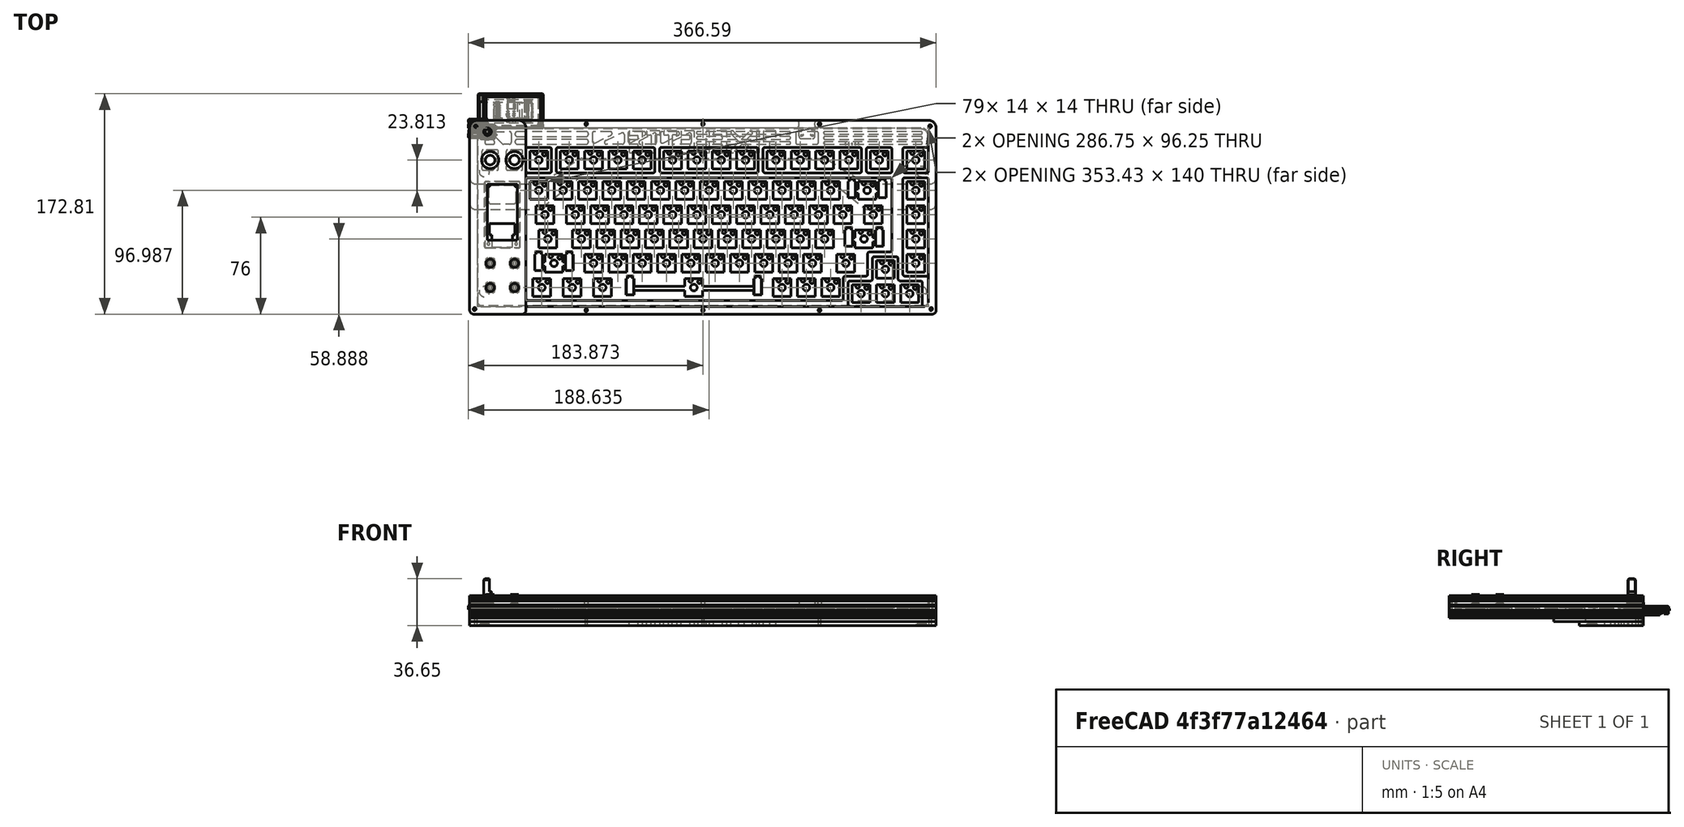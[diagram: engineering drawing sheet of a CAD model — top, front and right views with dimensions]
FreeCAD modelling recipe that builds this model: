
FCSTD DOCUMENT  (FreeCAD 0.20R29177 +426 (Git))
Label: Case design
License: All rights reserved
LicenseURL: http://en.wikipedia.org/wiki/All_rights_reserved
objects: App::Part×101, Part::Feature×100, Sketcher::SketchObject×84, PartDesign::Pocket×64, PartDesign::Pad×17, PartDesign::Body×17, TechDraw::DrawViewPart×13, TechDraw::DrawSVGTemplate×6, TechDraw::DrawPage×6, TechDraw::DrawViewDimension×4, App::DocumentObjectGroup×2, Spreadsheet::Sheet×1, PartDesign::Fillet×1
note: 365 computed .brp shape members not serialized (recipe doc carries the construction recipe); baked Part::Feature solids carry a one-line shape summary decoded from their .brp

FEATURE [Sketcher::SketchObject] Sketch
  AttachmentOffset = pos=(0,0,4.1) rot=(0,0,1;0rad)
  FullyConstrained = true
  MapMode = 5
  Placement = pos=(0,0,4.1) rot=(0,0,1;0rad)
  Support = -> [XY_Plane097]
  expr: .AttachmentOffset.Base.z = 4.1
  expr: Constraints[10] = Spreadsheet.switch_hole
  expr: Constraints[11] = Spreadsheet.PCB_width - Spreadsheet.u * 6
  expr: Constraints[12] = Spreadsheet.u * 2.5
  expr: Constraints[139] = Spreadsheet.switch_hole
  expr: Constraints[140] = Spreadsheet.switch_hole
  expr: Constraints[141] = Spreadsheet.switch_hole
  expr: Constraints[142] = Spreadsheet.switch_hole
  expr: Constraints[143] = Spreadsheet.switch_hole
  expr: Constraints[144] = Spreadsheet.switch_hole
  expr: Constraints[145] = Spreadsheet.switch_hole
  expr: Constraints[146] = Spreadsheet.switch_hole
  expr: Constraints[147] = Spreadsheet.switch_hole
  expr: Constraints[148] = Spreadsheet.switch_hole
  expr: Constraints[149] = Spreadsheet.switch_hole
  expr: Constraints[150] = Spreadsheet.switch_hole
  expr: Constraints[151] = Spreadsheet.switch_hole
  expr: Constraints[152] = Spreadsheet.switch_hole
  expr: Constraints[153] = Spreadsheet.switch_hole
  expr: Constraints[154] = Spreadsheet.switch_hole
  expr: Constraints[155] = Spreadsheet.switch_hole
  expr: Constraints[156] = Spreadsheet.switch_hole
  expr: Constraints[157] = Spreadsheet.switch_hole
  expr: Constraints[158] = Spreadsheet.switch_hole
  expr: Constraints[159] = Spreadsheet.switch_hole
  expr: Constraints[160] = Spreadsheet.switch_hole
  expr: Constraints[161] = Spreadsheet.switch_hole
  expr: Constraints[162] = Spreadsheet.switch_hole
  expr: Constraints[163] = Spreadsheet.switch_hole
  expr: Constraints[164] = Spreadsheet.switch_hole
  expr: Constraints[165] = Spreadsheet.switch_hole
  expr: Constraints[166] = Spreadsheet.switch_hole
  expr: Constraints[167] = Spreadsheet.u * 1.25
  expr: Constraints[182] = Spreadsheet.u
  expr: Constraints[183] = Spreadsheet.u
  expr: Constraints[184] = Spreadsheet.u
  expr: Constraints[185] = Spreadsheet.u
  expr: Constraints[186] = Spreadsheet.u
  expr: Constraints[187] = Spreadsheet.u
  expr: Constraints[188] = Spreadsheet.u
  expr: Constraints[189] = Spreadsheet.u
  expr: Constraints[190] = Spreadsheet.u
  expr: Constraints[191] = Spreadsheet.u * 1.25
  expr: Constraints[192] = Spreadsheet.u * 1.25
  expr: Constraints[193] = Spreadsheet.u * 1.25
  expr: Constraints[194] = Spreadsheet.u * 1.5
  expr: Constraints[9] = Spreadsheet.switch_hole
  sketch-geometry (75):
    g0: LineSegment StartX=40.625 StartY=-17.7 StartZ=0 EndX=40.625 EndY=-31.7 EndZ=0
    g1: LineSegment StartX=40.625 StartY=-31.7 StartZ=0 EndX=54.625 EndY=-31.7 EndZ=0
    g2: LineSegment StartX=54.625 StartY=-31.7 StartZ=0 EndX=54.625 EndY=-17.7 EndZ=0
    g3: LineSegment StartX=54.625 StartY=-17.7 StartZ=0 EndX=40.625 EndY=-17.7 EndZ=0
    g4: GeomPoint X=47.625 Y=-24.7 Z=0
    g5: LineSegment StartX=64.4375 StartY=-17.7 StartZ=0 EndX=64.4375 EndY=-31.7 EndZ=0
    g6: LineSegment StartX=64.4375 StartY=-31.7 StartZ=0 EndX=78.4375 EndY=-31.7 EndZ=0
    g7: LineSegment StartX=78.4375 StartY=-31.7 StartZ=0 EndX=78.4375 EndY=-17.7 EndZ=0
    g8: LineSegment StartX=78.4375 StartY=-17.7 StartZ=0 EndX=64.4375 EndY=-17.7 EndZ=0
    g9: GeomPoint X=71.4375 Y=-24.7 Z=0
    g10: LineSegment StartX=83.4875 StartY=-17.7 StartZ=0 EndX=83.4875 EndY=-31.7 EndZ=0
    g11: LineSegment StartX=83.4875 StartY=-31.7 StartZ=0 EndX=97.4875 EndY=-31.7 EndZ=0
    g12: LineSegment StartX=97.4875 StartY=-31.7 StartZ=0 EndX=97.4875 EndY=-17.7 EndZ=0
    g13: LineSegment StartX=97.4875 StartY=-17.7 StartZ=0 EndX=83.4875 EndY=-17.7 EndZ=0
    g14: GeomPoint X=90.4875 Y=-24.7 Z=0
    g15: LineSegment StartX=102.538 StartY=-17.7 StartZ=0 EndX=102.538 EndY=-31.7 EndZ=0
    g16: LineSegment StartX=102.538 StartY=-31.7 StartZ=0 EndX=116.538 EndY=-31.7 EndZ=0
    g17: LineSegment StartX=116.538 StartY=-31.7 StartZ=0 EndX=116.538 EndY=-17.7 EndZ=0
    g18: LineSegment StartX=116.538 StartY=-17.7 StartZ=0 EndX=102.538 EndY=-17.7 EndZ=0
    g19: GeomPoint X=109.538 Y=-24.7 Z=0
    g20: LineSegment StartX=121.588 StartY=-17.7 StartZ=0 EndX=121.588 EndY=-31.7 EndZ=0
    g21: LineSegment StartX=121.588 StartY=-31.7 StartZ=0 EndX=135.588 EndY=-31.7 EndZ=0
    g22: LineSegment StartX=135.588 StartY=-31.7 StartZ=0 EndX=135.588 EndY=-17.7 EndZ=0
    g23: LineSegment StartX=135.588 StartY=-17.7 StartZ=0 EndX=121.588 EndY=-17.7 EndZ=0
    g24: GeomPoint X=128.588 Y=-24.7 Z=0
    g25: LineSegment StartX=145.4 StartY=-17.7 StartZ=0 EndX=145.4 EndY=-31.7 EndZ=0
    g26: LineSegment StartX=145.4 StartY=-31.7 StartZ=0 EndX=159.4 EndY=-31.7 EndZ=0
    g27: LineSegment StartX=159.4 StartY=-31.7 StartZ=0 EndX=159.4 EndY=-17.7 EndZ=0
    g28: LineSegment StartX=159.4 StartY=-17.7 StartZ=0 EndX=145.4 EndY=-17.7 EndZ=0
    g29: GeomPoint X=152.4 Y=-24.7 Z=0
    g30: LineSegment StartX=164.45 StartY=-17.7 StartZ=0 EndX=164.45 EndY=-31.7 EndZ=0
    g31: LineSegment StartX=164.45 StartY=-31.7 StartZ=0 EndX=178.45 EndY=-31.7 EndZ=0
    g32: LineSegment StartX=178.45 StartY=-31.7 StartZ=0 EndX=178.45 EndY=-17.7 EndZ=0
    g33: LineSegment StartX=178.45 StartY=-17.7 StartZ=0 EndX=164.45 EndY=-17.7 EndZ=0
    g34: GeomPoint X=171.45 Y=-24.7 Z=0
    g35: LineSegment StartX=183.5 StartY=-17.7 StartZ=0 EndX=183.5 EndY=-31.7 EndZ=0
    g36: LineSegment StartX=183.5 StartY=-31.7 StartZ=0 EndX=197.5 EndY=-31.7 EndZ=0
    g37: LineSegment StartX=197.5 StartY=-31.7 StartZ=0 EndX=197.5 EndY=-17.7 EndZ=0
    g38: LineSegment StartX=197.5 StartY=-17.7 StartZ=0 EndX=183.5 EndY=-17.7 EndZ=0
    g39: GeomPoint X=190.5 Y=-24.7 Z=0
    g40: LineSegment StartX=202.55 StartY=-17.7 StartZ=0 EndX=202.55 EndY=-31.7 EndZ=0
    g41: LineSegment StartX=202.55 StartY=-31.7 StartZ=0 EndX=216.55 EndY=-31.7 EndZ=0
    g42: LineSegment StartX=216.55 StartY=-31.7 StartZ=0 EndX=216.55 EndY=-17.7 EndZ=0
    g43: LineSegment StartX=216.55 StartY=-17.7 StartZ=0 EndX=202.55 EndY=-17.7 EndZ=0
    g44: GeomPoint X=209.55 Y=-24.7 Z=0
    g45: LineSegment StartX=226.362 StartY=-17.7 StartZ=0 EndX=226.362 EndY=-31.7 EndZ=0
    g46: LineSegment StartX=226.362 StartY=-31.7 StartZ=0 EndX=240.362 EndY=-31.7 EndZ=0
    g47: LineSegment StartX=240.362 StartY=-31.7 StartZ=0 EndX=240.362 EndY=-17.7 EndZ=0
    g48: LineSegment StartX=240.362 StartY=-17.7 StartZ=0 EndX=226.362 EndY=-17.7 EndZ=0
    g49: GeomPoint X=233.363 Y=-24.7 Z=0
    g50: LineSegment StartX=245.412 StartY=-17.7 StartZ=0 EndX=245.412 EndY=-31.7 EndZ=0
    g51: LineSegment StartX=245.412 StartY=-31.7 StartZ=0 EndX=259.413 EndY=-31.7 EndZ=0
    g52: LineSegment StartX=259.413 StartY=-31.7 StartZ=0 EndX=259.413 EndY=-17.7 EndZ=0
    g53: LineSegment StartX=259.413 StartY=-17.7 StartZ=0 EndX=245.412 EndY=-17.7 EndZ=0
    g54: GeomPoint X=252.412 Y=-24.7 Z=0
    g55: LineSegment StartX=264.463 StartY=-17.7 StartZ=0 EndX=264.463 EndY=-31.7 EndZ=0
    g56: LineSegment StartX=264.463 StartY=-31.7 StartZ=0 EndX=278.463 EndY=-31.7 EndZ=0
    g57: LineSegment StartX=278.463 StartY=-31.7 StartZ=0 EndX=278.463 EndY=-17.7 EndZ=0
    g58: LineSegment StartX=278.463 StartY=-17.7 StartZ=0 EndX=264.463 EndY=-17.7 EndZ=0
    g59: GeomPoint X=271.462 Y=-24.7 Z=0
    g60: LineSegment StartX=283.513 StartY=-17.7 StartZ=0 EndX=283.513 EndY=-31.7 EndZ=0
    g61: LineSegment StartX=283.513 StartY=-31.7 StartZ=0 EndX=297.513 EndY=-31.7 EndZ=0
    g62: LineSegment StartX=297.513 StartY=-31.7 StartZ=0 EndX=297.513 EndY=-17.7 EndZ=0
    g63: LineSegment StartX=297.513 StartY=-17.7 StartZ=0 EndX=283.513 EndY=-17.7 EndZ=0
    g64: GeomPoint X=290.512 Y=-24.7 Z=0
    g65: LineSegment StartX=307.325 StartY=-17.7 StartZ=0 EndX=307.325 EndY=-31.7 EndZ=0
    g66: LineSegment StartX=307.325 StartY=-31.7 StartZ=0 EndX=321.325 EndY=-31.7 EndZ=0
    g67: LineSegment StartX=321.325 StartY=-31.7 StartZ=0 EndX=321.325 EndY=-17.7 EndZ=0
    g68: LineSegment StartX=321.325 StartY=-17.7 StartZ=0 EndX=307.325 EndY=-17.7 EndZ=0
    g69: GeomPoint X=314.325 Y=-24.7 Z=0
    g70: LineSegment StartX=335.9 StartY=-17.7 StartZ=0 EndX=335.9 EndY=-31.7 EndZ=0
    g71: LineSegment StartX=335.9 StartY=-31.7 StartZ=0 EndX=349.9 EndY=-31.7 EndZ=0
    g72: LineSegment StartX=349.9 StartY=-31.7 StartZ=0 EndX=349.9 EndY=-17.7 EndZ=0
    g73: LineSegment StartX=349.9 StartY=-17.7 StartZ=0 EndX=335.9 EndY=-17.7 EndZ=0
    g74: GeomPoint X=342.9 Y=-24.7 Z=0
  constraints (195):
    c: Coincident(g0,g1)
    c: Coincident(g1,g2)
    c: Coincident(g2,g3)
    c: Coincident(g3,g0)
    c: Horizontal(g1)
    c: Horizontal(g3)
    c: Vertical(g0)
    c: Vertical(g2)
    c: Symmetric(g1,g0,g4)
    c: DistanceX(g3,g3) = 14
    c: DistanceY(g2,g2) = 14
    c: DistanceY(g4,g-1) = 24.7
    c: DistanceX(g-1,g4) = 47.625
    c: Coincident(g5,g6)
    c: Coincident(g6,g7)
    c: Coincident(g7,g8)
    c: Coincident(g8,g5)
    c: Horizontal(g6)
    c: Horizontal(g8)
    c: Vertical(g5)
    c: Vertical(g7)
    c: Symmetric(g6,g5,g9)
    c: Coincident(g10,g11)
    c: Coincident(g11,g12)
    c: Coincident(g12,g13)
    c: Coincident(g13,g10)
    c: Horizontal(g11)
    c: Horizontal(g13)
    c: Vertical(g10)
    c: Vertical(g12)
    c: Symmetric(g11,g10,g14)
    c: Coincident(g15,g16)
    c: Coincident(g16,g17)
    c: Coincident(g17,g18)
    c: Coincident(g18,g15)
    c: Horizontal(g16)
    c: Horizontal(g18)
    c: Vertical(g15)
    c: Vertical(g17)
    c: Symmetric(g16,g15,g19)
    c: Coincident(g20,g21)
    c: Coincident(g21,g22)
    c: Coincident(g22,g23)
    c: Coincident(g23,g20)
    c: Horizontal(g21)
    c: Horizontal(g23)
    c: Vertical(g20)
    c: Vertical(g22)
    c: Symmetric(g21,g20,g24)
    c: Coincident(g25,g26)
    c: Coincident(g26,g27)
    c: Coincident(g27,g28)
    c: Coincident(g28,g25)
    c: Horizontal(g26)
    c: Horizontal(g28)
    c: Vertical(g25)
    c: Vertical(g27)
    c: Symmetric(g26,g25,g29)
    c: Coincident(g30,g31)
    c: Coincident(g31,g32)
    c: Coincident(g32,g33)
    c: Coincident(g33,g30)
    c: Horizontal(g31)
    c: Horizontal(g33)
    c: Vertical(g30)
    c: Vertical(g32)
    c: Symmetric(g31,g30,g34)
    c: Coincident(g35,g36)
    c: Coincident(g36,g37)
    c: Coincident(g37,g38)
    c: Coincident(g38,g35)
    c: Horizontal(g36)
    c: Horizontal(g38)
    c: Vertical(g35)
    c: Vertical(g37)
    c: Symmetric(g36,g35,g39)
    c: Coincident(g40,g41)
    c: Coincident(g41,g42)
    c: Coincident(g42,g43)
    c: Coincident(g43,g40)
    c: Horizontal(g41)
    c: Horizontal(g43)
    c: Vertical(g40)
    c: Vertical(g42)
    c: Symmetric(g41,g40,g44)
    c: Coincident(g45,g46)
    c: Coincident(g46,g47)
    c: Coincident(g47,g48)
    c: Coincident(g48,g45)
    c: Horizontal(g46)
    c: Horizontal(g48)
    c: Vertical(g45)
    c: Vertical(g47)
    c: Symmetric(g46,g45,g49)
    c: Coincident(g50,g51)
    c: Coincident(g51,g52)
    c: Coincident(g52,g53)
    c: Coincident(g53,g50)
    c: Horizontal(g51)
    c: Horizontal(g53)
    c: Vertical(g50)
    c: Vertical(g52)
    c: Symmetric(g51,g50,g54)
    c: Coincident(g55,g56)
    c: Coincident(g56,g57)
    c: Coincident(g57,g58)
    c: Coincident(g58,g55)
    c: Horizontal(g56)
    c: Horizontal(g58)
    c: Vertical(g55)
    c: Vertical(g57)
    c: Symmetric(g56,g55,g59)
    c: Coincident(g60,g61)
    c: Coincident(g61,g62)
    c: Coincident(g62,g63)
    c: Coincident(g63,g60)
    c: Horizontal(g61)
    c: Horizontal(g63)
    c: Vertical(g60)
    c: Vertical(g62)
    c: Symmetric(g61,g60,g64)
    c: Coincident(g65,g66)
    c: Coincident(g66,g67)
    c: Coincident(g67,g68)
    c: Coincident(g68,g65)
    c: Horizontal(g66)
    c: Horizontal(g68)
    c: Vertical(g65)
    c: Vertical(g67)
    c: Symmetric(g66,g65,g69)
    c: Coincident(g70,g71)
    c: Coincident(g71,g72)
    c: Coincident(g72,g73)
    c: Coincident(g73,g70)
    c: Horizontal(g71)
    c: Horizontal(g73)
    c: Vertical(g70)
    c: Vertical(g72)
    c: Symmetric(g71,g70,g74)
    c: DistanceX(g8,g8) = 14
    c: DistanceX(g13,g13) = 14
    c: DistanceX(g18,g18) = 14
    c: DistanceX(g23,g23) = 14
    c: DistanceX(g28,g28) = 14
    c: DistanceX(g33,g33) = 14
    c: DistanceX(g38,g38) = 14
    c: DistanceX(g43,g43) = 14
    c: DistanceX(g48,g48) = 14
    c: DistanceX(g53,g53) = 14
    c: DistanceX(g58,g58) = 14
    c: DistanceX(g63,g63) = 14
    c: DistanceX(g68,g68) = 14
    c: DistanceX(g73,g73) = 14
    c: DistanceY(g7,g7) = 14
    c: DistanceY(g12,g12) = 14
    c: DistanceY(g17,g17) = 14
    c: DistanceY(g22,g22) = 14
    c: DistanceY(g27,g27) = 14
    c: DistanceY(g32,g32) = 14
    c: DistanceY(g37,g37) = 14
    c: DistanceY(g42,g42) = 14
    c: DistanceY(g47,g47) = 14
    c: DistanceY(g52,g52) = 14
    c: DistanceY(g57,g57) = 14
    c: DistanceY(g62,g62) = 14
    c: DistanceY(g67,g67) = 14
    c: DistanceY(g72,g72) = 14
    c: DistanceX(g4,g9) = 23.8125
    c: Horizontal(g4,g9)
    c: Horizontal(g9,g14)
    c: Horizontal(g14,g19)
    c: Horizontal(g19,g24)
    c: Horizontal(g24,g29)
    c: Horizontal(g29,g34)
    c: Horizontal(g34,g39)
    c: Horizontal(g39,g44)
    c: Horizontal(g44,g49)
    c: Horizontal(g49,g54)
    c: Horizontal(g54,g59)
    c: Horizontal(g59,g64)
    c: Horizontal(g64,g69)
    c: Horizontal(g69,g74)
    c: DistanceX(g9,g14) = 19.05
    c: DistanceX(g14,g19) = 19.05
    c: DistanceX(g19,g24) = 19.05
    c: DistanceX(g29,g34) = 19.05
    c: DistanceX(g34,g39) = 19.05
    c: DistanceX(g39,g44) = 19.05
    c: DistanceX(g49,g54) = 19.05
    c: DistanceX(g54,g59) = 19.05
    c: DistanceX(g59,g64) = 19.05
    c: DistanceX(g24,g29) = 23.8125
    c: DistanceX(g44,g49) = 23.8125
    c: DistanceX(g64,g69) = 23.8125
    c: DistanceX(g69,g74) = 28.575
FEATURE [Spreadsheet::Sheet] Spreadsheet
  cells = A2=PCB_length; B2(PCB_length)=352.425; F2=u; G2(u)=19.05; A3=PCB_width; B3(PCB_width)=139; F3=switch_hole; G3(switch_hole)=14; A4=pcb_to_wall_gap; B4(pcb_to_wall_gap)=0.5; F4=encoder_hole_width; G4(encoder_hole_width)=13; A5=wall_thickness; B5(wall_thickness)=6; F5=encoder_hole_length; G5(encoder_hole_length)=16; A6=Spacer_hole; B6(Spacer_hole)=3.1; F6=encoder_fillet_rad; G6(encoder_fillet_rad)=1.25; A7=Screw_hole; B7(Screw_hole)=2.1; F7=screen_module_width; G7(screen_module_width)=27.3; A8=Bottom_c_rad; B8(Bottom_c_rad)=3; F8=screen_module_length; G8(screen_module_length)=51.2; A9=Top_c_rad; B9(Top_c_rad)=6; F9=screen_width; G9(screen_width)=22.7; F10=screen_length; G10(screen_length)=42.72; F11=bot_scr_mod_to_scr; G11(bot_scr_mod_to_scr)=6.25; F12=tact_button_size; G12(tact_button_size)=6; F13=stab_length; G13(stab_length)=12.4; F14=stab_width; G14(stab_width)=5.9; F15=key_fillet; G15(key_fillet)=1.5
FEATURE [Sketcher::SketchObject] Sketch001
  AttachmentOffset = pos=(0,0,2.9) rot=(0,0,1;0rad)
  FullyConstrained = false
  MapMode = 5
  Placement = pos=(0,0,2.9) rot=(0,0,1;0rad)
  Support = -> [XY_Plane097]
  expr: .AttachmentOffset.Base.z = 1.6 + 1.3
  expr: Constraints[25] = Spreadsheet.Bottom_c_rad
  expr: Constraints[26] = Spreadsheet.Bottom_c_rad
  expr: Constraints[29] = Spreadsheet.Spacer_hole + 0.3
  expr: Constraints[32] = Spreadsheet.PCB_length + Spreadsheet.pcb_to_wall_gap * 2
  expr: Constraints[33] = Spreadsheet.PCB_width + Spreadsheet.pcb_to_wall_gap * 2
  expr: Constraints[35] = 2 * Spreadsheet.Top_c_rad * sin(45 / 2)
  expr: Constraints[37] = Spreadsheet.Spacer_hole + 0.3
  expr: Constraints[39] = 2 * Spreadsheet.Top_c_rad * sin(45 / 2)
  expr: Constraints[43] = Spreadsheet.Spacer_hole + 0.3
  expr: Constraints[44] = Spreadsheet.wall_thickness / 2
  expr: Constraints[45] = Spreadsheet.PCB_length / 2
  expr: Constraints[46] = (Spreadsheet.PCB_length + Spreadsheet.pcb_to_wall_gap * 2 + Spreadsheet.wall_thickness * 2) / 4
  expr: Constraints[47] = (Spreadsheet.PCB_length + Spreadsheet.pcb_to_wall_gap * 2 + Spreadsheet.wall_thickness * 2) / 4
  expr: Constraints[49] = 2 * Spreadsheet.Bottom_c_rad * sin(45 / 2)
  expr: Constraints[51] = 2 * Spreadsheet.Bottom_c_rad * sin(45 / 2)
  expr: Constraints[53] = Spreadsheet.Spacer_hole + 0.3
  expr: Constraints[54] = Spreadsheet.Spacer_hole + 0.3
  expr: Constraints[5] = Spreadsheet.PCB_length / 2
  expr: Constraints[61] = Spreadsheet.PCB_length
  expr: Constraints[62] = Spreadsheet.PCB_width
  expr: Constraints[65] = Spreadsheet.PCB_length + 2 * Spreadsheet.pcb_to_wall_gap
  expr: Constraints[66] = Spreadsheet.PCB_width + 2 * Spreadsheet.pcb_to_wall_gap
  expr: Constraints[6] = Spreadsheet.PCB_width / 2
  expr: Constraints[74] = Spreadsheet.wall_thickness / 2
  expr: Constraints[7] = Spreadsheet.PCB_width + 2 * Spreadsheet.pcb_to_wall_gap + 2 * Spreadsheet.wall_thickness
  expr: Constraints[8] = Spreadsheet.PCB_length + 2 * Spreadsheet.pcb_to_wall_gap + 2 * Spreadsheet.wall_thickness
  sketch-geometry (46):
    g0: LineSegment StartX=-6.5 StartY=0.5 StartZ=0 EndX=-6.5 EndY=-142.5 EndZ=0
    g1: LineSegment StartX=-3.5 StartY=-145.5 StartZ=0 EndX=355.925 EndY=-145.5 EndZ=0
    g2: LineSegment StartX=358.925 StartY=-142.5 StartZ=0 EndX=358.925 EndY=0.5 EndZ=0
    g3: LineSegment StartX=352.925 StartY=6.5 StartZ=0 EndX=-0.5 EndY=6.5 EndZ=0
    g4: GeomPoint X=176.213 Y=-69.5 Z=0
    g5: ArcOfCircle CenterX=-0.5 CenterY=0.5 CenterZ=0 NormalX=0 NormalY=0 NormalZ=1 AngleXU=0 Radius=6 StartAngle=1.5708 EndAngle=3.14159
    g6: GeomPoint X=-6.5 Y=6.5 Z=0
    g7: ArcOfCircle CenterX=352.925 CenterY=0.5 CenterZ=0 NormalX=0 NormalY=0 NormalZ=1 AngleXU=0 Radius=6 StartAngle=0 EndAngle=1.5708
    g8: GeomPoint X=358.925 Y=6.5 Z=0
    g9: ArcOfCircle CenterX=-3.5 CenterY=-142.5 CenterZ=0 NormalX=0 NormalY=0 NormalZ=1 AngleXU=0 Radius=3 StartAngle=3.14159 EndAngle=4.71239
    g10: GeomPoint X=-6.5 Y=-145.5 Z=0
    g11: ArcOfCircle CenterX=355.925 CenterY=-142.5 CenterZ=0 NormalX=0 NormalY=0 NormalZ=1 AngleXU=0 Radius=3 StartAngle=4.71239 EndAngle=6.28319
    g12: GeomPoint X=358.925 Y=-145.5 Z=0
    g13: Circle CenterX=-1.74263 CenterY=1.74264 CenterZ=0 NormalX=0 NormalY=0 NormalZ=1 AngleXU=0 Radius=1.7
    g14: GeomPoint X=176.213 Y=-69.5 Z=0
    g15: GeomPoint X=-0.472801 Y=1.29801 Z=0
    g16: GeomPoint X=352.952 Y=1.5 Z=0
    g17: GeomPoint X=352.898 Y=-140.298 Z=0
    g18: GeomPoint X=-1.5 Y=-138.702 Z=0
    g19: GeomPoint X=-4.74264 Y=4.74264 Z=0
    g20: GeomPoint X=1.25738 Y=-1.25737 Z=0
    g21: Circle CenterX=354.168 CenterY=1.74264 CenterZ=0 NormalX=0 NormalY=0 NormalZ=1 AngleXU=0 Radius=1.7
    g22: GeomPoint X=351.168 Y=-1.25737 Z=0
    g23: GeomPoint X=357.168 Y=4.74264 Z=0
    g24: Circle CenterX=84.8563 CenterY=3.5 CenterZ=0 NormalX=0 NormalY=0 NormalZ=1 AngleXU=0 Radius=1.7
    g25: Circle CenterX=176.213 CenterY=3.5 CenterZ=0 NormalX=0 NormalY=0 NormalZ=1 AngleXU=0 Radius=1.7
    g26: Circle CenterX=267.569 CenterY=3.5 CenterZ=0 NormalX=0 NormalY=0 NormalZ=1 AngleXU=0 Radius=1.7
    g27: Circle CenterX=-2.62131 CenterY=-141.621 CenterZ=0 NormalX=0 NormalY=0 NormalZ=1 AngleXU=0 Radius=1.7
    g28: GeomPoint X=0.378703 Y=-138.621 Z=0
    g29: GeomPoint X=-5.62132 Y=-144.621 Z=0
    g30: GeomPoint X=352.046 Y=-138.621 Z=0
    g31: GeomPoint X=358.046 Y=-144.621 Z=0
    g32: Circle CenterX=355.046 CenterY=-141.621 CenterZ=0 NormalX=0 NormalY=0 NormalZ=1 AngleXU=0 Radius=1.7
    g33: GeomPoint X=176.213 Y=-69.5 Z=0
    g34: GeomPoint X=-0.472801 Y=1.29801 Z=0
    g35: GeomPoint X=7.7e-15 Y=-137.702 Z=0
    g36: GeomPoint X=352.898 Y=-140.298 Z=0
    g37: GeomPoint X=351.952 Y=-3e-15 Z=0
    g38: GeomPoint X=176.213 Y=-69.5 Z=0
    g39: GeomPoint X=-0.850325 Y=1.71354 Z=0
    g40: GeomPoint X=352.925 Y=-0.713539 Z=0
    g41: GeomPoint X=-0.149675 Y=-139.5 Z=0
    g42: GeomPoint X=353.275 Y=-140.714 Z=0
    g43: Circle CenterX=84.8563 CenterY=-142.5 CenterZ=0 NormalX=0 NormalY=0 NormalZ=1 AngleXU=0 Radius=1.7
    g44: Circle CenterX=176.213 CenterY=-142.5 CenterZ=0 NormalX=0 NormalY=0 NormalZ=1 AngleXU=0 Radius=1.7
    g45: Circle CenterX=267.569 CenterY=-142.5 CenterZ=0 NormalX=0 NormalY=0 NormalZ=1 AngleXU=0 Radius=1.7
  constraints (76):
    c: Horizontal(g1)
    c: Horizontal(g3)
    c: Vertical(g0)
    c: Vertical(g2)
    c: Symmetric(g12,g6,g4)
    c: DistanceX(g-1,g4) = 176.213
    c: DistanceY(g4,g-1) = 69.5
    c: DistanceY(g10,g6) = 152
    c: DistanceX(g6,g8) = 365.425
    c: PointOnObject(g6,g0)
    c: PointOnObject(g6,g3)
    c: Tangent(g0,g5) = -1.5708
    c: Tangent(g3,g5) = -1.5708
    c: PointOnObject(g8,g2)
    c: PointOnObject(g8,g3)
    c: Tangent(g2,g7) = -1.5708
    c: Tangent(g3,g7) = -1.5708
    c: PointOnObject(g10,g0)
    c: PointOnObject(g10,g1)
    c: Tangent(g0,g9) = -1.5708
    c: Tangent(g1,g9) = -1.5708
    c: PointOnObject(g12,g1)
    c: PointOnObject(g12,g2)
    c: Tangent(g1,g11) = -1.5708
    c: Tangent(g2,g11) = -1.5708
    c: Radius(g11) = 3
    c: Radius(g9) = 3
    c: Radius(g5) = 6
    c: Radius(g7) = 6
    c: Diameter(g13) = 3.4
    c: Symmetric(g17,g15,g14)
    c: Coincident(g14,g4)
    c: DistanceX(g15,g16) = 353.425
    c: DistanceY(g18,g15) = 140
    c: PointOnObject(g19,g5)
    c: Distance(g0,g19) = 4.5922
    c: Symmetric(g19,g20,g13)
    c: Diameter(g21) = 3.4
    c: PointOnObject(g23,g7)
    c: Distance(g2,g23) = 4.5922
    c: Symmetric(g22,g23,g21)
    c: Equal(g24,g25)
    c: Equal(g26,g25)
    c: Diameter(g25) = 3.4
    c: Distance(g25,g3) = 3
    c: DistanceX(g-1,g25) = 176.213
    c: DistanceX(g24,g25) = 91.3563
    c: DistanceX(g25,g26) = 91.3563
    c: PointOnObject(g29,g9)
    c: Distance(g0,g29) = 2.2961
    c: PointOnObject(g31,g11)
    c: Distance(g1,g31) = 2.2961
    c: Symmetric(g30,g31,g32)
    c: Diameter(g32) = 3.4
    c: Diameter(g27) = 3.4
    c: Symmetric(g29,g28,g27)
    c: Horizontal(g24,g25)
    c: Horizontal(g26,g25)
    c: Symmetric(g36,g34,g33)
    c: Coincident(g33,g4)
    c: Coincident(g36,g17)
    c: DistanceX(g34,g37) = 352.425
    c: DistanceY(g35,g34) = 139
    c: Symmetric(g42,g39,g38)
    c: Coincident(g38,g4)
    c: DistanceX(g41,g42) = 353.425
    c: DistanceY(g42,g40) = 140
    c: Equal(g43,g44)
    c: Equal(g45,g44)
    c: Equal(g25,g44) = 3.1
    c: DistanceX(g43,g44) = 91.3563
    c: DistanceX(g44,g45) = 91.3563
    c: Horizontal(g43,g44)
    c: Horizontal(g45,g44)
    c: Distance(g44,g1) = 3
    c: Vertical(g44,g25)
FEATURE [PartDesign::Pad] Pad
  Direction = (0,0,1)
  Length = 1.2
  Length2 = 10
  Profile = -> Sketch001
  ReferenceAxis = -> Sketch001 [N_Axis]
  Type = 0
FEATURE [Sketcher::SketchObject] Sketch002
  AttachmentOffset = pos=(0,0,4.1) rot=(0,0,1;0rad)
  FullyConstrained = true
  MapMode = 5
  Placement = pos=(0,0,4.1) rot=(0,0,1;0rad)
  Support = -> [XY_Plane097]
  expr: Constraints[10] = Spreadsheet.switch_hole
  expr: Constraints[11] = Spreadsheet.PCB_width - Spreadsheet.u * 4.75
  expr: Constraints[12] = Spreadsheet.u * 2.5
  expr: Constraints[139] = Spreadsheet.switch_hole
  expr: Constraints[140] = Spreadsheet.switch_hole
  expr: Constraints[141] = Spreadsheet.switch_hole
  expr: Constraints[142] = Spreadsheet.switch_hole
  expr: Constraints[143] = Spreadsheet.switch_hole
  expr: Constraints[144] = Spreadsheet.switch_hole
  expr: Constraints[145] = Spreadsheet.switch_hole
  expr: Constraints[146] = Spreadsheet.switch_hole
  expr: Constraints[147] = Spreadsheet.switch_hole
  expr: Constraints[148] = Spreadsheet.switch_hole
  expr: Constraints[149] = Spreadsheet.switch_hole
  expr: Constraints[150] = Spreadsheet.switch_hole
  expr: Constraints[151] = Spreadsheet.switch_hole
  expr: Constraints[152] = Spreadsheet.switch_hole
  expr: Constraints[153] = Spreadsheet.switch_hole
  expr: Constraints[154] = Spreadsheet.switch_hole
  expr: Constraints[155] = Spreadsheet.switch_hole
  expr: Constraints[156] = Spreadsheet.switch_hole
  expr: Constraints[157] = Spreadsheet.switch_hole
  expr: Constraints[158] = Spreadsheet.switch_hole
  expr: Constraints[159] = Spreadsheet.switch_hole
  expr: Constraints[160] = Spreadsheet.switch_hole
  expr: Constraints[161] = Spreadsheet.switch_hole
  expr: Constraints[162] = Spreadsheet.switch_hole
  expr: Constraints[163] = Spreadsheet.switch_hole
  expr: Constraints[164] = Spreadsheet.switch_hole
  expr: Constraints[165] = Spreadsheet.switch_hole
  expr: Constraints[166] = Spreadsheet.switch_hole
  expr: Constraints[167] = Spreadsheet.u
  expr: Constraints[182] = Spreadsheet.u
  expr: Constraints[183] = Spreadsheet.u
  expr: Constraints[184] = Spreadsheet.u
  expr: Constraints[185] = Spreadsheet.u
  expr: Constraints[186] = Spreadsheet.u
  expr: Constraints[187] = Spreadsheet.u
  expr: Constraints[188] = Spreadsheet.u
  expr: Constraints[189] = Spreadsheet.u
  expr: Constraints[190] = Spreadsheet.u
  expr: Constraints[191] = Spreadsheet.u
  expr: Constraints[192] = Spreadsheet.u
  expr: Constraints[193] = Spreadsheet.u * 1.5
  expr: Constraints[194] = Spreadsheet.u * 2
  expr: Constraints[9] = Spreadsheet.switch_hole
  sketch-geometry (75):
    g0: LineSegment StartX=40.625 StartY=-41.5125 StartZ=0 EndX=40.625 EndY=-55.5125 EndZ=0
    g1: LineSegment StartX=40.625 StartY=-55.5125 StartZ=0 EndX=54.625 EndY=-55.5125 EndZ=0
    g2: LineSegment StartX=54.625 StartY=-55.5125 StartZ=0 EndX=54.625 EndY=-41.5125 EndZ=0
    g3: LineSegment StartX=54.625 StartY=-41.5125 StartZ=0 EndX=40.625 EndY=-41.5125 EndZ=0
    g4: GeomPoint X=47.625 Y=-48.5125 Z=0
    g5: LineSegment StartX=59.675 StartY=-41.5125 StartZ=0 EndX=59.675 EndY=-55.5125 EndZ=0
    g6: LineSegment StartX=59.675 StartY=-55.5125 StartZ=0 EndX=73.675 EndY=-55.5125 EndZ=0
    g7: LineSegment StartX=73.675 StartY=-55.5125 StartZ=0 EndX=73.675 EndY=-41.5125 EndZ=0
    g8: LineSegment StartX=73.675 StartY=-41.5125 StartZ=0 EndX=59.675 EndY=-41.5125 EndZ=0
    g9: GeomPoint X=66.675 Y=-48.5125 Z=0
    g10: LineSegment StartX=78.725 StartY=-41.5125 StartZ=0 EndX=78.725 EndY=-55.5125 EndZ=0
    g11: LineSegment StartX=78.725 StartY=-55.5125 StartZ=0 EndX=92.725 EndY=-55.5125 EndZ=0
    g12: LineSegment StartX=92.725 StartY=-55.5125 StartZ=0 EndX=92.725 EndY=-41.5125 EndZ=0
    g13: LineSegment StartX=92.725 StartY=-41.5125 StartZ=0 EndX=78.725 EndY=-41.5125 EndZ=0
    g14: GeomPoint X=85.725 Y=-48.5125 Z=0
    g15: LineSegment StartX=97.775 StartY=-41.5125 StartZ=0 EndX=97.775 EndY=-55.5125 EndZ=0
    g16: LineSegment StartX=97.775 StartY=-55.5125 StartZ=0 EndX=111.775 EndY=-55.5125 EndZ=0
    g17: LineSegment StartX=111.775 StartY=-55.5125 StartZ=0 EndX=111.775 EndY=-41.5125 EndZ=0
    g18: LineSegment StartX=111.775 StartY=-41.5125 StartZ=0 EndX=97.775 EndY=-41.5125 EndZ=0
    g19: GeomPoint X=104.775 Y=-48.5125 Z=0
    g20: LineSegment StartX=116.825 StartY=-41.5125 StartZ=0 EndX=116.825 EndY=-55.5125 EndZ=0
    g21: LineSegment StartX=116.825 StartY=-55.5125 StartZ=0 EndX=130.825 EndY=-55.5125 EndZ=0
    g22: LineSegment StartX=130.825 StartY=-55.5125 StartZ=0 EndX=130.825 EndY=-41.5125 EndZ=0
    g23: LineSegment StartX=130.825 StartY=-41.5125 StartZ=0 EndX=116.825 EndY=-41.5125 EndZ=0
    g24: GeomPoint X=123.825 Y=-48.5125 Z=0
    g25: LineSegment StartX=135.875 StartY=-41.5125 StartZ=0 EndX=135.875 EndY=-55.5125 EndZ=0
    g26: LineSegment StartX=135.875 StartY=-55.5125 StartZ=0 EndX=149.875 EndY=-55.5125 EndZ=0
    g27: LineSegment StartX=149.875 StartY=-55.5125 StartZ=0 EndX=149.875 EndY=-41.5125 EndZ=0
    g28: LineSegment StartX=149.875 StartY=-41.5125 StartZ=0 EndX=135.875 EndY=-41.5125 EndZ=0
    g29: GeomPoint X=142.875 Y=-48.5125 Z=0
    g30: LineSegment StartX=154.925 StartY=-41.5125 StartZ=0 EndX=154.925 EndY=-55.5125 EndZ=0
    g31: LineSegment StartX=154.925 StartY=-55.5125 StartZ=0 EndX=168.925 EndY=-55.5125 EndZ=0
    g32: LineSegment StartX=168.925 StartY=-55.5125 StartZ=0 EndX=168.925 EndY=-41.5125 EndZ=0
    g33: LineSegment StartX=168.925 StartY=-41.5125 StartZ=0 EndX=154.925 EndY=-41.5125 EndZ=0
    g34: GeomPoint X=161.925 Y=-48.5125 Z=0
    g35: LineSegment StartX=173.975 StartY=-41.5125 StartZ=0 EndX=173.975 EndY=-55.5125 EndZ=0
    g36: LineSegment StartX=173.975 StartY=-55.5125 StartZ=0 EndX=187.975 EndY=-55.5125 EndZ=0
    g37: LineSegment StartX=187.975 StartY=-55.5125 StartZ=0 EndX=187.975 EndY=-41.5125 EndZ=0
    g38: LineSegment StartX=187.975 StartY=-41.5125 StartZ=0 EndX=173.975 EndY=-41.5125 EndZ=0
    g39: GeomPoint X=180.975 Y=-48.5125 Z=0
    g40: LineSegment StartX=193.025 StartY=-41.5125 StartZ=0 EndX=193.025 EndY=-55.5125 EndZ=0
    g41: LineSegment StartX=193.025 StartY=-55.5125 StartZ=0 EndX=207.025 EndY=-55.5125 EndZ=0
    g42: LineSegment StartX=207.025 StartY=-55.5125 StartZ=0 EndX=207.025 EndY=-41.5125 EndZ=0
    g43: LineSegment StartX=207.025 StartY=-41.5125 StartZ=0 EndX=193.025 EndY=-41.5125 EndZ=0
    g44: GeomPoint X=200.025 Y=-48.5125 Z=0
    g45: LineSegment StartX=212.075 StartY=-41.5125 StartZ=0 EndX=212.075 EndY=-55.5125 EndZ=0
    g46: LineSegment StartX=212.075 StartY=-55.5125 StartZ=0 EndX=226.075 EndY=-55.5125 EndZ=0
    g47: LineSegment StartX=226.075 StartY=-55.5125 StartZ=0 EndX=226.075 EndY=-41.5125 EndZ=0
    g48: LineSegment StartX=226.075 StartY=-41.5125 StartZ=0 EndX=212.075 EndY=-41.5125 EndZ=0
    g49: GeomPoint X=219.075 Y=-48.5125 Z=0
    g50: LineSegment StartX=231.125 StartY=-41.5125 StartZ=0 EndX=231.125 EndY=-55.5125 EndZ=0
    g51: LineSegment StartX=231.125 StartY=-55.5125 StartZ=0 EndX=245.125 EndY=-55.5125 EndZ=0
    g52: LineSegment StartX=245.125 StartY=-55.5125 StartZ=0 EndX=245.125 EndY=-41.5125 EndZ=0
    g53: LineSegment StartX=245.125 StartY=-41.5125 StartZ=0 EndX=231.125 EndY=-41.5125 EndZ=0
    g54: GeomPoint X=238.125 Y=-48.5125 Z=0
    g55: LineSegment StartX=250.175 StartY=-41.5125 StartZ=0 EndX=250.175 EndY=-55.5125 EndZ=0
    g56: LineSegment StartX=250.175 StartY=-55.5125 StartZ=0 EndX=264.175 EndY=-55.5125 EndZ=0
    g57: LineSegment StartX=264.175 StartY=-55.5125 StartZ=0 EndX=264.175 EndY=-41.5125 EndZ=0
    g58: LineSegment StartX=264.175 StartY=-41.5125 StartZ=0 EndX=250.175 EndY=-41.5125 EndZ=0
    g59: GeomPoint X=257.175 Y=-48.5125 Z=0
    g60: LineSegment StartX=269.225 StartY=-41.5125 StartZ=0 EndX=269.225 EndY=-55.5125 EndZ=0
    g61: LineSegment StartX=269.225 StartY=-55.5125 StartZ=0 EndX=283.225 EndY=-55.5125 EndZ=0
    g62: LineSegment StartX=283.225 StartY=-55.5125 StartZ=0 EndX=283.225 EndY=-41.5125 EndZ=0
    g63: LineSegment StartX=283.225 StartY=-41.5125 StartZ=0 EndX=269.225 EndY=-41.5125 EndZ=0
    g64: GeomPoint X=276.225 Y=-48.5125 Z=0
    g65: LineSegment StartX=297.8 StartY=-41.5125 StartZ=0 EndX=297.8 EndY=-55.5125 EndZ=0
    g66: LineSegment StartX=297.8 StartY=-55.5125 StartZ=0 EndX=311.8 EndY=-55.5125 EndZ=0
    g67: LineSegment StartX=311.8 StartY=-55.5125 StartZ=0 EndX=311.8 EndY=-41.5125 EndZ=0
    g68: LineSegment StartX=311.8 StartY=-41.5125 StartZ=0 EndX=297.8 EndY=-41.5125 EndZ=0
    g69: GeomPoint X=304.8 Y=-48.5125 Z=0
    g70: LineSegment StartX=335.9 StartY=-41.5125 StartZ=0 EndX=335.9 EndY=-55.5125 EndZ=0
    g71: LineSegment StartX=335.9 StartY=-55.5125 StartZ=0 EndX=349.9 EndY=-55.5125 EndZ=0
    g72: LineSegment StartX=349.9 StartY=-55.5125 StartZ=0 EndX=349.9 EndY=-41.5125 EndZ=0
    g73: LineSegment StartX=349.9 StartY=-41.5125 StartZ=0 EndX=335.9 EndY=-41.5125 EndZ=0
    g74: GeomPoint X=342.9 Y=-48.5125 Z=0
  constraints (195):
    c: Coincident(g0,g1)
    c: Coincident(g1,g2)
    c: Coincident(g2,g3)
    c: Coincident(g3,g0)
    c: Horizontal(g1)
    c: Horizontal(g3)
    c: Vertical(g0)
    c: Vertical(g2)
    c: Symmetric(g1,g0,g4)
    c: DistanceX(g3,g3) = 14
    c: DistanceY(g2,g2) = 14
    c: DistanceY(g4,g-1) = 48.5125
    c: DistanceX(g-1,g4) = 47.625
    c: Coincident(g5,g6)
    c: Coincident(g6,g7)
    c: Coincident(g7,g8)
    c: Coincident(g8,g5)
    c: Horizontal(g6)
    c: Horizontal(g8)
    c: Vertical(g5)
    c: Vertical(g7)
    c: Symmetric(g6,g5,g9)
    c: Coincident(g10,g11)
    c: Coincident(g11,g12)
    c: Coincident(g12,g13)
    c: Coincident(g13,g10)
    c: Horizontal(g11)
    c: Horizontal(g13)
    c: Vertical(g10)
    c: Vertical(g12)
    c: Symmetric(g11,g10,g14)
    c: Coincident(g15,g16)
    c: Coincident(g16,g17)
    c: Coincident(g17,g18)
    c: Coincident(g18,g15)
    c: Horizontal(g16)
    c: Horizontal(g18)
    c: Vertical(g15)
    c: Vertical(g17)
    c: Symmetric(g16,g15,g19)
    c: Coincident(g20,g21)
    c: Coincident(g21,g22)
    c: Coincident(g22,g23)
    c: Coincident(g23,g20)
    c: Horizontal(g21)
    c: Horizontal(g23)
    c: Vertical(g20)
    c: Vertical(g22)
    c: Symmetric(g21,g20,g24)
    c: Coincident(g25,g26)
    c: Coincident(g26,g27)
    c: Coincident(g27,g28)
    c: Coincident(g28,g25)
    c: Horizontal(g26)
    c: Horizontal(g28)
    c: Vertical(g25)
    c: Vertical(g27)
    c: Symmetric(g26,g25,g29)
    c: Coincident(g30,g31)
    c: Coincident(g31,g32)
    c: Coincident(g32,g33)
    c: Coincident(g33,g30)
    c: Horizontal(g31)
    c: Horizontal(g33)
    c: Vertical(g30)
    c: Vertical(g32)
    c: Symmetric(g31,g30,g34)
    c: Coincident(g35,g36)
    c: Coincident(g36,g37)
    c: Coincident(g37,g38)
    c: Coincident(g38,g35)
    c: Horizontal(g36)
    c: Horizontal(g38)
    c: Vertical(g35)
    c: Vertical(g37)
    c: Symmetric(g36,g35,g39)
    c: Coincident(g40,g41)
    c: Coincident(g41,g42)
    c: Coincident(g42,g43)
    c: Coincident(g43,g40)
    c: Horizontal(g41)
    c: Horizontal(g43)
    c: Vertical(g40)
    c: Vertical(g42)
    c: Symmetric(g41,g40,g44)
    c: Coincident(g45,g46)
    c: Coincident(g46,g47)
    c: Coincident(g47,g48)
    c: Coincident(g48,g45)
    c: Horizontal(g46)
    c: Horizontal(g48)
    c: Vertical(g45)
    c: Vertical(g47)
    c: Symmetric(g46,g45,g49)
    c: Coincident(g50,g51)
    c: Coincident(g51,g52)
    c: Coincident(g52,g53)
    c: Coincident(g53,g50)
    c: Horizontal(g51)
    c: Horizontal(g53)
    c: Vertical(g50)
    c: Vertical(g52)
    c: Symmetric(g51,g50,g54)
    c: Coincident(g55,g56)
    c: Coincident(g56,g57)
    c: Coincident(g57,g58)
    c: Coincident(g58,g55)
    c: Horizontal(g56)
    c: Horizontal(g58)
    c: Vertical(g55)
    c: Vertical(g57)
    c: Symmetric(g56,g55,g59)
    c: Coincident(g60,g61)
    c: Coincident(g61,g62)
    c: Coincident(g62,g63)
    c: Coincident(g63,g60)
    c: Horizontal(g61)
    c: Horizontal(g63)
    c: Vertical(g60)
    c: Vertical(g62)
    c: Symmetric(g61,g60,g64)
    c: Coincident(g65,g66)
    c: Coincident(g66,g67)
    c: Coincident(g67,g68)
    c: Coincident(g68,g65)
    c: Horizontal(g66)
    c: Horizontal(g68)
    c: Vertical(g65)
    c: Vertical(g67)
    c: Symmetric(g66,g65,g69)
    c: Coincident(g70,g71)
    c: Coincident(g71,g72)
    c: Coincident(g72,g73)
    c: Coincident(g73,g70)
    c: Horizontal(g71)
    c: Horizontal(g73)
    c: Vertical(g70)
    c: Vertical(g72)
    c: Symmetric(g71,g70,g74)
    c: DistanceX(g8,g8) = 14
    c: DistanceX(g13,g13) = 14
    c: DistanceX(g18,g18) = 14
    c: DistanceX(g23,g23) = 14
    c: DistanceX(g28,g28) = 14
    c: DistanceX(g33,g33) = 14
    c: DistanceX(g38,g38) = 14
    c: DistanceX(g43,g43) = 14
    c: DistanceX(g48,g48) = 14
    c: DistanceX(g53,g53) = 14
    c: DistanceX(g58,g58) = 14
    c: DistanceX(g63,g63) = 14
    c: DistanceX(g68,g68) = 14
    c: DistanceX(g73,g73) = 14
    c: DistanceY(g7,g7) = 14
    c: DistanceY(g12,g12) = 14
    c: DistanceY(g17,g17) = 14
    c: DistanceY(g22,g22) = 14
    c: DistanceY(g27,g27) = 14
    c: DistanceY(g32,g32) = 14
    c: DistanceY(g37,g37) = 14
    c: DistanceY(g42,g42) = 14
    c: DistanceY(g47,g47) = 14
    c: DistanceY(g52,g52) = 14
    c: DistanceY(g57,g57) = 14
    c: DistanceY(g62,g62) = 14
    c: DistanceY(g67,g67) = 14
    c: DistanceY(g72,g72) = 14
    c: DistanceX(g4,g9) = 19.05
    c: Horizontal(g4,g9)
    c: Horizontal(g9,g14)
    c: Horizontal(g14,g19)
    c: Horizontal(g19,g24)
    c: Horizontal(g24,g29)
    c: Horizontal(g29,g34)
    c: Horizontal(g34,g39)
    c: Horizontal(g39,g44)
    c: Horizontal(g44,g49)
    c: Horizontal(g49,g54)
    c: Horizontal(g54,g59)
    c: Horizontal(g59,g64)
    c: Horizontal(g64,g69)
    c: Horizontal(g69,g74)
    c: DistanceX(g9,g14) = 19.05
    c: DistanceX(g14,g19) = 19.05
    c: DistanceX(g19,g24) = 19.05
    c: DistanceX(g29,g34) = 19.05
    c: DistanceX(g34,g39) = 19.05
    c: DistanceX(g39,g44) = 19.05
    c: DistanceX(g49,g54) = 19.05
    c: DistanceX(g54,g59) = 19.05
    c: DistanceX(g59,g64) = 19.05
    c: DistanceX(g24,g29) = 19.05
    c: DistanceX(g44,g49) = 19.05
    c: DistanceX(g64,g69) = 28.575
    c: DistanceX(g69,g74) = 38.1
FEATURE [PartDesign::Pocket] Pocket
  BaseFeature = -> Pad
  Direction = (0,0,-1)
  Length = 5
  Length2 = 5
  Profile = -> Sketch
  ReferenceAxis = -> Sketch [N_Axis]
  Type = 0
FEATURE [Sketcher::SketchObject] Sketch003
  AttachmentOffset = pos=(0,0,4.1) rot=(0,0,1;0rad)
  FullyConstrained = true
  MapMode = 5
  Placement = pos=(0,0,4.1) rot=(0,0,1;0rad)
  Support = -> [XY_Plane097]
  expr: Constraints[10] = Spreadsheet.switch_hole
  expr: Constraints[11] = Spreadsheet.PCB_width - Spreadsheet.u * 3.75
  expr: Constraints[12] = Spreadsheet.u * 2.75
  expr: Constraints[139] = Spreadsheet.switch_hole
  expr: Constraints[140] = Spreadsheet.switch_hole
  expr: Constraints[141] = Spreadsheet.switch_hole
  expr: Constraints[142] = Spreadsheet.switch_hole
  expr: Constraints[143] = Spreadsheet.switch_hole
  expr: Constraints[144] = Spreadsheet.switch_hole
  expr: Constraints[145] = Spreadsheet.switch_hole
  expr: Constraints[146] = Spreadsheet.switch_hole
  expr: Constraints[147] = Spreadsheet.switch_hole
  expr: Constraints[148] = Spreadsheet.switch_hole
  expr: Constraints[149] = Spreadsheet.switch_hole
  expr: Constraints[150] = Spreadsheet.switch_hole
  expr: Constraints[151] = Spreadsheet.switch_hole
  expr: Constraints[152] = Spreadsheet.switch_hole
  expr: Constraints[153] = Spreadsheet.switch_hole
  expr: Constraints[154] = Spreadsheet.switch_hole
  expr: Constraints[155] = Spreadsheet.switch_hole
  expr: Constraints[156] = Spreadsheet.switch_hole
  expr: Constraints[157] = Spreadsheet.switch_hole
  expr: Constraints[158] = Spreadsheet.switch_hole
  expr: Constraints[159] = Spreadsheet.switch_hole
  expr: Constraints[160] = Spreadsheet.switch_hole
  expr: Constraints[161] = Spreadsheet.switch_hole
  expr: Constraints[162] = Spreadsheet.switch_hole
  expr: Constraints[163] = Spreadsheet.switch_hole
  expr: Constraints[164] = Spreadsheet.switch_hole
  expr: Constraints[165] = Spreadsheet.switch_hole
  expr: Constraints[166] = Spreadsheet.switch_hole
  expr: Constraints[167] = Spreadsheet.u * 1.25
  expr: Constraints[182] = Spreadsheet.u
  expr: Constraints[183] = Spreadsheet.u
  expr: Constraints[184] = Spreadsheet.u
  expr: Constraints[185] = Spreadsheet.u
  expr: Constraints[186] = Spreadsheet.u
  expr: Constraints[187] = Spreadsheet.u
  expr: Constraints[188] = Spreadsheet.u
  expr: Constraints[189] = Spreadsheet.u
  expr: Constraints[190] = Spreadsheet.u
  expr: Constraints[191] = Spreadsheet.u
  expr: Constraints[192] = Spreadsheet.u
  expr: Constraints[193] = Spreadsheet.u * 1.25
  expr: Constraints[194] = Spreadsheet.u * 1.75
  expr: Constraints[9] = Spreadsheet.switch_hole
  sketch-geometry (75):
    g0: LineSegment StartX=45.3875 StartY=-60.5625 StartZ=0 EndX=45.3875 EndY=-74.5625 EndZ=0
    g1: LineSegment StartX=45.3875 StartY=-74.5625 StartZ=0 EndX=59.3875 EndY=-74.5625 EndZ=0
    g2: LineSegment StartX=59.3875 StartY=-74.5625 StartZ=0 EndX=59.3875 EndY=-60.5625 EndZ=0
    g3: LineSegment StartX=59.3875 StartY=-60.5625 StartZ=0 EndX=45.3875 EndY=-60.5625 EndZ=0
    g4: GeomPoint X=52.3875 Y=-67.5625 Z=0
    g5: LineSegment StartX=69.2 StartY=-60.5625 StartZ=0 EndX=69.2 EndY=-74.5625 EndZ=0
    g6: LineSegment StartX=69.2 StartY=-74.5625 StartZ=0 EndX=83.2 EndY=-74.5625 EndZ=0
    g7: LineSegment StartX=83.2 StartY=-74.5625 StartZ=0 EndX=83.2 EndY=-60.5625 EndZ=0
    g8: LineSegment StartX=83.2 StartY=-60.5625 StartZ=0 EndX=69.2 EndY=-60.5625 EndZ=0
    g9: GeomPoint X=76.2 Y=-67.5625 Z=0
    g10: LineSegment StartX=88.25 StartY=-60.5625 StartZ=0 EndX=88.25 EndY=-74.5625 EndZ=0
    g11: LineSegment StartX=88.25 StartY=-74.5625 StartZ=0 EndX=102.25 EndY=-74.5625 EndZ=0
    g12: LineSegment StartX=102.25 StartY=-74.5625 StartZ=0 EndX=102.25 EndY=-60.5625 EndZ=0
    g13: LineSegment StartX=102.25 StartY=-60.5625 StartZ=0 EndX=88.25 EndY=-60.5625 EndZ=0
    g14: GeomPoint X=95.25 Y=-67.5625 Z=0
    g15: LineSegment StartX=107.3 StartY=-60.5625 StartZ=0 EndX=107.3 EndY=-74.5625 EndZ=0
    g16: LineSegment StartX=107.3 StartY=-74.5625 StartZ=0 EndX=121.3 EndY=-74.5625 EndZ=0
    g17: LineSegment StartX=121.3 StartY=-74.5625 StartZ=0 EndX=121.3 EndY=-60.5625 EndZ=0
    g18: LineSegment StartX=121.3 StartY=-60.5625 StartZ=0 EndX=107.3 EndY=-60.5625 EndZ=0
    g19: GeomPoint X=114.3 Y=-67.5625 Z=0
    g20: LineSegment StartX=126.35 StartY=-60.5625 StartZ=0 EndX=126.35 EndY=-74.5625 EndZ=0
    g21: LineSegment StartX=126.35 StartY=-74.5625 StartZ=0 EndX=140.35 EndY=-74.5625 EndZ=0
    g22: LineSegment StartX=140.35 StartY=-74.5625 StartZ=0 EndX=140.35 EndY=-60.5625 EndZ=0
    g23: LineSegment StartX=140.35 StartY=-60.5625 StartZ=0 EndX=126.35 EndY=-60.5625 EndZ=0
    g24: GeomPoint X=133.35 Y=-67.5625 Z=0
    g25: LineSegment StartX=145.4 StartY=-60.5625 StartZ=0 EndX=145.4 EndY=-74.5625 EndZ=0
    g26: LineSegment StartX=145.4 StartY=-74.5625 StartZ=0 EndX=159.4 EndY=-74.5625 EndZ=0
    g27: LineSegment StartX=159.4 StartY=-74.5625 StartZ=0 EndX=159.4 EndY=-60.5625 EndZ=0
    g28: LineSegment StartX=159.4 StartY=-60.5625 StartZ=0 EndX=145.4 EndY=-60.5625 EndZ=0
    g29: GeomPoint X=152.4 Y=-67.5625 Z=0
    g30: LineSegment StartX=164.45 StartY=-60.5625 StartZ=0 EndX=164.45 EndY=-74.5625 EndZ=0
    g31: LineSegment StartX=164.45 StartY=-74.5625 StartZ=0 EndX=178.45 EndY=-74.5625 EndZ=0
    g32: LineSegment StartX=178.45 StartY=-74.5625 StartZ=0 EndX=178.45 EndY=-60.5625 EndZ=0
    g33: LineSegment StartX=178.45 StartY=-60.5625 StartZ=0 EndX=164.45 EndY=-60.5625 EndZ=0
    g34: GeomPoint X=171.45 Y=-67.5625 Z=0
    g35: LineSegment StartX=183.5 StartY=-60.5625 StartZ=0 EndX=183.5 EndY=-74.5625 EndZ=0
    g36: LineSegment StartX=183.5 StartY=-74.5625 StartZ=0 EndX=197.5 EndY=-74.5625 EndZ=0
    g37: LineSegment StartX=197.5 StartY=-74.5625 StartZ=0 EndX=197.5 EndY=-60.5625 EndZ=0
    g38: LineSegment StartX=197.5 StartY=-60.5625 StartZ=0 EndX=183.5 EndY=-60.5625 EndZ=0
    g39: GeomPoint X=190.5 Y=-67.5625 Z=0
    g40: LineSegment StartX=202.55 StartY=-60.5625 StartZ=0 EndX=202.55 EndY=-74.5625 EndZ=0
    g41: LineSegment StartX=202.55 StartY=-74.5625 StartZ=0 EndX=216.55 EndY=-74.5625 EndZ=0
    g42: LineSegment StartX=216.55 StartY=-74.5625 StartZ=0 EndX=216.55 EndY=-60.5625 EndZ=0
    g43: LineSegment StartX=216.55 StartY=-60.5625 StartZ=0 EndX=202.55 EndY=-60.5625 EndZ=0
    g44: GeomPoint X=209.55 Y=-67.5625 Z=0
    g45: LineSegment StartX=221.6 StartY=-60.5625 StartZ=0 EndX=221.6 EndY=-74.5625 EndZ=0
    g46: LineSegment StartX=221.6 StartY=-74.5625 StartZ=0 EndX=235.6 EndY=-74.5625 EndZ=0
    g47: LineSegment StartX=235.6 StartY=-74.5625 StartZ=0 EndX=235.6 EndY=-60.5625 EndZ=0
    g48: LineSegment StartX=235.6 StartY=-60.5625 StartZ=0 EndX=221.6 EndY=-60.5625 EndZ=0
    g49: GeomPoint X=228.6 Y=-67.5625 Z=0
    g50: LineSegment StartX=240.65 StartY=-60.5625 StartZ=0 EndX=240.65 EndY=-74.5625 EndZ=0
    g51: LineSegment StartX=240.65 StartY=-74.5625 StartZ=0 EndX=254.65 EndY=-74.5625 EndZ=0
    g52: LineSegment StartX=254.65 StartY=-74.5625 StartZ=0 EndX=254.65 EndY=-60.5625 EndZ=0
    g53: LineSegment StartX=254.65 StartY=-60.5625 StartZ=0 EndX=240.65 EndY=-60.5625 EndZ=0
    g54: GeomPoint X=247.65 Y=-67.5625 Z=0
    g55: LineSegment StartX=259.7 StartY=-60.5625 StartZ=0 EndX=259.7 EndY=-74.5625 EndZ=0
    g56: LineSegment StartX=259.7 StartY=-74.5625 StartZ=0 EndX=273.7 EndY=-74.5625 EndZ=0
    g57: LineSegment StartX=273.7 StartY=-74.5625 StartZ=0 EndX=273.7 EndY=-60.5625 EndZ=0
    g58: LineSegment StartX=273.7 StartY=-60.5625 StartZ=0 EndX=259.7 EndY=-60.5625 EndZ=0
    g59: GeomPoint X=266.7 Y=-67.5625 Z=0
    g60: LineSegment StartX=278.75 StartY=-60.5625 StartZ=0 EndX=278.75 EndY=-74.5625 EndZ=0
    g61: LineSegment StartX=278.75 StartY=-74.5625 StartZ=0 EndX=292.75 EndY=-74.5625 EndZ=0
    g62: LineSegment StartX=292.75 StartY=-74.5625 StartZ=0 EndX=292.75 EndY=-60.5625 EndZ=0
    g63: LineSegment StartX=292.75 StartY=-60.5625 StartZ=0 EndX=278.75 EndY=-60.5625 EndZ=0
    g64: GeomPoint X=285.75 Y=-67.5625 Z=0
    g65: LineSegment StartX=302.562 StartY=-60.5625 StartZ=0 EndX=302.562 EndY=-74.5625 EndZ=0
    g66: LineSegment StartX=302.562 StartY=-74.5625 StartZ=0 EndX=316.562 EndY=-74.5625 EndZ=0
    g67: LineSegment StartX=316.562 StartY=-74.5625 StartZ=0 EndX=316.562 EndY=-60.5625 EndZ=0
    g68: LineSegment StartX=316.562 StartY=-60.5625 StartZ=0 EndX=302.562 EndY=-60.5625 EndZ=0
    g69: GeomPoint X=309.562 Y=-67.5625 Z=0
    g70: LineSegment StartX=335.9 StartY=-60.5625 StartZ=0 EndX=335.9 EndY=-74.5625 EndZ=0
    g71: LineSegment StartX=335.9 StartY=-74.5625 StartZ=0 EndX=349.9 EndY=-74.5625 EndZ=0
    g72: LineSegment StartX=349.9 StartY=-74.5625 StartZ=0 EndX=349.9 EndY=-60.5625 EndZ=0
    g73: LineSegment StartX=349.9 StartY=-60.5625 StartZ=0 EndX=335.9 EndY=-60.5625 EndZ=0
    g74: GeomPoint X=342.9 Y=-67.5625 Z=0
  constraints (195):
    c: Coincident(g0,g1)
    c: Coincident(g1,g2)
    c: Coincident(g2,g3)
    c: Coincident(g3,g0)
    c: Horizontal(g1)
    c: Horizontal(g3)
    c: Vertical(g0)
    c: Vertical(g2)
    c: Symmetric(g1,g0,g4)
    c: DistanceX(g3,g3) = 14
    c: DistanceY(g2,g2) = 14
    c: DistanceY(g4,g-1) = 67.5625
    c: DistanceX(g-1,g4) = 52.3875
    c: Coincident(g5,g6)
    c: Coincident(g6,g7)
    c: Coincident(g7,g8)
    c: Coincident(g8,g5)
    c: Horizontal(g6)
    c: Horizontal(g8)
    c: Vertical(g5)
    c: Vertical(g7)
    c: Symmetric(g6,g5,g9)
    c: Coincident(g10,g11)
    c: Coincident(g11,g12)
    c: Coincident(g12,g13)
    c: Coincident(g13,g10)
    c: Horizontal(g11)
    c: Horizontal(g13)
    c: Vertical(g10)
    c: Vertical(g12)
    c: Symmetric(g11,g10,g14)
    c: Coincident(g15,g16)
    c: Coincident(g16,g17)
    c: Coincident(g17,g18)
    c: Coincident(g18,g15)
    c: Horizontal(g16)
    c: Horizontal(g18)
    c: Vertical(g15)
    c: Vertical(g17)
    c: Symmetric(g16,g15,g19)
    c: Coincident(g20,g21)
    c: Coincident(g21,g22)
    c: Coincident(g22,g23)
    c: Coincident(g23,g20)
    c: Horizontal(g21)
    c: Horizontal(g23)
    c: Vertical(g20)
    c: Vertical(g22)
    c: Symmetric(g21,g20,g24)
    c: Coincident(g25,g26)
    c: Coincident(g26,g27)
    c: Coincident(g27,g28)
    c: Coincident(g28,g25)
    c: Horizontal(g26)
    c: Horizontal(g28)
    c: Vertical(g25)
    c: Vertical(g27)
    c: Symmetric(g26,g25,g29)
    c: Coincident(g30,g31)
    c: Coincident(g31,g32)
    c: Coincident(g32,g33)
    c: Coincident(g33,g30)
    c: Horizontal(g31)
    c: Horizontal(g33)
    c: Vertical(g30)
    c: Vertical(g32)
    c: Symmetric(g31,g30,g34)
    c: Coincident(g35,g36)
    c: Coincident(g36,g37)
    c: Coincident(g37,g38)
    c: Coincident(g38,g35)
    c: Horizontal(g36)
    c: Horizontal(g38)
    c: Vertical(g35)
    c: Vertical(g37)
    c: Symmetric(g36,g35,g39)
    c: Coincident(g40,g41)
    c: Coincident(g41,g42)
    c: Coincident(g42,g43)
    c: Coincident(g43,g40)
    c: Horizontal(g41)
    c: Horizontal(g43)
    c: Vertical(g40)
    c: Vertical(g42)
    c: Symmetric(g41,g40,g44)
    c: Coincident(g45,g46)
    c: Coincident(g46,g47)
    c: Coincident(g47,g48)
    c: Coincident(g48,g45)
    c: Horizontal(g46)
    c: Horizontal(g48)
    c: Vertical(g45)
    c: Vertical(g47)
    c: Symmetric(g46,g45,g49)
    c: Coincident(g50,g51)
    c: Coincident(g51,g52)
    c: Coincident(g52,g53)
    c: Coincident(g53,g50)
    c: Horizontal(g51)
    c: Horizontal(g53)
    c: Vertical(g50)
    c: Vertical(g52)
    c: Symmetric(g51,g50,g54)
    c: Coincident(g55,g56)
    c: Coincident(g56,g57)
    c: Coincident(g57,g58)
    c: Coincident(g58,g55)
    c: Horizontal(g56)
    c: Horizontal(g58)
    c: Vertical(g55)
    c: Vertical(g57)
    c: Symmetric(g56,g55,g59)
    c: Coincident(g60,g61)
    c: Coincident(g61,g62)
    c: Coincident(g62,g63)
    c: Coincident(g63,g60)
    c: Horizontal(g61)
    c: Horizontal(g63)
    c: Vertical(g60)
    c: Vertical(g62)
    c: Symmetric(g61,g60,g64)
    c: Coincident(g65,g66)
    c: Coincident(g66,g67)
    c: Coincident(g67,g68)
    c: Coincident(g68,g65)
    c: Horizontal(g66)
    c: Horizontal(g68)
    c: Vertical(g65)
    c: Vertical(g67)
    c: Symmetric(g66,g65,g69)
    c: Coincident(g70,g71)
    c: Coincident(g71,g72)
    c: Coincident(g72,g73)
    c: Coincident(g73,g70)
    c: Horizontal(g71)
    c: Horizontal(g73)
    c: Vertical(g70)
    c: Vertical(g72)
    c: Symmetric(g71,g70,g74)
    c: DistanceX(g8,g8) = 14
    c: DistanceX(g13,g13) = 14
    c: DistanceX(g18,g18) = 14
    c: DistanceX(g23,g23) = 14
    c: DistanceX(g28,g28) = 14
    c: DistanceX(g33,g33) = 14
    c: DistanceX(g38,g38) = 14
    c: DistanceX(g43,g43) = 14
    c: DistanceX(g48,g48) = 14
    c: DistanceX(g53,g53) = 14
    c: DistanceX(g58,g58) = 14
    c: DistanceX(g63,g63) = 14
    c: DistanceX(g68,g68) = 14
    c: DistanceX(g73,g73) = 14
    c: DistanceY(g7,g7) = 14
    c: DistanceY(g12,g12) = 14
    c: DistanceY(g17,g17) = 14
    c: DistanceY(g22,g22) = 14
    c: DistanceY(g27,g27) = 14
    c: DistanceY(g32,g32) = 14
    c: DistanceY(g37,g37) = 14
    c: DistanceY(g42,g42) = 14
    c: DistanceY(g47,g47) = 14
    c: DistanceY(g52,g52) = 14
    c: DistanceY(g57,g57) = 14
    c: DistanceY(g62,g62) = 14
    c: DistanceY(g67,g67) = 14
    c: DistanceY(g72,g72) = 14
    c: DistanceX(g4,g9) = 23.8125
    c: Horizontal(g4,g9)
    c: Horizontal(g9,g14)
    c: Horizontal(g14,g19)
    c: Horizontal(g19,g24)
    c: Horizontal(g24,g29)
    c: Horizontal(g29,g34)
    c: Horizontal(g34,g39)
    c: Horizontal(g39,g44)
    c: Horizontal(g44,g49)
    c: Horizontal(g49,g54)
    c: Horizontal(g54,g59)
    c: Horizontal(g59,g64)
    c: Horizontal(g64,g69)
    c: Horizontal(g69,g74)
    c: DistanceX(g9,g14) = 19.05
    c: DistanceX(g14,g19) = 19.05
    c: DistanceX(g19,g24) = 19.05
    c: DistanceX(g29,g34) = 19.05
    c: DistanceX(g34,g39) = 19.05
    c: DistanceX(g39,g44) = 19.05
    c: DistanceX(g49,g54) = 19.05
    c: DistanceX(g54,g59) = 19.05
    c: DistanceX(g59,g64) = 19.05
    c: DistanceX(g24,g29) = 19.05
    c: DistanceX(g44,g49) = 19.05
    c: DistanceX(g64,g69) = 23.8125
    c: DistanceX(g69,g74) = 33.3375
FEATURE [PartDesign::Pocket] Pocket001
  BaseFeature = -> Pocket
  Direction = (0,0,-1)
  Length = 5
  Length2 = 5
  Profile = -> Sketch002
  ReferenceAxis = -> Sketch002 [N_Axis]
  Type = 0
FEATURE [Sketcher::SketchObject] Sketch004
  AttachmentOffset = pos=(0,0,4.1) rot=(0,0,1;0rad)
  FullyConstrained = true
  MapMode = 5
  Placement = pos=(0,0,4.1) rot=(0,0,1;0rad)
  Support = -> [XY_Plane097]
  expr: Constraints[10] = Spreadsheet.switch_hole
  expr: Constraints[11] = Spreadsheet.PCB_width - Spreadsheet.u * 2.75
  expr: Constraints[12] = Spreadsheet.u * 2.875
  expr: Constraints[130] = Spreadsheet.switch_hole
  expr: Constraints[131] = Spreadsheet.switch_hole
  expr: Constraints[132] = Spreadsheet.switch_hole
  expr: Constraints[133] = Spreadsheet.switch_hole
  expr: Constraints[134] = Spreadsheet.switch_hole
  expr: Constraints[135] = Spreadsheet.switch_hole
  expr: Constraints[136] = Spreadsheet.switch_hole
  expr: Constraints[137] = Spreadsheet.switch_hole
  expr: Constraints[138] = Spreadsheet.switch_hole
  expr: Constraints[139] = Spreadsheet.switch_hole
  expr: Constraints[140] = Spreadsheet.switch_hole
  expr: Constraints[141] = Spreadsheet.switch_hole
  expr: Constraints[142] = Spreadsheet.switch_hole
  expr: Constraints[143] = Spreadsheet.switch_hole
  expr: Constraints[144] = Spreadsheet.switch_hole
  expr: Constraints[145] = Spreadsheet.switch_hole
  expr: Constraints[146] = Spreadsheet.switch_hole
  expr: Constraints[147] = Spreadsheet.switch_hole
  expr: Constraints[148] = Spreadsheet.switch_hole
  expr: Constraints[149] = Spreadsheet.switch_hole
  expr: Constraints[150] = Spreadsheet.switch_hole
  expr: Constraints[151] = Spreadsheet.switch_hole
  expr: Constraints[152] = Spreadsheet.switch_hole
  expr: Constraints[153] = Spreadsheet.switch_hole
  expr: Constraints[154] = Spreadsheet.switch_hole
  expr: Constraints[155] = Spreadsheet.switch_hole
  expr: Constraints[156] = Spreadsheet.u * 1.375
  expr: Constraints[170] = Spreadsheet.u
  expr: Constraints[171] = Spreadsheet.u
  expr: Constraints[172] = Spreadsheet.u
  expr: Constraints[173] = Spreadsheet.u
  expr: Constraints[174] = Spreadsheet.u
  expr: Constraints[175] = Spreadsheet.u
  expr: Constraints[176] = Spreadsheet.u
  expr: Constraints[177] = Spreadsheet.u
  expr: Constraints[178] = Spreadsheet.u * (0.5 + 1.125)
  expr: Constraints[179] = Spreadsheet.u
  expr: Constraints[180] = Spreadsheet.u
  expr: Constraints[181] = Spreadsheet.u * (1.125 + 1)
  expr: Constraints[9] = Spreadsheet.switch_hole
  sketch-geometry (70):
    g0: LineSegment StartX=47.7688 StartY=-79.6125 StartZ=0 EndX=47.7688 EndY=-93.6125 EndZ=0
    g1: LineSegment StartX=47.7688 StartY=-93.6125 StartZ=0 EndX=61.7688 EndY=-93.6125 EndZ=0
    g2: LineSegment StartX=61.7688 StartY=-93.6125 StartZ=0 EndX=61.7688 EndY=-79.6125 EndZ=0
    g3: LineSegment StartX=61.7688 StartY=-79.6125 StartZ=0 EndX=47.7688 EndY=-79.6125 EndZ=0
    g4: GeomPoint X=54.7688 Y=-86.6125 Z=0
    g5: LineSegment StartX=73.9625 StartY=-79.6125 StartZ=0 EndX=73.9625 EndY=-93.6125 EndZ=0
    g6: LineSegment StartX=73.9625 StartY=-93.6125 StartZ=0 EndX=87.9625 EndY=-93.6125 EndZ=0
    g7: LineSegment StartX=87.9625 StartY=-93.6125 StartZ=0 EndX=87.9625 EndY=-79.6125 EndZ=0
    g8: LineSegment StartX=87.9625 StartY=-79.6125 StartZ=0 EndX=73.9625 EndY=-79.6125 EndZ=0
    g9: GeomPoint X=80.9625 Y=-86.6125 Z=0
    g10: LineSegment StartX=93.0125 StartY=-79.6125 StartZ=0 EndX=93.0125 EndY=-93.6125 EndZ=0
    g11: LineSegment StartX=93.0125 StartY=-93.6125 StartZ=0 EndX=107.012 EndY=-93.6125 EndZ=0
    g12: LineSegment StartX=107.012 StartY=-93.6125 StartZ=0 EndX=107.012 EndY=-79.6125 EndZ=0
    g13: LineSegment StartX=107.012 StartY=-79.6125 StartZ=0 EndX=93.0125 EndY=-79.6125 EndZ=0
    g14: GeomPoint X=100.013 Y=-86.6125 Z=0
    g15: LineSegment StartX=112.063 StartY=-79.6125 StartZ=0 EndX=112.063 EndY=-93.6125 EndZ=0
    g16: LineSegment StartX=112.063 StartY=-93.6125 StartZ=0 EndX=126.063 EndY=-93.6125 EndZ=0
    g17: LineSegment StartX=126.063 StartY=-93.6125 StartZ=0 EndX=126.063 EndY=-79.6125 EndZ=0
    g18: LineSegment StartX=126.063 StartY=-79.6125 StartZ=0 EndX=112.063 EndY=-79.6125 EndZ=0
    g19: GeomPoint X=119.062 Y=-86.6125 Z=0
    g20: LineSegment StartX=131.113 StartY=-79.6125 StartZ=0 EndX=131.113 EndY=-93.6125 EndZ=0
    g21: LineSegment StartX=131.113 StartY=-93.6125 StartZ=0 EndX=145.113 EndY=-93.6125 EndZ=0
    g22: LineSegment StartX=145.113 StartY=-93.6125 StartZ=0 EndX=145.113 EndY=-79.6125 EndZ=0
    g23: LineSegment StartX=145.113 StartY=-79.6125 StartZ=0 EndX=131.113 EndY=-79.6125 EndZ=0
    g24: GeomPoint X=138.113 Y=-86.6125 Z=0
    g25: LineSegment StartX=150.163 StartY=-79.6125 StartZ=0 EndX=150.163 EndY=-93.6125 EndZ=0
    g26: LineSegment StartX=150.163 StartY=-93.6125 StartZ=0 EndX=164.163 EndY=-93.6125 EndZ=0
    g27: LineSegment StartX=164.163 StartY=-93.6125 StartZ=0 EndX=164.163 EndY=-79.6125 EndZ=0
    g28: LineSegment StartX=164.163 StartY=-79.6125 StartZ=0 EndX=150.163 EndY=-79.6125 EndZ=0
    g29: GeomPoint X=157.163 Y=-86.6125 Z=0
    g30: LineSegment StartX=169.213 StartY=-79.6125 StartZ=0 EndX=169.213 EndY=-93.6125 EndZ=0
    g31: LineSegment StartX=169.213 StartY=-93.6125 StartZ=0 EndX=183.213 EndY=-93.6125 EndZ=0
    g32: LineSegment StartX=183.213 StartY=-93.6125 StartZ=0 EndX=183.213 EndY=-79.6125 EndZ=0
    g33: LineSegment StartX=183.213 StartY=-79.6125 StartZ=0 EndX=169.213 EndY=-79.6125 EndZ=0
    g34: GeomPoint X=176.213 Y=-86.6125 Z=0
    g35: LineSegment StartX=188.263 StartY=-79.6125 StartZ=0 EndX=188.263 EndY=-93.6125 EndZ=0
    g36: LineSegment StartX=188.263 StartY=-93.6125 StartZ=0 EndX=202.263 EndY=-93.6125 EndZ=0
    g37: LineSegment StartX=202.263 StartY=-93.6125 StartZ=0 EndX=202.263 EndY=-79.6125 EndZ=0
    g38: LineSegment StartX=202.263 StartY=-79.6125 StartZ=0 EndX=188.263 EndY=-79.6125 EndZ=0
    g39: GeomPoint X=195.263 Y=-86.6125 Z=0
    g40: LineSegment StartX=207.313 StartY=-79.6125 StartZ=0 EndX=207.313 EndY=-93.6125 EndZ=0
    g41: LineSegment StartX=207.313 StartY=-93.6125 StartZ=0 EndX=221.313 EndY=-93.6125 EndZ=0
    g42: LineSegment StartX=221.313 StartY=-93.6125 StartZ=0 EndX=221.313 EndY=-79.6125 EndZ=0
    g43: LineSegment StartX=221.313 StartY=-79.6125 StartZ=0 EndX=207.313 EndY=-79.6125 EndZ=0
    g44: GeomPoint X=214.312 Y=-86.6125 Z=0
    g45: LineSegment StartX=226.362 StartY=-79.6125 StartZ=0 EndX=226.362 EndY=-93.6125 EndZ=0
    g46: LineSegment StartX=226.362 StartY=-93.6125 StartZ=0 EndX=240.362 EndY=-93.6125 EndZ=0
    g47: LineSegment StartX=240.362 StartY=-93.6125 StartZ=0 EndX=240.362 EndY=-79.6125 EndZ=0
    g48: LineSegment StartX=240.362 StartY=-79.6125 StartZ=0 EndX=226.362 EndY=-79.6125 EndZ=0
    g49: GeomPoint X=233.363 Y=-86.6125 Z=0
    g50: LineSegment StartX=245.412 StartY=-79.6125 StartZ=0 EndX=245.412 EndY=-93.6125 EndZ=0
    g51: LineSegment StartX=245.412 StartY=-93.6125 StartZ=0 EndX=259.413 EndY=-93.6125 EndZ=0
    g52: LineSegment StartX=259.413 StartY=-93.6125 StartZ=0 EndX=259.413 EndY=-79.6125 EndZ=0
    g53: LineSegment StartX=259.413 StartY=-79.6125 StartZ=0 EndX=245.412 EndY=-79.6125 EndZ=0
    g54: GeomPoint X=252.413 Y=-86.6125 Z=0
    g55: LineSegment StartX=264.463 StartY=-79.6125 StartZ=0 EndX=264.463 EndY=-93.6125 EndZ=0
    g56: LineSegment StartX=264.463 StartY=-93.6125 StartZ=0 EndX=278.463 EndY=-93.6125 EndZ=0
    g57: LineSegment StartX=278.463 StartY=-93.6125 StartZ=0 EndX=278.463 EndY=-79.6125 EndZ=0
    g58: LineSegment StartX=278.463 StartY=-79.6125 StartZ=0 EndX=264.463 EndY=-79.6125 EndZ=0
    g59: GeomPoint X=271.463 Y=-86.6125 Z=0
    g60: LineSegment StartX=295.419 StartY=-79.6125 StartZ=0 EndX=295.419 EndY=-93.6125 EndZ=0
    g61: LineSegment StartX=295.419 StartY=-93.6125 StartZ=0 EndX=309.419 EndY=-93.6125 EndZ=0
    g62: LineSegment StartX=309.419 StartY=-93.6125 StartZ=0 EndX=309.419 EndY=-79.6125 EndZ=0
    g63: LineSegment StartX=309.419 StartY=-79.6125 StartZ=0 EndX=295.419 EndY=-79.6125 EndZ=0
    g64: GeomPoint X=302.419 Y=-86.6125 Z=0
    g65: LineSegment StartX=335.9 StartY=-79.6125 StartZ=0 EndX=335.9 EndY=-93.6125 EndZ=0
    g66: LineSegment StartX=335.9 StartY=-93.6125 StartZ=0 EndX=349.9 EndY=-93.6125 EndZ=0
    g67: LineSegment StartX=349.9 StartY=-93.6125 StartZ=0 EndX=349.9 EndY=-79.6125 EndZ=0
    g68: LineSegment StartX=349.9 StartY=-79.6125 StartZ=0 EndX=335.9 EndY=-79.6125 EndZ=0
    g69: GeomPoint X=342.9 Y=-86.6125 Z=0
  constraints (182):
    c: Coincident(g0,g1)
    c: Coincident(g1,g2)
    c: Coincident(g2,g3)
    c: Coincident(g3,g0)
    c: Horizontal(g1)
    c: Horizontal(g3)
    c: Vertical(g0)
    c: Vertical(g2)
    c: Symmetric(g1,g0,g4)
    c: DistanceX(g3,g3) = 14
    c: DistanceY(g2,g2) = 14
    c: DistanceY(g4,g-1) = 86.6125
    c: DistanceX(g-1,g4) = 54.7688
    c: Coincident(g5,g6)
    c: Coincident(g6,g7)
    c: Coincident(g7,g8)
    c: Coincident(g8,g5)
    c: Horizontal(g6)
    c: Horizontal(g8)
    c: Vertical(g5)
    c: Vertical(g7)
    c: Symmetric(g6,g5,g9)
    c: Coincident(g10,g11)
    c: Coincident(g11,g12)
    c: Coincident(g12,g13)
    c: Coincident(g13,g10)
    c: Horizontal(g11)
    c: Horizontal(g13)
    c: Vertical(g10)
    c: Vertical(g12)
    c: Symmetric(g11,g10,g14)
    c: Coincident(g15,g16)
    c: Coincident(g16,g17)
    c: Coincident(g17,g18)
    c: Coincident(g18,g15)
    c: Horizontal(g16)
    c: Horizontal(g18)
    c: Vertical(g15)
    c: Vertical(g17)
    c: Symmetric(g16,g15,g19)
    c: Coincident(g20,g21)
    c: Coincident(g21,g22)
    c: Coincident(g22,g23)
    c: Coincident(g23,g20)
    c: Horizontal(g21)
    c: Horizontal(g23)
    c: Vertical(g20)
    c: Vertical(g22)
    c: Symmetric(g21,g20,g24)
    c: Coincident(g25,g26)
    c: Coincident(g26,g27)
    c: Coincident(g27,g28)
    c: Coincident(g28,g25)
    c: Horizontal(g26)
    c: Horizontal(g28)
    c: Vertical(g25)
    c: Vertical(g27)
    c: Symmetric(g26,g25,g29)
    c: Coincident(g30,g31)
    c: Coincident(g31,g32)
    c: Coincident(g32,g33)
    c: Coincident(g33,g30)
    c: Horizontal(g31)
    c: Horizontal(g33)
    c: Vertical(g30)
    c: Vertical(g32)
    c: Symmetric(g31,g30,g34)
    c: Coincident(g35,g36)
    c: Coincident(g36,g37)
    c: Coincident(g37,g38)
    c: Coincident(g38,g35)
    c: Horizontal(g36)
    c: Horizontal(g38)
    c: Vertical(g35)
    c: Vertical(g37)
    c: Symmetric(g36,g35,g39)
    c: Coincident(g40,g41)
    c: Coincident(g41,g42)
    c: Coincident(g42,g43)
    c: Coincident(g43,g40)
    c: Horizontal(g41)
    c: Horizontal(g43)
    c: Vertical(g40)
    c: Vertical(g42)
    c: Symmetric(g41,g40,g44)
    c: Coincident(g45,g46)
    c: Coincident(g46,g47)
    c: Coincident(g47,g48)
    c: Coincident(g48,g45)
    c: Horizontal(g46)
    c: Horizontal(g48)
    c: Vertical(g45)
    c: Vertical(g47)
    c: Symmetric(g46,g45,g49)
    c: Coincident(g50,g51)
    c: Coincident(g51,g52)
    c: Coincident(g52,g53)
    c: Coincident(g53,g50)
    c: Horizontal(g51)
    c: Horizontal(g53)
    c: Vertical(g50)
    c: Vertical(g52)
    c: Symmetric(g51,g50,g54)
    c: Coincident(g55,g56)
    c: Coincident(g56,g57)
    c: Coincident(g57,g58)
    c: Coincident(g58,g55)
    c: Horizontal(g56)
    c: Horizontal(g58)
    c: Vertical(g55)
    c: Vertical(g57)
    c: Symmetric(g56,g55,g59)
    c: Coincident(g60,g61)
    c: Coincident(g61,g62)
    c: Coincident(g62,g63)
    c: Coincident(g63,g60)
    c: Horizontal(g61)
    c: Horizontal(g63)
    c: Vertical(g60)
    c: Vertical(g62)
    c: Symmetric(g61,g60,g64)
    c: Coincident(g65,g66)
    c: Coincident(g66,g67)
    c: Coincident(g67,g68)
    c: Coincident(g68,g65)
    c: Horizontal(g66)
    c: Horizontal(g68)
    c: Vertical(g65)
    c: Vertical(g67)
    c: Symmetric(g66,g65,g69)
    c: DistanceX(g8,g8) = 14
    c: DistanceX(g13,g13) = 14
    c: DistanceX(g18,g18) = 14
    c: DistanceX(g23,g23) = 14
    c: DistanceX(g28,g28) = 14
    c: DistanceX(g33,g33) = 14
    c: DistanceX(g38,g38) = 14
    c: DistanceX(g43,g43) = 14
    c: DistanceX(g48,g48) = 14
    c: DistanceX(g53,g53) = 14
    c: DistanceX(g58,g58) = 14
    c: DistanceX(g63,g63) = 14
    c: DistanceX(g68,g68) = 14
    c: DistanceY(g7,g7) = 14
    c: DistanceY(g12,g12) = 14
    c: DistanceY(g17,g17) = 14
    c: DistanceY(g22,g22) = 14
    c: DistanceY(g27,g27) = 14
    c: DistanceY(g32,g32) = 14
    c: DistanceY(g37,g37) = 14
    c: DistanceY(g42,g42) = 14
    c: DistanceY(g47,g47) = 14
    c: DistanceY(g52,g52) = 14
    c: DistanceY(g57,g57) = 14
    c: DistanceY(g62,g62) = 14
    c: DistanceY(g67,g67) = 14
    c: DistanceX(g4,g9) = 26.1938
    c: Horizontal(g4,g9)
    c: Horizontal(g9,g14)
    c: Horizontal(g14,g19)
    c: Horizontal(g19,g24)
    c: Horizontal(g24,g29)
    c: Horizontal(g29,g34)
    c: Horizontal(g34,g39)
    c: Horizontal(g39,g44)
    c: Horizontal(g44,g49)
    c: Horizontal(g49,g54)
    c: Horizontal(g54,g59)
    c: Horizontal(g59,g64)
    c: Horizontal(g64,g69)
    c: DistanceX(g9,g14) = 19.05
    c: DistanceX(g14,g19) = 19.05
    c: DistanceX(g19,g24) = 19.05
    c: DistanceX(g29,g34) = 19.05
    c: DistanceX(g34,g39) = 19.05
    c: DistanceX(g39,g44) = 19.05
    c: DistanceX(g49,g54) = 19.05
    c: DistanceX(g54,g59) = 19.05
    c: DistanceX(g59,g64) = 30.9563
    c: DistanceX(g24,g29) = 19.05
    c: DistanceX(g44,g49) = 19.05
    c: DistanceX(g64,g69) = 40.4813
FEATURE [PartDesign::Pocket] Pocket002
  BaseFeature = -> Pocket001
  Direction = (0,0,-1)
  Length = 5
  Length2 = 5
  Profile = -> Sketch003
  ReferenceAxis = -> Sketch003 [N_Axis]
  Type = 0
FEATURE [Sketcher::SketchObject] Sketch005
  AttachmentOffset = pos=(0,0,4.1) rot=(0,0,1;0rad)
  FullyConstrained = true
  MapMode = 5
  Placement = pos=(0,0,4.1) rot=(0,0,1;0rad)
  Support = -> [XY_Plane097]
  expr: Constraints[10] = Spreadsheet.switch_hole
  expr: Constraints[11] = Spreadsheet.PCB_width - Spreadsheet.u * 1.75
  expr: Constraints[12] = Spreadsheet.u * (2 + 1.125)
  expr: Constraints[130] = Spreadsheet.switch_hole
  expr: Constraints[131] = Spreadsheet.switch_hole
  expr: Constraints[132] = Spreadsheet.switch_hole
  expr: Constraints[133] = Spreadsheet.switch_hole
  expr: Constraints[134] = Spreadsheet.switch_hole
  expr: Constraints[135] = Spreadsheet.switch_hole
  expr: Constraints[136] = Spreadsheet.switch_hole
  expr: Constraints[137] = Spreadsheet.switch_hole
  expr: Constraints[138] = Spreadsheet.switch_hole
  expr: Constraints[139] = Spreadsheet.switch_hole
  expr: Constraints[140] = Spreadsheet.switch_hole
  expr: Constraints[141] = Spreadsheet.switch_hole
  expr: Constraints[142] = Spreadsheet.switch_hole
  expr: Constraints[143] = Spreadsheet.switch_hole
  expr: Constraints[144] = Spreadsheet.switch_hole
  expr: Constraints[145] = Spreadsheet.switch_hole
  expr: Constraints[146] = Spreadsheet.switch_hole
  expr: Constraints[147] = Spreadsheet.switch_hole
  expr: Constraints[148] = Spreadsheet.switch_hole
  expr: Constraints[149] = Spreadsheet.switch_hole
  expr: Constraints[150] = Spreadsheet.switch_hole
  expr: Constraints[151] = Spreadsheet.switch_hole
  expr: Constraints[152] = Spreadsheet.switch_hole
  expr: Constraints[153] = Spreadsheet.switch_hole
  expr: Constraints[154] = Spreadsheet.switch_hole
  expr: Constraints[155] = Spreadsheet.switch_hole
  expr: Constraints[156] = Spreadsheet.u * (1.125 + 0.5)
  expr: Constraints[168] = Spreadsheet.u
  expr: Constraints[169] = Spreadsheet.u
  expr: Constraints[170] = Spreadsheet.u
  expr: Constraints[171] = Spreadsheet.u
  expr: Constraints[172] = Spreadsheet.u
  expr: Constraints[173] = Spreadsheet.u
  expr: Constraints[174] = Spreadsheet.u
  expr: Constraints[175] = Spreadsheet.u * (0.5 + 1.75 / 2)
  expr: Constraints[176] = Spreadsheet.u * (0.5 + 1.125)
  expr: Constraints[177] = Spreadsheet.u
  expr: Constraints[178] = Spreadsheet.u
  expr: Constraints[179] = Spreadsheet.u * 1.25
  expr: Constraints[181] = Spreadsheet.u * 0.25
  expr: Constraints[9] = Spreadsheet.switch_hole
  sketch-geometry (70):
    g0: LineSegment StartX=52.5313 StartY=-98.6625 StartZ=0 EndX=52.5313 EndY=-112.662 EndZ=0
    g1: LineSegment StartX=52.5313 StartY=-112.662 StartZ=0 EndX=66.5313 EndY=-112.662 EndZ=0
    g2: LineSegment StartX=66.5313 StartY=-112.662 StartZ=0 EndX=66.5313 EndY=-98.6625 EndZ=0
    g3: LineSegment StartX=66.5313 StartY=-98.6625 StartZ=0 EndX=52.5313 EndY=-98.6625 EndZ=0
    g4: GeomPoint X=59.5312 Y=-105.662 Z=0
    g5: LineSegment StartX=83.4875 StartY=-98.6625 StartZ=0 EndX=83.4875 EndY=-112.663 EndZ=0
    g6: LineSegment StartX=83.4875 StartY=-112.663 StartZ=0 EndX=97.4875 EndY=-112.663 EndZ=0
    g7: LineSegment StartX=97.4875 StartY=-112.663 StartZ=0 EndX=97.4875 EndY=-98.6625 EndZ=0
    g8: LineSegment StartX=97.4875 StartY=-98.6625 StartZ=0 EndX=83.4875 EndY=-98.6625 EndZ=0
    g9: GeomPoint X=90.4875 Y=-105.662 Z=0
    g10: LineSegment StartX=102.538 StartY=-98.6625 StartZ=0 EndX=102.538 EndY=-112.662 EndZ=0
    g11: LineSegment StartX=102.538 StartY=-112.662 StartZ=0 EndX=116.538 EndY=-112.662 EndZ=0
    g12: LineSegment StartX=116.538 StartY=-112.662 StartZ=0 EndX=116.538 EndY=-98.6625 EndZ=0
    g13: LineSegment StartX=116.538 StartY=-98.6625 StartZ=0 EndX=102.538 EndY=-98.6625 EndZ=0
    g14: GeomPoint X=109.537 Y=-105.662 Z=0
    g15: LineSegment StartX=121.587 StartY=-98.6625 StartZ=0 EndX=121.587 EndY=-112.663 EndZ=0
    g16: LineSegment StartX=121.587 StartY=-112.663 StartZ=0 EndX=135.587 EndY=-112.663 EndZ=0
    g17: LineSegment StartX=135.587 StartY=-112.663 StartZ=0 EndX=135.587 EndY=-98.6625 EndZ=0
    g18: LineSegment StartX=135.587 StartY=-98.6625 StartZ=0 EndX=121.587 EndY=-98.6625 EndZ=0
    g19: GeomPoint X=128.588 Y=-105.662 Z=0
    g20: LineSegment StartX=140.637 StartY=-98.6625 StartZ=0 EndX=140.637 EndY=-112.663 EndZ=0
    g21: LineSegment StartX=140.637 StartY=-112.663 StartZ=0 EndX=154.637 EndY=-112.663 EndZ=0
    g22: LineSegment StartX=154.637 StartY=-112.663 StartZ=0 EndX=154.637 EndY=-98.6625 EndZ=0
    g23: LineSegment StartX=154.637 StartY=-98.6625 StartZ=0 EndX=140.637 EndY=-98.6625 EndZ=0
    g24: GeomPoint X=147.638 Y=-105.662 Z=0
    g25: LineSegment StartX=159.687 StartY=-98.6625 StartZ=0 EndX=159.687 EndY=-112.663 EndZ=0
    g26: LineSegment StartX=159.687 StartY=-112.663 StartZ=0 EndX=173.687 EndY=-112.663 EndZ=0
    g27: LineSegment StartX=173.687 StartY=-112.663 StartZ=0 EndX=173.687 EndY=-98.6625 EndZ=0
    g28: LineSegment StartX=173.687 StartY=-98.6625 StartZ=0 EndX=159.687 EndY=-98.6625 EndZ=0
    g29: GeomPoint X=166.688 Y=-105.662 Z=0
    g30: LineSegment StartX=178.737 StartY=-98.6625 StartZ=0 EndX=178.737 EndY=-112.663 EndZ=0
    g31: LineSegment StartX=178.737 StartY=-112.663 StartZ=0 EndX=192.737 EndY=-112.663 EndZ=0
    g32: LineSegment StartX=192.737 StartY=-112.663 StartZ=0 EndX=192.737 EndY=-98.6625 EndZ=0
    g33: LineSegment StartX=192.737 StartY=-98.6625 StartZ=0 EndX=178.737 EndY=-98.6625 EndZ=0
    g34: GeomPoint X=185.738 Y=-105.662 Z=0
    g35: LineSegment StartX=197.788 StartY=-98.6625 StartZ=0 EndX=197.788 EndY=-112.662 EndZ=0
    g36: LineSegment StartX=197.788 StartY=-112.662 StartZ=0 EndX=211.788 EndY=-112.662 EndZ=0
    g37: LineSegment StartX=211.788 StartY=-112.662 StartZ=0 EndX=211.788 EndY=-98.6625 EndZ=0
    g38: LineSegment StartX=211.788 StartY=-98.6625 StartZ=0 EndX=197.788 EndY=-98.6625 EndZ=0
    g39: GeomPoint X=204.787 Y=-105.662 Z=0
    g40: LineSegment StartX=216.838 StartY=-98.6625 StartZ=0 EndX=216.838 EndY=-112.662 EndZ=0
    g41: LineSegment StartX=216.838 StartY=-112.662 StartZ=0 EndX=230.838 EndY=-112.662 EndZ=0
    g42: LineSegment StartX=230.838 StartY=-112.662 StartZ=0 EndX=230.838 EndY=-98.6625 EndZ=0
    g43: LineSegment StartX=230.838 StartY=-98.6625 StartZ=0 EndX=216.838 EndY=-98.6625 EndZ=0
    g44: GeomPoint X=223.838 Y=-105.662 Z=0
    g45: LineSegment StartX=235.887 StartY=-98.6625 StartZ=0 EndX=235.887 EndY=-112.663 EndZ=0
    g46: LineSegment StartX=235.887 StartY=-112.663 StartZ=0 EndX=249.887 EndY=-112.663 EndZ=0
    g47: LineSegment StartX=249.887 StartY=-112.663 StartZ=0 EndX=249.887 EndY=-98.6625 EndZ=0
    g48: LineSegment StartX=249.887 StartY=-98.6625 StartZ=0 EndX=235.887 EndY=-98.6625 EndZ=0
    g49: GeomPoint X=242.888 Y=-105.662 Z=0
    g50: LineSegment StartX=254.938 StartY=-98.6625 StartZ=0 EndX=254.938 EndY=-112.662 EndZ=0
    g51: LineSegment StartX=254.938 StartY=-112.662 StartZ=0 EndX=268.938 EndY=-112.662 EndZ=0
    g52: LineSegment StartX=268.938 StartY=-112.662 StartZ=0 EndX=268.938 EndY=-98.6625 EndZ=0
    g53: LineSegment StartX=268.938 StartY=-98.6625 StartZ=0 EndX=254.938 EndY=-98.6625 EndZ=0
    g54: GeomPoint X=261.938 Y=-105.662 Z=0
    g55: LineSegment StartX=281.131 StartY=-98.6625 StartZ=0 EndX=281.131 EndY=-112.662 EndZ=0
    g56: LineSegment StartX=281.131 StartY=-112.662 StartZ=0 EndX=295.131 EndY=-112.662 EndZ=0
    g57: LineSegment StartX=295.131 StartY=-112.662 StartZ=0 EndX=295.131 EndY=-98.6625 EndZ=0
    g58: LineSegment StartX=295.131 StartY=-98.6625 StartZ=0 EndX=281.131 EndY=-98.6625 EndZ=0
    g59: GeomPoint X=288.131 Y=-105.662 Z=0
    g60: LineSegment StartX=312.087 StartY=-103.425 StartZ=0 EndX=312.087 EndY=-117.425 EndZ=0
    g61: LineSegment StartX=312.087 StartY=-117.425 StartZ=0 EndX=326.087 EndY=-117.425 EndZ=0
    g62: LineSegment StartX=326.087 StartY=-117.425 StartZ=0 EndX=326.087 EndY=-103.425 EndZ=0
    g63: LineSegment StartX=326.087 StartY=-103.425 StartZ=0 EndX=312.087 EndY=-103.425 EndZ=0
    g64: GeomPoint X=319.088 Y=-110.425 Z=0
    g65: LineSegment StartX=335.9 StartY=-98.6625 StartZ=0 EndX=335.9 EndY=-112.662 EndZ=0
    g66: LineSegment StartX=335.9 StartY=-112.662 StartZ=0 EndX=349.9 EndY=-112.662 EndZ=0
    g67: LineSegment StartX=349.9 StartY=-112.662 StartZ=0 EndX=349.9 EndY=-98.6625 EndZ=0
    g68: LineSegment StartX=349.9 StartY=-98.6625 StartZ=0 EndX=335.9 EndY=-98.6625 EndZ=0
    g69: GeomPoint X=342.9 Y=-105.662 Z=0
  constraints (182):
    c: Coincident(g0,g1)
    c: Coincident(g1,g2)
    c: Coincident(g2,g3)
    c: Coincident(g3,g0)
    c: Horizontal(g1)
    c: Horizontal(g3)
    c: Vertical(g0)
    c: Vertical(g2)
    c: Symmetric(g1,g0,g4)
    c: DistanceX(g3,g3) = 14
    c: DistanceY(g2,g2) = 14
    c: DistanceY(g4,g-1) = 105.662
    c: DistanceX(g-1,g4) = 59.5312
    c: Coincident(g5,g6)
    c: Coincident(g6,g7)
    c: Coincident(g7,g8)
    c: Coincident(g8,g5)
    c: Horizontal(g6)
    c: Horizontal(g8)
    c: Vertical(g5)
    c: Vertical(g7)
    c: Symmetric(g6,g5,g9)
    c: Coincident(g10,g11)
    c: Coincident(g11,g12)
    c: Coincident(g12,g13)
    c: Coincident(g13,g10)
    c: Horizontal(g11)
    c: Horizontal(g13)
    c: Vertical(g10)
    c: Vertical(g12)
    c: Symmetric(g11,g10,g14)
    c: Coincident(g15,g16)
    c: Coincident(g16,g17)
    c: Coincident(g17,g18)
    c: Coincident(g18,g15)
    c: Horizontal(g16)
    c: Horizontal(g18)
    c: Vertical(g15)
    c: Vertical(g17)
    c: Symmetric(g16,g15,g19)
    c: Coincident(g20,g21)
    c: Coincident(g21,g22)
    c: Coincident(g22,g23)
    c: Coincident(g23,g20)
    c: Horizontal(g21)
    c: Horizontal(g23)
    c: Vertical(g20)
    c: Vertical(g22)
    c: Symmetric(g21,g20,g24)
    c: Coincident(g25,g26)
    c: Coincident(g26,g27)
    c: Coincident(g27,g28)
    c: Coincident(g28,g25)
    c: Horizontal(g26)
    c: Horizontal(g28)
    c: Vertical(g25)
    c: Vertical(g27)
    c: Symmetric(g26,g25,g29)
    c: Coincident(g30,g31)
    c: Coincident(g31,g32)
    c: Coincident(g32,g33)
    c: Coincident(g33,g30)
    c: Horizontal(g31)
    c: Horizontal(g33)
    c: Vertical(g30)
    c: Vertical(g32)
    c: Symmetric(g31,g30,g34)
    c: Coincident(g35,g36)
    c: Coincident(g36,g37)
    c: Coincident(g37,g38)
    c: Coincident(g38,g35)
    c: Horizontal(g36)
    c: Horizontal(g38)
    c: Vertical(g35)
    c: Vertical(g37)
    c: Symmetric(g36,g35,g39)
    c: Coincident(g40,g41)
    c: Coincident(g41,g42)
    c: Coincident(g42,g43)
    c: Coincident(g43,g40)
    c: Horizontal(g41)
    c: Horizontal(g43)
    c: Vertical(g40)
    c: Vertical(g42)
    c: Symmetric(g41,g40,g44)
    c: Coincident(g45,g46)
    c: Coincident(g46,g47)
    c: Coincident(g47,g48)
    c: Coincident(g48,g45)
    c: Horizontal(g46)
    c: Horizontal(g48)
    c: Vertical(g45)
    c: Vertical(g47)
    c: Symmetric(g46,g45,g49)
    c: Coincident(g50,g51)
    c: Coincident(g51,g52)
    c: Coincident(g52,g53)
    c: Coincident(g53,g50)
    c: Horizontal(g51)
    c: Horizontal(g53)
    c: Vertical(g50)
    c: Vertical(g52)
    c: Symmetric(g51,g50,g54)
    c: Coincident(g55,g56)
    c: Coincident(g56,g57)
    c: Coincident(g57,g58)
    c: Coincident(g58,g55)
    c: Horizontal(g56)
    c: Horizontal(g58)
    c: Vertical(g55)
    c: Vertical(g57)
    c: Symmetric(g56,g55,g59)
    c: Coincident(g60,g61)
    c: Coincident(g61,g62)
    c: Coincident(g62,g63)
    c: Coincident(g63,g60)
    c: Horizontal(g61)
    c: Horizontal(g63)
    c: Vertical(g60)
    c: Vertical(g62)
    c: Symmetric(g61,g60,g64)
    c: Coincident(g65,g66)
    c: Coincident(g66,g67)
    c: Coincident(g67,g68)
    c: Coincident(g68,g65)
    c: Horizontal(g66)
    c: Horizontal(g68)
    c: Vertical(g65)
    c: Vertical(g67)
    c: Symmetric(g66,g65,g69)
    c: DistanceX(g8,g8) = 14
    c: DistanceX(g13,g13) = 14
    c: DistanceX(g18,g18) = 14
    c: DistanceX(g23,g23) = 14
    c: DistanceX(g28,g28) = 14
    c: DistanceX(g33,g33) = 14
    c: DistanceX(g38,g38) = 14
    c: DistanceX(g43,g43) = 14
    c: DistanceX(g48,g48) = 14
    c: DistanceX(g53,g53) = 14
    c: DistanceX(g58,g58) = 14
    c: DistanceX(g63,g63) = 14
    c: DistanceX(g68,g68) = 14
    c: DistanceY(g7,g7) = 14
    c: DistanceY(g12,g12) = 14
    c: DistanceY(g17,g17) = 14
    c: DistanceY(g22,g22) = 14
    c: DistanceY(g27,g27) = 14
    c: DistanceY(g32,g32) = 14
    c: DistanceY(g37,g37) = 14
    c: DistanceY(g42,g42) = 14
    c: DistanceY(g47,g47) = 14
    c: DistanceY(g52,g52) = 14
    c: DistanceY(g57,g57) = 14
    c: DistanceY(g62,g62) = 14
    c: DistanceY(g67,g67) = 14
    c: DistanceX(g4,g9) = 30.9563
    c: Horizontal(g4,g9)
    c: Horizontal(g9,g14)
    c: Horizontal(g14,g19)
    c: Horizontal(g19,g24)
    c: Horizontal(g24,g29)
    c: Horizontal(g29,g34)
    c: Horizontal(g34,g39)
    c: Horizontal(g39,g44)
    c: Horizontal(g44,g49)
    c: Horizontal(g49,g54)
    c: Horizontal(g54,g59)
    c: DistanceX(g9,g14) = 19.05
    c: DistanceX(g14,g19) = 19.05
    c: DistanceX(g19,g24) = 19.05
    c: DistanceX(g29,g34) = 19.05
    c: DistanceX(g34,g39) = 19.05
    c: DistanceX(g39,g44) = 19.05
    c: DistanceX(g49,g54) = 19.05
    c: DistanceX(g54,g59) = 26.1938
    c: DistanceX(g59,g64) = 30.9563
    c: DistanceX(g24,g29) = 19.05
    c: DistanceX(g44,g49) = 19.05
    c: DistanceX(g64,g69) = 23.8125
    c: Horizontal(g59,g69)
    c: DistanceY(g64,g59) = 4.7625
FEATURE [PartDesign::Pocket] Pocket003
  BaseFeature = -> Pocket002
  Direction = (0,0,-1)
  Length = 5
  Length2 = 5
  Profile = -> Sketch004
  ReferenceAxis = -> Sketch004 [N_Axis]
  Type = 0
FEATURE [Sketcher::SketchObject] Sketch006
  AttachmentOffset = pos=(0,0,4.1) rot=(0,0,1;0rad)
  FullyConstrained = true
  MapMode = 5
  Placement = pos=(0,0,4.1) rot=(0,0,1;0rad)
  Support = -> [XY_Plane097]
  expr: Constraints[100] = Spreadsheet.switch_hole
  expr: Constraints[101] = Spreadsheet.u * 1.25
  expr: Constraints[107] = Spreadsheet.u * 1.25
  expr: Constraints[108] = Spreadsheet.u * (1.25 / 2 + 6.25 / 2)
  expr: Constraints[109] = Spreadsheet.u
  expr: Constraints[10] = Spreadsheet.switch_hole
  expr: Constraints[110] = Spreadsheet.u
  expr: Constraints[111] = Spreadsheet.u * (1 + 0.25)
  expr: Constraints[112] = Spreadsheet.u
  expr: Constraints[113] = Spreadsheet.u * 0.25
  expr: Constraints[114] = Spreadsheet.u * (6.25 / 2 + 0.5)
  expr: Constraints[11] = Spreadsheet.PCB_width - Spreadsheet.u * 0.75
  expr: Constraints[127] = Spreadsheet.switch_hole
  expr: Constraints[128] = Spreadsheet.switch_hole
  expr: Constraints[129] = Spreadsheet.u
  expr: Constraints[12] = Spreadsheet.u * (2 + 1.25 / 2)
  expr: Constraints[85] = Spreadsheet.switch_hole
  expr: Constraints[86] = Spreadsheet.switch_hole
  expr: Constraints[87] = Spreadsheet.switch_hole
  expr: Constraints[88] = Spreadsheet.switch_hole
  expr: Constraints[89] = Spreadsheet.switch_hole
  expr: Constraints[90] = Spreadsheet.switch_hole
  expr: Constraints[91] = Spreadsheet.switch_hole
  expr: Constraints[92] = Spreadsheet.switch_hole
  expr: Constraints[93] = Spreadsheet.switch_hole
  expr: Constraints[94] = Spreadsheet.switch_hole
  expr: Constraints[95] = Spreadsheet.switch_hole
  expr: Constraints[96] = Spreadsheet.switch_hole
  expr: Constraints[97] = Spreadsheet.switch_hole
  expr: Constraints[98] = Spreadsheet.switch_hole
  expr: Constraints[99] = Spreadsheet.switch_hole
  expr: Constraints[9] = Spreadsheet.switch_hole
  sketch-geometry (50):
    g0: LineSegment StartX=43.0063 StartY=-117.712 StartZ=0 EndX=43.0063 EndY=-131.712 EndZ=0
    g1: LineSegment StartX=43.0063 StartY=-131.712 StartZ=0 EndX=57.0063 EndY=-131.712 EndZ=0
    g2: LineSegment StartX=57.0063 StartY=-131.712 StartZ=0 EndX=57.0063 EndY=-117.712 EndZ=0
    g3: LineSegment StartX=57.0063 StartY=-117.712 StartZ=0 EndX=43.0063 EndY=-117.712 EndZ=0
    g4: GeomPoint X=50.0063 Y=-124.713 Z=0
    g5: LineSegment StartX=66.8188 StartY=-117.712 StartZ=0 EndX=66.8188 EndY=-131.712 EndZ=0
    g6: LineSegment StartX=66.8188 StartY=-131.712 StartZ=0 EndX=80.8188 EndY=-131.712 EndZ=0
    g7: LineSegment StartX=80.8188 StartY=-131.712 StartZ=0 EndX=80.8188 EndY=-117.712 EndZ=0
    g8: LineSegment StartX=80.8188 StartY=-117.712 StartZ=0 EndX=66.8188 EndY=-117.712 EndZ=0
    g9: GeomPoint X=73.8187 Y=-124.713 Z=0
    g10: LineSegment StartX=90.6312 StartY=-117.713 StartZ=0 EndX=90.6312 EndY=-131.713 EndZ=0
    g11: LineSegment StartX=90.6312 StartY=-131.713 StartZ=0 EndX=104.631 EndY=-131.713 EndZ=0
    g12: LineSegment StartX=104.631 StartY=-131.713 StartZ=0 EndX=104.631 EndY=-117.713 EndZ=0
    g13: LineSegment StartX=104.631 StartY=-117.713 StartZ=0 EndX=90.6312 EndY=-117.713 EndZ=0
    g14: GeomPoint X=97.6312 Y=-124.713 Z=0
    g15: LineSegment StartX=162.069 StartY=-117.713 StartZ=0 EndX=162.069 EndY=-131.713 EndZ=0
    g16: LineSegment StartX=162.069 StartY=-131.713 StartZ=0 EndX=176.069 EndY=-131.713 EndZ=0
    g17: LineSegment StartX=176.069 StartY=-131.713 StartZ=0 EndX=176.069 EndY=-117.713 EndZ=0
    g18: LineSegment StartX=176.069 StartY=-117.713 StartZ=0 EndX=162.069 EndY=-117.713 EndZ=0
    g19: GeomPoint X=169.069 Y=-124.713 Z=0
    g20: LineSegment StartX=231.125 StartY=-117.712 StartZ=0 EndX=231.125 EndY=-131.713 EndZ=0
    g21: LineSegment StartX=231.125 StartY=-131.713 StartZ=0 EndX=245.125 EndY=-131.713 EndZ=0
    g22: LineSegment StartX=245.125 StartY=-131.713 StartZ=0 EndX=245.125 EndY=-117.712 EndZ=0
    g23: LineSegment StartX=245.125 StartY=-117.712 StartZ=0 EndX=231.125 EndY=-117.712 EndZ=0
    g24: GeomPoint X=238.125 Y=-124.713 Z=0
    g25: LineSegment StartX=250.175 StartY=-117.713 StartZ=0 EndX=250.175 EndY=-131.713 EndZ=0
    g26: LineSegment StartX=250.175 StartY=-131.713 StartZ=0 EndX=264.175 EndY=-131.713 EndZ=0
    g27: LineSegment StartX=264.175 StartY=-131.713 StartZ=0 EndX=264.175 EndY=-117.713 EndZ=0
    g28: LineSegment StartX=264.175 StartY=-117.713 StartZ=0 EndX=250.175 EndY=-117.713 EndZ=0
    g29: GeomPoint X=257.175 Y=-124.713 Z=0
    g30: LineSegment StartX=269.225 StartY=-117.713 StartZ=0 EndX=269.225 EndY=-131.713 EndZ=0
    g31: LineSegment StartX=269.225 StartY=-131.713 StartZ=0 EndX=283.225 EndY=-131.713 EndZ=0
    g32: LineSegment StartX=283.225 StartY=-131.713 StartZ=0 EndX=283.225 EndY=-117.713 EndZ=0
    g33: LineSegment StartX=283.225 StartY=-117.713 StartZ=0 EndX=269.225 EndY=-117.713 EndZ=0
    g34: GeomPoint X=276.225 Y=-124.713 Z=0
    g35: LineSegment StartX=293.037 StartY=-122.475 StartZ=0 EndX=293.037 EndY=-136.475 EndZ=0
    g36: LineSegment StartX=293.037 StartY=-136.475 StartZ=0 EndX=307.037 EndY=-136.475 EndZ=0
    g37: LineSegment StartX=307.037 StartY=-136.475 StartZ=0 EndX=307.037 EndY=-122.475 EndZ=0
    g38: LineSegment StartX=307.037 StartY=-122.475 StartZ=0 EndX=293.037 EndY=-122.475 EndZ=0
    g39: GeomPoint X=300.038 Y=-129.475 Z=0
    g40: LineSegment StartX=312.088 StartY=-122.475 StartZ=0 EndX=312.088 EndY=-136.475 EndZ=0
    g41: LineSegment StartX=312.088 StartY=-136.475 StartZ=0 EndX=326.088 EndY=-136.475 EndZ=0
    g42: LineSegment StartX=326.088 StartY=-136.475 StartZ=0 EndX=326.088 EndY=-122.475 EndZ=0
    g43: LineSegment StartX=326.088 StartY=-122.475 StartZ=0 EndX=312.088 EndY=-122.475 EndZ=0
    g44: GeomPoint X=319.088 Y=-129.475 Z=0
    g45: LineSegment StartX=331.138 StartY=-122.475 StartZ=0 EndX=331.138 EndY=-136.475 EndZ=0
    g46: LineSegment StartX=331.138 StartY=-136.475 StartZ=0 EndX=345.138 EndY=-136.475 EndZ=0
    g47: LineSegment StartX=345.138 StartY=-136.475 StartZ=0 EndX=345.138 EndY=-122.475 EndZ=0
    g48: LineSegment StartX=345.138 StartY=-122.475 StartZ=0 EndX=331.138 EndY=-122.475 EndZ=0
    g49: GeomPoint X=338.137 Y=-129.475 Z=0
  constraints (130):
    c: Coincident(g0,g1)
    c: Coincident(g1,g2)
    c: Coincident(g2,g3)
    c: Coincident(g3,g0)
    c: Horizontal(g1)
    c: Horizontal(g3)
    c: Vertical(g0)
    c: Vertical(g2)
    c: Symmetric(g1,g0,g4)
    c: DistanceX(g3,g3) = 14
    c: DistanceY(g2,g2) = 14
    c: DistanceY(g4,g-1) = 124.713
    c: DistanceX(g-1,g4) = 50.0063
    c: Coincident(g5,g6)
    c: Coincident(g6,g7)
    c: Coincident(g7,g8)
    c: Coincident(g8,g5)
    c: Horizontal(g6)
    c: Horizontal(g8)
    c: Vertical(g5)
    c: Vertical(g7)
    c: Symmetric(g6,g5,g9)
    c: Coincident(g10,g11)
    c: Coincident(g11,g12)
    c: Coincident(g12,g13)
    c: Coincident(g13,g10)
    c: Horizontal(g11)
    c: Horizontal(g13)
    c: Vertical(g10)
    c: Vertical(g12)
    c: Symmetric(g11,g10,g14)
    c: Coincident(g15,g16)
    c: Coincident(g16,g17)
    c: Coincident(g17,g18)
    c: Coincident(g18,g15)
    c: Horizontal(g16)
    c: Horizontal(g18)
    c: Vertical(g15)
    c: Vertical(g17)
    c: Symmetric(g16,g15,g19)
    c: Coincident(g20,g21)
    c: Coincident(g21,g22)
    c: Coincident(g22,g23)
    c: Coincident(g23,g20)
    c: Horizontal(g21)
    c: Horizontal(g23)
    c: Vertical(g20)
    c: Vertical(g22)
    c: Symmetric(g21,g20,g24)
    c: Coincident(g25,g26)
    c: Coincident(g26,g27)
    c: Coincident(g27,g28)
    c: Coincident(g28,g25)
    c: Horizontal(g26)
    c: Horizontal(g28)
    c: Vertical(g25)
    c: Vertical(g27)
    c: Symmetric(g26,g25,g29)
    c: Coincident(g30,g31)
    c: Coincident(g31,g32)
    c: Coincident(g32,g33)
    c: Coincident(g33,g30)
    c: Horizontal(g31)
    c: Horizontal(g33)
    c: Vertical(g30)
    c: Vertical(g32)
    c: Symmetric(g31,g30,g34)
    c: Coincident(g35,g36)
    c: Coincident(g36,g37)
    c: Coincident(g37,g38)
    c: Coincident(g38,g35)
    c: Horizontal(g36)
    c: Horizontal(g38)
    c: Vertical(g35)
    c: Vertical(g37)
    c: Symmetric(g36,g35,g39)
    c: Coincident(g40,g41)
    c: Coincident(g41,g42)
    c: Coincident(g42,g43)
    c: Coincident(g43,g40)
    c: Horizontal(g41)
    c: Horizontal(g43)
    c: Vertical(g40)
    c: Vertical(g42)
    c: Symmetric(g41,g40,g44)
    c: DistanceX(g8,g8) = 14
    c: DistanceX(g13,g13) = 14
    c: DistanceX(g18,g18) = 14
    c: DistanceX(g23,g23) = 14
    c: DistanceX(g28,g28) = 14
    c: DistanceX(g33,g33) = 14
    c: DistanceX(g38,g38) = 14
    c: DistanceX(g43,g43) = 14
    c: DistanceY(g7,g7) = 14
    c: DistanceY(g12,g12) = 14
    c: DistanceY(g17,g17) = 14
    c: DistanceY(g22,g22) = 14
    c: DistanceY(g27,g27) = 14
    c: DistanceY(g32,g32) = 14
    c: DistanceY(g37,g37) = 14
    c: DistanceY(g42,g42) = 14
    c: DistanceX(g4,g9) = 23.8125
    c: Horizontal(g4,g9)
    c: Horizontal(g9,g14)
    c: Horizontal(g14,g19)
    c: Horizontal(g24,g29)
    c: Horizontal(g29,g34)
    c: DistanceX(g9,g14) = 23.8125
    c: DistanceX(g14,g19) = 71.4375
    c: DistanceX(g24,g29) = 19.05
    c: DistanceX(g29,g34) = 19.05
    c: DistanceX(g34,g39) = 23.8125
    c: DistanceX(g39,g44) = 19.05
    c: DistanceY(g39,g34) = 4.7625
    c: DistanceX(g19,g24) = 69.0563
    c: Horizontal(g19,g24)
    c: Horizontal(g39,g44)
    c: Coincident(g45,g46)
    c: Coincident(g46,g47)
    c: Coincident(g47,g48)
    c: Coincident(g48,g45)
    c: Horizontal(g46)
    c: Horizontal(g48)
    c: Vertical(g45)
    c: Vertical(g47)
    c: Symmetric(g46,g45,g49)
    c: Horizontal(g44,g49)
    c: DistanceX(g48,g48) = 14
    c: DistanceY(g47,g47) = 14
    c: DistanceX(g44,g49) = 19.05
FEATURE [PartDesign::Pocket] Pocket004
  BaseFeature = -> Pocket003
  Direction = (0,0,-1)
  Length = 5
  Length2 = 5
  Profile = -> Sketch005
  ReferenceAxis = -> Sketch005 [N_Axis]
  Type = 0
FEATURE [PartDesign::Pocket] Pocket005
  BaseFeature = -> Pocket004
  Direction = (0,0,-1)
  Length = 5
  Length2 = 5
  Profile = -> Sketch006
  ReferenceAxis = -> Sketch006 [N_Axis]
  Type = 0
FEATURE [Sketcher::SketchObject] Sketch007
  AttachmentOffset = pos=(0,0,4.1) rot=(0,0,1;0rad)
  FullyConstrained = true
  MapMode = 5
  Placement = pos=(0,0,4.1) rot=(0,0,1;0rad)
  Support = -> [XY_Plane097]
  expr: Constraints[11] = Spreadsheet.encoder_hole_width
  expr: Constraints[12] = Spreadsheet.encoder_hole_width
  expr: Constraints[13] = Spreadsheet.u
  expr: Constraints[14] = Spreadsheet.encoder_hole_length
  expr: Constraints[15] = Spreadsheet.encoder_hole_length
  expr: Constraints[16] = Spreadsheet.u * 0.5
  expr: Constraints[17] = Spreadsheet.PCB_width - Spreadsheet.u * 6
  expr: Constraints[22] = Spreadsheet.encoder_fillet_rad
  expr: Constraints[51] = Spreadsheet.encoder_fillet_rad
  expr: Constraints[52] = Spreadsheet.encoder_fillet_rad
  expr: Constraints[53] = Spreadsheet.encoder_fillet_rad
  expr: Constraints[54] = Spreadsheet.encoder_fillet_rad
  expr: Constraints[55] = Spreadsheet.encoder_fillet_rad
  expr: Constraints[56] = Spreadsheet.encoder_fillet_rad
  expr: Constraints[57] = Spreadsheet.encoder_fillet_rad
  sketch-geometry (26):
    g0: LineSegment StartX=22.075 StartY=-17.95 StartZ=0 EndX=22.075 EndY=-31.45 EndZ=0
    g1: LineSegment StartX=23.325 StartY=-32.7 StartZ=0 EndX=33.825 EndY=-32.7 EndZ=0
    g2: LineSegment StartX=35.075 StartY=-31.45 StartZ=0 EndX=35.075 EndY=-17.95 EndZ=0
    g3: LineSegment StartX=33.825 StartY=-16.7 StartZ=0 EndX=23.325 EndY=-16.7 EndZ=0
    g4: GeomPoint X=28.575 Y=-24.7 Z=0
    g5: LineSegment StartX=3.025 StartY=-17.95 StartZ=0 EndX=3.025 EndY=-31.45 EndZ=0
    g6: LineSegment StartX=4.275 StartY=-32.7 StartZ=0 EndX=14.775 EndY=-32.7 EndZ=0
    g7: LineSegment StartX=16.025 StartY=-31.45 StartZ=0 EndX=16.025 EndY=-17.95 EndZ=0
    g8: LineSegment StartX=14.775 StartY=-16.7 StartZ=0 EndX=4.275 EndY=-16.7 EndZ=0
    g9: GeomPoint X=9.525 Y=-24.7 Z=0
    g10: ArcOfCircle CenterX=14.775 CenterY=-31.45 CenterZ=0 NormalX=0 NormalY=0 NormalZ=1 AngleXU=0 Radius=1.25 StartAngle=4.71239 EndAngle=6.28319
    g11: GeomPoint X=16.025 Y=-32.7 Z=0
    g12: ArcOfCircle CenterX=14.775 CenterY=-17.95 CenterZ=0 NormalX=0 NormalY=0 NormalZ=1 AngleXU=0 Radius=1.25 StartAngle=0 EndAngle=1.5708
    g13: GeomPoint X=16.025 Y=-16.7 Z=0
    g14: ArcOfCircle CenterX=4.275 CenterY=-17.95 CenterZ=0 NormalX=0 NormalY=0 NormalZ=1 AngleXU=0 Radius=1.25 StartAngle=1.5708 EndAngle=3.14159
    g15: GeomPoint X=3.025 Y=-16.7 Z=0
    g16: ArcOfCircle CenterX=4.275 CenterY=-31.45 CenterZ=0 NormalX=0 NormalY=0 NormalZ=1 AngleXU=0 Radius=1.25 StartAngle=3.14159 EndAngle=4.71239
    g17: GeomPoint X=3.025 Y=-32.7 Z=0
    g18: ArcOfCircle CenterX=23.325 CenterY=-31.45 CenterZ=0 NormalX=0 NormalY=0 NormalZ=1 AngleXU=0 Radius=1.25 StartAngle=3.14159 EndAngle=4.71239
    g19: GeomPoint X=22.075 Y=-32.7 Z=0
    g20: ArcOfCircle CenterX=33.825 CenterY=-31.45 CenterZ=0 NormalX=0 NormalY=0 NormalZ=1 AngleXU=0 Radius=1.25 StartAngle=4.71239 EndAngle=6.28319
    g21: GeomPoint X=35.075 Y=-32.7 Z=0
    g22: ArcOfCircle CenterX=33.825 CenterY=-17.95 CenterZ=0 NormalX=0 NormalY=0 NormalZ=1 AngleXU=0 Radius=1.25 StartAngle=1.2e-15 EndAngle=1.5708
    g23: GeomPoint X=35.075 Y=-16.7 Z=0
    g24: ArcOfCircle CenterX=23.325 CenterY=-17.95 CenterZ=0 NormalX=0 NormalY=0 NormalZ=1 AngleXU=0 Radius=1.25 StartAngle=1.5708 EndAngle=3.14159
    g25: GeomPoint X=22.075 Y=-16.7 Z=0
  constraints (58):
    c: Horizontal(g1)
    c: Horizontal(g3)
    c: Vertical(g0)
    c: Vertical(g2)
    c: Symmetric(g21,g25,g4)
    c: Horizontal(g6)
    c: Horizontal(g8)
    c: Vertical(g5)
    c: Vertical(g7)
    c: Symmetric(g11,g15,g9)
    c: Horizontal(g9,g4)
    c: DistanceX(g15,g13) = 13
    c: DistanceX(g25,g23) = 13
    c: DistanceX(g9,g4) = 19.05
    c: DistanceY(g11,g13) = 16
    c: DistanceY(g21,g23) = 16
    c: DistanceX(g-1,g9) = 9.525
    c: DistanceY(g9,g-1) = 24.7
    c: PointOnObject(g11,g6)
    c: PointOnObject(g11,g7)
    c: Tangent(g6,g10) = -1.5708
    c: Tangent(g7,g10) = -1.5708
    c: Radius(g10) = 1.25
    c: PointOnObject(g13,g7)
    c: PointOnObject(g13,g8)
    c: Tangent(g7,g12) = -1.5708
    c: Tangent(g8,g12) = -1.5708
    c: PointOnObject(g15,g5)
    c: PointOnObject(g15,g8)
    c: Tangent(g5,g14) = -1.5708
    c: Tangent(g8,g14) = -1.5708
    c: PointOnObject(g17,g5)
    c: PointOnObject(g17,g6)
    c: Tangent(g5,g16) = -1.5708
    c: Tangent(g6,g16) = -1.5708
    c: PointOnObject(g19,g0)
    c: PointOnObject(g19,g1)
    c: Tangent(g0,g18) = -1.5708
    c: Tangent(g1,g18) = -1.5708
    c: PointOnObject(g21,g1)
    c: PointOnObject(g21,g2)
    c: Tangent(g1,g20) = -1.5708
    c: Tangent(g2,g20) = -1.5708
    c: PointOnObject(g23,g2)
    c: PointOnObject(g23,g3)
    c: Tangent(g2,g22) = -1.5708
    c: Tangent(g3,g22) = -1.5708
    c: PointOnObject(g25,g0)
    c: PointOnObject(g25,g3)
    c: Tangent(g0,g24) = -1.5708
    c: Tangent(g3,g24) = -1.5708
    c: Radius(g12) = 1.25
    c: Radius(g14) = 1.25
    c: Radius(g16) = 1.25
    c: Radius(g18) = 1.25
    c: Radius(g20) = 1.25
    c: Radius(g22) = 1.25
    c: Radius(g24) = 1.25
FEATURE [PartDesign::Pocket] Pocket006
  BaseFeature = -> Pocket005
  Direction = (0,0,-1)
  Length = 5
  Length2 = 5
  Profile = -> Sketch007
  ReferenceAxis = -> Sketch007 [N_Axis]
  Type = 0
FEATURE [Sketcher::SketchObject] Sketch008
  AttachmentOffset = pos=(0,0,4.1) rot=(0,0,1;0rad)
  FullyConstrained = true
  MapMode = 5
  Placement = pos=(0,0,4.1) rot=(0,0,1;0rad)
  Support = -> [XY_Plane097]
  expr: Constraints[5] = Spreadsheet.screen_module_width + 1
  expr: Constraints[6] = Spreadsheet.screen_module_length + 1
  expr: Constraints[7] = Spreadsheet.PCB_width - Spreadsheet.u * 3.75
  expr: Constraints[8] = Spreadsheet.u * 1
  sketch-geometry (13):
    g0: LineSegment StartX=4.9 StartY=-42.9625 StartZ=0 EndX=4.9 EndY=-92.1625 EndZ=0
    g1: LineSegment StartX=6.4 StartY=-93.6625 StartZ=0 EndX=31.7 EndY=-93.6625 EndZ=0
    g2: LineSegment StartX=33.2 StartY=-92.1625 StartZ=0 EndX=33.2 EndY=-42.9625 EndZ=0
    g3: LineSegment StartX=31.7 StartY=-41.4625 StartZ=0 EndX=6.4 EndY=-41.4625 EndZ=0
    g4: GeomPoint X=19.05 Y=-67.5625 Z=0
    g5: ArcOfCircle CenterX=31.7 CenterY=-42.9625 CenterZ=0 NormalX=0 NormalY=0 NormalZ=1 AngleXU=0 Radius=1.5 StartAngle=8e-16 EndAngle=1.5708
    g6: GeomPoint X=33.2 Y=-41.4625 Z=0
    g7: ArcOfCircle CenterX=6.4 CenterY=-42.9625 CenterZ=0 NormalX=0 NormalY=0 NormalZ=1 AngleXU=0 Radius=1.5 StartAngle=1.5708 EndAngle=3.14159
    g8: GeomPoint X=4.9 Y=-41.4625 Z=0
    g9: ArcOfCircle CenterX=6.4 CenterY=-92.1625 CenterZ=0 NormalX=0 NormalY=0 NormalZ=1 AngleXU=0 Radius=1.5 StartAngle=3.14159 EndAngle=4.71239
    g10: GeomPoint X=4.9 Y=-93.6625 Z=0
    g11: ArcOfCircle CenterX=31.7 CenterY=-92.1625 CenterZ=0 NormalX=0 NormalY=0 NormalZ=1 AngleXU=0 Radius=1.5 StartAngle=4.71239 EndAngle=6.28319
    g12: GeomPoint X=33.2 Y=-93.6625 Z=0
  constraints (29):
    c: Horizontal(g1)
    c: Horizontal(g3)
    c: Vertical(g0)
    c: Vertical(g2)
    c: Symmetric(g12,g8,g4)
    c: DistanceX(g8,g6) = 28.3
    c: DistanceY(g12,g6) = 52.2
    c: DistanceY(g4,g-1) = 67.5625
    c: DistanceX(g-1,g4) = 19.05
    c: PointOnObject(g6,g2)
    c: PointOnObject(g6,g3)
    c: Tangent(g2,g5) = -1.5708
    c: Tangent(g3,g5) = -1.5708
    c: Radius(g5) = 1.5
    c: PointOnObject(g8,g0)
    c: PointOnObject(g8,g3)
    c: Tangent(g0,g7) = -1.5708
    c: Tangent(g3,g7) = -1.5708
    c: PointOnObject(g10,g0)
    c: PointOnObject(g10,g1)
    c: Tangent(g0,g9) = -1.5708
    c: Tangent(g1,g9) = -1.5708
    c: PointOnObject(g12,g1)
    c: PointOnObject(g12,g2)
    c: Tangent(g1,g11) = -1.5708
    c: Tangent(g2,g11) = -1.5708
    c: Radius(g11) = 1.5
    c: Radius(g9) = 1.5
    c: Radius(g7) = 1.5
FEATURE [PartDesign::Pocket] Pocket007
  BaseFeature = -> Pocket006
  Direction = (0,0,-1)
  Length = 5
  Length2 = 5
  Profile = -> Sketch008
  ReferenceAxis = -> Sketch008 [N_Axis]
  Type = 0
FEATURE [Sketcher::SketchObject] Sketch009
  AttachmentOffset = pos=(0,0,4.1) rot=(0,0,1;0rad)
  FullyConstrained = true
  MapMode = 5
  Placement = pos=(0,0,4.1) rot=(0,0,1;0rad)
  Support = -> [XY_Plane097]
  expr: Constraints[47] = Spreadsheet.tact_button_size + 1
  expr: Constraints[48] = Spreadsheet.PCB_width - Spreadsheet.u * 1.75
  expr: Constraints[49] = Spreadsheet.u
  expr: Constraints[50] = Spreadsheet.u
  expr: Constraints[51] = Spreadsheet.u * 0.5
  sketch-geometry (20):
    g0: LineSegment StartX=6.025 StartY=-121.213 StartZ=0 EndX=6.025 EndY=-128.212 EndZ=0
    g1: LineSegment StartX=6.025 StartY=-128.212 StartZ=0 EndX=13.025 EndY=-128.212 EndZ=0
    g2: LineSegment StartX=13.025 StartY=-128.212 StartZ=0 EndX=13.025 EndY=-121.213 EndZ=0
    g3: LineSegment StartX=13.025 StartY=-121.213 StartZ=0 EndX=6.025 EndY=-121.213 EndZ=0
    g4: GeomPoint X=9.525 Y=-124.712 Z=0
    g5: LineSegment StartX=25.075 StartY=-121.213 StartZ=0 EndX=25.075 EndY=-128.212 EndZ=0
    g6: LineSegment StartX=25.075 StartY=-128.212 StartZ=0 EndX=32.075 EndY=-128.212 EndZ=0
    g7: LineSegment StartX=32.075 StartY=-128.212 StartZ=0 EndX=32.075 EndY=-121.213 EndZ=0
    g8: LineSegment StartX=32.075 StartY=-121.213 StartZ=0 EndX=25.075 EndY=-121.213 EndZ=0
    g9: GeomPoint X=28.575 Y=-124.712 Z=0
    g10: LineSegment StartX=25.075 StartY=-102.163 StartZ=0 EndX=25.075 EndY=-109.162 EndZ=0
    g11: LineSegment StartX=25.075 StartY=-109.162 StartZ=0 EndX=32.075 EndY=-109.162 EndZ=0
    g12: LineSegment StartX=32.075 StartY=-109.162 StartZ=0 EndX=32.075 EndY=-102.163 EndZ=0
    g13: LineSegment StartX=32.075 StartY=-102.163 StartZ=0 EndX=25.075 EndY=-102.163 EndZ=0
    g14: GeomPoint X=28.575 Y=-105.662 Z=0
    g15: LineSegment StartX=6.025 StartY=-102.162 StartZ=0 EndX=6.025 EndY=-109.162 EndZ=0
    g16: LineSegment StartX=6.025 StartY=-109.162 StartZ=0 EndX=13.025 EndY=-109.162 EndZ=0
    g17: LineSegment StartX=13.025 StartY=-109.162 StartZ=0 EndX=13.025 EndY=-102.162 EndZ=0
    g18: LineSegment StartX=13.025 StartY=-102.162 StartZ=0 EndX=6.025 EndY=-102.162 EndZ=0
    g19: GeomPoint X=9.525 Y=-105.662 Z=0
  constraints (52):
    c: Coincident(g0,g1)
    c: Coincident(g1,g2)
    c: Coincident(g2,g3)
    c: Coincident(g3,g0)
    c: Horizontal(g1)
    c: Horizontal(g3)
    c: Vertical(g0)
    c: Vertical(g2)
    c: Symmetric(g1,g0,g4)
    c: Coincident(g5,g6)
    c: Coincident(g6,g7)
    c: Coincident(g7,g8)
    c: Coincident(g8,g5)
    c: Horizontal(g6)
    c: Horizontal(g8)
    c: Vertical(g5)
    c: Vertical(g7)
    c: Symmetric(g6,g5,g9)
    c: Coincident(g10,g11)
    c: Coincident(g11,g12)
    c: Coincident(g12,g13)
    c: Coincident(g13,g10)
    c: Horizontal(g11)
    c: Horizontal(g13)
    c: Vertical(g10)
    c: Vertical(g12)
    c: Symmetric(g11,g10,g14)
    c: Coincident(g15,g16)
    c: Coincident(g16,g17)
    c: Coincident(g17,g18)
    c: Coincident(g18,g15)
    c: Horizontal(g16)
    c: Horizontal(g18)
    c: Vertical(g15)
    c: Vertical(g17)
    c: Symmetric(g16,g15,g19)
    c: Equal(g17,g18)
    c: Equal(g12,g13)
    c: Equal(g7,g8)
    c: Equal(g2,g3)
    c: Equal(g3,g18)
    c: Equal(g8,g13)
    c: Equal(g13,g18)
    c: Horizontal(g19,g14)
    c: Horizontal(g4,g9)
    c: Vertical(g19,g4)
    c: Vertical(g9,g14)
    c: DistanceX(g18,g18) = 7
    c: DistanceY(g19,g-1) = 105.662
    c: DistanceY(g4,g19) = 19.05
    c: DistanceX(g19,g14) = 19.05
    c: DistanceX(g-1,g19) = 9.525
FEATURE [PartDesign::Pocket] Pocket008
  BaseFeature = -> Pocket007
  Direction = (0,0,-1)
  Length = 5
  Length2 = 5
  Profile = -> Sketch009
  ReferenceAxis = -> Sketch009 [N_Axis]
  Type = 0
FEATURE [Sketcher::SketchObject] Sketch010
  AttachmentOffset = pos=(0,0,4.1) rot=(0,0,1;0rad)
  FullyConstrained = true
  MapMode = 5
  Placement = pos=(0,0,4.1) rot=(0,0,1;0rad)
  Support = -> [XY_Plane097]
  expr: Constraints[0] = Spreadsheet.u * (2 + 3 * 1.25 + 6.25 / 2)
  expr: Constraints[1] = Spreadsheet.PCB_width - Spreadsheet.u * 0.75
  expr: Constraints[26] = Spreadsheet.stab_length + 0.2
  expr: Constraints[37] = Spreadsheet.stab_width + 0.2
  expr: Constraints[45] = (Spreadsheet.stab_width + 0.2) / 2 - 2
  expr: Constraints[59] = (Spreadsheet.stab_width + 0.2) / 2 - 2
  sketch-geometry (24):
    g0: GeomPoint X=169.069 Y=-124.713 Z=0
    g1: LineSegment StartX=116.019 StartY=-117.793 StartZ=0 EndX=116.019 EndY=-130.393 EndZ=0
    g2: LineSegment StartX=116.019 StartY=-130.393 StartZ=0 EndX=122.119 EndY=-130.393 EndZ=0
    g3: LineSegment StartX=122.119 StartY=-130.393 StartZ=0 EndX=122.119 EndY=-127.003 EndZ=0
    g4: LineSegment StartX=122.119 StartY=-117.793 StartZ=0 EndX=121.069 EndY=-117.793 EndZ=0
    g5: GeomPoint X=119.069 Y=-124.093 Z=0
    g6: LineSegment StartX=216.019 StartY=-117.793 StartZ=0 EndX=216.019 EndY=-123.803 EndZ=0
    g7: LineSegment StartX=216.019 StartY=-130.393 StartZ=0 EndX=222.119 EndY=-130.393 EndZ=0
    g8: LineSegment StartX=222.119 StartY=-130.393 StartZ=0 EndX=222.119 EndY=-117.793 EndZ=0
    g9: LineSegment StartX=222.119 StartY=-117.793 StartZ=0 EndX=221.069 EndY=-117.793 EndZ=0
    g10: GeomPoint X=219.069 Y=-124.093 Z=0
    g11: LineSegment StartX=122.119 StartY=-123.803 StartZ=0 EndX=216.019 EndY=-123.803 EndZ=0
    g12: LineSegment StartX=216.019 StartY=-127.003 StartZ=0 EndX=122.119 EndY=-127.003 EndZ=0
    g13: LineSegment StartX=122.119 StartY=-123.803 StartZ=0 EndX=122.119 EndY=-117.793 EndZ=0
    g14: LineSegment StartX=216.019 StartY=-127.003 StartZ=0 EndX=216.019 EndY=-130.393 EndZ=0
    g15: GeomPoint X=169.069 Y=-124.093 Z=0
    g16: LineSegment StartX=121.069 StartY=-117.793 StartZ=0 EndX=121.069 EndY=-115.793 EndZ=0
    g17: LineSegment StartX=121.069 StartY=-115.793 StartZ=0 EndX=117.069 EndY=-115.793 EndZ=0
    g18: LineSegment StartX=117.069 StartY=-115.793 StartZ=0 EndX=117.069 EndY=-117.793 EndZ=0
    g19: LineSegment StartX=117.069 StartY=-117.793 StartZ=0 EndX=116.019 EndY=-117.793 EndZ=0
    g20: LineSegment StartX=217.069 StartY=-117.793 StartZ=0 EndX=217.069 EndY=-115.793 EndZ=0
    g21: LineSegment StartX=217.069 StartY=-115.793 StartZ=0 EndX=221.069 EndY=-115.793 EndZ=0
    g22: LineSegment StartX=221.069 StartY=-115.793 StartZ=0 EndX=221.069 EndY=-117.793 EndZ=0
    g23: LineSegment StartX=217.069 StartY=-117.793 StartZ=0 EndX=216.019 EndY=-117.793 EndZ=0
  constraints (65):
    c: DistanceX(g-1,g0) = 169.069
    c: DistanceY(g0,g-1) = 124.713
    c: Coincident(g1,g2)
    c: Coincident(g2,g3)
    c: Coincident(g13,g4)
    c: Coincident(g19,g1)
    c: Horizontal(g2)
    c: Horizontal(g4)
    c: Vertical(g1)
    c: Vertical(g3)
    c: Symmetric(g2,g1,g5)
    c: Coincident(g14,g7)
    c: Coincident(g7,g8)
    c: Coincident(g8,g9)
    c: Coincident(g23,g6)
    c: Horizontal(g7)
    c: Horizontal(g9)
    c: Vertical(g6)
    c: Vertical(g8)
    c: Symmetric(g7,g6,g10)
    c: Horizontal(g5,g10)
    c: DistanceX(g5,g10) = 100
    c: Horizontal(g11)
    c: Horizontal(g12)
    c: DistanceY(g12,g11) = 3.2
    c: DistanceY(g2,g12) = 3.39
    c: DistanceY(g1,g1) = 12.6
    c: Coincident(g3,g12)
    c: Coincident(g13,g11)
    c: Coincident(g6,g11)
    c: Coincident(g14,g12)
    c: Vertical(g13)
    c: Vertical(g14)
    c: Equal(g8,g1)
    c: Vertical(g0,g15)
    c: DistanceY(g0,g15) = 0.62
    c: Symmetric(g10,g5,g15)
    c: DistanceX(g2,g2) = 6.1
    c: Vertical(g16)
    c: Coincident(g17,g16)
    c: Horizontal(g17)
    c: Coincident(g18,g17)
    c: Vertical(g18)
    c: DistanceY(g18,g18) = 2
    c: DistanceX(g17,g17) = 4
    c: DistanceX(g16,g4) = 1.05
    c: Coincident(g4,g16)
    c: Coincident(g19,g18)
    c: Horizontal(g19)
    c: Vertical(g11,g3)
    c: Horizontal(g18,g4)
    c: Vertical(g20)
    c: Coincident(g21,g20)
    c: Horizontal(g21)
    c: Coincident(g22,g21)
    c: Vertical(g22)
    c: DistanceY(g20,g20) = 2
    c: DistanceX(g21,g21) = 4
    c: Equal(g7,g2)
    c: DistanceX(g6,g20) = 1.05
    c: Coincident(g9,g22)
    c: Coincident(g23,g20)
    c: Vertical(g6,g12)
    c: Horizontal(g20,g9)
    c: Horizontal(g23)
FEATURE [Sketcher::SketchObject] Sketch011
  AttachmentOffset = pos=(0,0,4.1) rot=(0,0,1;0rad)
  FullyConstrained = true
  MapMode = 5
  Placement = pos=(0,0,4.1) rot=(0,0,1;0rad)
  Support = -> [XY_Plane097]
  expr: Constraints[0] = Spreadsheet.u * (2 + 2.25 / 2)
  expr: Constraints[1] = Spreadsheet.PCB_width - Spreadsheet.u * 1.75
  expr: Constraints[30] = Spreadsheet.stab_length + 0.2
  expr: Constraints[51] = Spreadsheet.stab_width + 0.2
  expr: Constraints[53] = (Spreadsheet.stab_width + 0.2) / 2 - 2
  expr: Constraints[58] = (Spreadsheet.stab_width + 0.2) / 2 - 2
  sketch-geometry (24):
    g0: GeomPoint X=59.5312 Y=-105.662 Z=0
    g1: LineSegment StartX=44.4813 StartY=-98.7425 StartZ=0 EndX=44.4813 EndY=-111.342 EndZ=0
    g2: LineSegment StartX=44.4813 StartY=-111.342 StartZ=0 EndX=50.5813 EndY=-111.342 EndZ=0
    g3: LineSegment StartX=50.5813 StartY=-111.342 StartZ=0 EndX=50.5813 EndY=-107.952 EndZ=0
    g4: LineSegment StartX=50.5813 StartY=-98.7425 StartZ=0 EndX=49.5313 EndY=-98.7425 EndZ=0
    g5: GeomPoint X=47.5312 Y=-105.042 Z=0
    g6: LineSegment StartX=68.4813 StartY=-98.7425 StartZ=0 EndX=68.4813 EndY=-104.752 EndZ=0
    g7: LineSegment StartX=68.4813 StartY=-111.342 StartZ=0 EndX=74.5813 EndY=-111.342 EndZ=0
    g8: LineSegment StartX=74.5813 StartY=-111.342 StartZ=0 EndX=74.5813 EndY=-98.7425 EndZ=0
    g9: LineSegment StartX=74.5813 StartY=-98.7425 StartZ=0 EndX=73.5313 EndY=-98.7425 EndZ=0
    g10: GeomPoint X=71.5312 Y=-105.042 Z=0
    g11: LineSegment StartX=50.5813 StartY=-104.752 StartZ=0 EndX=68.4813 EndY=-104.752 EndZ=0
    g12: LineSegment StartX=68.4813 StartY=-107.952 StartZ=0 EndX=50.5813 EndY=-107.952 EndZ=0
    g13: LineSegment StartX=50.5813 StartY=-104.752 StartZ=0 EndX=50.5813 EndY=-98.7425 EndZ=0
    g14: LineSegment StartX=68.4813 StartY=-107.952 StartZ=0 EndX=68.4813 EndY=-111.342 EndZ=0
    g15: GeomPoint X=59.5312 Y=-105.042 Z=0
    g16: LineSegment StartX=45.5313 StartY=-98.7425 StartZ=0 EndX=45.5313 EndY=-96.7425 EndZ=0
    g17: LineSegment StartX=45.5313 StartY=-96.7425 StartZ=0 EndX=49.5313 EndY=-96.7425 EndZ=0
    g18: LineSegment StartX=49.5313 StartY=-96.7425 StartZ=0 EndX=49.5313 EndY=-98.7425 EndZ=0
    g19: LineSegment StartX=69.5313 StartY=-98.7425 StartZ=0 EndX=69.5313 EndY=-96.7425 EndZ=0
    g20: LineSegment StartX=69.5313 StartY=-96.7425 StartZ=0 EndX=73.5313 EndY=-96.7425 EndZ=0
    g21: LineSegment StartX=73.5313 StartY=-96.7425 StartZ=0 EndX=73.5313 EndY=-98.7425 EndZ=0
    g22: LineSegment StartX=45.5313 StartY=-98.7425 StartZ=0 EndX=44.4813 EndY=-98.7425 EndZ=0
    g23: LineSegment StartX=69.5313 StartY=-98.7425 StartZ=0 EndX=68.4813 EndY=-98.7425 EndZ=0
  constraints (65):
    c: DistanceX(g-1,g0) = 59.5312
    c: DistanceY(g0,g-1) = 105.662
    c: Coincident(g1,g2)
    c: Coincident(g2,g3)
    c: Coincident(g13,g4)
    c: Coincident(g22,g1)
    c: Horizontal(g2)
    c: Horizontal(g4)
    c: Vertical(g1)
    c: Vertical(g3)
    c: Symmetric(g2,g1,g5)
    c: Coincident(g14,g7)
    c: Coincident(g7,g8)
    c: Coincident(g8,g9)
    c: Coincident(g23,g6)
    c: Horizontal(g7)
    c: Horizontal(g9)
    c: Vertical(g6)
    c: Vertical(g8)
    c: Symmetric(g7,g6,g10)
    c: Horizontal(g5,g10)
    c: DistanceX(g5,g10) = 24
    c: Horizontal(g11)
    c: Horizontal(g12)
    c: DistanceY(g12,g11) = 3.2
    c: DistanceY(g2,g12) = 3.39
    c: Coincident(g3,g12)
    c: Coincident(g13,g11)
    c: Coincident(g6,g11)
    c: Coincident(g14,g12)
    c: DistanceY(g1,g1) = 12.6
    c: Equal(g8,g1)
    c: Vertical(g14)
    c: Vertical(g13)
    c: Vertical(g0,g15)
    c: DistanceY(g0,g15) = 0.62
    c: Symmetric(g5,g10,g15)
    c: Vertical(g16)
    c: Coincident(g17,g16)
    c: Horizontal(g17)
    c: Coincident(g18,g17)
    c: Vertical(g18)
    c: Vertical(g19)
    c: Coincident(g20,g19)
    c: Horizontal(g20)
    c: Coincident(g21,g20)
    c: Vertical(g21)
    c: DistanceX(g20,g20) = 4
    c: DistanceX(g17,g17) = 4
    c: DistanceY(g16,g16) = 2
    c: DistanceY(g19,g19) = 2
    c: DistanceX(g2,g2) = 6.1
    c: Vertical(g11,g3)
    c: DistanceX(g18,g4) = 1.05
    c: Coincident(g4,g18)
    c: Coincident(g22,g16)
    c: Horizontal(g22)
    c: Horizontal(g4,g16)
    c: DistanceX(g6,g19) = 1.05
    c: Coincident(g9,g21)
    c: Coincident(g23,g19)
    c: Vertical(g6,g12)
    c: Horizontal(g19,g9)
    c: Horizontal(g23)
    c: Equal(g7,g2)
FEATURE [PartDesign::Pocket] Pocket009
  BaseFeature = -> Pocket008
  Direction = (0,0,-1)
  Length = 5
  Length2 = 5
  Profile = -> Sketch010
  ReferenceAxis = -> Sketch010 [N_Axis]
  Type = 0
FEATURE [Sketcher::SketchObject] Sketch012
  AttachmentOffset = pos=(0,0,4.1) rot=(0,0,1;0rad)
  FullyConstrained = true
  MapMode = 5
  Placement = pos=(0,0,4.1) rot=(0,0,1;0rad)
  Support = -> [XY_Plane097]
  expr: Constraints[0] = Spreadsheet.u * (2 + 1.75 + 11 + 2.25 / 2)
  expr: Constraints[16] = Spreadsheet.stab_length + 0.2
  expr: Constraints[1] = Spreadsheet.PCB_width - Spreadsheet.u * 2.75
  expr: Constraints[46] = Spreadsheet.stab_width + 0.2
  expr: Constraints[47] = (Spreadsheet.stab_width + 0.2) / 2 - 2
  expr: Constraints[48] = (Spreadsheet.stab_width + 0.2) / 2 - 2
  sketch-geometry (24):
    g0: GeomPoint X=302.419 Y=-86.6125 Z=0
    g1: LineSegment StartX=287.369 StartY=-79.6925 StartZ=0 EndX=287.369 EndY=-92.2925 EndZ=0
    g2: LineSegment StartX=287.369 StartY=-92.2925 StartZ=0 EndX=293.469 EndY=-92.2925 EndZ=0
    g3: LineSegment StartX=293.469 StartY=-79.6925 StartZ=0 EndX=292.419 EndY=-79.6925 EndZ=0
    g4: GeomPoint X=290.419 Y=-85.9925 Z=0
    g5: LineSegment StartX=311.369 StartY=-92.2925 StartZ=0 EndX=317.469 EndY=-92.2925 EndZ=0
    g6: LineSegment StartX=317.469 StartY=-92.2925 StartZ=0 EndX=317.469 EndY=-79.6925 EndZ=0
    g7: LineSegment StartX=317.469 StartY=-79.6925 StartZ=0 EndX=316.419 EndY=-79.6925 EndZ=0
    g8: GeomPoint X=314.419 Y=-85.9925 Z=0
    g9: LineSegment StartX=293.469 StartY=-79.6925 StartZ=0 EndX=293.469 EndY=-85.7025 EndZ=0
    g10: LineSegment StartX=293.469 StartY=-85.7025 StartZ=0 EndX=311.369 EndY=-85.7025 EndZ=0
    g11: LineSegment StartX=311.369 StartY=-85.7025 StartZ=0 EndX=311.369 EndY=-79.6925 EndZ=0
    g12: LineSegment StartX=311.369 StartY=-92.2925 StartZ=0 EndX=311.369 EndY=-88.9025 EndZ=0
    g13: LineSegment StartX=311.369 StartY=-88.9025 StartZ=0 EndX=293.469 EndY=-88.9025 EndZ=0
    g14: LineSegment StartX=293.469 StartY=-88.9025 StartZ=0 EndX=293.469 EndY=-92.2925 EndZ=0
    g15: GeomPoint X=302.419 Y=-85.9925 Z=0
    g16: LineSegment StartX=288.419 StartY=-79.6925 StartZ=0 EndX=288.419 EndY=-77.6925 EndZ=0
    g17: LineSegment StartX=288.419 StartY=-77.6925 StartZ=0 EndX=292.419 EndY=-77.6925 EndZ=0
    g18: LineSegment StartX=292.419 StartY=-77.6925 StartZ=0 EndX=292.419 EndY=-79.6925 EndZ=0
    g19: LineSegment StartX=312.419 StartY=-79.6925 StartZ=0 EndX=312.419 EndY=-77.6925 EndZ=0
    g20: LineSegment StartX=312.419 StartY=-77.6925 StartZ=0 EndX=316.419 EndY=-77.6925 EndZ=0
    g21: LineSegment StartX=316.419 StartY=-77.6925 StartZ=0 EndX=316.419 EndY=-79.6925 EndZ=0
    g22: LineSegment StartX=312.419 StartY=-79.6925 StartZ=0 EndX=311.369 EndY=-79.6925 EndZ=0
    g23: LineSegment StartX=288.419 StartY=-79.6925 StartZ=0 EndX=287.369 EndY=-79.6925 EndZ=0
  constraints (65):
    c: DistanceX(g-1,g0) = 302.419
    c: DistanceY(g0,g-1) = 86.6125
    c: Coincident(g1,g2)
    c: Coincident(g23,g1)
    c: Horizontal(g2)
    c: Horizontal(g3)
    c: Vertical(g1)
    c: Symmetric(g2,g1,g4)
    c: Coincident(g5,g6)
    c: Coincident(g6,g7)
    c: Horizontal(g5)
    c: Horizontal(g7)
    c: Vertical(g6)
    c: Symmetric(g5,g22,g8)
    c: Horizontal(g4,g8)
    c: DistanceX(g4,g8) = 24
    c: DistanceY(g1,g1) = 12.6
    c: Equal(g1,g6)
    c: Coincident(g9,g3)
    c: Vertical(g9)
    c: Coincident(g10,g9)
    c: Horizontal(g10)
    c: Coincident(g11,g10)
    c: Coincident(g11,g22)
    c: Vertical(g11)
    c: Coincident(g12,g5)
    c: Vertical(g12)
    c: Horizontal(g13)
    c: Coincident(g14,g13)
    c: Coincident(g14,g2)
    c: Vertical(g14)
    c: DistanceY(g13,g9) = 3.2
    c: DistanceY(g14,g14) = 3.39
    c: Coincident(g12,g13)
    c: Vertical(g15,g0)
    c: DistanceY(g0,g15) = 0.62
    c: Symmetric(g4,g8,g15)
    c: Vertical(g16)
    c: Coincident(g17,g16)
    c: Horizontal(g17)
    c: Coincident(g18,g17)
    c: Vertical(g18)
    c: Vertical(g19)
    c: Coincident(g20,g19)
    c: Horizontal(g20)
    c: Vertical(g21)
    c: DistanceX(g2,g2) = 6.1
    c: DistanceX(g18,g3) = 1.05
    c: DistanceX(g22,g19) = 1.05
    c: DistanceX(g17,g17) = 4
    c: DistanceX(g20,g20) = 4
    c: Coincident(g20,g21)
    c: DistanceY(g18,g18) = 2
    c: DistanceY(g19,g19) = 2
    c: Coincident(g7,g21)
    c: Coincident(g22,g19)
    c: Coincident(g3,g18)
    c: Coincident(g23,g16)
    c: Equal(g5,g2)
    c: Vertical(g13,g9)
    c: Vertical(g10,g12)
    c: Horizontal(g23)
    c: Horizontal(g3,g16)
    c: Horizontal(g22)
    c: Horizontal(g19,g7)
FEATURE [PartDesign::Pocket] Pocket010
  BaseFeature = -> Pocket009
  Direction = (0,0,-1)
  Length = 5
  Length2 = 5
  Profile = -> Sketch011
  ReferenceAxis = -> Sketch011 [N_Axis]
  Type = 0
FEATURE [Sketcher::SketchObject] Sketch013
  AttachmentOffset = pos=(0,0,4.1) rot=(0,0,1;0rad)
  FullyConstrained = true
  MapMode = 5
  Placement = pos=(0,0,4.1) rot=(0,0,1;0rad)
  Support = -> [XY_Plane097]
  expr: Constraints[0] = Spreadsheet.u * (2 + +13 + 2 / 2)
  expr: Constraints[15] = Spreadsheet.stab_length + 0.2
  expr: Constraints[1] = Spreadsheet.PCB_width - Spreadsheet.u * 4.75
  expr: Constraints[37] = Spreadsheet.stab_width + 0.2
  expr: Constraints[48] = (Spreadsheet.stab_width + 0.2) / 2 - 2
  expr: Constraints[49] = (Spreadsheet.stab_width + 0.2) / 2 - 2
  sketch-geometry (24):
    g0: GeomPoint X=304.8 Y=-48.5125 Z=0
    g1: LineSegment StartX=289.75 StartY=-41.5925 StartZ=0 EndX=289.75 EndY=-54.1925 EndZ=0
    g2: LineSegment StartX=289.75 StartY=-54.1925 StartZ=0 EndX=295.85 EndY=-54.1925 EndZ=0
    g3: LineSegment StartX=295.85 StartY=-41.5925 StartZ=0 EndX=294.8 EndY=-41.5925 EndZ=0
    g4: GeomPoint X=292.8 Y=-47.8925 Z=0
    g5: LineSegment StartX=313.75 StartY=-54.1925 StartZ=0 EndX=319.85 EndY=-54.1925 EndZ=0
    g6: LineSegment StartX=319.85 StartY=-54.1925 StartZ=0 EndX=319.85 EndY=-41.5925 EndZ=0
    g7: LineSegment StartX=319.85 StartY=-41.5925 StartZ=0 EndX=318.8 EndY=-41.5925 EndZ=0
    g8: GeomPoint X=316.8 Y=-47.8925 Z=0
    g9: LineSegment StartX=313.75 StartY=-41.5925 StartZ=0 EndX=313.75 EndY=-47.6025 EndZ=0
    g10: LineSegment StartX=313.75 StartY=-47.6025 StartZ=0 EndX=295.85 EndY=-47.6025 EndZ=0
    g11: LineSegment StartX=295.85 StartY=-41.5925 StartZ=0 EndX=295.85 EndY=-47.6025 EndZ=0
    g12: LineSegment StartX=295.85 StartY=-54.1925 StartZ=0 EndX=295.85 EndY=-50.8025 EndZ=0
    g13: LineSegment StartX=295.85 StartY=-50.8025 StartZ=0 EndX=313.75 EndY=-50.8025 EndZ=0
    g14: LineSegment StartX=313.75 StartY=-50.8025 StartZ=0 EndX=313.75 EndY=-54.1925 EndZ=0
    g15: GeomPoint X=304.8 Y=-47.8925 Z=0
    g16: LineSegment StartX=290.8 StartY=-41.5925 StartZ=0 EndX=290.8 EndY=-39.5925 EndZ=0
    g17: LineSegment StartX=290.8 StartY=-39.5925 StartZ=0 EndX=294.8 EndY=-39.5925 EndZ=0
    g18: LineSegment StartX=294.8 StartY=-39.5925 StartZ=0 EndX=294.8 EndY=-41.5925 EndZ=0
    g19: LineSegment StartX=314.8 StartY=-41.5925 StartZ=0 EndX=314.8 EndY=-39.5925 EndZ=0
    g20: LineSegment StartX=314.8 StartY=-39.5925 StartZ=0 EndX=318.8 EndY=-39.5925 EndZ=0
    g21: LineSegment StartX=318.8 StartY=-39.5925 StartZ=0 EndX=318.8 EndY=-41.5925 EndZ=0
    g22: LineSegment StartX=314.8 StartY=-41.5925 StartZ=0 EndX=313.75 EndY=-41.5925 EndZ=0
    g23: LineSegment StartX=290.8 StartY=-41.5925 StartZ=0 EndX=289.75 EndY=-41.5925 EndZ=0
  constraints (65):
    c: DistanceX(g-1,g0) = 304.8
    c: DistanceY(g0,g-1) = 48.5125
    c: Coincident(g1,g2)
    c: Coincident(g23,g1)
    c: Horizontal(g2)
    c: Horizontal(g3)
    c: Vertical(g1)
    c: Symmetric(g2,g1,g4)
    c: Coincident(g5,g6)
    c: Coincident(g6,g7)
    c: Horizontal(g5)
    c: Horizontal(g7)
    c: Vertical(g6)
    c: Symmetric(g5,g22,g8)
    c: DistanceX(g4,g8) = 24
    c: DistanceY(g1,g1) = 12.6
    c: Equal(g1,g6)
    c: Coincident(g9,g22)
    c: Vertical(g9)
    c: Coincident(g10,g9)
    c: Horizontal(g10)
    c: Coincident(g11,g3)
    c: Coincident(g11,g10)
    c: Vertical(g11)
    c: Coincident(g12,g2)
    c: Vertical(g12)
    c: Coincident(g13,g12)
    c: Horizontal(g13)
    c: Coincident(g14,g13)
    c: Coincident(g14,g5)
    c: Vertical(g14)
    c: DistanceY(g12,g10) = 3.2
    c: Horizontal(g4,g8)
    c: Symmetric(g4,g8,g15)
    c: Vertical(g15,g0)
    c: DistanceY(g0,g15) = 0.62
    c: DistanceY(g12,g12) = 3.39
    c: DistanceX(g2,g2) = 6.1
    c: Vertical(g16)
    c: Coincident(g17,g16)
    c: Horizontal(g17)
    c: Coincident(g18,g17)
    c: Vertical(g18)
    c: Vertical(g19)
    c: Coincident(g20,g19)
    c: Horizontal(g20)
    c: Coincident(g21,g20)
    c: Vertical(g21)
    c: DistanceX(g18,g3) = 1.05
    c: DistanceX(g22,g19) = 1.05
    c: DistanceX(g17,g17) = 4
    c: DistanceX(g20,g20) = 4
    c: DistanceY(g16,g16) = 2
    c: DistanceY(g19,g19) = 2
    c: Coincident(g7,g21)
    c: Coincident(g22,g19)
    c: Coincident(g3,g18)
    c: Coincident(g23,g16)
    c: Equal(g5,g2)
    c: Vertical(g10,g12)
    c: Vertical(g9,g13)
    c: Horizontal(g16,g3)
    c: Horizontal(g23)
    c: Horizontal(g19,g7)
    c: Horizontal(g22)
FEATURE [PartDesign::Pocket] Pocket011
  BaseFeature = -> Pocket010
  Direction = (0,0,-1)
  Length = 5
  Length2 = 5
  Profile = -> Sketch012
  ReferenceAxis = -> Sketch012 [N_Axis]
  Type = 0
FEATURE [PartDesign::Pocket] Pocket012
  BaseFeature = -> Pocket011
  Direction = (0,0,-1)
  Length = 5
  Length2 = 5
  Profile = -> Sketch013
  ReferenceAxis = -> Sketch013 [N_Axis]
  Type = 0
FEATURE [Part::Feature] Part__Feature  label="COMPOUND"
  shape: bbox 15 x 15 x 11.8 mm, 252 faces, 6 solids (baked)
FEATURE [App::Part] ks33
  Group = -> [Part__Feature]
  Origin = -> Origin
  Placement = pos=(47.625,-24.7,1.6) rot=(0,0,1;3.14159rad)
FEATURE [Part::Feature] Part__Feature001  label="COMPOUND001"
  shape: bbox 15 x 15 x 11.8 mm, 252 faces, 6 solids (baked)
FEATURE [App::Part] ks33001
  Group = -> [Part__Feature001]
  Origin = -> Origin098
  Placement = pos=(180.975,-48.5125,1.6) rot=(0,0,1;3.14159rad)
FEATURE [Part::Feature] Part__Feature002  label="COMPOUND002"
  shape: bbox 15 x 15 x 11.8 mm, 252 faces, 6 solids (baked)
FEATURE [App::Part] ks33002
  Group = -> [Part__Feature002]
  Origin = -> Origin099
  Placement = pos=(190.5,-24.7,1.6) rot=(0,0,1;3.14159rad)
FEATURE [Part::Feature] Part__Feature003  label="COMPOUND003"
  shape: bbox 15 x 15 x 11.8 mm, 252 faces, 6 solids (baked)
FEATURE [App::Part] ks33003
  Group = -> [Part__Feature003]
  Origin = -> Origin100
  Placement = pos=(54.7687,-86.6125,1.6) rot=(0,0,1;3.14159rad)
FEATURE [Part::Feature] Part__Feature004  label="COMPOUND004"
  shape: bbox 15 x 15 x 11.8 mm, 252 faces, 6 solids (baked)
FEATURE [App::Part] ks33004
  Group = -> [Part__Feature004]
  Origin = -> Origin101
  Placement = pos=(171.45,-67.5625,1.6) rot=(0,0,1;3.14159rad)
FEATURE [Part::Feature] Part__Feature005  label="COMPOUND005"
  shape: bbox 15 x 15 x 11.8 mm, 252 faces, 6 solids (baked)
FEATURE [App::Part] ks33005
  Group = -> [Part__Feature005]
  Origin = -> Origin102
  Placement = pos=(97.6312,-124.713,1.6) rot=(0,0,1;3.14159rad)
FEATURE [Part::Feature] Part__Feature006  label="COMPOUND006"
  shape: bbox 15 x 15 x 11.8 mm, 252 faces, 6 solids (baked)
FEATURE [App::Part] ks33006
  Group = -> [Part__Feature006]
  Origin = -> Origin103
  Placement = pos=(166.688,-105.662,1.6) rot=(0,0,1;3.14159rad)
FEATURE [Part::Feature] Part__Feature007  label="COMPOUND007"
  shape: bbox 15 x 15 x 11.8 mm, 252 faces, 6 solids (baked)
FEATURE [App::Part] ks33007
  Group = -> [Part__Feature007]
  Origin = -> Origin104
  Placement = pos=(342.9,-86.6125,1.6) rot=(0,0,1;3.14159rad)
FEATURE [Part::Feature] Part__Feature008  label="COMPOUND008"
  shape: bbox 15 x 15 x 11.8 mm, 252 faces, 6 solids (baked)
FEATURE [App::Part] ks33008
  Group = -> [Part__Feature008]
  Origin = -> Origin105
  Placement = pos=(176.213,-86.6125,1.6) rot=(0,0,1;3.14159rad)
FEATURE [Part::Feature] Part__Feature009  label="COMPOUND009"
  shape: bbox 15 x 15 x 11.8 mm, 252 faces, 6 solids (baked)
FEATURE [App::Part] ks33009
  Group = -> [Part__Feature009]
  Origin = -> Origin106
  Placement = pos=(271.462,-86.6125,1.6) rot=(0,0,1;3.14159rad)
FEATURE [Part::Feature] Part__Feature010  label="COMPOUND010"
  shape: bbox 15 x 15 x 11.8 mm, 252 faces, 6 solids (baked)
FEATURE [App::Part] ks33010
  Group = -> [Part__Feature010]
  Origin = -> Origin107
  Placement = pos=(114.3,-67.5625,1.6) rot=(0,0,1;3.14159rad)
FEATURE [Part::Feature] Part__Feature011  label="COMPOUND011"
  shape: bbox 15 x 15 x 11.8 mm, 252 faces, 6 solids (baked)
FEATURE [App::Part] ks33011
  Group = -> [Part__Feature011]
  Origin = -> Origin108
  Placement = pos=(190.5,-67.5625,1.6) rot=(0,0,1;3.14159rad)
FEATURE [Part::Feature] Part__Feature012  label="COMPOUND012"
  shape: bbox 15 x 15 x 11.8 mm, 252 faces, 6 solids (baked)
FEATURE [App::Part] ks33012
  Group = -> [Part__Feature012]
  Origin = -> Origin109
  Placement = pos=(161.925,-48.5125,1.6) rot=(0,0,1;3.14159rad)
FEATURE [Part::Feature] Part__Feature013  label="COMPOUND013"
  shape: bbox 15 x 15 x 11.8 mm, 252 faces, 6 solids (baked)
FEATURE [App::Part] ks33013
  Group = -> [Part__Feature013]
  Origin = -> Origin110
  Placement = pos=(285.75,-67.5625,1.6) rot=(0,0,1;3.14159rad)
FEATURE [Part::Feature] Part__Feature014  label="SOLID"
  shape: bbox 15.88 x 13.9 x 29 mm, 532 faces (baked)
FEATURE [App::Part] ROT_EC11E
  Group = -> [Part__Feature014]
  Origin = -> Origin111
  Placement = pos=(31.075,-17.2,1.65) rot=(0,0,-1;1.5708rad)
FEATURE [Part::Feature] Part__Feature015  label="COMPOUND014"
  shape: bbox 15 x 15 x 11.8 mm, 252 faces, 6 solids (baked)
FEATURE [App::Part] ks33014
  Group = -> [Part__Feature015]
  Origin = -> Origin112
  Placement = pos=(338.137,-129.475,1.6) rot=(0,0,1;3.14159rad)
FEATURE [Part::Feature] Part__Feature016  label="SOLID001"
  shape: bbox 9 x 6 x 4.3 mm, 97 faces (baked)
FEATURE [App::Part] SW_SPST_PTS645
  Group = -> [Part__Feature016]
  Origin = -> Origin113
  Placement = pos=(9.525,-124.713,1.65) rot=(0,0,-1;1.5708rad)
FEATURE [Part::Feature] Part__Feature017  label="COMPOUND015"
  shape: bbox 15 x 15 x 11.8 mm, 252 faces, 6 solids (baked)
FEATURE [App::Part] ks33015
  Group = -> [Part__Feature017]
  Origin = -> Origin114
  Placement = pos=(276.225,-124.713,1.6) rot=(0,0,1;3.14159rad)
FEATURE [Part::Feature] Part__Feature018  label="COMPOUND016"
  shape: bbox 15 x 15 x 11.8 mm, 252 faces, 6 solids (baked)
FEATURE [App::Part] ks33016
  Group = -> [Part__Feature018]
  Origin = -> Origin115
  Placement = pos=(119.062,-86.6125,1.6) rot=(0,0,1;3.14159rad)
FEATURE [Part::Feature] Part__Feature019  label="COMPOUND017"
  shape: bbox 15 x 15 x 11.8 mm, 252 faces, 6 solids (baked)
FEATURE [App::Part] ks33017
  Group = -> [Part__Feature019]
  Origin = -> Origin116
  Placement = pos=(85.725,-48.5125,1.6) rot=(0,0,1;3.14159rad)
FEATURE [Part::Feature] Part__Feature020  label="COMPOUND018"
  shape: bbox 15 x 15 x 11.8 mm, 252 faces, 6 solids (baked)
FEATURE [App::Part] ks33018
  Group = -> [Part__Feature020]
  Origin = -> Origin117
  Placement = pos=(95.25,-67.5625,1.6) rot=(0,0,1;3.14159rad)
FEATURE [Part::Feature] Part__Feature021  label="COMPOUND019"
  shape: bbox 15 x 15 x 11.8 mm, 252 faces, 6 solids (baked)
FEATURE [App::Part] ks33019
  Group = -> [Part__Feature021]
  Origin = -> Origin118
  Placement = pos=(219.075,-48.5125,1.6) rot=(0,0,1;3.14159rad)
FEATURE [Part::Feature] Part__Feature022  label="COMPOUND020"
  shape: bbox 15 x 15 x 11.8 mm, 252 faces, 6 solids (baked)
FEATURE [App::Part] ks33020
  Group = -> [Part__Feature022]
  Origin = -> Origin119
  Placement = pos=(195.262,-86.6125,1.6) rot=(0,0,1;3.14159rad)
FEATURE [Part::Feature] Part__Feature023  label="SOLID002"
  shape: bbox 9 x 6 x 4.3 mm, 97 faces (baked)
FEATURE [App::Part] SW_SPST_PTS645001
  Group = -> [Part__Feature023]
  Origin = -> Origin120
  Placement = pos=(28.575,-105.662,1.65) rot=(0,0,-1;1.5708rad)
FEATURE [Part::Feature] Part__Feature024  label="COMPOUND021"
  shape: bbox 15 x 15 x 11.8 mm, 252 faces, 6 solids (baked)
FEATURE [App::Part] ks33021
  Group = -> [Part__Feature024]
  Origin = -> Origin121
  Placement = pos=(228.6,-67.5625,1.6) rot=(0,0,1;3.14159rad)
FEATURE [Part::Feature] Part__Feature025  label="SOLID003"
  shape: bbox 9 x 6 x 4.3 mm, 97 faces (baked)
FEATURE [App::Part] SW_SPST_PTS645002
  Group = -> [Part__Feature025]
  Origin = -> Origin122
  Placement = pos=(28.575,-124.713,1.65) rot=(0,0,-1;1.5708rad)
FEATURE [Part::Feature] Part__Feature026  label="COMPOUND022"
  shape: bbox 15 x 15 x 11.8 mm, 252 faces, 6 solids (baked)
FEATURE [App::Part] ks33022
  Group = -> [Part__Feature026]
  Origin = -> Origin123
  Placement = pos=(300.038,-129.475,1.6) rot=(0,0,1;3.14159rad)
FEATURE [Part::Feature] Part__Feature027  label="COMPOUND023"
  shape: bbox 15 x 15 x 11.8 mm, 252 faces, 6 solids (baked)
FEATURE [App::Part] ks33023
  Group = -> [Part__Feature027]
  Origin = -> Origin124
  Placement = pos=(47.625,-48.5125,1.6) rot=(0,0,1;3.14159rad)
FEATURE [Part::Feature] Part__Feature028  label="COMPOUND024"
  shape: bbox 15 x 15 x 11.8 mm, 252 faces, 6 solids (baked)
FEATURE [App::Part] ks33024
  Group = -> [Part__Feature028]
  Origin = -> Origin125
  Placement = pos=(233.363,-86.6125,1.6) rot=(0,0,1;3.14159rad)
FEATURE [Part::Feature] Part__Feature029  label="COMPOUND025"
  shape: bbox 15 x 15 x 11.8 mm, 252 faces, 6 solids (baked)
FEATURE [App::Part] ks33025
  Group = -> [Part__Feature029]
  Origin = -> Origin126
  Placement = pos=(302.419,-86.6125,1.6) rot=(0,0,1;3.14159rad)
FEATURE [Part::Feature] Part__Feature030  label="COMPOUND026"
  shape: bbox 15 x 15 x 11.8 mm, 252 faces, 6 solids (baked)
FEATURE [App::Part] ks33026
  Group = -> [Part__Feature030]
  Origin = -> Origin127
  Placement = pos=(233.363,-24.7,1.6) rot=(0,0,1;3.14159rad)
FEATURE [Part::Feature] Part__Feature031  label="COMPOUND027"
  shape: bbox 15 x 15 x 11.8 mm, 252 faces, 6 solids (baked)
FEATURE [App::Part] ks33027
  Group = -> [Part__Feature031]
  Origin = -> Origin128
  Placement = pos=(50.0063,-124.713,1.6) rot=(0,0,1;3.14159rad)
FEATURE [Part::Feature] Part__Feature032  label="COMPOUND028"
  shape: bbox 15 x 15 x 11.8 mm, 252 faces, 6 solids (baked)
FEATURE [App::Part] ks33028
  Group = -> [Part__Feature032]
  Origin = -> Origin129
  Placement = pos=(73.8187,-124.713,1.6) rot=(0,0,1;3.14159rad)
FEATURE [Part::Feature] Part__Feature033  label="COMPOUND029"
  shape: bbox 15 x 15 x 11.8 mm, 252 faces, 6 solids (baked)
FEATURE [App::Part] ks33029
  Group = -> [Part__Feature033]
  Origin = -> Origin130
  Placement = pos=(276.225,-48.5125,1.6) rot=(0,0,1;3.14159rad)
FEATURE [Part::Feature] Part__Feature034  label="COMPOUND030"
  shape: bbox 15 x 15 x 11.8 mm, 252 faces, 6 solids (baked)
FEATURE [App::Part] ks33030
  Group = -> [Part__Feature034]
  Origin = -> Origin131
  Placement = pos=(133.35,-67.5625,1.6) rot=(0,0,1;3.14159rad)
FEATURE [Part::Feature] Part__Feature035  label="COMPOUND031"
  shape: bbox 15 x 15 x 11.8 mm, 252 faces, 6 solids (baked)
FEATURE [App::Part] ks33031
  Group = -> [Part__Feature035]
  Origin = -> Origin132
  Placement = pos=(100.013,-86.6125,1.6) rot=(0,0,1;3.14159rad)
FEATURE [Part::Feature] Part__Feature036  label="COMPOUND032"
  shape: bbox 15 x 15 x 11.8 mm, 252 faces, 6 solids (baked)
FEATURE [App::Part] ks33032
  Group = -> [Part__Feature036]
  Origin = -> Origin133
  Placement = pos=(342.9,-24.7,1.6) rot=(0,0,1;3.14159rad)
FEATURE [Part::Feature] Part__Feature037  label="COMPOUND033"
  shape: bbox 15 x 15 x 11.8 mm, 252 faces, 6 solids (baked)
FEATURE [App::Part] ks33033
  Group = -> [Part__Feature037]
  Origin = -> Origin134
  Placement = pos=(109.537,-105.662,1.6) rot=(0,0,1;3.14159rad)
FEATURE [Part::Feature] Part__Feature038  label="COMPOUND034"
  shape: bbox 15 x 15 x 11.8 mm, 252 faces, 6 solids (baked)
FEATURE [App::Part] ks33034
  Group = -> [Part__Feature038]
  Origin = -> Origin135
  Placement = pos=(223.838,-105.662,1.6) rot=(0,0,1;3.14159rad)
FEATURE [Part::Feature] Part__Feature039  label="COMPOUND035"
  shape: bbox 15 x 15 x 11.8 mm, 252 faces, 6 solids (baked)
FEATURE [App::Part] ks33035
  Group = -> [Part__Feature039]
  Origin = -> Origin136
  Placement = pos=(314.325,-24.7,1.6) rot=(0,0,1;3.14159rad)
FEATURE [Part::Feature] Part__Feature040  label="COMPOUND036"
  shape: bbox 15 x 15 x 11.8 mm, 252 faces, 6 solids (baked)
FEATURE [App::Part] ks33036
  Group = -> [Part__Feature040]
  Origin = -> Origin137
  Placement = pos=(242.887,-105.662,1.6) rot=(0,0,1;3.14159rad)
FEATURE [Part::Feature] Part__Feature041  label="COMPOUND037"
  shape: bbox 15 x 15 x 11.8 mm, 252 faces, 6 solids (baked)
FEATURE [App::Part] ks33037
  Group = -> [Part__Feature041]
  Origin = -> Origin138
  Placement = pos=(252.412,-24.7,1.6) rot=(0,0,1;3.14159rad)
FEATURE [Part::Feature] Part__Feature042  label="COMPOUND038"
  shape: bbox 15 x 15 x 11.8 mm, 252 faces, 6 solids (baked)
FEATURE [App::Part] ks33038
  Group = -> [Part__Feature042]
  Origin = -> Origin139
  Placement = pos=(319.087,-110.425,1.6) rot=(0,0,1;3.14159rad)
FEATURE [Part::Feature] Part__Feature043  label="COMPOUND039"
  shape: bbox 15 x 15 x 11.8 mm, 252 faces, 6 solids (baked)
FEATURE [App::Part] ks33039
  Group = -> [Part__Feature043]
  Origin = -> Origin140
  Placement = pos=(171.45,-24.7,1.6) rot=(0,0,1;3.14159rad)
FEATURE [Part::Feature] Part__Feature044  label="COMPOUND040"
  shape: bbox 15 x 15 x 11.8 mm, 252 faces, 6 solids (baked)
FEATURE [App::Part] ks33040
  Group = -> [Part__Feature044]
  Origin = -> Origin141
  Placement = pos=(157.162,-86.6125,1.6) rot=(0,0,1;3.14159rad)
FEATURE [Part::Feature] Part__Feature045  label="COMPOUND041"
  shape: bbox 15 x 15 x 11.8 mm, 252 faces, 6 solids (baked)
FEATURE [App::Part] ks33041
  Group = -> [Part__Feature045]
  Origin = -> Origin142
  Placement = pos=(342.9,-67.5625,1.6) rot=(0,0,1;3.14159rad)
FEATURE [Part::Feature] Part__Feature046  label="COMPOUND042"
  shape: bbox 15 x 15 x 11.8 mm, 252 faces, 6 solids (baked)
FEATURE [App::Part] ks33042
  Group = -> [Part__Feature046]
  Origin = -> Origin143
  Placement = pos=(90.4875,-24.7,1.6) rot=(0,0,1;3.14159rad)
FEATURE [Part::Feature] Part__Feature047  label="COMPOUND043"
  shape: bbox 15 x 15 x 11.8 mm, 252 faces, 6 solids (baked)
FEATURE [App::Part] ks33043
  Group = -> [Part__Feature047]
  Origin = -> Origin144
  Placement = pos=(319.087,-129.475,1.6) rot=(0,0,1;3.14159rad)
FEATURE [Part::Feature] Part__Feature048  label="COMPOUND044"
  shape: bbox 15 x 15 x 11.8 mm, 252 faces, 6 solids (baked)
FEATURE [App::Part] ks33044
  Group = -> [Part__Feature048]
  Origin = -> Origin145
  Placement = pos=(152.4,-24.7,1.6) rot=(0,0,1;3.14159rad)
FEATURE [Part::Feature] Part__Feature049  label="COMPOUND045"
  shape: bbox 15 x 15 x 11.8 mm, 252 faces, 6 solids (baked)
FEATURE [App::Part] ks33045
  Group = -> [Part__Feature049]
  Origin = -> Origin146
  Placement = pos=(342.9,-105.662,1.6) rot=(0,0,1;3.14159rad)
FEATURE [Part::Feature] Part__Feature050  label="COMPOUND046"
  shape: bbox 15 x 15 x 11.8 mm, 252 faces, 6 solids (baked)
FEATURE [App::Part] ks33046
  Group = -> [Part__Feature050]
  Origin = -> Origin147
  Placement = pos=(147.637,-105.662,1.6) rot=(0,0,1;3.14159rad)
FEATURE [Part::Feature] Part__Feature051  label="COMPOUND047"
  shape: bbox 15 x 15 x 11.8 mm, 252 faces, 6 solids (baked)
FEATURE [App::Part] ks33047
  Group = -> [Part__Feature051]
  Origin = -> Origin148
  Placement = pos=(104.775,-48.5125,1.6) rot=(0,0,1;3.14159rad)
FEATURE [Part::Feature] Part__Feature052  label="COMPOUND048"
  shape: bbox 15 x 15 x 11.8 mm, 252 faces, 6 solids (baked)
FEATURE [App::Part] ks33048
  Group = -> [Part__Feature052]
  Origin = -> Origin149
  Placement = pos=(342.9,-48.5125,1.6) rot=(0,0,1;3.14159rad)
FEATURE [Part::Feature] Part__Feature053  label="COMPOUND049"
  shape: bbox 15 x 15 x 11.8 mm, 252 faces, 6 solids (baked)
FEATURE [App::Part] ks33049
  Group = -> [Part__Feature053]
  Origin = -> Origin150
  Placement = pos=(209.55,-24.7,1.6) rot=(0,0,1;3.14159rad)
FEATURE [Part::Feature] Part__Feature054  label="COMPOUND050"
  shape: bbox 15 x 15 x 11.8 mm, 252 faces, 6 solids (baked)
FEATURE [App::Part] ks33050
  Group = -> [Part__Feature054]
  Origin = -> Origin151
  Placement = pos=(128.588,-105.662,1.6) rot=(0,0,1;3.14159rad)
FEATURE [Part::Feature] Part__Feature055  label="COMPOUND051"
  shape: bbox 15 x 15 x 11.8 mm, 252 faces, 6 solids (baked)
FEATURE [App::Part] ks33051
  Group = -> [Part__Feature055]
  Origin = -> Origin152
  Placement = pos=(214.312,-86.6125,1.6) rot=(0,0,1;3.14159rad)
FEATURE [Part::Feature] Part__Feature056  label="COMPOUND052"
  shape: bbox 15 x 15 x 11.8 mm, 252 faces, 6 solids (baked)
FEATURE [App::Part] ks33052
  Group = -> [Part__Feature056]
  Origin = -> Origin153
  Placement = pos=(59.5312,-105.662,1.6) rot=(0,0,1;3.14159rad)
FEATURE [Part::Feature] Part__Feature057  label="SOLID004"
  shape: bbox 15.88 x 13.9 x 29 mm, 532 faces (baked)
FEATURE [App::Part] ROT_EC11E001
  Group = -> [Part__Feature057]
  Origin = -> Origin154
  Placement = pos=(12.025,-17.2,1.65) rot=(0,0,-1;1.5708rad)
FEATURE [Part::Feature] Part__Feature058  label="COMPOUND053"
  shape: bbox 15 x 15 x 11.8 mm, 252 faces, 6 solids (baked)
FEATURE [App::Part] ks33053
  Group = -> [Part__Feature058]
  Origin = -> Origin155
  Placement = pos=(238.125,-124.713,1.6) rot=(0,0,1;3.14159rad)
FEATURE [Part::Feature] Part__Feature059  label="COMPOUND054"
  shape: bbox 15 x 15 x 11.8 mm, 252 faces, 6 solids (baked)
FEATURE [App::Part] ks33054
  Group = -> [Part__Feature059]
  Origin = -> Origin156
  Placement = pos=(123.825,-48.5125,1.6) rot=(0,0,1;3.14159rad)
FEATURE [Part::Feature] Part__Feature060  label="COMPOUND055"
  shape: bbox 15 x 15 x 11.8 mm, 252 faces, 6 solids (baked)
FEATURE [App::Part] ks33055
  Group = -> [Part__Feature060]
  Origin = -> Origin157
  Placement = pos=(238.125,-48.5125,1.6) rot=(0,0,1;3.14159rad)
FEATURE [Part::Feature] Part__Feature061  label="COMPOUND056"
  shape: bbox 15 x 15 x 11.8 mm, 252 faces, 6 solids (baked)
FEATURE [App::Part] ks33056
  Group = -> [Part__Feature061]
  Origin = -> Origin158
  Placement = pos=(109.537,-24.7,1.6) rot=(0,0,1;3.14159rad)
FEATURE [Part::Feature] Part__Feature062  label="COMPOUND057"
  shape: bbox 15 x 15 x 11.8 mm, 252 faces, 6 solids (baked)
FEATURE [App::Part] ks33057
  Group = -> [Part__Feature062]
  Origin = -> Origin159
  Placement = pos=(152.4,-67.5625,1.6) rot=(0,0,1;3.14159rad)
FEATURE [Part::Feature] Part__Feature063  label="COMPOUND058"
  shape: bbox 15 x 15 x 11.8 mm, 252 faces, 6 solids (baked)
FEATURE [App::Part] ks33058
  Group = -> [Part__Feature063]
  Origin = -> Origin160
  Placement = pos=(309.562,-67.5625,1.6) rot=(0,0,1;3.14159rad)
FEATURE [Part::Feature] Part__Feature064  label="COMPOUND059"
  shape: bbox 15 x 15 x 11.8 mm, 252 faces, 6 solids (baked)
FEATURE [App::Part] ks33059
  Group = -> [Part__Feature064]
  Origin = -> Origin161
  Placement = pos=(209.55,-67.5625,1.6) rot=(0,0,1;3.14159rad)
FEATURE [Part::Feature] Part__Feature065  label="COMPOUND060"
  shape: bbox 15 x 15 x 11.8 mm, 252 faces, 6 solids (baked)
FEATURE [App::Part] ks33060
  Group = -> [Part__Feature065]
  Origin = -> Origin162
  Placement = pos=(261.938,-105.662,1.6) rot=(0,0,1;3.14159rad)
FEATURE [Part::Feature] Part__Feature066  label="COMPOUND061"
  shape: bbox 15 x 15 x 11.8 mm, 252 faces, 6 solids (baked)
FEATURE [App::Part] ks33061
  Group = -> [Part__Feature066]
  Origin = -> Origin163
  Placement = pos=(169.069,-124.713,1.6) rot=(0,0,1;3.14159rad)
FEATURE [Part::Feature] Part__Feature067  label="SOLID005"
  shape: bbox 9 x 6 x 4.3 mm, 97 faces (baked)
FEATURE [App::Part] SW_SPST_PTS645003
  Group = -> [Part__Feature067]
  Origin = -> Origin164
  Placement = pos=(9.525,-105.662,1.65) rot=(0,0,-1;1.5708rad)
FEATURE [Part::Feature] Part__Feature068  label="COMPOUND062"
  shape: bbox 15 x 15 x 11.8 mm, 252 faces, 6 solids (baked)
FEATURE [App::Part] ks33062
  Group = -> [Part__Feature068]
  Origin = -> Origin165
  Placement = pos=(142.875,-48.5125,1.6) rot=(0,0,1;3.14159rad)
FEATURE [Part::Feature] Part__Feature069  label="COMPOUND063"
  shape: bbox 15 x 15 x 11.8 mm, 252 faces, 6 solids (baked)
FEATURE [App::Part] ks33063
  Group = -> [Part__Feature069]
  Origin = -> Origin166
  Placement = pos=(80.9625,-86.6125,1.6) rot=(0,0,1;3.14159rad)
FEATURE [Part::Feature] Part__Feature070  label="COMPOUND064"
  shape: bbox 15 x 15 x 11.8 mm, 252 faces, 6 solids (baked)
FEATURE [App::Part] ks33064
  Group = -> [Part__Feature070]
  Origin = -> Origin167
  Placement = pos=(288.131,-105.662,1.6) rot=(0,0,1;3.14159rad)
FEATURE [Part::Feature] Part__Feature071  label="COMPOUND065"
  shape: bbox 15 x 15 x 11.8 mm, 252 faces, 6 solids (baked)
FEATURE [App::Part] ks33065
  Group = -> [Part__Feature071]
  Origin = -> Origin168
  Placement = pos=(90.4875,-105.662,1.6) rot=(0,0,1;3.14159rad)
FEATURE [Part::Feature] Part__Feature072  label="COMPOUND066"
  shape: bbox 15 x 15 x 11.8 mm, 252 faces, 6 solids (baked)
FEATURE [App::Part] ks33066
  Group = -> [Part__Feature072]
  Origin = -> Origin169
  Placement = pos=(138.113,-86.6125,1.6) rot=(0,0,1;3.14159rad)
FEATURE [Part::Feature] Part__Feature073  label="COMPOUND067"
  shape: bbox 15 x 15 x 11.8 mm, 252 faces, 6 solids (baked)
FEATURE [App::Part] ks33067
  Group = -> [Part__Feature073]
  Origin = -> Origin170
  Placement = pos=(252.412,-86.6125,1.6) rot=(0,0,1;3.14159rad)
FEATURE [Part::Feature] Part__Feature074  label="COMPOUND068"
  shape: bbox 15 x 15 x 11.8 mm, 252 faces, 6 solids (baked)
FEATURE [App::Part] ks33068
  Group = -> [Part__Feature074]
  Origin = -> Origin171
  Placement = pos=(185.738,-105.662,1.6) rot=(0,0,1;3.14159rad)
FEATURE [Part::Feature] Part__Feature075  label="COMPOUND069"
  shape: bbox 15 x 15 x 11.8 mm, 252 faces, 6 solids (baked)
FEATURE [App::Part] ks33069
  Group = -> [Part__Feature075]
  Origin = -> Origin172
  Placement = pos=(266.7,-67.5625,1.6) rot=(0,0,1;3.14159rad)
FEATURE [Part::Feature] Part__Feature076  label="COMPOUND070"
  shape: bbox 15 x 15 x 11.8 mm, 252 faces, 6 solids (baked)
FEATURE [App::Part] ks33070
  Group = -> [Part__Feature076]
  Origin = -> Origin173
  Placement = pos=(290.512,-24.7,1.6) rot=(0,0,1;3.14159rad)
FEATURE [Part::Feature] Part__Feature077  label="COMPOUND071"
  shape: bbox 15 x 15 x 11.8 mm, 252 faces, 6 solids (baked)
FEATURE [App::Part] ks33071
  Group = -> [Part__Feature077]
  Origin = -> Origin174
  Placement = pos=(257.175,-124.713,1.6) rot=(0,0,1;3.14159rad)
FEATURE [Part::Feature] Part__Feature078  label="COMPOUND072"
  shape: bbox 15 x 15 x 11.8 mm, 252 faces, 6 solids (baked)
FEATURE [App::Part] ks33072
  Group = -> [Part__Feature078]
  Origin = -> Origin175
  Placement = pos=(204.787,-105.662,1.6) rot=(0,0,1;3.14159rad)
FEATURE [Part::Feature] Part__Feature079  label="COMPOUND073"
  shape: bbox 15 x 15 x 11.8 mm, 252 faces, 6 solids (baked)
FEATURE [App::Part] ks33073
  Group = -> [Part__Feature079]
  Origin = -> Origin176
  Placement = pos=(76.2,-67.5625,1.6) rot=(0,0,1;3.14159rad)
FEATURE [Part::Feature] Part__Feature080  label="COMPOUND074"
  shape: bbox 15 x 15 x 11.8 mm, 252 faces, 6 solids (baked)
FEATURE [App::Part] ks33074
  Group = -> [Part__Feature080]
  Origin = -> Origin177
  Placement = pos=(304.8,-48.5125,1.6) rot=(0,0,1;3.14159rad)
FEATURE [Part::Feature] Part__Feature081  label="COMPOUND075"
  shape: bbox 15 x 15 x 11.8 mm, 252 faces, 6 solids (baked)
FEATURE [App::Part] ks33075
  Group = -> [Part__Feature081]
  Origin = -> Origin178
  Placement = pos=(66.675,-48.5125,1.6) rot=(0,0,1;3.14159rad)
FEATURE [Part::Feature] Part__Feature082  label="COMPOUND076"
  shape: bbox 8.94 x 7.78 x 4.26 mm, 646 faces, 36 solids (baked)
FEATURE [App::Part] USB_C_Receptacle_GCT_USB4105_xx_A_16P_TopMnt_Horizontal  label="USB_C_Receptacle_GCT_USB4105-xx-A_16P_TopMnt_Horizontal"
  Group = -> [Part__Feature082]
  Origin = -> Origin179
  Placement = pos=(257.692,-2.39875,1.65) rot=(0,0,1;3.14159rad)
FEATURE [Part::Feature] Part__Feature083  label="COMPOUND077"
  shape: bbox 15 x 15 x 11.8 mm, 252 faces, 6 solids (baked)
FEATURE [App::Part] ks33076
  Group = -> [Part__Feature083]
  Origin = -> Origin180
  Placement = pos=(71.4375,-24.7,1.6) rot=(0,0,1;3.14159rad)
FEATURE [Part::Feature] Part__Feature084  label="COMPOUND078"
  shape: bbox 15 x 15 x 11.8 mm, 252 faces, 6 solids (baked)
FEATURE [App::Part] ks33077
  Group = -> [Part__Feature084]
  Origin = -> Origin181
  Placement = pos=(257.175,-48.5125,1.6) rot=(0,0,1;3.14159rad)
FEATURE [Part::Feature] Part__Feature085  label="COMPOUND079"
  shape: bbox 15 x 15 x 11.8 mm, 252 faces, 6 solids (baked)
FEATURE [App::Part] ks33078
  Group = -> [Part__Feature085]
  Origin = -> Origin182
  Placement = pos=(247.65,-67.5625,1.6) rot=(0,0,1;3.14159rad)
FEATURE [Part::Feature] Part__Feature086  label="COMPOUND080"
  shape: bbox 15 x 15 x 11.8 mm, 252 faces, 6 solids (baked)
FEATURE [App::Part] ks33079
  Group = -> [Part__Feature086]
  Origin = -> Origin183
  Placement = pos=(271.462,-24.7,1.6) rot=(0,0,1;3.14159rad)
FEATURE [Part::Feature] Part__Feature087  label="COMPOUND081"
  shape: bbox 51.22 x 27.32 x 7.001 mm, 2041 faces, 49 solids (baked)
FEATURE [App::Part] __9inch_lcd_module  label="1_9inch-lcd-module"
  Group = -> [Part__Feature087]
  Origin = -> Origin184
  Placement = pos=(32.7,-93.1625,4.5) rot=(0,0,1;1.5708rad)
FEATURE [Part::Feature] Part__Feature088  label="COMPOUND082"
  shape: bbox 15 x 15 x 11.8 mm, 252 faces, 6 solids (baked)
FEATURE [App::Part] ks33080
  Group = -> [Part__Feature088]
  Origin = -> Origin185
  Placement = pos=(52.3875,-67.5625,1.6) rot=(0,0,1;3.14159rad)
FEATURE [Part::Feature] Part__Feature089  label="COMPOUND083"
  shape: bbox 15 x 15 x 11.8 mm, 252 faces, 6 solids (baked)
FEATURE [App::Part] ks33081
  Group = -> [Part__Feature089]
  Origin = -> Origin186
  Placement = pos=(200.025,-48.5125,1.6) rot=(0,0,1;3.14159rad)
FEATURE [Part::Feature] Part__Feature090  label="COMPOUND084"
  shape: bbox 15 x 15 x 11.8 mm, 252 faces, 6 solids (baked)
FEATURE [App::Part] ks33082
  Group = -> [Part__Feature090]
  Origin = -> Origin187
  Placement = pos=(128.588,-24.7,1.6) rot=(0,0,1;3.14159rad)
FEATURE [Part::Feature] Part__Feature091  label="COMPOUND085"
  shape: bbox 15.35 x 5.364 x 3.552 mm, 431 faces, 3 solids (baked)
FEATURE [App::Part] JST___GH___SMD__R____8Pin___1_25mm  label="JST - GH - SMD (R) - 8Pin - 1.25mm"
  Group = -> [Part__Feature091]
  Origin = -> Origin188
  Placement = pos=(19.05,-45.925,-0.05) rot=(1,0,0;3.14159rad)
FEATURE [Part::Feature] Part__Feature092  label="SOLID006"
  shape: bbox 7.9 x 5.275 x 2.055 mm, 156 faces (baked)
FEATURE [App::Part] SOIC_8_5_275x5_275mm_P1_27mm  label="SOIC-8_5.275x5.275mm_P1.27mm"
  Group = -> [Part__Feature092]
  Origin = -> Origin189
  Placement = pos=(345.233,-5.0525,-0.05) rot=(1,0,0;3.14159rad)
FEATURE [Part::Feature] Part__Feature093  label="SOLID007"
  shape: bbox 6.401 x 5.201 x 1.541 mm, 193 faces (baked)
FEATURE [App::Part] SW_SPST_TL3342
  Group = -> [Part__Feature093]
  Origin = -> Origin190
  Placement = pos=(345.752,-11.9925,-0.05) rot=(0,1,0;3.14159rad)
FEATURE [Part::Feature] Part__Feature094  label="SOLID008"
  shape: bbox 2.5 x 3 x 1.2 mm, 76 faces (baked)
FEATURE [App::Part] SOT_23  label="SOT-23"
  Group = -> [Part__Feature094]
  Origin = -> Origin191
  Placement = pos=(297.493,-2.09,-0.05) rot=(0,1,0;3.14159rad)
FEATURE [Part::Feature] Part__Feature095  label="Pixelette PCB"
  shape: bbox 352.4 x 139 x 1.6 mm, 582 faces (baked)
FEATURE [Sketcher::SketchObject] Sketch014
  AttachmentOffset = pos=(0,0,5) rot=(0,0,1;0rad)
  FullyConstrained = false
  MapMode = 5
  Placement = pos=(0,0,5) rot=(0,0,1;0rad)
  Support = -> [XY_Plane097]
  expr: Constraints[5] = Spreadsheet.PCB_length
  expr: Constraints[9] = 8 + 1.5 + 5
  sketch-geometry (19):
    g0: GeomPoint X=352.425 Y=3.90395 Z=0
    g1: GeomPoint X=263.925 Y=-8 Z=0
    g2: GeomPoint X=251.425 Y=-8 Z=0
    g3: LineSegment StartX=253.425 StartY=-8 StartZ=0 EndX=261.925 EndY=-8 EndZ=0
    g4: LineSegment StartX=251.425 StartY=-6 StartZ=0 EndX=251.425 EndY=4.5 EndZ=0
    g5: LineSegment StartX=263.925 StartY=-6 StartZ=0 EndX=263.925 EndY=4.5 EndZ=0
    g6: LineSegment StartX=249.425 StartY=6.5 StartZ=0 EndX=-27.3647 EndY=6.5 EndZ=0
    g7: LineSegment StartX=265.925 StartY=6.5 StartZ=0 EndX=398.557 EndY=6.5 EndZ=0
    g8: LineSegment StartX=398.557 StartY=6.5 StartZ=0 EndX=398.557 EndY=82.3248 EndZ=0
    g9: LineSegment StartX=398.557 StartY=82.3248 StartZ=0 EndX=-27.3647 EndY=82.3248 EndZ=0
    g10: LineSegment StartX=-27.3647 StartY=82.3248 StartZ=0 EndX=-27.3647 EndY=6.5 EndZ=0
    g11: ArcOfCircle CenterX=249.425 CenterY=4.5 CenterZ=0 NormalX=0 NormalY=0 NormalZ=1 AngleXU=0 Radius=2 StartAngle=1e-16 EndAngle=1.5708
    g12: GeomPoint X=251.425 Y=6.5 Z=0
    g13: ArcOfCircle CenterX=265.925 CenterY=4.5 CenterZ=0 NormalX=0 NormalY=0 NormalZ=1 AngleXU=0 Radius=2 StartAngle=1.5708 EndAngle=3.14159
    g14: GeomPoint X=263.925 Y=6.5 Z=0
    g15: ArcOfCircle CenterX=261.925 CenterY=-6 CenterZ=0 NormalX=0 NormalY=0 NormalZ=1 AngleXU=0 Radius=2 StartAngle=4.71239 EndAngle=6.28319
    g16: GeomPoint X=263.925 Y=-8 Z=0
    g17: ArcOfCircle CenterX=253.425 CenterY=-6 CenterZ=0 NormalX=0 NormalY=0 NormalZ=1 AngleXU=0 Radius=2 StartAngle=3.14159 EndAngle=4.71239
    g18: GeomPoint X=251.425 Y=-8 Z=0
  constraints (40):
    c: Coincident(g18,g2)
    c: Coincident(g16,g1)
    c: Horizontal(g3)
    c: DistanceX(g16,g0) = 88.5
    c: DistanceX(g18,g0) = 101
    c: DistanceX(g-1,g0) = 352.425
    c: DistanceY(g18,g-1) = 8
    c: Vertical(g4)
    c: Vertical(g5)
    c: DistanceY(g18,g12) = 14.5
    c: Horizontal(g12,g14)
    c: Horizontal(g6)
    c: Horizontal(g7)
    c: Vertical(g8)
    c: Coincident(g9,g8)
    c: Horizontal(g9)
    c: Coincident(g10,g6)
    c: Vertical(g10)
    c: PointOnObject(g12,g4)
    c: PointOnObject(g12,g6)
    c: Tangent(g4,g11) = -1.5708
    c: Tangent(g6,g11) = -1.5708
    c: PointOnObject(g14,g5)
    c: PointOnObject(g14,g7)
    c: Tangent(g5,g13) = 1.5708
    c: Tangent(g7,g13) = 1.5708
    c: Radius(g11) = 2
    c: Radius(g13) = 2
    c: Coincident(g7,g8)
    c: Coincident(g9,g10)
    c: PointOnObject(g16,g5)
    c: PointOnObject(g16,g3)
    c: Tangent(g5,g15) = -1.5708
    c: Tangent(g3,g15) = -1.5708
    c: PointOnObject(g18,g3)
    c: PointOnObject(g18,g4)
    c: Tangent(g3,g17) = -1.5708
    c: Tangent(g4,g17) = 1.5708
    c: Radius(g17) = 2
    c: Radius(g15) = 2
FEATURE [PartDesign::Pocket] Pocket013
  BaseFeature = -> Pocket012
  Direction = (0,0,-1)
  Length = 5
  Length2 = 5
  Profile = -> Sketch014
  ReferenceAxis = -> Sketch014 [N_Axis]
  Type = 0
FEATURE [PartDesign::Body] Body
  Group = -> [Sketch,Sketch001,Pad,Sketch002,Pocket,Pocket001,Sketch003,Pocket002,Sketch004,Pocket003,Sketch005,Pocket004,Sketch006,Pocket005,Sketch007,Pocket006,Sketch008,Pocket007,Sketch009,Pocket008,Sketch010,Pocket009,Sketch011,Pocket010,Sketch012,Pocket011,Sketch013,Pocket012,Sketch014,Pocket013]
  Origin = -> Origin097
  Tip = -> Pocket013
FEATURE [Sketcher::SketchObject] Sketch015
  AttachmentOffset = pos=(0,0,2.9) rot=(0,0,1;0rad)
  FullyConstrained = false
  MapMode = 5
  Placement = pos=(0,0,2.9) rot=(0,0,1;0rad)
  Support = -> [XY_Plane194]
  expr: .AttachmentOffset.Base.z = 1.6 + 1.3
  expr: Constraints[25] = Spreadsheet.Bottom_c_rad
  expr: Constraints[26] = Spreadsheet.Bottom_c_rad
  expr: Constraints[29] = Spreadsheet.Spacer_hole
  expr: Constraints[36] = Spreadsheet.PCB_length + Spreadsheet.pcb_to_wall_gap * 2
  expr: Constraints[37] = Spreadsheet.PCB_width + Spreadsheet.pcb_to_wall_gap * 2
  expr: Constraints[54] = Spreadsheet.Bottom_c_rad
  expr: Constraints[57] = Spreadsheet.Bottom_c_rad
  expr: Constraints[5] = Spreadsheet.PCB_length / 2
  expr: Constraints[60] = 2 * Spreadsheet.Top_c_rad * sin(45 / 2)
  expr: Constraints[61] = 2 * Spreadsheet.Top_c_rad * sin(45 / 2)
  expr: Constraints[66] = 2 * Spreadsheet.Top_c_rad * sin(45 / 2)
  expr: Constraints[67] = 2 * Spreadsheet.Top_c_rad * sin(45 / 2)
  expr: Constraints[6] = Spreadsheet.PCB_width / 2
  expr: Constraints[72] = Spreadsheet.wall_thickness / 2
  expr: Constraints[73] = Spreadsheet.PCB_length / 2
  expr: Constraints[74] = (Spreadsheet.PCB_length + Spreadsheet.pcb_to_wall_gap * 2 + Spreadsheet.wall_thickness * 2) / 4
  expr: Constraints[75] = (Spreadsheet.PCB_length + Spreadsheet.pcb_to_wall_gap * 2 + Spreadsheet.wall_thickness * 2) / 4
  expr: Constraints[7] = Spreadsheet.PCB_width + 2 * Spreadsheet.pcb_to_wall_gap + 2 * Spreadsheet.wall_thickness
  expr: Constraints[83] = Spreadsheet.wall_thickness / 2
  expr: Constraints[88] = 2 * Spreadsheet.Bottom_c_rad * sin(45 / 2)
  expr: Constraints[89] = 2 * Spreadsheet.Bottom_c_rad * sin(45 / 2)
  expr: Constraints[8] = Spreadsheet.PCB_length + 2 * Spreadsheet.pcb_to_wall_gap + 2 * Spreadsheet.wall_thickness
  expr: Constraints[92] = 2 * Spreadsheet.Bottom_c_rad * sin(45 / 2)
  expr: Constraints[93] = 2 * Spreadsheet.Bottom_c_rad * sin(45 / 2)
  sketch-geometry (45):
    g0: LineSegment StartX=-6.5 StartY=0.5 StartZ=0 EndX=-6.5 EndY=-142.5 EndZ=0
    g1: LineSegment StartX=-3.5 StartY=-145.5 StartZ=0 EndX=355.925 EndY=-145.5 EndZ=0
    g2: LineSegment StartX=358.925 StartY=-142.5 StartZ=0 EndX=358.925 EndY=0.5 EndZ=0
    g3: LineSegment StartX=352.925 StartY=6.5 StartZ=0 EndX=-0.5 EndY=6.5 EndZ=0
    g4: GeomPoint X=176.213 Y=-69.5 Z=0
    g5: ArcOfCircle CenterX=-0.5 CenterY=0.5 CenterZ=0 NormalX=0 NormalY=0 NormalZ=1 AngleXU=0 Radius=6 StartAngle=1.5708 EndAngle=3.14159
    g6: GeomPoint X=-6.5 Y=6.5 Z=0
    g7: ArcOfCircle CenterX=352.925 CenterY=0.5 CenterZ=0 NormalX=0 NormalY=0 NormalZ=1 AngleXU=0 Radius=6 StartAngle=0 EndAngle=1.5708
    g8: GeomPoint X=358.925 Y=6.5 Z=0
    g9: ArcOfCircle CenterX=-3.5 CenterY=-142.5 CenterZ=0 NormalX=0 NormalY=0 NormalZ=1 AngleXU=0 Radius=3 StartAngle=3.14159 EndAngle=4.71239
    g10: GeomPoint X=-6.5 Y=-145.5 Z=0
    g11: ArcOfCircle CenterX=355.925 CenterY=-142.5 CenterZ=0 NormalX=0 NormalY=0 NormalZ=1 AngleXU=0 Radius=3 StartAngle=4.71239 EndAngle=6.28319
    g12: GeomPoint X=358.925 Y=-145.5 Z=0
    g13: Circle CenterX=-1.74264 CenterY=1.74264 CenterZ=0 NormalX=0 NormalY=0 NormalZ=1 AngleXU=0 Radius=1.55
    g14: LineSegment StartX=-0.5 StartY=-5.5 StartZ=0 EndX=-0.5 EndY=-136.5 EndZ=0
    g15: LineSegment StartX=2.5 StartY=-139.5 StartZ=0 EndX=349.925 EndY=-139.5 EndZ=0
    g16: LineSegment StartX=352.925 StartY=-136.5 StartZ=0 EndX=352.925 EndY=-5.5 EndZ=0
    g17: LineSegment StartX=346.925 StartY=0.5 StartZ=0 EndX=5.5 EndY=0.5 EndZ=0
    g18: GeomPoint X=176.213 Y=-69.5 Z=0
    g19: ArcOfCircle CenterX=5.5 CenterY=-5.5 CenterZ=0 NormalX=0 NormalY=0 NormalZ=1 AngleXU=0 Radius=6 StartAngle=1.5708 EndAngle=3.14159
    g20: GeomPoint X=-0.5 Y=0.5 Z=0
    g21: ArcOfCircle CenterX=346.925 CenterY=-5.5 CenterZ=0 NormalX=0 NormalY=0 NormalZ=1 AngleXU=0 Radius=6 StartAngle=0 EndAngle=1.5708
    g22: GeomPoint X=352.925 Y=0.5 Z=0
    g23: ArcOfCircle CenterX=349.925 CenterY=-136.5 CenterZ=0 NormalX=0 NormalY=0 NormalZ=1 AngleXU=0 Radius=3 StartAngle=4.71239 EndAngle=6.28319
    g24: GeomPoint X=352.925 Y=-139.5 Z=0
    g25: ArcOfCircle CenterX=2.5 CenterY=-136.5 CenterZ=0 NormalX=0 NormalY=0 NormalZ=1 AngleXU=0 Radius=3 StartAngle=3.14159 EndAngle=4.71239
    g26: GeomPoint X=-0.5 Y=-139.5 Z=0
    g27: GeomPoint X=-4.74264 Y=4.74264 Z=0
    g28: GeomPoint X=1.25736 Y=-1.25736 Z=0
    g29: Circle CenterX=354.168 CenterY=1.74264 CenterZ=0 NormalX=0 NormalY=0 NormalZ=1 AngleXU=0 Radius=1.55
    g30: GeomPoint X=351.168 Y=-1.25736 Z=0
    g31: GeomPoint X=357.168 Y=4.74264 Z=0
    g32: Circle CenterX=84.8563 CenterY=3.5 CenterZ=0 NormalX=0 NormalY=0 NormalZ=1 AngleXU=0 Radius=1.55
    g33: Circle CenterX=176.213 CenterY=3.5 CenterZ=0 NormalX=0 NormalY=0 NormalZ=1 AngleXU=0 Radius=1.55
    g34: Circle CenterX=267.569 CenterY=3.5 CenterZ=0 NormalX=0 NormalY=0 NormalZ=1 AngleXU=0 Radius=1.55
    g35: Circle CenterX=84.8563 CenterY=-142.5 CenterZ=0 NormalX=0 NormalY=0 NormalZ=1 AngleXU=0 Radius=1.55
    g36: Circle CenterX=176.213 CenterY=-142.5 CenterZ=0 NormalX=0 NormalY=0 NormalZ=1 AngleXU=0 Radius=1.55
    g37: Circle CenterX=267.569 CenterY=-142.5 CenterZ=0 NormalX=0 NormalY=0 NormalZ=1 AngleXU=0 Radius=1.55
    g38: Circle CenterX=-2.62132 CenterY=-141.621 CenterZ=0 NormalX=0 NormalY=0 NormalZ=1 AngleXU=0 Radius=1.55
    g39: GeomPoint X=0.37868 Y=-138.621 Z=0
    g40: GeomPoint X=-5.62132 Y=-144.621 Z=0
    g41: GeomPoint X=6.2644 Y=-139.5 Z=0
    g42: GeomPoint X=352.046 Y=-138.621 Z=0
    g43: GeomPoint X=358.046 Y=-144.621 Z=0
    g44: Circle CenterX=355.046 CenterY=-141.621 CenterZ=0 NormalX=0 NormalY=0 NormalZ=1 AngleXU=0 Radius=1.55
  constraints (100):
    c: Horizontal(g1)
    c: Horizontal(g3)
    c: Vertical(g0)
    c: Vertical(g2)
    c: Symmetric(g12,g6,g4)
    c: DistanceX(g-1,g4) = 176.213
    c: DistanceY(g4,g-1) = 69.5
    c: DistanceY(g10,g6) = 152
    c: DistanceX(g6,g8) = 365.425
    c: PointOnObject(g6,g0)
    c: PointOnObject(g6,g3)
    c: Tangent(g0,g5) = -1.5708
    c: Tangent(g3,g5) = -1.5708
    c: PointOnObject(g8,g2)
    c: PointOnObject(g8,g3)
    c: Tangent(g2,g7) = -1.5708
    c: Tangent(g3,g7) = -1.5708
    c: PointOnObject(g10,g0)
    c: PointOnObject(g10,g1)
    c: Tangent(g0,g9) = -1.5708
    c: Tangent(g1,g9) = -1.5708
    c: PointOnObject(g12,g1)
    c: PointOnObject(g12,g2)
    c: Tangent(g1,g11) = -1.5708
    c: Tangent(g2,g11) = -1.5708
    c: Radius(g11) = 3
    c: Radius(g9) = 3
    c: Radius(g5) = 6
    c: Radius(g7) = 6
    c: Diameter(g13) = 3.1
    c: Horizontal(g15)
    c: Horizontal(g17)
    c: Vertical(g14)
    c: Vertical(g16)
    c: Symmetric(g24,g20,g18)
    c: Coincident(g18,g4)
    c: DistanceX(g20,g22) = 353.425
    c: DistanceY(g26,g20) = 140
    c: PointOnObject(g20,g14)
    c: PointOnObject(g20,g17)
    c: Tangent(g14,g19) = -1.5708
    c: Tangent(g17,g19) = -1.5708
    c: PointOnObject(g22,g16)
    c: PointOnObject(g22,g17)
    c: Tangent(g16,g21) = -1.5708
    c: Tangent(g17,g21) = -1.5708
    c: PointOnObject(g24,g15)
    c: PointOnObject(g24,g16)
    c: Tangent(g15,g23) = -1.5708
    c: Tangent(g16,g23) = -1.5708
    c: PointOnObject(g26,g14)
    c: PointOnObject(g26,g15)
    c: Tangent(g14,g25) = -1.5708
    c: Tangent(g15,g25) = -1.5708
    c: Radius(g25) = 3
    c: Radius(g19) = 6
    c: Radius(g21) = 6
    c: Radius(g23) = 3
    c: PointOnObject(g27,g5)
    c: PointOnObject(g28,g19)
    c: Distance(g14,g28) = 4.5922
    c: Distance(g0,g27) = 4.5922
    c: Symmetric(g27,g28,g13)
    c: Diameter(g29) = 3.1
    c: PointOnObject(g30,g21)
    c: PointOnObject(g31,g7)
    c: Distance(g30,g16) = 4.5922
    c: Distance(g2,g31) = 4.5922
    c: Symmetric(g30,g31,g29)
    c: Equal(g32,g33)
    c: Equal(g34,g33)
    c: Diameter(g33) = 3.1
    c: Distance(g33,g3) = 3
    c: DistanceX(g-1,g33) = 176.213
    c: DistanceX(g32,g33) = 91.3563
    c: DistanceX(g33,g34) = 91.3563
    c: Equal(g35,g36)
    c: Equal(g37,g36)
    c: Equal(g33,g36) = 3.1
    c: DistanceX(g35,g36) = 91.3563
    c: DistanceX(g36,g37) = 91.3563
    c: Horizontal(g35,g36)
    c: Horizontal(g37,g36)
    c: Distance(g36,g1) = 3
    c: Vertical(g36,g33)
    c: PointOnObject(g39,g25)
    c: PointOnObject(g40,g9)
    c: PointOnObject(g41,g15)
    c: Distance(g39,g14) = 2.2961
    c: Distance(g0,g40) = 2.2961
    c: PointOnObject(g42,g23)
    c: PointOnObject(g43,g11)
    c: Distance(g15,g42) = 2.2961
    c: Distance(g1,g43) = 2.2961
    c: Symmetric(g42,g43,g44)
    c: Diameter(g44) = 3.1
    c: Diameter(g38) = 3.1
    c: Symmetric(g40,g39,g38)
    c: Horizontal(g32,g33)
    c: Horizontal(g34,g33)
FEATURE [PartDesign::Pad] Pad001
  Direction = (0,0,1)
  Length = 3
  Length2 = 10
  Profile = -> Sketch015
  ReferenceAxis = -> Sketch015 [N_Axis]
  Type = 0
FEATURE [Sketcher::SketchObject] Sketch016
  AttachmentOffset = pos=(0,0,2.9) rot=(0,0,1;0rad)
  FullyConstrained = false
  MapMode = 5
  Placement = pos=(0,0,2.9) rot=(0,0,1;0rad)
  Support = -> [XY_Plane195]
  expr: .AttachmentOffset.Base.z = 1.6 + 1.3
  expr: Constraints[25] = Spreadsheet.Bottom_c_rad
  expr: Constraints[26] = Spreadsheet.Bottom_c_rad
  expr: Constraints[29] = Spreadsheet.Spacer_hole
  expr: Constraints[36] = Spreadsheet.PCB_length + Spreadsheet.pcb_to_wall_gap * 2
  expr: Constraints[37] = Spreadsheet.PCB_width + Spreadsheet.pcb_to_wall_gap * 2
  expr: Constraints[54] = Spreadsheet.Bottom_c_rad
  expr: Constraints[57] = Spreadsheet.Bottom_c_rad
  expr: Constraints[5] = Spreadsheet.PCB_length / 2
  expr: Constraints[60] = 2 * Spreadsheet.Top_c_rad * sin(45 / 2)
  expr: Constraints[61] = 2 * Spreadsheet.Top_c_rad * sin(45 / 2)
  expr: Constraints[66] = 2 * Spreadsheet.Top_c_rad * sin(45 / 2)
  expr: Constraints[67] = 2 * Spreadsheet.Top_c_rad * sin(45 / 2)
  expr: Constraints[6] = Spreadsheet.PCB_width / 2
  expr: Constraints[72] = Spreadsheet.wall_thickness / 2
  expr: Constraints[73] = Spreadsheet.PCB_length / 2
  expr: Constraints[74] = (Spreadsheet.PCB_length + Spreadsheet.pcb_to_wall_gap * 2 + Spreadsheet.wall_thickness * 2) / 4
  expr: Constraints[75] = (Spreadsheet.PCB_length + Spreadsheet.pcb_to_wall_gap * 2 + Spreadsheet.wall_thickness * 2) / 4
  expr: Constraints[7] = Spreadsheet.PCB_width + 2 * Spreadsheet.pcb_to_wall_gap + 2 * Spreadsheet.wall_thickness
  expr: Constraints[83] = Spreadsheet.wall_thickness / 2
  expr: Constraints[88] = 2 * Spreadsheet.Bottom_c_rad * sin(45 / 2)
  expr: Constraints[89] = 2 * Spreadsheet.Bottom_c_rad * sin(45 / 2)
  expr: Constraints[8] = Spreadsheet.PCB_length + 2 * Spreadsheet.pcb_to_wall_gap + 2 * Spreadsheet.wall_thickness
  expr: Constraints[92] = 2 * Spreadsheet.Bottom_c_rad * sin(45 / 2)
  expr: Constraints[93] = 2 * Spreadsheet.Bottom_c_rad * sin(45 / 2)
  sketch-geometry (45):
    g0: LineSegment StartX=-6.5 StartY=0.5 StartZ=0 EndX=-6.5 EndY=-142.5 EndZ=0
    g1: LineSegment StartX=-3.5 StartY=-145.5 StartZ=0 EndX=355.925 EndY=-145.5 EndZ=0
    g2: LineSegment StartX=358.925 StartY=-142.5 StartZ=0 EndX=358.925 EndY=0.5 EndZ=0
    g3: LineSegment StartX=352.925 StartY=6.5 StartZ=0 EndX=-0.5 EndY=6.5 EndZ=0
    g4: GeomPoint X=176.213 Y=-69.5 Z=0
    g5: ArcOfCircle CenterX=-0.5 CenterY=0.5 CenterZ=0 NormalX=0 NormalY=0 NormalZ=1 AngleXU=0 Radius=6 StartAngle=1.5708 EndAngle=3.14159
    g6: GeomPoint X=-6.5 Y=6.5 Z=0
    g7: ArcOfCircle CenterX=352.925 CenterY=0.5 CenterZ=0 NormalX=0 NormalY=0 NormalZ=1 AngleXU=0 Radius=6 StartAngle=0 EndAngle=1.5708
    g8: GeomPoint X=358.925 Y=6.5 Z=0
    g9: ArcOfCircle CenterX=-3.5 CenterY=-142.5 CenterZ=0 NormalX=0 NormalY=0 NormalZ=1 AngleXU=0 Radius=3 StartAngle=3.14159 EndAngle=4.71239
    g10: GeomPoint X=-6.5 Y=-145.5 Z=0
    g11: ArcOfCircle CenterX=355.925 CenterY=-142.5 CenterZ=0 NormalX=0 NormalY=0 NormalZ=1 AngleXU=0 Radius=3 StartAngle=4.71239 EndAngle=6.28319
    g12: GeomPoint X=358.925 Y=-145.5 Z=0
    g13: Circle CenterX=-1.74264 CenterY=1.74264 CenterZ=0 NormalX=0 NormalY=0 NormalZ=1 AngleXU=0 Radius=1.55
    g14: LineSegment StartX=-0.5 StartY=-5.5 StartZ=0 EndX=-0.5 EndY=-136.5 EndZ=0
    g15: LineSegment StartX=2.5 StartY=-139.5 StartZ=0 EndX=349.925 EndY=-139.5 EndZ=0
    g16: LineSegment StartX=352.925 StartY=-136.5 StartZ=0 EndX=352.925 EndY=-5.5 EndZ=0
    g17: LineSegment StartX=346.925 StartY=0.5 StartZ=0 EndX=5.5 EndY=0.5 EndZ=0
    g18: GeomPoint X=176.213 Y=-69.5 Z=0
    g19: ArcOfCircle CenterX=5.5 CenterY=-5.5 CenterZ=0 NormalX=0 NormalY=0 NormalZ=1 AngleXU=0 Radius=6 StartAngle=1.5708 EndAngle=3.14159
    g20: GeomPoint X=-0.5 Y=0.5 Z=0
    g21: ArcOfCircle CenterX=346.925 CenterY=-5.5 CenterZ=0 NormalX=0 NormalY=0 NormalZ=1 AngleXU=0 Radius=6 StartAngle=0 EndAngle=1.5708
    g22: GeomPoint X=352.925 Y=0.5 Z=0
    g23: ArcOfCircle CenterX=349.925 CenterY=-136.5 CenterZ=0 NormalX=0 NormalY=0 NormalZ=1 AngleXU=0 Radius=3 StartAngle=4.71239 EndAngle=6.28319
    g24: GeomPoint X=352.925 Y=-139.5 Z=0
    g25: ArcOfCircle CenterX=2.5 CenterY=-136.5 CenterZ=0 NormalX=0 NormalY=0 NormalZ=1 AngleXU=0 Radius=3 StartAngle=3.14159 EndAngle=4.71239
    g26: GeomPoint X=-0.5 Y=-139.5 Z=0
    g27: GeomPoint X=-4.74264 Y=4.74264 Z=0
    g28: GeomPoint X=1.25736 Y=-1.25736 Z=0
    g29: Circle CenterX=354.168 CenterY=1.74264 CenterZ=0 NormalX=0 NormalY=0 NormalZ=1 AngleXU=0 Radius=1.55
    g30: GeomPoint X=351.168 Y=-1.25736 Z=0
    g31: GeomPoint X=357.168 Y=4.74264 Z=0
    g32: Circle CenterX=84.8563 CenterY=3.5 CenterZ=0 NormalX=0 NormalY=0 NormalZ=1 AngleXU=0 Radius=1.55
    g33: Circle CenterX=176.213 CenterY=3.5 CenterZ=0 NormalX=0 NormalY=0 NormalZ=1 AngleXU=0 Radius=1.55
    g34: Circle CenterX=267.569 CenterY=3.5 CenterZ=0 NormalX=0 NormalY=0 NormalZ=1 AngleXU=0 Radius=1.55
    g35: Circle CenterX=84.8563 CenterY=-142.5 CenterZ=0 NormalX=0 NormalY=0 NormalZ=1 AngleXU=0 Radius=1.55
    g36: Circle CenterX=176.213 CenterY=-142.5 CenterZ=0 NormalX=0 NormalY=0 NormalZ=1 AngleXU=0 Radius=1.55
    g37: Circle CenterX=267.569 CenterY=-142.5 CenterZ=0 NormalX=0 NormalY=0 NormalZ=1 AngleXU=0 Radius=1.55
    g38: Circle CenterX=-2.62132 CenterY=-141.621 CenterZ=0 NormalX=0 NormalY=0 NormalZ=1 AngleXU=0 Radius=1.55
    g39: GeomPoint X=0.37868 Y=-138.621 Z=0
    g40: GeomPoint X=-5.62132 Y=-144.621 Z=0
    g41: GeomPoint X=6.2644 Y=-139.5 Z=0
    g42: GeomPoint X=352.046 Y=-138.621 Z=0
    g43: GeomPoint X=358.046 Y=-144.621 Z=0
    g44: Circle CenterX=355.046 CenterY=-141.621 CenterZ=0 NormalX=0 NormalY=0 NormalZ=1 AngleXU=0 Radius=1.55
  constraints (100):
    c: Horizontal(g1)
    c: Horizontal(g3)
    c: Vertical(g0)
    c: Vertical(g2)
    c: Symmetric(g12,g6,g4)
    c: DistanceX(g-1,g4) = 176.213
    c: DistanceY(g4,g-1) = 69.5
    c: DistanceY(g10,g6) = 152
    c: DistanceX(g6,g8) = 365.425
    c: PointOnObject(g6,g0)
    c: PointOnObject(g6,g3)
    c: Tangent(g0,g5) = -1.5708
    c: Tangent(g3,g5) = -1.5708
    c: PointOnObject(g8,g2)
    c: PointOnObject(g8,g3)
    c: Tangent(g2,g7) = -1.5708
    c: Tangent(g3,g7) = -1.5708
    c: PointOnObject(g10,g0)
    c: PointOnObject(g10,g1)
    c: Tangent(g0,g9) = -1.5708
    c: Tangent(g1,g9) = -1.5708
    c: PointOnObject(g12,g1)
    c: PointOnObject(g12,g2)
    c: Tangent(g1,g11) = -1.5708
    c: Tangent(g2,g11) = -1.5708
    c: Radius(g11) = 3
    c: Radius(g9) = 3
    c: Radius(g5) = 6
    c: Radius(g7) = 6
    c: Diameter(g13) = 3.1
    c: Horizontal(g15)
    c: Horizontal(g17)
    c: Vertical(g14)
    c: Vertical(g16)
    c: Symmetric(g24,g20,g18)
    c: Coincident(g18,g4)
    c: DistanceX(g20,g22) = 353.425
    c: DistanceY(g26,g20) = 140
    c: PointOnObject(g20,g14)
    c: PointOnObject(g20,g17)
    c: Tangent(g14,g19) = -1.5708
    c: Tangent(g17,g19) = -1.5708
    c: PointOnObject(g22,g16)
    c: PointOnObject(g22,g17)
    c: Tangent(g16,g21) = -1.5708
    c: Tangent(g17,g21) = -1.5708
    c: PointOnObject(g24,g15)
    c: PointOnObject(g24,g16)
    c: Tangent(g15,g23) = -1.5708
    c: Tangent(g16,g23) = -1.5708
    c: PointOnObject(g26,g14)
    c: PointOnObject(g26,g15)
    c: Tangent(g14,g25) = -1.5708
    c: Tangent(g15,g25) = -1.5708
    c: Radius(g25) = 3
    c: Radius(g19) = 6
    c: Radius(g21) = 6
    c: Radius(g23) = 3
    c: PointOnObject(g27,g5)
    c: PointOnObject(g28,g19)
    c: Distance(g14,g28) = 4.5922
    c: Distance(g0,g27) = 4.5922
    c: Symmetric(g27,g28,g13)
    c: Diameter(g29) = 3.1
    c: PointOnObject(g30,g21)
    c: PointOnObject(g31,g7)
    c: Distance(g30,g16) = 4.5922
    c: Distance(g2,g31) = 4.5922
    c: Symmetric(g30,g31,g29)
    c: Equal(g32,g33)
    c: Equal(g34,g33)
    c: Diameter(g33) = 3.1
    c: Distance(g33,g3) = 3
    c: DistanceX(g-1,g33) = 176.213
    c: DistanceX(g32,g33) = 91.3563
    c: DistanceX(g33,g34) = 91.3563
    c: Equal(g35,g36)
    c: Equal(g37,g36)
    c: Equal(g33,g36) = 3.1
    c: DistanceX(g35,g36) = 91.3563
    c: DistanceX(g36,g37) = 91.3563
    c: Horizontal(g35,g36)
    c: Horizontal(g37,g36)
    c: Distance(g36,g1) = 3
    c: Vertical(g36,g33)
    c: PointOnObject(g39,g25)
    c: PointOnObject(g40,g9)
    c: PointOnObject(g41,g15)
    c: Distance(g39,g14) = 2.2961
    c: Distance(g0,g40) = 2.2961
    c: PointOnObject(g42,g23)
    c: PointOnObject(g43,g11)
    c: Distance(g15,g42) = 2.2961
    c: Distance(g1,g43) = 2.2961
    c: Symmetric(g42,g43,g44)
    c: Diameter(g44) = 3.1
    c: Diameter(g38) = 3.1
    c: Symmetric(g40,g39,g38)
    c: Horizontal(g32,g33)
    c: Horizontal(g34,g33)
FEATURE [PartDesign::Pad] Pad002
  Direction = (0,0,1)
  Length = 3
  Length2 = 10
  Profile = -> Sketch016
  ReferenceAxis = -> Sketch016 [N_Axis]
  Type = 0
FEATURE [PartDesign::Body] Body002  label="Body003"
  Group = -> [Sketch016,Pad002]
  Origin = -> Origin195
  Placement = pos=(0,0,-6) rot=(0,0,1;0rad)
  Tip = -> Pad002
FEATURE [Sketcher::SketchObject] Sketch017
  AttachmentOffset = pos=(0,0,2.9) rot=(0,0,1;0rad)
  FullyConstrained = false
  MapMode = 5
  Placement = pos=(0,0,2.9) rot=(0,0,1;0rad)
  Support = -> [XY_Plane196]
  expr: .AttachmentOffset.Base.z = 1.6 + 1.3
  expr: Constraints[25] = Spreadsheet.Bottom_c_rad
  expr: Constraints[26] = Spreadsheet.Bottom_c_rad
  expr: Constraints[29] = Spreadsheet.Spacer_hole
  expr: Constraints[32] = Spreadsheet.PCB_length + Spreadsheet.pcb_to_wall_gap * 2
  expr: Constraints[33] = Spreadsheet.PCB_width + Spreadsheet.pcb_to_wall_gap * 2
  expr: Constraints[35] = 2 * Spreadsheet.Top_c_rad * sin(45 / 2)
  expr: Constraints[37] = Spreadsheet.Spacer_hole
  expr: Constraints[39] = 2 * Spreadsheet.Top_c_rad * sin(45 / 2)
  expr: Constraints[43] = Spreadsheet.Spacer_hole
  expr: Constraints[44] = Spreadsheet.wall_thickness / 2
  expr: Constraints[45] = Spreadsheet.PCB_length / 2
  expr: Constraints[46] = (Spreadsheet.PCB_length + Spreadsheet.pcb_to_wall_gap * 2 + Spreadsheet.wall_thickness * 2) / 4
  expr: Constraints[47] = (Spreadsheet.PCB_length + Spreadsheet.pcb_to_wall_gap * 2 + Spreadsheet.wall_thickness * 2) / 4
  expr: Constraints[54] = Spreadsheet.wall_thickness / 2
  expr: Constraints[57] = 2 * Spreadsheet.Bottom_c_rad * sin(45 / 2)
  expr: Constraints[59] = 2 * Spreadsheet.Bottom_c_rad * sin(45 / 2)
  expr: Constraints[5] = Spreadsheet.PCB_length / 2
  expr: Constraints[61] = Spreadsheet.Screw_hole
  expr: Constraints[62] = Spreadsheet.Screw_hole
  expr: Constraints[66] = Spreadsheet.Screw_hole
  expr: Constraints[6] = Spreadsheet.PCB_width / 2
  expr: Constraints[7] = Spreadsheet.PCB_width + 2 * Spreadsheet.pcb_to_wall_gap + 2 * Spreadsheet.wall_thickness
  expr: Constraints[8] = Spreadsheet.PCB_length + 2 * Spreadsheet.pcb_to_wall_gap + 2 * Spreadsheet.wall_thickness
  sketch-geometry (36):
    g0: LineSegment StartX=-6.5 StartY=0.5 StartZ=0 EndX=-6.5 EndY=-142.5 EndZ=0
    g1: LineSegment StartX=-3.5 StartY=-145.5 StartZ=0 EndX=355.925 EndY=-145.5 EndZ=0
    g2: LineSegment StartX=358.925 StartY=-142.5 StartZ=0 EndX=358.925 EndY=0.5 EndZ=0
    g3: LineSegment StartX=352.925 StartY=6.5 StartZ=0 EndX=-0.5 EndY=6.5 EndZ=0
    g4: GeomPoint X=176.213 Y=-69.5 Z=0
    g5: ArcOfCircle CenterX=-0.5 CenterY=0.5 CenterZ=0 NormalX=0 NormalY=0 NormalZ=1 AngleXU=0 Radius=6 StartAngle=1.5708 EndAngle=3.14159
    g6: GeomPoint X=-6.5 Y=6.5 Z=0
    g7: ArcOfCircle CenterX=352.925 CenterY=0.5 CenterZ=0 NormalX=0 NormalY=0 NormalZ=1 AngleXU=0 Radius=6 StartAngle=0 EndAngle=1.5708
    g8: GeomPoint X=358.925 Y=6.5 Z=0
    g9: ArcOfCircle CenterX=-3.5 CenterY=-142.5 CenterZ=0 NormalX=0 NormalY=0 NormalZ=1 AngleXU=0 Radius=3 StartAngle=3.14159 EndAngle=4.71239
    g10: GeomPoint X=-6.5 Y=-145.5 Z=0
    g11: ArcOfCircle CenterX=355.925 CenterY=-142.5 CenterZ=0 NormalX=0 NormalY=0 NormalZ=1 AngleXU=0 Radius=3 StartAngle=4.71239 EndAngle=6.28319
    g12: GeomPoint X=358.925 Y=-145.5 Z=0
    g13: Circle CenterX=-1.74259 CenterY=1.74261 CenterZ=0 NormalX=0 NormalY=0 NormalZ=1 AngleXU=0 Radius=1.55
    g14: GeomPoint X=176.213 Y=-69.5 Z=0
    g15: GeomPoint X=-1.67193 Y=0.402977 Z=0
    g16: GeomPoint X=351.753 Y=0.5 Z=0
    g17: GeomPoint X=354.097 Y=-139.403 Z=0
    g18: GeomPoint X=-0.5 Y=-139.597 Z=0
    g19: GeomPoint X=-4.74264 Y=4.74264 Z=0
    g20: GeomPoint X=1.25746 Y=-1.25743 Z=0
    g21: Circle CenterX=354.168 CenterY=1.74261 CenterZ=0 NormalX=0 NormalY=0 NormalZ=1 AngleXU=0 Radius=1.55
    g22: GeomPoint X=351.168 Y=-1.25743 Z=0
    g23: GeomPoint X=357.168 Y=4.74264 Z=0
    g24: Circle CenterX=84.8563 CenterY=3.5 CenterZ=0 NormalX=0 NormalY=0 NormalZ=1 AngleXU=0 Radius=1.55
    g25: Circle CenterX=176.213 CenterY=3.5 CenterZ=0 NormalX=0 NormalY=0 NormalZ=1 AngleXU=0 Radius=1.55
    g26: Circle CenterX=267.569 CenterY=3.5 CenterZ=0 NormalX=0 NormalY=0 NormalZ=1 AngleXU=0 Radius=1.55
    g27: Circle CenterX=84.8563 CenterY=-142.5 CenterZ=0 NormalX=0 NormalY=0 NormalZ=1 AngleXU=0 Radius=1.05
    g28: Circle CenterX=176.213 CenterY=-142.5 CenterZ=0 NormalX=0 NormalY=0 NormalZ=1 AngleXU=0 Radius=1.05
    g29: Circle CenterX=267.569 CenterY=-142.5 CenterZ=0 NormalX=0 NormalY=0 NormalZ=1 AngleXU=0 Radius=1.05
    g30: Circle CenterX=-2.62127 CenterY=-141.621 CenterZ=0 NormalX=0 NormalY=0 NormalZ=1 AngleXU=0 Radius=1.05
    g31: GeomPoint X=0.378778 Y=-138.621 Z=0
    g32: GeomPoint X=-5.62132 Y=-144.621 Z=0
    g33: GeomPoint X=352.047 Y=-138.621 Z=0
    g34: GeomPoint X=358.046 Y=-144.621 Z=0
    g35: Circle CenterX=355.047 CenterY=-141.621 CenterZ=0 NormalX=0 NormalY=0 NormalZ=1 AngleXU=0 Radius=1.05
  constraints (67):
    c: Horizontal(g1)
    c: Horizontal(g3)
    c: Vertical(g0)
    c: Vertical(g2)
    c: Symmetric(g12,g6,g4)
    c: DistanceX(g-1,g4) = 176.213
    c: DistanceY(g4,g-1) = 69.5
    c: DistanceY(g10,g6) = 152
    c: DistanceX(g6,g8) = 365.425
    c: PointOnObject(g6,g0)
    c: PointOnObject(g6,g3)
    c: Tangent(g0,g5) = -1.5708
    c: Tangent(g3,g5) = -1.5708
    c: PointOnObject(g8,g2)
    c: PointOnObject(g8,g3)
    c: Tangent(g2,g7) = -1.5708
    c: Tangent(g3,g7) = -1.5708
    c: PointOnObject(g10,g0)
    c: PointOnObject(g10,g1)
    c: Tangent(g0,g9) = -1.5708
    c: Tangent(g1,g9) = -1.5708
    c: PointOnObject(g12,g1)
    c: PointOnObject(g12,g2)
    c: Tangent(g1,g11) = -1.5708
    c: Tangent(g2,g11) = -1.5708
    c: Radius(g11) = 3
    c: Radius(g9) = 3
    c: Radius(g5) = 6
    c: Radius(g7) = 6
    c: Diameter(g13) = 3.1
    c: Symmetric(g17,g15,g14)
    c: Coincident(g14,g4)
    c: DistanceX(g15,g16) = 353.425
    c: DistanceY(g18,g15) = 140
    c: PointOnObject(g19,g5)
    c: Distance(g0,g19) = 4.5922
    c: Symmetric(g19,g20,g13)
    c: Diameter(g21) = 3.1
    c: PointOnObject(g23,g7)
    c: Distance(g2,g23) = 4.5922
    c: Symmetric(g22,g23,g21)
    c: Equal(g24,g25)
    c: Equal(g26,g25)
    c: Diameter(g25) = 3.1
    c: Distance(g25,g3) = 3
    c: DistanceX(g-1,g25) = 176.213
    c: DistanceX(g24,g25) = 91.3563
    c: DistanceX(g25,g26) = 91.3563
    c: Equal(g27,g28)
    c: Equal(g29,g28)
    c: DistanceX(g27,g28) = 91.3563
    c: DistanceX(g28,g29) = 91.3563
    c: Horizontal(g27,g28)
    c: Horizontal(g29,g28)
    c: Distance(g28,g1) = 3
    c: Vertical(g28,g25)
    c: PointOnObject(g32,g9)
    c: Distance(g0,g32) = 2.2961
    c: PointOnObject(g34,g11)
    c: Distance(g1,g34) = 2.2961
    c: Symmetric(g33,g34,g35)
    c: Diameter(g35) = 2.1
    c: Diameter(g30) = 2.1
    c: Symmetric(g32,g31,g30)
    c: Horizontal(g24,g25)
    c: Horizontal(g26,g25)
    c: Diameter(g28) = 2.1
FEATURE [PartDesign::Pad] Pad003
  Direction = (0,0,1)
  Length = 3
  Length2 = 10
  Profile = -> Sketch017
  ReferenceAxis = -> Sketch017 [N_Axis]
  Type = 0
FEATURE [Part::Feature] Part__Feature096  label="button_smd_6x6xH"
  Placement = pos=(9.525,-105.662,1.6) rot=(0,0,1;0rad)
  shape: bbox 6 x 8 x 8 mm, 97 faces (baked)
  expr: .Placement.Base.x = Spreadsheet.u / 2
  expr: .Placement.Base.y = (Spreadsheet.PCB_width - Spreadsheet.u * 1.75) * -1
FEATURE [Part::Feature] Part__Feature097  label="button_smd_6x6xH001"
  Placement = pos=(28.575,-105.662,1.6) rot=(0,0,1;0rad)
  shape: bbox 6 x 8 x 8 mm, 97 faces (baked)
  expr: .Placement.Base.x = Spreadsheet.u * 2 - Spreadsheet.u / 2
  expr: .Placement.Base.y = (Spreadsheet.PCB_width - Spreadsheet.u * 1.75) * -1
FEATURE [Part::Feature] Part__Feature098  label="button_smd_6x6xH002"
  Placement = pos=(9.525,-124.713,1.6) rot=(0,0,1;0rad)
  shape: bbox 6 x 8 x 8 mm, 97 faces (baked)
  expr: .Placement.Base.x = Spreadsheet.u / 2
  expr: .Placement.Base.y = (Spreadsheet.PCB_width - Spreadsheet.u * 0.75) * -1
FEATURE [Part::Feature] Part__Feature099  label="button_smd_6x6xH003"
  Placement = pos=(28.575,-124.713,1.6) rot=(0,0,1;0rad)
  shape: bbox 6 x 8 x 8 mm, 97 faces (baked)
  expr: .Placement.Base.x = Spreadsheet.u * 2 - Spreadsheet.u / 2
  expr: .Placement.Base.y = (Spreadsheet.PCB_width - Spreadsheet.u * 0.75) * -1
FEATURE [App::DocumentObjectGroup] Group001  label="Buttons"
  Group = -> [Part__Feature096,Part__Feature097,Part__Feature098,Part__Feature099]
FEATURE [App::Part] Pixelette_1  label="Pixelette 1"
  Group = -> [ks33,ks33001,ks33002,ks33003,ks33004,ks33005,ks33006,ks33007,ks33008,ks33009,ks33010,ks33011,ks33012,ks33013,ROT_EC11E,ks33014,SW_SPST_PTS645,ks33015,ks33016,ks33017,ks33018,ks33019,ks33020,SW_SPST_PTS645001,ks33021,SW_SPST_PTS645002,ks33022,ks33023,ks33024,ks33025,ks33026,ks33027,ks33028,ks33029,ks33030,ks33031,ks33032,ks33033,ks33034,ks33035,ks33036,ks33037,ks33038,ks33039,ks33040,ks33041,+55 more]
  Origin = -> Origin192
FEATURE [Sketcher::SketchObject] Sketch018
  AttachmentOffset = pos=(0,0,7) rot=(0,0,1;0rad)
  FullyConstrained = false
  MapMode = 5
  Placement = pos=(0,0,7) rot=(0,0,1;0rad)
  Support = -> [XY_Plane194]
  expr: Constraints[2] = Spreadsheet.PCB_length
  sketch-geometry (22):
    g0: GeomPoint X=352.425 Y=8.12855 Z=0
    g1: GeomPoint X=263.925 Y=0.5 Z=0
    g2: LineSegment StartX=251.425 StartY=2.5 StartZ=0 EndX=251.425 EndY=4.5 EndZ=0
    g3: LineSegment StartX=263.925 StartY=2.5 StartZ=0 EndX=263.925 EndY=4.5 EndZ=0
    g4: LineSegment StartX=265.925 StartY=6.5 StartZ=0 EndX=275.238 EndY=6.5 EndZ=0
    g5: LineSegment StartX=275.238 StartY=6.5 StartZ=0 EndX=275.238 EndY=16.2807 EndZ=0
    g6: LineSegment StartX=275.238 StartY=16.2807 StartZ=0 EndX=237.56 EndY=16.2807 EndZ=0
    g7: LineSegment StartX=237.56 StartY=16.2807 StartZ=0 EndX=237.56 EndY=6.5 EndZ=0
    g8: LineSegment StartX=237.56 StartY=6.5 StartZ=0 EndX=249.425 EndY=6.5 EndZ=0
    g9: LineSegment StartX=249.425 StartY=0.5 StartZ=0 EndX=237.56 EndY=0.5 EndZ=0
    g10: LineSegment StartX=265.925 StartY=0.5 StartZ=0 EndX=275.238 EndY=0.5 EndZ=0
    g11: LineSegment StartX=275.238 StartY=0.5 StartZ=0 EndX=275.238 EndY=-5.65737 EndZ=0
    g12: LineSegment StartX=275.238 StartY=-5.65737 StartZ=0 EndX=237.56 EndY=-5.65737 EndZ=0
    g13: LineSegment StartX=237.56 StartY=0.5 StartZ=0 EndX=237.56 EndY=-5.65737 EndZ=0
    g14: ArcOfCircle CenterX=265.925 CenterY=4.5 CenterZ=0 NormalX=0 NormalY=0 NormalZ=1 AngleXU=0 Radius=2 StartAngle=1.5708 EndAngle=3.14159
    g15: GeomPoint X=263.925 Y=6.5 Z=0
    g16: ArcOfCircle CenterX=249.425 CenterY=4.5 CenterZ=0 NormalX=0 NormalY=0 NormalZ=1 AngleXU=0 Radius=2 StartAngle=0 EndAngle=1.5708
    g17: GeomPoint X=251.425 Y=6.5 Z=0
    g18: ArcOfCircle CenterX=265.925 CenterY=2.5 CenterZ=0 NormalX=0 NormalY=0 NormalZ=1 AngleXU=0 Radius=2 StartAngle=3.14159 EndAngle=4.71239
    g19: GeomPoint X=263.925 Y=0.5 Z=0
    g20: ArcOfCircle CenterX=249.425 CenterY=2.5 CenterZ=0 NormalX=0 NormalY=0 NormalZ=1 AngleXU=0 Radius=2 StartAngle=4.71239 EndAngle=6.28319
    g21: GeomPoint X=251.425 Y=0.5 Z=0
  constraints (50):
    c: DistanceX(g1,g0) = 88.5
    c: DistanceX(g21,g0) = 101
    c: DistanceX(g-1,g0) = 352.425
    c: DistanceY(g-1,g21) = 0.5
    c: Vertical(g2)
    c: Vertical(g3)
    c: Horizontal(g4)
    c: Coincident(g5,g4)
    c: Vertical(g5)
    c: Coincident(g6,g5)
    c: Horizontal(g6)
    c: Coincident(g7,g6)
    c: Vertical(g7)
    c: Coincident(g8,g7)
    c: Horizontal(g8)
    c: Horizontal(g21,g19)
    c: Horizontal(g17,g15)
    c: DistanceY(g21,g17) = 6
    c: Horizontal(g9)
    c: Horizontal(g10)
    c: Coincident(g11,g10)
    c: Vertical(g11)
    c: Coincident(g12,g11)
    c: Horizontal(g12)
    c: Coincident(g13,g9)
    c: Coincident(g13,g12)
    c: Vertical(g13)
    c: Vertical(g7,g9)
    c: Vertical(g4,g10)
    c: PointOnObject(g15,g3)
    c: PointOnObject(g15,g4)
    c: Tangent(g3,g14) = 1.5708
    c: Tangent(g4,g14) = 1.5708
    c: PointOnObject(g17,g2)
    c: PointOnObject(g17,g8)
    c: Tangent(g2,g16) = -1.5708
    c: Tangent(g8,g16) = 1.5708
    c: PointOnObject(g19,g3)
    c: PointOnObject(g19,g10)
    c: Tangent(g3,g18) = 1.5708
    c: Tangent(g10,g18) = -1.5708
    c: PointOnObject(g21,g2)
    c: PointOnObject(g21,g9)
    c: Tangent(g2,g20) = -1.5708
    c: Tangent(g9,g20) = 1.5708
    c: Radius(g16) = 2
    c: Radius(g20) = 2
    c: Radius(g18) = 2
    c: Coincident(g19,g1)
    c: Radius(g14) = 2
FEATURE [PartDesign::Pocket] Pocket014
  BaseFeature = -> Pad001
  Direction = (0,0,-1)
  Length = 5
  Length2 = 5
  Profile = -> Sketch018
  ReferenceAxis = -> Sketch018 [N_Axis]
  Type = 0
FEATURE [PartDesign::Body] Body001
  Group = -> [Sketch015,Pad001,Sketch018,Pocket014]
  Origin = -> Origin194
  Placement = pos=(0,0,1.2) rot=(0,0,1;0rad)
  Tip = -> Pocket014
FEATURE [Sketcher::SketchObject] Sketch019
  AttachmentOffset = pos=(0,0,2.9) rot=(0,0,1;0rad)
  FullyConstrained = false
  MapMode = 5
  Placement = pos=(0,0,2.9) rot=(0,0,1;0rad)
  Support = -> [XY_Plane197]
  expr: .AttachmentOffset.Base.z = 1.6 + 1.3
  expr: Constraints[25] = Spreadsheet.Bottom_c_rad
  expr: Constraints[26] = Spreadsheet.Bottom_c_rad
  expr: Constraints[29] = Spreadsheet.Spacer_hole
  expr: Constraints[36] = Spreadsheet.PCB_length + Spreadsheet.pcb_to_wall_gap * 2
  expr: Constraints[37] = Spreadsheet.PCB_width + Spreadsheet.pcb_to_wall_gap * 2
  expr: Constraints[54] = Spreadsheet.Bottom_c_rad
  expr: Constraints[57] = Spreadsheet.Bottom_c_rad
  expr: Constraints[5] = Spreadsheet.PCB_length / 2
  expr: Constraints[60] = 2 * Spreadsheet.Top_c_rad * sin(45 / 2)
  expr: Constraints[61] = 2 * Spreadsheet.Top_c_rad * sin(45 / 2)
  expr: Constraints[66] = 2 * Spreadsheet.Top_c_rad * sin(45 / 2)
  expr: Constraints[67] = 2 * Spreadsheet.Top_c_rad * sin(45 / 2)
  expr: Constraints[6] = Spreadsheet.PCB_width / 2
  expr: Constraints[72] = Spreadsheet.wall_thickness / 2
  expr: Constraints[73] = Spreadsheet.PCB_length / 2
  expr: Constraints[74] = (Spreadsheet.PCB_length + Spreadsheet.pcb_to_wall_gap * 2 + Spreadsheet.wall_thickness * 2) / 4
  expr: Constraints[75] = (Spreadsheet.PCB_length + Spreadsheet.pcb_to_wall_gap * 2 + Spreadsheet.wall_thickness * 2) / 4
  expr: Constraints[7] = Spreadsheet.PCB_width + 2 * Spreadsheet.pcb_to_wall_gap + 2 * Spreadsheet.wall_thickness
  expr: Constraints[83] = Spreadsheet.wall_thickness / 2
  expr: Constraints[88] = 2 * Spreadsheet.Bottom_c_rad * sin(45 / 2)
  expr: Constraints[89] = 2 * Spreadsheet.Bottom_c_rad * sin(45 / 2)
  expr: Constraints[8] = Spreadsheet.PCB_length + 2 * Spreadsheet.pcb_to_wall_gap + 2 * Spreadsheet.wall_thickness
  expr: Constraints[92] = 2 * Spreadsheet.Bottom_c_rad * sin(45 / 2)
  expr: Constraints[93] = 2 * Spreadsheet.Bottom_c_rad * sin(45 / 2)
  sketch-geometry (45):
    g0: LineSegment StartX=-6.5 StartY=0.5 StartZ=0 EndX=-6.5 EndY=-142.5 EndZ=0
    g1: LineSegment StartX=-3.5 StartY=-145.5 StartZ=0 EndX=355.925 EndY=-145.5 EndZ=0
    g2: LineSegment StartX=358.925 StartY=-142.5 StartZ=0 EndX=358.925 EndY=0.5 EndZ=0
    g3: LineSegment StartX=352.925 StartY=6.5 StartZ=0 EndX=-0.5 EndY=6.5 EndZ=0
    g4: GeomPoint X=176.213 Y=-69.5 Z=0
    g5: ArcOfCircle CenterX=-0.5 CenterY=0.5 CenterZ=0 NormalX=0 NormalY=0 NormalZ=1 AngleXU=0 Radius=6 StartAngle=1.5708 EndAngle=3.14159
    g6: GeomPoint X=-6.5 Y=6.5 Z=0
    g7: ArcOfCircle CenterX=352.925 CenterY=0.5 CenterZ=0 NormalX=0 NormalY=0 NormalZ=1 AngleXU=0 Radius=6 StartAngle=0 EndAngle=1.5708
    g8: GeomPoint X=358.925 Y=6.5 Z=0
    g9: ArcOfCircle CenterX=-3.5 CenterY=-142.5 CenterZ=0 NormalX=0 NormalY=0 NormalZ=1 AngleXU=0 Radius=3 StartAngle=3.14159 EndAngle=4.71239
    g10: GeomPoint X=-6.5 Y=-145.5 Z=0
    g11: ArcOfCircle CenterX=355.925 CenterY=-142.5 CenterZ=0 NormalX=0 NormalY=0 NormalZ=1 AngleXU=0 Radius=3 StartAngle=4.71239 EndAngle=6.28319
    g12: GeomPoint X=358.925 Y=-145.5 Z=0
    g13: Circle CenterX=-1.74264 CenterY=1.74264 CenterZ=0 NormalX=0 NormalY=0 NormalZ=1 AngleXU=0 Radius=1.55
    g14: LineSegment StartX=-0.5 StartY=-5.5 StartZ=0 EndX=-0.5 EndY=-136.5 EndZ=0
    g15: LineSegment StartX=2.5 StartY=-139.5 StartZ=0 EndX=349.925 EndY=-139.5 EndZ=0
    g16: LineSegment StartX=352.925 StartY=-136.5 StartZ=0 EndX=352.925 EndY=-5.5 EndZ=0
    g17: LineSegment StartX=346.925 StartY=0.5 StartZ=0 EndX=5.5 EndY=0.5 EndZ=0
    g18: GeomPoint X=176.213 Y=-69.5 Z=0
    g19: ArcOfCircle CenterX=5.5 CenterY=-5.5 CenterZ=0 NormalX=0 NormalY=0 NormalZ=1 AngleXU=0 Radius=6 StartAngle=1.5708 EndAngle=3.14159
    g20: GeomPoint X=-0.5 Y=0.5 Z=0
    g21: ArcOfCircle CenterX=346.925 CenterY=-5.5 CenterZ=0 NormalX=0 NormalY=0 NormalZ=1 AngleXU=0 Radius=6 StartAngle=0 EndAngle=1.5708
    g22: GeomPoint X=352.925 Y=0.5 Z=0
    g23: ArcOfCircle CenterX=349.925 CenterY=-136.5 CenterZ=0 NormalX=0 NormalY=0 NormalZ=1 AngleXU=0 Radius=3 StartAngle=4.71239 EndAngle=6.28319
    g24: GeomPoint X=352.925 Y=-139.5 Z=0
    g25: ArcOfCircle CenterX=2.5 CenterY=-136.5 CenterZ=0 NormalX=0 NormalY=0 NormalZ=1 AngleXU=0 Radius=3 StartAngle=3.14159 EndAngle=4.71239
    g26: GeomPoint X=-0.5 Y=-139.5 Z=0
    g27: GeomPoint X=-4.74264 Y=4.74264 Z=0
    g28: GeomPoint X=1.25736 Y=-1.25736 Z=0
    g29: Circle CenterX=354.168 CenterY=1.74264 CenterZ=0 NormalX=0 NormalY=0 NormalZ=1 AngleXU=0 Radius=1.55
    g30: GeomPoint X=351.168 Y=-1.25736 Z=0
    g31: GeomPoint X=357.168 Y=4.74264 Z=0
    g32: Circle CenterX=84.8563 CenterY=3.5 CenterZ=0 NormalX=0 NormalY=0 NormalZ=1 AngleXU=0 Radius=1.55
    g33: Circle CenterX=176.213 CenterY=3.5 CenterZ=0 NormalX=0 NormalY=0 NormalZ=1 AngleXU=0 Radius=1.55
    g34: Circle CenterX=267.569 CenterY=3.5 CenterZ=0 NormalX=0 NormalY=0 NormalZ=1 AngleXU=0 Radius=1.55
    g35: Circle CenterX=84.8563 CenterY=-142.5 CenterZ=0 NormalX=0 NormalY=0 NormalZ=1 AngleXU=0 Radius=1.55
    g36: Circle CenterX=176.213 CenterY=-142.5 CenterZ=0 NormalX=0 NormalY=0 NormalZ=1 AngleXU=0 Radius=1.55
    g37: Circle CenterX=267.569 CenterY=-142.5 CenterZ=0 NormalX=0 NormalY=0 NormalZ=1 AngleXU=0 Radius=1.55
    g38: Circle CenterX=-2.62132 CenterY=-141.621 CenterZ=0 NormalX=0 NormalY=0 NormalZ=1 AngleXU=0 Radius=1.55
    g39: GeomPoint X=0.37868 Y=-138.621 Z=0
    g40: GeomPoint X=-5.62132 Y=-144.621 Z=0
    g41: GeomPoint X=6.2644 Y=-139.5 Z=0
    g42: GeomPoint X=352.046 Y=-138.621 Z=0
    g43: GeomPoint X=358.046 Y=-144.621 Z=0
    g44: Circle CenterX=355.046 CenterY=-141.621 CenterZ=0 NormalX=0 NormalY=0 NormalZ=1 AngleXU=0 Radius=1.55
  constraints (100):
    c: Horizontal(g1)
    c: Horizontal(g3)
    c: Vertical(g0)
    c: Vertical(g2)
    c: Symmetric(g12,g6,g4)
    c: DistanceX(g-1,g4) = 176.213
    c: DistanceY(g4,g-1) = 69.5
    c: DistanceY(g10,g6) = 152
    c: DistanceX(g6,g8) = 365.425
    c: PointOnObject(g6,g0)
    c: PointOnObject(g6,g3)
    c: Tangent(g0,g5) = -1.5708
    c: Tangent(g3,g5) = -1.5708
    c: PointOnObject(g8,g2)
    c: PointOnObject(g8,g3)
    c: Tangent(g2,g7) = -1.5708
    c: Tangent(g3,g7) = -1.5708
    c: PointOnObject(g10,g0)
    c: PointOnObject(g10,g1)
    c: Tangent(g0,g9) = -1.5708
    c: Tangent(g1,g9) = -1.5708
    c: PointOnObject(g12,g1)
    c: PointOnObject(g12,g2)
    c: Tangent(g1,g11) = -1.5708
    c: Tangent(g2,g11) = -1.5708
    c: Radius(g11) = 3
    c: Radius(g9) = 3
    c: Radius(g5) = 6
    c: Radius(g7) = 6
    c: Diameter(g13) = 3.1
    c: Horizontal(g15)
    c: Horizontal(g17)
    c: Vertical(g14)
    c: Vertical(g16)
    c: Symmetric(g24,g20,g18)
    c: Coincident(g18,g4)
    c: DistanceX(g20,g22) = 353.425
    c: DistanceY(g26,g20) = 140
    c: PointOnObject(g20,g14)
    c: PointOnObject(g20,g17)
    c: Tangent(g14,g19) = -1.5708
    c: Tangent(g17,g19) = -1.5708
    c: PointOnObject(g22,g16)
    c: PointOnObject(g22,g17)
    c: Tangent(g16,g21) = -1.5708
    c: Tangent(g17,g21) = -1.5708
    c: PointOnObject(g24,g15)
    c: PointOnObject(g24,g16)
    c: Tangent(g15,g23) = -1.5708
    c: Tangent(g16,g23) = -1.5708
    c: PointOnObject(g26,g14)
    c: PointOnObject(g26,g15)
    c: Tangent(g14,g25) = -1.5708
    c: Tangent(g15,g25) = -1.5708
    c: Radius(g25) = 3
    c: Radius(g19) = 6
    c: Radius(g21) = 6
    c: Radius(g23) = 3
    c: PointOnObject(g27,g5)
    c: PointOnObject(g28,g19)
    c: Distance(g14,g28) = 4.5922
    c: Distance(g0,g27) = 4.5922
    c: Symmetric(g27,g28,g13)
    c: Diameter(g29) = 3.1
    c: PointOnObject(g30,g21)
    c: PointOnObject(g31,g7)
    c: Distance(g30,g16) = 4.5922
    c: Distance(g2,g31) = 4.5922
    c: Symmetric(g30,g31,g29)
    c: Equal(g32,g33)
    c: Equal(g34,g33)
    c: Diameter(g33) = 3.1
    c: Distance(g33,g3) = 3
    c: DistanceX(g-1,g33) = 176.213
    c: DistanceX(g32,g33) = 91.3563
    c: DistanceX(g33,g34) = 91.3563
    c: Equal(g35,g36)
    c: Equal(g37,g36)
    c: Equal(g33,g36) = 3.1
    c: DistanceX(g35,g36) = 91.3563
    c: DistanceX(g36,g37) = 91.3563
    c: Horizontal(g35,g36)
    c: Horizontal(g37,g36)
    c: Distance(g36,g1) = 3
    c: Vertical(g36,g33)
    c: PointOnObject(g39,g25)
    c: PointOnObject(g40,g9)
    c: PointOnObject(g41,g15)
    c: Distance(g39,g14) = 2.2961
    c: Distance(g0,g40) = 2.2961
    c: PointOnObject(g42,g23)
    c: PointOnObject(g43,g11)
    c: Distance(g15,g42) = 2.2961
    c: Distance(g1,g43) = 2.2961
    c: Symmetric(g42,g43,g44)
    c: Diameter(g44) = 3.1
    c: Diameter(g38) = 3.1
    c: Symmetric(g40,g39,g38)
    c: Horizontal(g32,g33)
    c: Horizontal(g34,g33)
FEATURE [PartDesign::Pad] Pad004
  Direction = (0,0,1)
  Length = 3
  Length2 = 10
  Profile = -> Sketch019
  ReferenceAxis = -> Sketch019 [N_Axis]
  Type = 0
FEATURE [Sketcher::SketchObject] Sketch020
  AttachmentOffset = pos=(0,0,7) rot=(0,0,1;0rad)
  FullyConstrained = false
  MapMode = 5
  Placement = pos=(0,0,7) rot=(0,0,1;0rad)
  Support = -> [XY_Plane197]
  expr: Constraints[2] = Spreadsheet.PCB_length
  sketch-geometry (22):
    g0: GeomPoint X=352.425 Y=8.12855 Z=0
    g1: GeomPoint X=263.925 Y=0.5 Z=0
    g2: LineSegment StartX=251.425 StartY=2.5 StartZ=0 EndX=251.425 EndY=4.5 EndZ=0
    g3: LineSegment StartX=263.925 StartY=2.5 StartZ=0 EndX=263.925 EndY=4.5 EndZ=0
    g4: LineSegment StartX=265.925 StartY=6.5 StartZ=0 EndX=275.238 EndY=6.5 EndZ=0
    g5: LineSegment StartX=275.238 StartY=6.5 StartZ=0 EndX=275.238 EndY=16.2807 EndZ=0
    g6: LineSegment StartX=275.238 StartY=16.2807 StartZ=0 EndX=237.56 EndY=16.2807 EndZ=0
    g7: LineSegment StartX=237.56 StartY=16.2807 StartZ=0 EndX=237.56 EndY=6.5 EndZ=0
    g8: LineSegment StartX=237.56 StartY=6.5 StartZ=0 EndX=249.425 EndY=6.5 EndZ=0
    g9: LineSegment StartX=249.425 StartY=0.5 StartZ=0 EndX=237.56 EndY=0.5 EndZ=0
    g10: LineSegment StartX=265.925 StartY=0.5 StartZ=0 EndX=275.238 EndY=0.5 EndZ=0
    g11: LineSegment StartX=275.238 StartY=0.5 StartZ=0 EndX=275.238 EndY=-5.65737 EndZ=0
    g12: LineSegment StartX=275.238 StartY=-5.65737 StartZ=0 EndX=237.56 EndY=-5.65737 EndZ=0
    g13: LineSegment StartX=237.56 StartY=0.5 StartZ=0 EndX=237.56 EndY=-5.65737 EndZ=0
    g14: ArcOfCircle CenterX=265.925 CenterY=4.5 CenterZ=0 NormalX=0 NormalY=0 NormalZ=1 AngleXU=0 Radius=2 StartAngle=1.5708 EndAngle=3.14159
    g15: GeomPoint X=263.925 Y=6.5 Z=0
    g16: ArcOfCircle CenterX=249.425 CenterY=4.5 CenterZ=0 NormalX=0 NormalY=0 NormalZ=1 AngleXU=0 Radius=2 StartAngle=0 EndAngle=1.5708
    g17: GeomPoint X=251.425 Y=6.5 Z=0
    g18: ArcOfCircle CenterX=265.925 CenterY=2.5 CenterZ=0 NormalX=0 NormalY=0 NormalZ=1 AngleXU=0 Radius=2 StartAngle=3.14159 EndAngle=4.71239
    g19: GeomPoint X=263.925 Y=0.5 Z=0
    g20: ArcOfCircle CenterX=249.425 CenterY=2.5 CenterZ=0 NormalX=0 NormalY=0 NormalZ=1 AngleXU=0 Radius=2 StartAngle=4.71239 EndAngle=6.28319
    g21: GeomPoint X=251.425 Y=0.5 Z=0
  constraints (50):
    c: DistanceX(g1,g0) = 88.5
    c: DistanceX(g21,g0) = 101
    c: DistanceX(g-1,g0) = 352.425
    c: DistanceY(g-1,g21) = 0.5
    c: Vertical(g2)
    c: Vertical(g3)
    c: Horizontal(g4)
    c: Coincident(g5,g4)
    c: Vertical(g5)
    c: Coincident(g6,g5)
    c: Horizontal(g6)
    c: Coincident(g7,g6)
    c: Vertical(g7)
    c: Coincident(g8,g7)
    c: Horizontal(g8)
    c: Horizontal(g21,g19)
    c: Horizontal(g17,g15)
    c: DistanceY(g21,g17) = 6
    c: Horizontal(g9)
    c: Horizontal(g10)
    c: Coincident(g11,g10)
    c: Vertical(g11)
    c: Coincident(g12,g11)
    c: Horizontal(g12)
    c: Coincident(g13,g9)
    c: Coincident(g13,g12)
    c: Vertical(g13)
    c: Vertical(g7,g9)
    c: Vertical(g4,g10)
    c: PointOnObject(g15,g3)
    c: PointOnObject(g15,g4)
    c: Tangent(g3,g14) = 1.5708
    c: Tangent(g4,g14) = 1.5708
    c: PointOnObject(g17,g2)
    c: PointOnObject(g17,g8)
    c: Tangent(g2,g16) = -1.5708
    c: Tangent(g8,g16) = 1.5708
    c: PointOnObject(g19,g3)
    c: PointOnObject(g19,g10)
    c: Tangent(g3,g18) = 1.5708
    c: Tangent(g10,g18) = -1.5708
    c: PointOnObject(g21,g2)
    c: PointOnObject(g21,g9)
    c: Tangent(g2,g20) = -1.5708
    c: Tangent(g9,g20) = 1.5708
    c: Radius(g16) = 2
    c: Radius(g20) = 2
    c: Radius(g18) = 2
    c: Coincident(g19,g1)
    c: Radius(g14) = 2
FEATURE [PartDesign::Pocket] Pocket015
  BaseFeature = -> Pad004
  Direction = (0,0,-1)
  Length = 5
  Length2 = 5
  Profile = -> Sketch020
  ReferenceAxis = -> Sketch020 [N_Axis]
  Type = 0
FEATURE [PartDesign::Body] Body004  label="Body002"
  Group = -> [Sketch019,Pad004,Sketch020,Pocket015]
  Origin = -> Origin197
  Placement = pos=(0,0,-3) rot=(0,0,1;0rad)
  Tip = -> Pocket015
FEATURE [Sketcher::SketchObject] Sketch021
  AttachmentOffset = pos=(0,0,2.9) rot=(0,0,1;0rad)
  FullyConstrained = false
  MapMode = 5
  Placement = pos=(0,0,2.9) rot=(0,0,1;0rad)
  Support = -> [XY_Plane199]
  expr: .AttachmentOffset.Base.z = 1.6 + 1.3
  expr: Constraints[25] = Spreadsheet.Bottom_c_rad
  expr: Constraints[26] = Spreadsheet.Bottom_c_rad
  expr: Constraints[29] = Spreadsheet.Screw_hole
  expr: Constraints[32] = Spreadsheet.PCB_length + Spreadsheet.pcb_to_wall_gap * 2
  expr: Constraints[33] = Spreadsheet.PCB_width + Spreadsheet.pcb_to_wall_gap * 2
  expr: Constraints[35] = 2 * Spreadsheet.Top_c_rad * sin(45 / 2)
  expr: Constraints[37] = Spreadsheet.Screw_hole
  expr: Constraints[39] = 2 * Spreadsheet.Top_c_rad * sin(45 / 2)
  expr: Constraints[43] = Spreadsheet.Screw_hole
  expr: Constraints[44] = Spreadsheet.wall_thickness / 2
  expr: Constraints[45] = Spreadsheet.PCB_length / 2
  expr: Constraints[46] = (Spreadsheet.PCB_length + Spreadsheet.pcb_to_wall_gap * 2 + Spreadsheet.wall_thickness * 2) / 4
  expr: Constraints[47] = (Spreadsheet.PCB_length + Spreadsheet.pcb_to_wall_gap * 2 + Spreadsheet.wall_thickness * 2) / 4
  expr: Constraints[55] = Spreadsheet.wall_thickness / 2
  expr: Constraints[58] = 2 * Spreadsheet.Bottom_c_rad * sin(45 / 2)
  expr: Constraints[5] = Spreadsheet.PCB_length / 2
  expr: Constraints[60] = 2 * Spreadsheet.Bottom_c_rad * sin(45 / 2)
  expr: Constraints[62] = Spreadsheet.Screw_hole
  expr: Constraints[63] = Spreadsheet.Screw_hole
  expr: Constraints[6] = Spreadsheet.PCB_width / 2
  expr: Constraints[7] = Spreadsheet.PCB_width + 2 * Spreadsheet.pcb_to_wall_gap + 2 * Spreadsheet.wall_thickness
  expr: Constraints[8] = Spreadsheet.PCB_length + 2 * Spreadsheet.pcb_to_wall_gap + 2 * Spreadsheet.wall_thickness
  sketch-geometry (36):
    g0: LineSegment StartX=-6.5 StartY=0.5 StartZ=0 EndX=-6.5 EndY=-142.5 EndZ=0
    g1: LineSegment StartX=-3.5 StartY=-145.5 StartZ=0 EndX=355.925 EndY=-145.5 EndZ=0
    g2: LineSegment StartX=358.925 StartY=-142.5 StartZ=0 EndX=358.925 EndY=0.5 EndZ=0
    g3: LineSegment StartX=352.925 StartY=6.5 StartZ=0 EndX=-0.5 EndY=6.5 EndZ=0
    g4: GeomPoint X=176.213 Y=-69.5 Z=0
    g5: ArcOfCircle CenterX=-0.5 CenterY=0.5 CenterZ=0 NormalX=0 NormalY=0 NormalZ=1 AngleXU=0 Radius=6 StartAngle=1.5708 EndAngle=3.14159
    g6: GeomPoint X=-6.5 Y=6.5 Z=0
    g7: ArcOfCircle CenterX=352.925 CenterY=0.5 CenterZ=0 NormalX=0 NormalY=0 NormalZ=1 AngleXU=0 Radius=6 StartAngle=1e-16 EndAngle=1.5708
    g8: GeomPoint X=358.925 Y=6.5 Z=0
    g9: ArcOfCircle CenterX=-3.5 CenterY=-142.5 CenterZ=0 NormalX=0 NormalY=0 NormalZ=1 AngleXU=0 Radius=3 StartAngle=3.14159 EndAngle=4.71239
    g10: GeomPoint X=-6.5 Y=-145.5 Z=0
    g11: ArcOfCircle CenterX=355.925 CenterY=-142.5 CenterZ=0 NormalX=0 NormalY=0 NormalZ=1 AngleXU=0 Radius=3 StartAngle=4.71239 EndAngle=6.28319
    g12: GeomPoint X=358.925 Y=-145.5 Z=0
    g13: Circle CenterX=-1.74264 CenterY=1.74264 CenterZ=0 NormalX=0 NormalY=0 NormalZ=1 AngleXU=0 Radius=1.05
    g14: GeomPoint X=176.213 Y=-69.5 Z=0
    g15: GeomPoint X=-0.908997 Y=0.376244 Z=0
    g16: GeomPoint X=352.516 Y=0.5 Z=0
    g17: GeomPoint X=353.334 Y=-139.376 Z=0
    g18: GeomPoint X=-0.5 Y=-139.624 Z=0
    g19: GeomPoint X=-4.74264 Y=4.74264 Z=0
    g20: GeomPoint X=1.25736 Y=-1.25736 Z=0
    g21: Circle CenterX=354.168 CenterY=1.74264 CenterZ=0 NormalX=0 NormalY=0 NormalZ=1 AngleXU=0 Radius=1.05
    g22: GeomPoint X=351.168 Y=-1.25736 Z=0
    g23: GeomPoint X=357.168 Y=4.74264 Z=0
    g24: Circle CenterX=84.8563 CenterY=3.5 CenterZ=0 NormalX=0 NormalY=0 NormalZ=1 AngleXU=0 Radius=1.05
    g25: Circle CenterX=176.213 CenterY=3.5 CenterZ=0 NormalX=0 NormalY=0 NormalZ=1 AngleXU=0 Radius=1.05
    g26: Circle CenterX=267.569 CenterY=3.5 CenterZ=0 NormalX=0 NormalY=0 NormalZ=1 AngleXU=0 Radius=1.05
    g27: Circle CenterX=84.8563 CenterY=-142.5 CenterZ=0 NormalX=0 NormalY=0 NormalZ=1 AngleXU=0 Radius=1.05
    g28: Circle CenterX=176.213 CenterY=-142.5 CenterZ=0 NormalX=0 NormalY=0 NormalZ=1 AngleXU=0 Radius=1.05
    g29: Circle CenterX=267.569 CenterY=-142.5 CenterZ=0 NormalX=0 NormalY=0 NormalZ=1 AngleXU=0 Radius=1.05
    g30: Circle CenterX=-2.62132 CenterY=-141.621 CenterZ=0 NormalX=0 NormalY=0 NormalZ=1 AngleXU=0 Radius=1.05
    g31: GeomPoint X=0.37868 Y=-138.621 Z=0
    g32: GeomPoint X=-5.62132 Y=-144.621 Z=0
    g33: GeomPoint X=352.046 Y=-138.621 Z=0
    g34: GeomPoint X=358.046 Y=-144.621 Z=0
    g35: Circle CenterX=355.046 CenterY=-141.621 CenterZ=0 NormalX=0 NormalY=0 NormalZ=1 AngleXU=0 Radius=1.05
  constraints (71):
    c: Horizontal(g1)
    c: Horizontal(g3)
    c: Vertical(g0)
    c: Vertical(g2)
    c: Symmetric(g12,g6,g4)
    c: DistanceX(g-1,g4) = 176.213
    c: DistanceY(g4,g-1) = 69.5
    c: DistanceY(g10,g6) = 152
    c: DistanceX(g6,g8) = 365.425
    c: PointOnObject(g6,g0)
    c: PointOnObject(g6,g3)
    c: Tangent(g0,g5) = -1.5708
    c: Tangent(g3,g5) = -1.5708
    c: PointOnObject(g8,g2)
    c: PointOnObject(g8,g3)
    c: Tangent(g2,g7) = -1.5708
    c: Tangent(g3,g7) = -1.5708
    c: PointOnObject(g10,g0)
    c: PointOnObject(g10,g1)
    c: Tangent(g0,g9) = -1.5708
    c: Tangent(g1,g9) = -1.5708
    c: PointOnObject(g12,g1)
    c: PointOnObject(g12,g2)
    c: Tangent(g1,g11) = -1.5708
    c: Tangent(g2,g11) = -1.5708
    c: Radius(g11) = 3
    c: Radius(g9) = 3
    c: Radius(g5) = 6
    c: Radius(g7) = 6
    c: Diameter(g13) = 2.1
    c: Symmetric(g17,g15,g14)
    c: Coincident(g14,g4)
    c: DistanceX(g15,g16) = 353.425
    c: DistanceY(g18,g15) = 140
    c: PointOnObject(g19,g5)
    c: Distance(g0,g19) = 4.5922
    c: Symmetric(g19,g20,g13)
    c: Diameter(g21) = 2.1
    c: PointOnObject(g23,g7)
    c: Distance(g2,g23) = 4.5922
    c: Symmetric(g22,g23,g21)
    c: Equal(g24,g25)
    c: Equal(g26,g25)
    c: Diameter(g25) = 2.1
    c: Distance(g25,g3) = 3
    c: DistanceX(g-1,g25) = 176.213
    c: DistanceX(g24,g25) = 91.3563
    c: DistanceX(g25,g26) = 91.3563
    c: Equal(g27,g28)
    c: Equal(g29,g28)
    c: Equal(g25,g28) = 3.1
    c: DistanceX(g27,g28) = 91.3563
    c: DistanceX(g28,g29) = 91.3563
    c: Horizontal(g27,g28)
    c: Horizontal(g29,g28)
    c: Distance(g28,g1) = 3
    c: Vertical(g28,g25)
    c: PointOnObject(g32,g9)
    c: Distance(g0,g32) = 2.2961
    c: PointOnObject(g34,g11)
    c: Distance(g1,g34) = 2.2961
    c: Symmetric(g33,g34,g35)
    c: Diameter(g35) = 2.1
    c: Diameter(g30) = 2.1
    c: Symmetric(g32,g31,g30)
    c: Horizontal(g24,g25)
    c: Horizontal(g26,g25)
    c: Block(g13)
    c: Block(g30)
    c: Block(g35)
    c: Block(g21)
FEATURE [PartDesign::Pad] Pad005
  Direction = (0,0,1)
  Length = 2
  Length2 = 10
  Profile = -> Sketch021
  ReferenceAxis = -> Sketch021 [N_Axis]
  Type = 0
FEATURE [Sketcher::SketchObject] Sketch022
  AttachmentOffset = pos=(0,0,5) rot=(0,0,1;0rad)
  FullyConstrained = true
  MapMode = 5
  Placement = pos=(0,0,5) rot=(0,0,1;0rad)
  Support = -> [XY_Plane199]
  expr: Constraints[10] = Spreadsheet.PCB_width - Spreadsheet.u * 6
  expr: Constraints[11] = Spreadsheet.u * 2.5
  expr: Constraints[12] = Spreadsheet.u + 1
  expr: Constraints[13] = Spreadsheet.u * 4 + 1
  expr: Constraints[15] = Spreadsheet.u * (0.5 + 0.25 + 2)
  expr: Constraints[169] = Spreadsheet.key_fillet
  expr: Constraints[170] = Spreadsheet.u + 1
  expr: Constraints[171] = Spreadsheet.u + 1
  expr: Constraints[172] = Spreadsheet.u + 1
  expr: Constraints[173] = Spreadsheet.u + 1
  expr: Constraints[174] = Spreadsheet.u + 1
  expr: Constraints[175] = Spreadsheet.u + 1
  expr: Constraints[176] = Spreadsheet.u + 1
  expr: Constraints[177] = Spreadsheet.u + 1
  expr: Constraints[178] = Spreadsheet.u * 4 + 1
  expr: Constraints[179] = Spreadsheet.u * 4 + 1
  expr: Constraints[22] = Spreadsheet.u * (2 + 0.25 + 2)
  expr: Constraints[41] = Spreadsheet.u * (2 + 0.25 + 2)
  expr: Constraints[42] = Spreadsheet.u * (0.5 + 2 + 0.25)
  expr: Constraints[43] = Spreadsheet.u * 1.5
  expr: Constraints[48] = Spreadsheet.u
  expr: Constraints[49] = Spreadsheet.u
  sketch-geometry (80):
    g0: Circle CenterX=9.525 CenterY=-24.7 CenterZ=0 NormalX=0 NormalY=0 NormalZ=1 AngleXU=0 Radius=3.75
    g1: Circle CenterX=28.575 CenterY=-24.7 CenterZ=0 NormalX=0 NormalY=0 NormalZ=1 AngleXU=0 Radius=3.75
    g2: LineSegment StartX=37.6 StartY=-16.175 StartZ=0 EndX=37.6 EndY=-33.225 EndZ=0
    g3: LineSegment StartX=39.1 StartY=-34.725 StartZ=0 EndX=56.15 EndY=-34.725 EndZ=0
    g4: LineSegment StartX=57.65 StartY=-33.225 StartZ=0 EndX=57.65 EndY=-16.175 EndZ=0
    g5: LineSegment StartX=56.15 StartY=-14.675 StartZ=0 EndX=39.1 EndY=-14.675 EndZ=0
    g6: GeomPoint X=47.625 Y=-24.7 Z=0
    g7: LineSegment StartX=61.4125 StartY=-16.175 StartZ=0 EndX=61.4125 EndY=-33.225 EndZ=0
    g8: LineSegment StartX=62.9125 StartY=-34.725 StartZ=0 EndX=137.112 EndY=-34.725 EndZ=0
    g9: LineSegment StartX=138.612 StartY=-33.225 StartZ=0 EndX=138.612 EndY=-16.175 EndZ=0
    g10: LineSegment StartX=137.112 StartY=-14.675 StartZ=0 EndX=62.9125 EndY=-14.675 EndZ=0
    g11: GeomPoint X=100.013 Y=-24.7 Z=0
    g12: LineSegment StartX=142.375 StartY=-16.175 StartZ=0 EndX=142.375 EndY=-33.225 EndZ=0
    g13: LineSegment StartX=143.875 StartY=-34.725 StartZ=0 EndX=218.075 EndY=-34.725 EndZ=0
    g14: LineSegment StartX=219.575 StartY=-33.225 StartZ=0 EndX=219.575 EndY=-16.175 EndZ=0
    g15: LineSegment StartX=218.075 StartY=-14.675 StartZ=0 EndX=143.875 EndY=-14.675 EndZ=0
    g16: GeomPoint X=180.975 Y=-24.7 Z=0
    g17: LineSegment StartX=223.338 StartY=-16.175 StartZ=0 EndX=223.338 EndY=-33.225 EndZ=0
    g18: LineSegment StartX=224.838 StartY=-34.725 StartZ=0 EndX=299.038 EndY=-34.725 EndZ=0
    g19: LineSegment StartX=300.538 StartY=-33.225 StartZ=0 EndX=300.538 EndY=-16.175 EndZ=0
    g20: LineSegment StartX=299.038 StartY=-14.675 StartZ=0 EndX=224.838 EndY=-14.675 EndZ=0
    g21: GeomPoint X=261.938 Y=-24.7 Z=0
    g22: LineSegment StartX=304.3 StartY=-16.175 StartZ=0 EndX=304.3 EndY=-33.225 EndZ=0
    g23: LineSegment StartX=305.8 StartY=-34.725 StartZ=0 EndX=322.85 EndY=-34.725 EndZ=0
    g24: LineSegment StartX=324.35 StartY=-33.225 StartZ=0 EndX=324.35 EndY=-16.175 EndZ=0
    g25: LineSegment StartX=322.85 StartY=-14.675 StartZ=0 EndX=305.8 EndY=-14.675 EndZ=0
    g26: GeomPoint X=314.325 Y=-24.7 Z=0
    g27: LineSegment StartX=332.875 StartY=-16.175 StartZ=0 EndX=332.875 EndY=-33.225 EndZ=0
    g28: LineSegment StartX=334.375 StartY=-34.725 StartZ=0 EndX=351.425 EndY=-34.725 EndZ=0
    g29: LineSegment StartX=352.925 StartY=-33.225 StartZ=0 EndX=352.925 EndY=-16.175 EndZ=0
    g30: LineSegment StartX=351.425 StartY=-14.675 StartZ=0 EndX=334.375 EndY=-14.675 EndZ=0
    g31: GeomPoint X=342.9 Y=-24.7 Z=0
    g32: ArcOfCircle CenterX=39.1 CenterY=-16.175 CenterZ=0 NormalX=0 NormalY=0 NormalZ=1 AngleXU=0 Radius=1.5 StartAngle=1.5708 EndAngle=3.14159
    g33: GeomPoint X=37.6 Y=-14.675 Z=0
    g34: ArcOfCircle CenterX=39.1 CenterY=-33.225 CenterZ=0 NormalX=0 NormalY=0 NormalZ=1 AngleXU=0 Radius=1.5 StartAngle=3.14159 EndAngle=4.71239
    g35: GeomPoint X=37.6 Y=-34.725 Z=0
    g36: ArcOfCircle CenterX=56.15 CenterY=-33.225 CenterZ=0 NormalX=0 NormalY=0 NormalZ=1 AngleXU=0 Radius=1.5 StartAngle=4.71239 EndAngle=6.28319
    g37: GeomPoint X=57.65 Y=-34.725 Z=0
    g38: ArcOfCircle CenterX=56.15 CenterY=-16.175 CenterZ=0 NormalX=0 NormalY=0 NormalZ=1 AngleXU=0 Radius=1.5 StartAngle=9e-16 EndAngle=1.5708
    g39: GeomPoint X=57.65 Y=-14.675 Z=0
    g40: ArcOfCircle CenterX=62.9125 CenterY=-16.175 CenterZ=0 NormalX=0 NormalY=0 NormalZ=1 AngleXU=0 Radius=1.5 StartAngle=1.5708 EndAngle=3.14159
    g41: GeomPoint X=61.4125 Y=-14.675 Z=0
    g42: ArcOfCircle CenterX=62.9125 CenterY=-33.225 CenterZ=0 NormalX=0 NormalY=0 NormalZ=1 AngleXU=0 Radius=1.5 StartAngle=3.14159 EndAngle=4.71239
    g43: GeomPoint X=61.4125 Y=-34.725 Z=0
    g44: ArcOfCircle CenterX=137.112 CenterY=-33.225 CenterZ=0 NormalX=0 NormalY=0 NormalZ=1 AngleXU=0 Radius=1.5 StartAngle=4.71239 EndAngle=6.28319
    g45: GeomPoint X=138.613 Y=-34.725 Z=0
    g46: ArcOfCircle CenterX=137.112 CenterY=-16.175 CenterZ=0 NormalX=0 NormalY=0 NormalZ=1 AngleXU=0 Radius=1.5 StartAngle=0 EndAngle=1.5708
    g47: GeomPoint X=138.613 Y=-14.675 Z=0
    g48: ArcOfCircle CenterX=143.875 CenterY=-16.175 CenterZ=0 NormalX=0 NormalY=0 NormalZ=1 AngleXU=0 Radius=1.5 StartAngle=1.5708 EndAngle=3.14159
    g49: GeomPoint X=142.375 Y=-14.675 Z=0
    g50: ArcOfCircle CenterX=143.875 CenterY=-33.225 CenterZ=0 NormalX=0 NormalY=0 NormalZ=1 AngleXU=0 Radius=1.5 StartAngle=3.14159 EndAngle=4.71239
    g51: GeomPoint X=142.375 Y=-34.725 Z=0
    g52: ArcOfCircle CenterX=218.075 CenterY=-33.225 CenterZ=0 NormalX=0 NormalY=0 NormalZ=1 AngleXU=0 Radius=1.5 StartAngle=4.71239 EndAngle=6.28319
    g53: GeomPoint X=219.575 Y=-34.725 Z=0
    g54: ArcOfCircle CenterX=218.075 CenterY=-16.175 CenterZ=0 NormalX=0 NormalY=0 NormalZ=1 AngleXU=0 Radius=1.5 StartAngle=3e-16 EndAngle=1.5708
    g55: GeomPoint X=219.575 Y=-14.675 Z=0
    g56: ArcOfCircle CenterX=224.838 CenterY=-16.175 CenterZ=0 NormalX=0 NormalY=0 NormalZ=1 AngleXU=0 Radius=1.5 StartAngle=1.5708 EndAngle=3.14159
    g57: GeomPoint X=223.338 Y=-14.675 Z=0
    g58: ArcOfCircle CenterX=224.838 CenterY=-33.225 CenterZ=0 NormalX=0 NormalY=0 NormalZ=1 AngleXU=0 Radius=1.5 StartAngle=3.14159 EndAngle=4.71239
    g59: GeomPoint X=223.338 Y=-34.725 Z=0
    g60: ArcOfCircle CenterX=299.038 CenterY=-33.225 CenterZ=0 NormalX=0 NormalY=0 NormalZ=1 AngleXU=0 Radius=1.5 StartAngle=4.71239 EndAngle=6.28319
    g61: GeomPoint X=300.538 Y=-34.725 Z=0
    g62: ArcOfCircle CenterX=299.038 CenterY=-16.175 CenterZ=0 NormalX=0 NormalY=0 NormalZ=1 AngleXU=0 Radius=1.5 StartAngle=5e-16 EndAngle=1.5708
    g63: GeomPoint X=300.538 Y=-14.675 Z=0
    g64: ArcOfCircle CenterX=305.8 CenterY=-16.175 CenterZ=0 NormalX=0 NormalY=0 NormalZ=1 AngleXU=0 Radius=1.5 StartAngle=1.5708 EndAngle=3.14159
    g65: GeomPoint X=304.3 Y=-14.675 Z=0
    g66: ArcOfCircle CenterX=305.8 CenterY=-33.225 CenterZ=0 NormalX=0 NormalY=0 NormalZ=1 AngleXU=0 Radius=1.5 StartAngle=3.14159 EndAngle=4.71239
    g67: GeomPoint X=304.3 Y=-34.725 Z=0
    g68: ArcOfCircle CenterX=322.85 CenterY=-33.225 CenterZ=0 NormalX=0 NormalY=0 NormalZ=1 AngleXU=0 Radius=1.5 StartAngle=4.71239 EndAngle=6.28319
    g69: GeomPoint X=324.35 Y=-34.725 Z=0
    g70: ArcOfCircle CenterX=322.85 CenterY=-16.175 CenterZ=0 NormalX=0 NormalY=0 NormalZ=1 AngleXU=0 Radius=1.5 StartAngle=0 EndAngle=1.5708
    g71: GeomPoint X=324.35 Y=-14.675 Z=0
    g72: ArcOfCircle CenterX=334.375 CenterY=-16.175 CenterZ=0 NormalX=0 NormalY=0 NormalZ=1 AngleXU=0 Radius=1.5 StartAngle=1.5708 EndAngle=3.14159
    g73: GeomPoint X=332.875 Y=-14.675 Z=0
    g74: ArcOfCircle CenterX=334.375 CenterY=-33.225 CenterZ=0 NormalX=0 NormalY=0 NormalZ=1 AngleXU=0 Radius=1.5 StartAngle=3.14159 EndAngle=4.71239
    g75: GeomPoint X=332.875 Y=-34.725 Z=0
    g76: ArcOfCircle CenterX=351.425 CenterY=-33.225 CenterZ=0 NormalX=0 NormalY=0 NormalZ=1 AngleXU=0 Radius=1.5 StartAngle=4.71239 EndAngle=6.28319
    g77: GeomPoint X=352.925 Y=-34.725 Z=0
    g78: ArcOfCircle CenterX=351.425 CenterY=-16.175 CenterZ=0 NormalX=0 NormalY=0 NormalZ=1 AngleXU=0 Radius=1.5 StartAngle=6e-16 EndAngle=1.5708
    g79: GeomPoint X=352.925 Y=-14.675 Z=0
  constraints (180):
    c: Horizontal(g3)
    c: Horizontal(g5)
    c: Vertical(g2)
    c: Vertical(g4)
    c: Symmetric(g37,g33,g6)
    c: Horizontal(g8)
    c: Horizontal(g10)
    c: Vertical(g7)
    c: Vertical(g9)
    c: Symmetric(g45,g41,g11)
    c: DistanceY(g6,g-1) = 24.7
    c: DistanceX(g-1,g6) = 47.625
    c: DistanceY(g35,g33) = 20.05
    c: DistanceX(g41,g47) = 77.2
    c: Horizontal(g6,g11)
    c: DistanceX(g6,g11) = 52.3875
    c: Horizontal(g13)
    c: Horizontal(g15)
    c: Vertical(g12)
    c: Vertical(g14)
    c: Symmetric(g53,g49,g16)
    c: Horizontal(g11,g16)
    c: DistanceX(g11,g16) = 80.9625
    c: Horizontal(g18)
    c: Horizontal(g20)
    c: Vertical(g17)
    c: Vertical(g19)
    c: Symmetric(g61,g57,g21)
    c: Horizontal(g23)
    c: Horizontal(g25)
    c: Vertical(g22)
    c: Vertical(g24)
    c: Symmetric(g69,g65,g26)
    c: Horizontal(g28)
    c: Horizontal(g30)
    c: Vertical(g27)
    c: Vertical(g29)
    c: Symmetric(g77,g73,g31)
    c: Horizontal(g16,g21)
    c: Horizontal(g21,g26)
    c: Horizontal(g26,g31)
    c: DistanceX(g16,g21) = 80.9625
    c: DistanceX(g21,g26) = 52.3875
    c: DistanceX(g26,g31) = 28.575
    c: Equal(g0,g1)
    c: Horizontal(g1,g6)
    c: Horizontal(g0,g6)
    c: Diameter(g1) = 7.5
    c: DistanceX(g1,g6) = 19.05
    c: DistanceX(g0,g1) = 19.05
    c: PointOnObject(g33,g2)
    c: PointOnObject(g33,g5)
    c: Tangent(g2,g32) = -1.5708
    c: Tangent(g5,g32) = -1.5708
    c: PointOnObject(g35,g2)
    c: PointOnObject(g35,g3)
    c: Tangent(g2,g34) = -1.5708
    c: Tangent(g3,g34) = -1.5708
    c: PointOnObject(g37,g3)
    c: PointOnObject(g37,g4)
    c: Tangent(g3,g36) = -1.5708
    c: Tangent(g4,g36) = -1.5708
    c: PointOnObject(g39,g4)
    c: PointOnObject(g39,g5)
    c: Tangent(g4,g38) = -1.5708
    c: Tangent(g5,g38) = -1.5708
    c: PointOnObject(g41,g7)
    c: PointOnObject(g41,g10)
    c: Tangent(g7,g40) = -1.5708
    c: Tangent(g10,g40) = -1.5708
    c: PointOnObject(g43,g7)
    c: PointOnObject(g43,g8)
    c: Tangent(g7,g42) = -1.5708
    c: Tangent(g8,g42) = -1.5708
    c: PointOnObject(g45,g8)
    c: PointOnObject(g45,g9)
    c: Tangent(g8,g44) = -1.5708
    c: Tangent(g9,g44) = -1.5708
    c: PointOnObject(g47,g9)
    c: PointOnObject(g47,g10)
    c: Tangent(g9,g46) = -1.5708
    c: Tangent(g10,g46) = -1.5708
    c: PointOnObject(g49,g12)
    c: PointOnObject(g49,g15)
    c: Tangent(g12,g48) = -1.5708
    c: Tangent(g15,g48) = -1.5708
    c: PointOnObject(g51,g12)
    c: PointOnObject(g51,g13)
    c: Tangent(g12,g50) = -1.5708
    c: Tangent(g13,g50) = -1.5708
    c: PointOnObject(g53,g13)
    c: PointOnObject(g53,g14)
    c: Tangent(g13,g52) = -1.5708
    c: Tangent(g14,g52) = -1.5708
    c: PointOnObject(g55,g14)
    c: PointOnObject(g55,g15)
    c: Tangent(g14,g54) = -1.5708
    c: Tangent(g15,g54) = -1.5708
    c: PointOnObject(g57,g17)
    c: PointOnObject(g57,g20)
    c: Tangent(g17,g56) = -1.5708
    c: Tangent(g20,g56) = -1.5708
    c: PointOnObject(g59,g17)
    c: PointOnObject(g59,g18)
    c: Tangent(g17,g58) = -1.5708
    c: Tangent(g18,g58) = -1.5708
    c: PointOnObject(g61,g18)
    c: PointOnObject(g61,g19)
    c: Tangent(g18,g60) = -1.5708
    c: Tangent(g19,g60) = -1.5708
    c: PointOnObject(g63,g19)
    c: PointOnObject(g63,g20)
    c: Tangent(g19,g62) = -1.5708
    c: Tangent(g20,g62) = -1.5708
    c: PointOnObject(g65,g22)
    c: PointOnObject(g65,g25)
    c: Tangent(g22,g64) = -1.5708
    c: Tangent(g25,g64) = -1.5708
    c: PointOnObject(g67,g22)
    c: PointOnObject(g67,g23)
    c: Tangent(g22,g66) = -1.5708
    c: Tangent(g23,g66) = -1.5708
    c: PointOnObject(g69,g23)
    c: PointOnObject(g69,g24)
    c: Tangent(g23,g68) = -1.5708
    c: Tangent(g24,g68) = -1.5708
    c: PointOnObject(g71,g24)
    c: PointOnObject(g71,g25)
    c: Tangent(g24,g70) = -1.5708
    c: Tangent(g25,g70) = -1.5708
    c: PointOnObject(g73,g27)
    c: PointOnObject(g73,g30)
    c: Tangent(g27,g72) = -1.5708
    c: Tangent(g30,g72) = -1.5708
    c: PointOnObject(g75,g27)
    c: PointOnObject(g75,g28)
    c: Tangent(g27,g74) = -1.5708
    c: Tangent(g28,g74) = -1.5708
    c: PointOnObject(g77,g28)
    c: PointOnObject(g77,g29)
    c: Tangent(g28,g76) = -1.5708
    c: Tangent(g29,g76) = -1.5708
    c: PointOnObject(g79,g29)
    c: PointOnObject(g79,g30)
    c: Tangent(g29,g78) = -1.5708
    c: Tangent(g30,g78) = -1.5708
    c: Equal(g78,g76)
    c: Equal(g76,g74)
    c: Equal(g74,g72)
    c: Equal(g70,g64)
    c: Equal(g64,g66)
    c: Equal(g66,g68)
    c: Equal(g56,g58)
    c: Equal(g58,g60)
    c: Equal(g60,g62)
    c: Equal(g48,g50)
    c: Equal(g50,g52)
    c: Equal(g52,g54)
    c: Equal(g40,g42)
    c: Equal(g42,g44)
    c: Equal(g44,g46)
    c: Equal(g32,g34)
    c: Equal(g34,g36)
    c: Equal(g36,g38)
    c: Equal(g32,g40)
    c: Equal(g40,g48)
    c: Equal(g48,g56)
    c: Equal(g56,g64)
    c: Equal(g72,g64)
    c: Radius(g32) = 1.5
    c: DistanceY(g43,g41) = 20.05
    c: DistanceX(g33,g39) = 20.05
    c: DistanceX(g65,g71) = 20.05
    c: DistanceX(g73,g79) = 20.05
    c: DistanceY(g67,g65) = 20.05
    c: DistanceY(g75,g73) = 20.05
    c: DistanceY(g59,g57) = 20.05
    c: DistanceY(g51,g49) = 20.05
    c: DistanceX(g49,g55) = 77.2
    c: DistanceX(g57,g63) = 77.2
FEATURE [PartDesign::Pocket] Pocket016  label="f row"
  BaseFeature = -> Pad005
  Direction = (0,0,-1)
  Length = 5
  Length2 = 5
  Profile = -> Sketch022
  ReferenceAxis = -> Sketch022 [N_Axis]
  Type = 0
FEATURE [Sketcher::SketchObject] Sketch023
  AttachmentOffset = pos=(0,0,5) rot=(0,0,1;0rad)
  FullyConstrained = true
  MapMode = 5
  Placement = pos=(0,0,5) rot=(0,0,1;0rad)
  Support = -> [XY_Plane199]
  expr: Constraints[10] = Spreadsheet.u * 3 + 1
  expr: Constraints[12] = Spreadsheet.u
  expr: Constraints[15] = Spreadsheet.u
  expr: Constraints[2] = Spreadsheet.u * 15 + 1
  expr: Constraints[3] = Spreadsheet.u * 2 - 0.5
  expr: Constraints[4] = Spreadsheet.PCB_width - Spreadsheet.u * 5.25 - 0.5
  expr: Constraints[56] = Spreadsheet.key_fillet
  expr: Constraints[6] = Spreadsheet.u * 5 + 1
  expr: Constraints[8] = Spreadsheet.u * (1.25 * 3 + 6.25 + 1 * 3) + 1
  sketch-geometry (25):
    g0: LineSegment StartX=39.1 StartY=-38.4875 StartZ=0 EndX=322.85 EndY=-38.4875 EndZ=0
    g1: GeomPoint X=180.975 Y=-38.4875 Z=0
    g2: LineSegment StartX=37.6 StartY=-39.9875 StartZ=0 EndX=37.6 EndY=-133.237 EndZ=0
    g3: LineSegment StartX=39.1 StartY=-134.737 StartZ=0 EndX=284.75 EndY=-134.737 EndZ=0
    g4: LineSegment StartX=324.35 StartY=-39.9875 StartZ=0 EndX=324.35 EndY=-95.1375 EndZ=0
    g5: LineSegment StartX=286.25 StartY=-133.238 StartZ=0 EndX=286.25 EndY=-117.187 EndZ=0
    g6: LineSegment StartX=322.85 StartY=-96.6375 StartZ=0 EndX=306.8 EndY=-96.6375 EndZ=0
    g7: LineSegment StartX=287.75 StartY=-115.688 StartZ=0 EndX=303.8 EndY=-115.688 EndZ=0
    g8: LineSegment StartX=305.3 StartY=-98.1375 StartZ=0 EndX=305.3 EndY=-114.188 EndZ=0
    g9: ArcOfCircle CenterX=39.1 CenterY=-39.9875 CenterZ=0 NormalX=0 NormalY=0 NormalZ=1 AngleXU=0 Radius=1.5 StartAngle=1.5708 EndAngle=3.14159
    g10: GeomPoint X=37.6 Y=-38.4875 Z=0
    g11: ArcOfCircle CenterX=39.1 CenterY=-133.237 CenterZ=0 NormalX=0 NormalY=0 NormalZ=1 AngleXU=0 Radius=1.5 StartAngle=3.14159 EndAngle=4.71239
    g12: GeomPoint X=37.6 Y=-134.738 Z=0
    g13: ArcOfCircle CenterX=284.75 CenterY=-133.237 CenterZ=0 NormalX=0 NormalY=0 NormalZ=1 AngleXU=0 Radius=1.5 StartAngle=4.71239 EndAngle=6.28319
    g14: GeomPoint X=286.25 Y=-134.738 Z=0
    g15: ArcOfCircle CenterX=287.75 CenterY=-117.188 CenterZ=0 NormalX=0 NormalY=0 NormalZ=1 AngleXU=0 Radius=1.5 StartAngle=1.5708 EndAngle=3.14159
    g16: GeomPoint X=286.25 Y=-115.688 Z=0
    g17: ArcOfCircle CenterX=303.8 CenterY=-114.187 CenterZ=0 NormalX=0 NormalY=0 NormalZ=1 AngleXU=0 Radius=1.5 StartAngle=4.71239 EndAngle=6.28319
    g18: GeomPoint X=305.3 Y=-115.688 Z=0
    g19: ArcOfCircle CenterX=306.8 CenterY=-98.1375 CenterZ=0 NormalX=0 NormalY=0 NormalZ=1 AngleXU=0 Radius=1.5 StartAngle=1.5708 EndAngle=3.14159
    g20: GeomPoint X=305.3 Y=-96.6375 Z=0
    g21: ArcOfCircle CenterX=322.85 CenterY=-95.1375 CenterZ=0 NormalX=0 NormalY=0 NormalZ=1 AngleXU=0 Radius=1.5 StartAngle=4.71239 EndAngle=6.28319
    g22: GeomPoint X=324.35 Y=-96.6375 Z=0
    g23: ArcOfCircle CenterX=322.85 CenterY=-39.9875 CenterZ=0 NormalX=0 NormalY=0 NormalZ=1 AngleXU=0 Radius=1.5 StartAngle=-1.1617e-12 EndAngle=1.5708
    g24: GeomPoint X=324.35 Y=-38.4875 Z=0
  constraints (57):
    c: Horizontal(g0)
    c: Symmetric(g10,g24,g1)
    c: DistanceX(g10,g24) = 286.75
    c: DistanceX(g-1,g10) = 37.6
    c: DistanceY(g10,g-1) = 38.4875
    c: Vertical(g2)
    c: DistanceY(g12,g10) = 96.25
    c: Horizontal(g3)
    c: DistanceX(g12,g14) = 248.65
    c: Vertical(g4)
    c: DistanceY(g22,g24) = 58.15
    c: Vertical(g5)
    c: DistanceY(g14,g16) = 19.05
    c: Horizontal(g6)
    c: Horizontal(g7)
    c: DistanceX(g20,g22) = 19.05
    c: Vertical(g8)
    c: PointOnObject(g10,g0)
    c: PointOnObject(g10,g2)
    c: Tangent(g0,g9) = 1.5708
    c: Tangent(g2,g9) = -1.5708
    c: PointOnObject(g12,g2)
    c: PointOnObject(g12,g3)
    c: Tangent(g2,g11) = -1.5708
    c: Tangent(g3,g11) = -1.5708
    c: PointOnObject(g14,g3)
    c: PointOnObject(g14,g5)
    c: Tangent(g3,g13) = -1.5708
    c: Tangent(g5,g13) = -1.5708
    c: PointOnObject(g16,g5)
    c: PointOnObject(g16,g7)
    c: Tangent(g5,g15) = 1.5708
    c: Tangent(g7,g15) = 1.5708
    c: PointOnObject(g18,g7)
    c: PointOnObject(g18,g8)
    c: Tangent(g7,g17) = -1.5708
    c: Tangent(g8,g17) = 1.5708
    c: PointOnObject(g20,g6)
    c: PointOnObject(g20,g8)
    c: Tangent(g6,g19) = -1.5708
    c: Tangent(g8,g19) = -1.5708
    c: PointOnObject(g22,g4)
    c: PointOnObject(g22,g6)
    c: Tangent(g4,g21) = 1.5708
    c: Tangent(g6,g21) = 1.5708
    c: PointOnObject(g24,g0)
    c: PointOnObject(g24,g4)
    c: Tangent(g0,g23) = 1.5708
    c: Tangent(g4,g23) = 1.5708
    c: Equal(g13,g15)
    c: Equal(g15,g17)
    c: Equal(g17,g19)
    c: Equal(g19,g21)
    c: Equal(g21,g23)
    c: Equal(g23,g9)
    c: Equal(g9,g11)
    c: Radius(g9) = 1.5
FEATURE [PartDesign::Pocket] Pocket017  label="alpha"
  BaseFeature = -> Pocket016
  Direction = (0,0,-1)
  Length = 5
  Length2 = 5
  Profile = -> Sketch023
  ReferenceAxis = -> Sketch023 [N_Axis]
  Type = 0
FEATURE [Sketcher::SketchObject] Sketch024
  AttachmentOffset = pos=(0,0,5) rot=(0,0,1;0rad)
  FullyConstrained = true
  MapMode = 5
  Placement = pos=(0,0,5) rot=(0,0,1;0rad)
  Support = -> [XY_Plane199]
  expr: Constraints[28] = Spreadsheet.key_fillet
  expr: Constraints[5] = Spreadsheet.u * 4 + 1
  expr: Constraints[6] = Spreadsheet.u + 1
  expr: Constraints[7] = Spreadsheet.u * (0.5 + 17 + 0.5)
  expr: Constraints[8] = Spreadsheet.PCB_width - Spreadsheet.u * (1 + 0.25 + 2)
  sketch-geometry (13):
    g0: LineSegment StartX=332.875 StartY=-39.9875 StartZ=0 EndX=332.875 EndY=-114.188 EndZ=0
    g1: LineSegment StartX=334.375 StartY=-115.688 StartZ=0 EndX=351.425 EndY=-115.688 EndZ=0
    g2: LineSegment StartX=352.925 StartY=-114.188 StartZ=0 EndX=352.925 EndY=-39.9875 EndZ=0
    g3: LineSegment StartX=351.425 StartY=-38.4875 StartZ=0 EndX=334.375 EndY=-38.4875 EndZ=0
    g4: GeomPoint X=342.9 Y=-77.0875 Z=0
    g5: ArcOfCircle CenterX=334.375 CenterY=-39.9875 CenterZ=0 NormalX=0 NormalY=0 NormalZ=1 AngleXU=0 Radius=1.5 StartAngle=1.5708 EndAngle=3.14159
    g6: GeomPoint X=332.875 Y=-38.4875 Z=0
    g7: ArcOfCircle CenterX=334.375 CenterY=-114.188 CenterZ=0 NormalX=0 NormalY=0 NormalZ=1 AngleXU=0 Radius=1.5 StartAngle=3.14159 EndAngle=4.71239
    g8: GeomPoint X=332.875 Y=-115.687 Z=0
    g9: ArcOfCircle CenterX=351.425 CenterY=-39.9875 CenterZ=0 NormalX=0 NormalY=0 NormalZ=1 AngleXU=0 Radius=1.5 StartAngle=7e-16 EndAngle=1.5708
    g10: GeomPoint X=352.925 Y=-38.4875 Z=0
    g11: ArcOfCircle CenterX=351.425 CenterY=-114.188 CenterZ=0 NormalX=0 NormalY=0 NormalZ=1 AngleXU=0 Radius=1.5 StartAngle=4.71239 EndAngle=6.28319
    g12: GeomPoint X=352.925 Y=-115.687 Z=0
  constraints (29):
    c: Horizontal(g1)
    c: Horizontal(g3)
    c: Vertical(g0)
    c: Vertical(g2)
    c: Symmetric(g12,g6,g4)
    c: DistanceY(g12,g10) = 77.2
    c: DistanceX(g6,g10) = 20.05
    c: DistanceX(g-1,g4) = 342.9
    c: DistanceY(g4,g-1) = 77.0875
    c: PointOnObject(g6,g0)
    c: PointOnObject(g6,g3)
    c: Tangent(g0,g5) = -1.5708
    c: Tangent(g3,g5) = -1.5708
    c: PointOnObject(g8,g0)
    c: PointOnObject(g8,g1)
    c: Tangent(g0,g7) = -1.5708
    c: Tangent(g1,g7) = -1.5708
    c: PointOnObject(g10,g2)
    c: PointOnObject(g10,g3)
    c: Tangent(g2,g9) = -1.5708
    c: Tangent(g3,g9) = -1.5708
    c: PointOnObject(g12,g1)
    c: PointOnObject(g12,g2)
    c: Tangent(g1,g11) = -1.5708
    c: Tangent(g2,g11) = -1.5708
    c: Equal(g5,g7)
    c: Equal(g7,g11)
    c: Equal(g11,g9)
    c: Radius(g5) = 1.5
FEATURE [PartDesign::Pocket] Pocket018  label="right thiny"
  BaseFeature = -> Pocket017
  Direction = (0,0,-1)
  Length = 5
  Length2 = 5
  Profile = -> Sketch024
  ReferenceAxis = -> Sketch024 [N_Axis]
  Type = 0
FEATURE [Sketcher::SketchObject] Sketch025
  AttachmentOffset = pos=(0,0,5) rot=(0,0,1;0rad)
  FullyConstrained = true
  MapMode = 5
  Placement = pos=(0,0,5) rot=(0,0,1;0rad)
  Support = -> [XY_Plane199]
  expr: Constraints[12] = Spreadsheet.u
  expr: Constraints[13] = Spreadsheet.u + 1
  expr: Constraints[1] = Spreadsheet.u * 3 + 1
  expr: Constraints[2] = Spreadsheet.u * (15 + 0.25) - 0.5
  expr: Constraints[3] = Spreadsheet.PCB_width + 0.5
  expr: Constraints[47] = Spreadsheet.u + 1
  expr: Constraints[55] = Spreadsheet.key_fillet
  expr: Constraints[6] = Spreadsheet.u + 1
  expr: Constraints[7] = Spreadsheet.u
  sketch-geometry (24):
    g0: LineSegment StartX=291.512 StartY=-139.5 StartZ=0 EndX=346.663 EndY=-139.5 EndZ=0
    g1: LineSegment StartX=290.012 StartY=-138 StartZ=0 EndX=290.012 EndY=-120.95 EndZ=0
    g2: LineSegment StartX=291.512 StartY=-119.45 StartZ=0 EndX=307.562 EndY=-119.45 EndZ=0
    g3: LineSegment StartX=309.062 StartY=-117.95 StartZ=0 EndX=309.062 EndY=-101.9 EndZ=0
    g4: LineSegment StartX=310.562 StartY=-100.4 StartZ=0 EndX=327.613 EndY=-100.4 EndZ=0
    g5: LineSegment StartX=329.112 StartY=-101.9 StartZ=0 EndX=329.112 EndY=-117.95 EndZ=0
    g6: LineSegment StartX=330.612 StartY=-119.45 StartZ=0 EndX=346.663 EndY=-119.45 EndZ=0
    g7: LineSegment StartX=348.163 StartY=-138 StartZ=0 EndX=348.163 EndY=-120.95 EndZ=0
    g8: ArcOfCircle CenterX=346.663 CenterY=-138 CenterZ=0 NormalX=0 NormalY=0 NormalZ=1 AngleXU=0 Radius=1.5 StartAngle=4.71239 EndAngle=6.28319
    g9: GeomPoint X=348.162 Y=-139.5 Z=0
    g10: ArcOfCircle CenterX=346.663 CenterY=-120.95 CenterZ=0 NormalX=0 NormalY=0 NormalZ=1 AngleXU=0 Radius=1.5 StartAngle=1.48e-14 EndAngle=1.5708
    g11: GeomPoint X=348.163 Y=-119.45 Z=0
    g12: ArcOfCircle CenterX=330.612 CenterY=-117.95 CenterZ=0 NormalX=0 NormalY=0 NormalZ=1 AngleXU=0 Radius=1.5 StartAngle=3.14159 EndAngle=4.71239
    g13: GeomPoint X=329.113 Y=-119.45 Z=0
    g14: ArcOfCircle CenterX=327.612 CenterY=-101.9 CenterZ=0 NormalX=0 NormalY=0 NormalZ=1 AngleXU=0 Radius=1.5 StartAngle=4.8e-15 EndAngle=1.5708
    g15: GeomPoint X=329.112 Y=-100.4 Z=0
    g16: ArcOfCircle CenterX=310.562 CenterY=-101.9 CenterZ=0 NormalX=0 NormalY=0 NormalZ=1 AngleXU=0 Radius=1.5 StartAngle=1.5708 EndAngle=3.14159
    g17: GeomPoint X=309.062 Y=-100.4 Z=0
    g18: ArcOfCircle CenterX=307.562 CenterY=-117.95 CenterZ=0 NormalX=0 NormalY=0 NormalZ=1 AngleXU=0 Radius=1.5 StartAngle=4.71239 EndAngle=6.28319
    g19: GeomPoint X=309.062 Y=-119.45 Z=0
    g20: ArcOfCircle CenterX=291.512 CenterY=-120.95 CenterZ=0 NormalX=0 NormalY=0 NormalZ=1 AngleXU=0 Radius=1.5 StartAngle=1.5708 EndAngle=3.14159
    g21: GeomPoint X=290.012 Y=-119.45 Z=0
    g22: ArcOfCircle CenterX=291.512 CenterY=-138 CenterZ=0 NormalX=0 NormalY=0 NormalZ=1 AngleXU=0 Radius=1.5 StartAngle=3.14159 EndAngle=4.71239
    g23: GeomPoint X=290.012 Y=-139.5 Z=0
  constraints (56):
    c: Horizontal(g0)
    c: DistanceX(g23,g9) = 58.15
    c: DistanceX(g-1,g23) = 290.012
    c: DistanceY(g23,g-1) = 139.5
    c: Vertical(g1)
    c: Horizontal(g2)
    c: DistanceY(g23,g21) = 20.05
    c: DistanceX(g21,g19) = 19.05
    c: Vertical(g3)
    c: Horizontal(g4)
    c: Vertical(g5)
    c: Horizontal(g6)
    c: DistanceY(g19,g17) = 19.05
    c: DistanceX(g17,g15) = 20.05
    c: Vertical(g7)
    c: PointOnObject(g9,g0)
    c: PointOnObject(g9,g7)
    c: Tangent(g0,g8) = -1.5708
    c: Tangent(g7,g8) = -1.5708
    c: PointOnObject(g11,g6)
    c: PointOnObject(g11,g7)
    c: Tangent(g6,g10) = 1.5708
    c: Tangent(g7,g10) = -1.5708
    c: PointOnObject(g13,g5)
    c: PointOnObject(g13,g6)
    c: Tangent(g5,g12) = -1.5708
    c: Tangent(g6,g12) = -1.5708
    c: PointOnObject(g15,g4)
    c: PointOnObject(g15,g5)
    c: Tangent(g4,g14) = 1.5708
    c: Tangent(g5,g14) = 1.5708
    c: PointOnObject(g17,g3)
    c: PointOnObject(g17,g4)
    c: Tangent(g3,g16) = 1.5708
    c: Tangent(g4,g16) = 1.5708
    c: PointOnObject(g19,g2)
    c: PointOnObject(g19,g3)
    c: Tangent(g2,g18) = -1.5708
    c: Tangent(g3,g18) = -1.5708
    c: PointOnObject(g21,g1)
    c: PointOnObject(g21,g2)
    c: Tangent(g1,g20) = 1.5708
    c: Tangent(g2,g20) = 1.5708
    c: PointOnObject(g23,g0)
    c: PointOnObject(g23,g1)
    c: Tangent(g0,g22) = -1.5708
    c: Tangent(g1,g22) = 1.5708
    c: DistanceY(g9,g11) = 20.05
    c: Equal(g22,g8)
    c: Equal(g8,g10)
    c: Equal(g10,g12)
    c: Equal(g12,g14)
    c: Equal(g14,g16)
    c: Equal(g16,g18)
    c: Equal(g18,g20)
    c: Radius(g16) = 1.5
FEATURE [PartDesign::Pocket] Pocket019  label="arrow keys"
  BaseFeature = -> Pocket018
  Direction = (0,0,-1)
  Length = 5
  Length2 = 5
  Profile = -> Sketch025
  ReferenceAxis = -> Sketch025 [N_Axis]
  Type = 0
FEATURE [Sketcher::SketchObject] Sketch026
  AttachmentOffset = pos=(0,0,5) rot=(0,0,1;0rad)
  FullyConstrained = false
  MapMode = 5
  Placement = pos=(0,0,5) rot=(0,0,1;0rad)
  Support = -> [XY_Plane199]
  expr: Constraints[10] = Spreadsheet.screen_module_width
  expr: Constraints[11] = Spreadsheet.u
  expr: Constraints[9] = Spreadsheet.screen_module_length
  sketch-geometry (5):
    g0: LineSegment StartX=5.4 StartY=-41.9625 StartZ=0 EndX=5.4 EndY=-93.1625 EndZ=0
    g1: LineSegment StartX=5.4 StartY=-93.1625 StartZ=0 EndX=32.7 EndY=-93.1625 EndZ=0
    g2: LineSegment StartX=32.7 StartY=-93.1625 StartZ=0 EndX=32.7 EndY=-41.9625 EndZ=0
    g3: LineSegment StartX=32.7 StartY=-41.9625 StartZ=0 EndX=5.4 EndY=-41.9625 EndZ=0
    g4: GeomPoint X=19.05 Y=-67.5625 Z=0
  constraints (12):
    c: Coincident(g0,g1)
    c: Coincident(g1,g2)
    c: Coincident(g2,g3)
    c: Coincident(g3,g0)
    c: Horizontal(g1)
    c: Horizontal(g3)
    c: Vertical(g0)
    c: Vertical(g2)
    c: Symmetric(g1,g0,g4)
    c: DistanceY(g0,g0) = 51.2
    c: DistanceX(g3,g3) = 27.3
    c: DistanceX(g-1,g4) = 19.05
FEATURE [PartDesign::Pocket] Pocket020  label="misc"
  BaseFeature = -> Pocket019
  Direction = (0,0,-1)
  Length = 5
  Length2 = 5
  Profile = -> Sketch026
  ReferenceAxis = -> Sketch026 [N_Axis]
  Type = 0
FEATURE [Sketcher::SketchObject] Sketch027
  AttachmentOffset = pos=(0,0,2.9) rot=(0,0,1;0rad)
  FullyConstrained = false
  MapMode = 5
  Placement = pos=(0,0,2.9) rot=(0,0,1;0rad)
  Support = -> [XY_Plane201]
  expr: .AttachmentOffset.Base.z = 1.6 + 1.3
  expr: Constraints[25] = Spreadsheet.Bottom_c_rad
  expr: Constraints[26] = Spreadsheet.Bottom_c_rad
  expr: Constraints[31] = Spreadsheet.PCB_length + Spreadsheet.pcb_to_wall_gap * 2
  expr: Constraints[32] = Spreadsheet.PCB_width + Spreadsheet.pcb_to_wall_gap * 2
  expr: Constraints[34] = 2 * Spreadsheet.Top_c_rad * sin(45 / 2)
  expr: Constraints[40] = Spreadsheet.Screw_hole
  expr: Constraints[41] = Spreadsheet.wall_thickness / 2
  expr: Constraints[42] = Spreadsheet.PCB_length / 2
  expr: Constraints[43] = (Spreadsheet.PCB_length + Spreadsheet.pcb_to_wall_gap * 2 + Spreadsheet.wall_thickness * 2) / 4
  expr: Constraints[44] = (Spreadsheet.PCB_length + Spreadsheet.pcb_to_wall_gap * 2 + Spreadsheet.wall_thickness * 2) / 4
  expr: Constraints[52] = Spreadsheet.wall_thickness / 2
  expr: Constraints[55] = 2 * Spreadsheet.Bottom_c_rad * sin(45 / 2)
  expr: Constraints[57] = 2 * Spreadsheet.Bottom_c_rad * sin(45 / 2)
  expr: Constraints[5] = Spreadsheet.PCB_length / 2
  expr: Constraints[6] = Spreadsheet.PCB_width / 2
  expr: Constraints[7] = Spreadsheet.PCB_width + 2 * Spreadsheet.pcb_to_wall_gap + 2 * Spreadsheet.wall_thickness
  expr: Constraints[8] = Spreadsheet.PCB_length + 2 * Spreadsheet.pcb_to_wall_gap + 2 * Spreadsheet.wall_thickness
  sketch-geometry (36):
    g0: LineSegment StartX=-6.5 StartY=0.5 StartZ=0 EndX=-6.5 EndY=-142.5 EndZ=0
    g1: LineSegment StartX=-3.5 StartY=-145.5 StartZ=0 EndX=355.925 EndY=-145.5 EndZ=0
    g2: LineSegment StartX=358.925 StartY=-142.5 StartZ=0 EndX=358.925 EndY=0.5 EndZ=0
    g3: LineSegment StartX=352.925 StartY=6.5 StartZ=0 EndX=-0.5 EndY=6.5 EndZ=0
    g4: GeomPoint X=176.213 Y=-69.5 Z=0
    g5: ArcOfCircle CenterX=-0.5 CenterY=0.5 CenterZ=0 NormalX=0 NormalY=0 NormalZ=1 AngleXU=0 Radius=6 StartAngle=1.5708 EndAngle=3.14159
    g6: GeomPoint X=-6.5 Y=6.5 Z=0
    g7: ArcOfCircle CenterX=352.925 CenterY=0.5 CenterZ=0 NormalX=0 NormalY=0 NormalZ=1 AngleXU=0 Radius=6 StartAngle=1e-16 EndAngle=1.5708
    g8: GeomPoint X=358.925 Y=6.5 Z=0
    g9: ArcOfCircle CenterX=-3.5 CenterY=-142.5 CenterZ=0 NormalX=0 NormalY=0 NormalZ=1 AngleXU=0 Radius=3 StartAngle=3.14159 EndAngle=4.71239
    g10: GeomPoint X=-6.5 Y=-145.5 Z=0
    g11: ArcOfCircle CenterX=355.925 CenterY=-142.5 CenterZ=0 NormalX=0 NormalY=0 NormalZ=1 AngleXU=0 Radius=3 StartAngle=4.71239 EndAngle=6.28319
    g12: GeomPoint X=358.925 Y=-145.5 Z=0
    g13: Circle CenterX=-1.74264 CenterY=1.74264 CenterZ=0 NormalX=0 NormalY=0 NormalZ=1 AngleXU=0 Radius=1.05
    g14: GeomPoint X=176.213 Y=-69.5 Z=0
    g15: GeomPoint X=-1.66549 Y=1.10512 Z=0
    g16: GeomPoint X=351.76 Y=0.5 Z=0
    g17: GeomPoint X=354.09 Y=-140.105 Z=0
    g18: GeomPoint X=-0.5 Y=-138.895 Z=0
    g19: GeomPoint X=-4.74264 Y=4.74264 Z=0
    g20: GeomPoint X=1.25736 Y=-1.25736 Z=0
    g21: Circle CenterX=354.168 CenterY=1.74264 CenterZ=0 NormalX=0 NormalY=0 NormalZ=1 AngleXU=0 Radius=1.05
    g22: GeomPoint X=351.168 Y=-1.25736 Z=0
    g23: GeomPoint X=357.168 Y=4.74264 Z=0
    g24: Circle CenterX=84.8563 CenterY=3.5 CenterZ=0 NormalX=0 NormalY=0 NormalZ=1 AngleXU=0 Radius=1.05
    g25: Circle CenterX=176.213 CenterY=3.5 CenterZ=0 NormalX=0 NormalY=0 NormalZ=1 AngleXU=0 Radius=1.05
    g26: Circle CenterX=267.569 CenterY=3.5 CenterZ=0 NormalX=0 NormalY=0 NormalZ=1 AngleXU=0 Radius=1.05
    g27: Circle CenterX=84.8563 CenterY=-142.5 CenterZ=0 NormalX=0 NormalY=0 NormalZ=1 AngleXU=0 Radius=1.05
    g28: Circle CenterX=176.213 CenterY=-142.5 CenterZ=0 NormalX=0 NormalY=0 NormalZ=1 AngleXU=0 Radius=1.05
    g29: Circle CenterX=267.569 CenterY=-142.5 CenterZ=0 NormalX=0 NormalY=0 NormalZ=1 AngleXU=0 Radius=1.05
    g30: Circle CenterX=-2.62132 CenterY=-141.621 CenterZ=0 NormalX=0 NormalY=0 NormalZ=1 AngleXU=0 Radius=1.05
    g31: GeomPoint X=0.37868 Y=-138.621 Z=0
    g32: GeomPoint X=-5.62132 Y=-144.621 Z=0
    g33: GeomPoint X=352.046 Y=-138.621 Z=0
    g34: GeomPoint X=358.046 Y=-144.621 Z=0
    g35: Circle CenterX=355.046 CenterY=-141.621 CenterZ=0 NormalX=0 NormalY=0 NormalZ=1 AngleXU=0 Radius=1.05
  constraints (70):
    c: Horizontal(g1)
    c: Horizontal(g3)
    c: Vertical(g0)
    c: Vertical(g2)
    c: Symmetric(g12,g6,g4)
    c: DistanceX(g-1,g4) = 176.213
    c: DistanceY(g4,g-1) = 69.5
    c: DistanceY(g10,g6) = 152
    c: DistanceX(g6,g8) = 365.425
    c: PointOnObject(g6,g0)
    c: PointOnObject(g6,g3)
    c: Tangent(g0,g5) = -1.5708
    c: Tangent(g3,g5) = -1.5708
    c: PointOnObject(g8,g2)
    c: PointOnObject(g8,g3)
    c: Tangent(g2,g7) = -1.5708
    c: Tangent(g3,g7) = -1.5708
    c: PointOnObject(g10,g0)
    c: PointOnObject(g10,g1)
    c: Tangent(g0,g9) = -1.5708
    c: Tangent(g1,g9) = -1.5708
    c: PointOnObject(g12,g1)
    c: PointOnObject(g12,g2)
    c: Tangent(g1,g11) = -1.5708
    c: Tangent(g2,g11) = -1.5708
    c: Radius(g11) = 3
    c: Radius(g9) = 3
    c: Radius(g5) = 6
    c: Radius(g7) = 6
    c: Symmetric(g17,g15,g14)
    c: Coincident(g14,g4)
    c: DistanceX(g15,g16) = 353.425
    c: DistanceY(g18,g15) = 140
    c: PointOnObject(g19,g5)
    c: Distance(g0,g19) = 4.5922
    c: Symmetric(g19,g20,g13)
    c: PointOnObject(g23,g7)
    c: Symmetric(g22,g23,g21)
    c: Equal(g24,g25)
    c: Equal(g26,g25)
    c: Diameter(g25) = 2.1
    c: Distance(g25,g3) = 3
    c: DistanceX(g-1,g25) = 176.213
    c: DistanceX(g24,g25) = 91.3563
    c: DistanceX(g25,g26) = 91.3563
    c: Equal(g27,g28)
    c: Equal(g29,g28)
    c: Equal(g25,g28) = 3.1
    c: DistanceX(g27,g28) = 91.3563
    c: DistanceX(g28,g29) = 91.3563
    c: Horizontal(g27,g28)
    c: Horizontal(g29,g28)
    c: Distance(g28,g1) = 3
    c: Vertical(g28,g25)
    c: PointOnObject(g32,g9)
    c: Distance(g0,g32) = 2.2961
    c: PointOnObject(g34,g11)
    c: Distance(g1,g34) = 2.2961
    c: Symmetric(g33,g34,g35)
    c: Symmetric(g32,g31,g30)
    c: Horizontal(g24,g25)
    c: Horizontal(g26,g25)
    c: Block(g13)
    c: Block(g30)
    c: Block(g35)
    c: Block(g21)
    c: Equal(g13,g24)
    c: Equal(g26,g21)
    c: Equal(g35,g29)
    c: Equal(g30,g27)
FEATURE [PartDesign::Pad] Pad006
  Direction = (0,0,1)
  Length = 2
  Length2 = 10
  Profile = -> Sketch027
  ReferenceAxis = -> Sketch027 [N_Axis]
  Type = 0
FEATURE [Sketcher::SketchObject] Sketch028
  AttachmentOffset = pos=(0,0,5) rot=(0,0,1;0rad)
  FullyConstrained = true
  MapMode = 5
  Placement = pos=(0,0,5) rot=(0,0,1;0rad)
  Support = -> [XY_Plane201]
  expr: Constraints[10] = Spreadsheet.PCB_width - Spreadsheet.u * 6
  expr: Constraints[11] = Spreadsheet.u * 2.5
  expr: Constraints[12] = Spreadsheet.u + 1
  expr: Constraints[13] = Spreadsheet.u * 4 + 1
  expr: Constraints[15] = Spreadsheet.u * (0.5 + 0.25 + 2)
  expr: Constraints[166] = Spreadsheet.u + 1
  expr: Constraints[167] = Spreadsheet.key_fillet
  expr: Constraints[168] = Spreadsheet.u + 1
  expr: Constraints[169] = Spreadsheet.u + 1
  expr: Constraints[170] = Spreadsheet.u * 4 + 1
  expr: Constraints[171] = Spreadsheet.u * 4 + 1
  expr: Constraints[172] = Spreadsheet.u + 1
  expr: Constraints[173] = Spreadsheet.u + 1
  expr: Constraints[174] = Spreadsheet.u + 1
  expr: Constraints[175] = Spreadsheet.u + 1
  expr: Constraints[176] = Spreadsheet.u + 1
  expr: Constraints[22] = Spreadsheet.u * (2 + 0.25 + 2)
  expr: Constraints[41] = Spreadsheet.u * (2 + 0.25 + 2)
  expr: Constraints[42] = Spreadsheet.u * (0.5 + 2 + 0.25)
  expr: Constraints[43] = Spreadsheet.u * 1.5
  expr: Constraints[47] = 13.5
  expr: Constraints[48] = Spreadsheet.u
  expr: Constraints[49] = Spreadsheet.u
  sketch-geometry (80):
    g0: Circle CenterX=9.525 CenterY=-24.7 CenterZ=0 NormalX=0 NormalY=0 NormalZ=1 AngleXU=0 Radius=6.75
    g1: Circle CenterX=28.575 CenterY=-24.7 CenterZ=0 NormalX=0 NormalY=0 NormalZ=1 AngleXU=0 Radius=6.75
    g2: LineSegment StartX=37.6 StartY=-16.175 StartZ=0 EndX=37.6 EndY=-33.225 EndZ=0
    g3: LineSegment StartX=39.1 StartY=-34.725 StartZ=0 EndX=56.15 EndY=-34.725 EndZ=0
    g4: LineSegment StartX=57.65 StartY=-33.225 StartZ=0 EndX=57.65 EndY=-16.175 EndZ=0
    g5: LineSegment StartX=56.15 StartY=-14.675 StartZ=0 EndX=39.1 EndY=-14.675 EndZ=0
    g6: GeomPoint X=47.625 Y=-24.7 Z=0
    g7: LineSegment StartX=61.4125 StartY=-16.175 StartZ=0 EndX=61.4125 EndY=-33.225 EndZ=0
    g8: LineSegment StartX=62.9125 StartY=-34.725 StartZ=0 EndX=137.113 EndY=-34.725 EndZ=0
    g9: LineSegment StartX=138.613 StartY=-33.225 StartZ=0 EndX=138.613 EndY=-16.175 EndZ=0
    g10: LineSegment StartX=137.113 StartY=-14.675 StartZ=0 EndX=62.9125 EndY=-14.675 EndZ=0
    g11: GeomPoint X=100.013 Y=-24.7 Z=0
    g12: LineSegment StartX=142.375 StartY=-16.175 StartZ=0 EndX=142.375 EndY=-33.225 EndZ=0
    g13: LineSegment StartX=143.875 StartY=-34.725 StartZ=0 EndX=218.075 EndY=-34.725 EndZ=0
    g14: LineSegment StartX=219.575 StartY=-33.225 StartZ=0 EndX=219.575 EndY=-16.175 EndZ=0
    g15: LineSegment StartX=218.075 StartY=-14.675 StartZ=0 EndX=143.875 EndY=-14.675 EndZ=0
    g16: GeomPoint X=180.975 Y=-24.7 Z=0
    g17: LineSegment StartX=223.338 StartY=-16.175 StartZ=0 EndX=223.338 EndY=-33.225 EndZ=0
    g18: LineSegment StartX=224.838 StartY=-34.725 StartZ=0 EndX=299.037 EndY=-34.725 EndZ=0
    g19: LineSegment StartX=300.537 StartY=-33.225 StartZ=0 EndX=300.537 EndY=-16.175 EndZ=0
    g20: LineSegment StartX=299.037 StartY=-14.675 StartZ=0 EndX=224.838 EndY=-14.675 EndZ=0
    g21: GeomPoint X=261.938 Y=-24.7 Z=0
    g22: LineSegment StartX=304.3 StartY=-16.175 StartZ=0 EndX=304.3 EndY=-33.225 EndZ=0
    g23: LineSegment StartX=305.8 StartY=-34.725 StartZ=0 EndX=322.85 EndY=-34.725 EndZ=0
    g24: LineSegment StartX=324.35 StartY=-33.225 StartZ=0 EndX=324.35 EndY=-16.175 EndZ=0
    g25: LineSegment StartX=322.85 StartY=-14.675 StartZ=0 EndX=305.8 EndY=-14.675 EndZ=0
    g26: GeomPoint X=314.325 Y=-24.7 Z=0
    g27: LineSegment StartX=332.875 StartY=-16.175 StartZ=0 EndX=332.875 EndY=-33.225 EndZ=0
    g28: LineSegment StartX=334.375 StartY=-34.725 StartZ=0 EndX=351.425 EndY=-34.725 EndZ=0
    g29: LineSegment StartX=352.925 StartY=-33.225 StartZ=0 EndX=352.925 EndY=-16.175 EndZ=0
    g30: LineSegment StartX=351.425 StartY=-14.675 StartZ=0 EndX=334.375 EndY=-14.675 EndZ=0
    g31: GeomPoint X=342.9 Y=-24.7 Z=0
    g32: ArcOfCircle CenterX=39.1 CenterY=-16.175 CenterZ=0 NormalX=0 NormalY=0 NormalZ=1 AngleXU=0 Radius=1.5 StartAngle=1.5708 EndAngle=3.14159
    g33: GeomPoint X=37.6 Y=-14.675 Z=0
    g34: ArcOfCircle CenterX=39.1 CenterY=-33.225 CenterZ=0 NormalX=0 NormalY=0 NormalZ=1 AngleXU=0 Radius=1.5 StartAngle=3.14159 EndAngle=4.71239
    g35: GeomPoint X=37.6 Y=-34.725 Z=0
    g36: ArcOfCircle CenterX=56.15 CenterY=-33.225 CenterZ=0 NormalX=0 NormalY=0 NormalZ=1 AngleXU=0 Radius=1.5 StartAngle=4.71239 EndAngle=6.28319
    g37: GeomPoint X=57.65 Y=-34.725 Z=0
    g38: ArcOfCircle CenterX=56.15 CenterY=-16.175 CenterZ=0 NormalX=0 NormalY=0 NormalZ=1 AngleXU=0 Radius=1.5 StartAngle=-9e-16 EndAngle=1.5708
    g39: GeomPoint X=57.65 Y=-14.675 Z=0
    g40: ArcOfCircle CenterX=62.9125 CenterY=-16.175 CenterZ=0 NormalX=0 NormalY=0 NormalZ=1 AngleXU=0 Radius=1.5 StartAngle=1.5708 EndAngle=3.14159
    g41: GeomPoint X=61.4125 Y=-14.675 Z=0
    g42: ArcOfCircle CenterX=62.9125 CenterY=-33.225 CenterZ=0 NormalX=0 NormalY=0 NormalZ=1 AngleXU=0 Radius=1.5 StartAngle=3.14159 EndAngle=4.71239
    g43: GeomPoint X=61.4125 Y=-34.725 Z=0
    g44: ArcOfCircle CenterX=137.113 CenterY=-33.225 CenterZ=0 NormalX=0 NormalY=0 NormalZ=1 AngleXU=0 Radius=1.5 StartAngle=4.71239 EndAngle=6.28319
    g45: GeomPoint X=138.613 Y=-34.725 Z=0
    g46: ArcOfCircle CenterX=137.113 CenterY=-16.175 CenterZ=0 NormalX=0 NormalY=0 NormalZ=1 AngleXU=0 Radius=1.5 StartAngle=-9e-16 EndAngle=1.5708
    g47: GeomPoint X=138.613 Y=-14.675 Z=0
    g48: ArcOfCircle CenterX=143.875 CenterY=-16.175 CenterZ=0 NormalX=0 NormalY=0 NormalZ=1 AngleXU=0 Radius=1.5 StartAngle=1.5708 EndAngle=3.14159
    g49: GeomPoint X=142.375 Y=-14.675 Z=0
    g50: ArcOfCircle CenterX=143.875 CenterY=-33.225 CenterZ=0 NormalX=0 NormalY=0 NormalZ=1 AngleXU=0 Radius=1.5 StartAngle=3.14159 EndAngle=4.71239
    g51: GeomPoint X=142.375 Y=-34.725 Z=0
    g52: ArcOfCircle CenterX=218.075 CenterY=-16.175 CenterZ=0 NormalX=0 NormalY=0 NormalZ=1 AngleXU=0 Radius=1.5 StartAngle=-9e-16 EndAngle=1.5708
    g53: GeomPoint X=219.575 Y=-14.675 Z=0
    g54: ArcOfCircle CenterX=218.075 CenterY=-33.225 CenterZ=0 NormalX=0 NormalY=0 NormalZ=1 AngleXU=0 Radius=1.5 StartAngle=4.71239 EndAngle=6.28319
    g55: GeomPoint X=219.575 Y=-34.725 Z=0
    g56: ArcOfCircle CenterX=224.838 CenterY=-33.225 CenterZ=0 NormalX=0 NormalY=0 NormalZ=1 AngleXU=0 Radius=1.5 StartAngle=3.14159 EndAngle=4.71239
    g57: GeomPoint X=223.338 Y=-34.725 Z=0
    g58: ArcOfCircle CenterX=224.838 CenterY=-16.175 CenterZ=0 NormalX=0 NormalY=0 NormalZ=1 AngleXU=0 Radius=1.5 StartAngle=1.5708 EndAngle=3.14159
    g59: GeomPoint X=223.338 Y=-14.675 Z=0
    g60: ArcOfCircle CenterX=299.037 CenterY=-16.175 CenterZ=0 NormalX=0 NormalY=0 NormalZ=1 AngleXU=0 Radius=1.5 StartAngle=0 EndAngle=1.5708
    g61: GeomPoint X=300.538 Y=-14.675 Z=0
    g62: ArcOfCircle CenterX=299.037 CenterY=-33.225 CenterZ=0 NormalX=0 NormalY=0 NormalZ=1 AngleXU=0 Radius=1.5 StartAngle=4.71239 EndAngle=6.28319
    g63: GeomPoint X=300.537 Y=-34.725 Z=0
    g64: ArcOfCircle CenterX=305.8 CenterY=-33.225 CenterZ=0 NormalX=0 NormalY=0 NormalZ=1 AngleXU=0 Radius=1.5 StartAngle=3.14159 EndAngle=4.71239
    g65: GeomPoint X=304.3 Y=-34.725 Z=0
    g66: ArcOfCircle CenterX=305.8 CenterY=-16.175 CenterZ=0 NormalX=0 NormalY=0 NormalZ=1 AngleXU=0 Radius=1.5 StartAngle=1.5708 EndAngle=3.14159
    g67: GeomPoint X=304.3 Y=-14.675 Z=0
    g68: ArcOfCircle CenterX=322.85 CenterY=-16.175 CenterZ=0 NormalX=0 NormalY=0 NormalZ=1 AngleXU=0 Radius=1.5 StartAngle=-9e-16 EndAngle=1.5708
    g69: GeomPoint X=324.35 Y=-14.675 Z=0
    g70: ArcOfCircle CenterX=322.85 CenterY=-33.225 CenterZ=0 NormalX=0 NormalY=0 NormalZ=1 AngleXU=0 Radius=1.5 StartAngle=4.71239 EndAngle=6.28319
    g71: GeomPoint X=324.35 Y=-34.725 Z=0
    g72: ArcOfCircle CenterX=334.375 CenterY=-33.225 CenterZ=0 NormalX=0 NormalY=0 NormalZ=1 AngleXU=0 Radius=1.5 StartAngle=3.14159 EndAngle=4.71239
    g73: GeomPoint X=332.875 Y=-34.725 Z=0
    g74: ArcOfCircle CenterX=334.375 CenterY=-16.175 CenterZ=0 NormalX=0 NormalY=0 NormalZ=1 AngleXU=0 Radius=1.5 StartAngle=1.5708 EndAngle=3.14159
    g75: GeomPoint X=332.875 Y=-14.675 Z=0
    g76: ArcOfCircle CenterX=351.425 CenterY=-16.175 CenterZ=0 NormalX=0 NormalY=0 NormalZ=1 AngleXU=0 Radius=1.5 StartAngle=2.7e-15 EndAngle=1.5708
    g77: GeomPoint X=352.925 Y=-14.675 Z=0
    g78: ArcOfCircle CenterX=351.425 CenterY=-33.225 CenterZ=0 NormalX=0 NormalY=0 NormalZ=1 AngleXU=0 Radius=1.5 StartAngle=4.71239 EndAngle=6.28319
    g79: GeomPoint X=352.925 Y=-34.725 Z=0
  constraints (180):
    c: Horizontal(g3)
    c: Horizontal(g5)
    c: Vertical(g2)
    c: Vertical(g4)
    c: Symmetric(g37,g33,g6)
    c: Horizontal(g8)
    c: Horizontal(g10)
    c: Vertical(g7)
    c: Vertical(g9)
    c: Symmetric(g45,g41,g11)
    c: DistanceY(g6,g-1) = 24.7
    c: DistanceX(g-1,g6) = 47.625
    c: DistanceY(g35,g33) = 20.05
    c: DistanceX(g41,g47) = 77.2
    c: Horizontal(g6,g11)
    c: DistanceX(g6,g11) = 52.3875
    c: Horizontal(g13)
    c: Horizontal(g15)
    c: Vertical(g12)
    c: Vertical(g14)
    c: Symmetric(g55,g49,g16)
    c: Horizontal(g11,g16)
    c: DistanceX(g11,g16) = 80.9625
    c: Horizontal(g18)
    c: Horizontal(g20)
    c: Vertical(g17)
    c: Vertical(g19)
    c: Symmetric(g63,g59,g21)
    c: Horizontal(g23)
    c: Horizontal(g25)
    c: Vertical(g22)
    c: Vertical(g24)
    c: Symmetric(g71,g67,g26)
    c: Horizontal(g28)
    c: Horizontal(g30)
    c: Vertical(g27)
    c: Vertical(g29)
    c: Symmetric(g79,g75,g31)
    c: Horizontal(g16,g21)
    c: Horizontal(g21,g26)
    c: Horizontal(g26,g31)
    c: DistanceX(g16,g21) = 80.9625
    c: DistanceX(g21,g26) = 52.3875
    c: DistanceX(g26,g31) = 28.575
    c: Equal(g0,g1)
    c: Horizontal(g1,g6)
    c: Horizontal(g0,g6)
    c: Diameter(g1) = 13.5
    c: DistanceX(g1,g6) = 19.05
    c: DistanceX(g0,g1) = 19.05
    c: PointOnObject(g33,g2)
    c: PointOnObject(g33,g5)
    c: Tangent(g2,g32) = -1.5708
    c: Tangent(g5,g32) = -1.5708
    c: PointOnObject(g35,g2)
    c: PointOnObject(g35,g3)
    c: Tangent(g2,g34) = -1.5708
    c: Tangent(g3,g34) = -1.5708
    c: PointOnObject(g37,g3)
    c: PointOnObject(g37,g4)
    c: Tangent(g3,g36) = -1.5708
    c: Tangent(g4,g36) = -1.5708
    c: PointOnObject(g39,g4)
    c: PointOnObject(g39,g5)
    c: Tangent(g4,g38) = -1.5708
    c: Tangent(g5,g38) = -1.5708
    c: PointOnObject(g41,g7)
    c: PointOnObject(g41,g10)
    c: Tangent(g7,g40) = -1.5708
    c: Tangent(g10,g40) = -1.5708
    c: PointOnObject(g43,g7)
    c: PointOnObject(g43,g8)
    c: Tangent(g7,g42) = -1.5708
    c: Tangent(g8,g42) = -1.5708
    c: PointOnObject(g45,g8)
    c: PointOnObject(g45,g9)
    c: Tangent(g8,g44) = -1.5708
    c: Tangent(g9,g44) = -1.5708
    c: PointOnObject(g47,g9)
    c: PointOnObject(g47,g10)
    c: Tangent(g9,g46) = -1.5708
    c: Tangent(g10,g46) = -1.5708
    c: PointOnObject(g49,g12)
    c: PointOnObject(g49,g15)
    c: Tangent(g12,g48) = -1.5708
    c: Tangent(g15,g48) = -1.5708
    c: PointOnObject(g51,g12)
    c: PointOnObject(g51,g13)
    c: Tangent(g12,g50) = -1.5708
    c: Tangent(g13,g50) = -1.5708
    c: PointOnObject(g53,g14)
    c: PointOnObject(g53,g15)
    c: Tangent(g14,g52) = -1.5708
    c: Tangent(g15,g52) = -1.5708
    c: PointOnObject(g55,g13)
    c: PointOnObject(g55,g14)
    c: Tangent(g13,g54) = -1.5708
    c: Tangent(g14,g54) = -1.5708
    c: PointOnObject(g57,g17)
    c: PointOnObject(g57,g18)
    c: Tangent(g17,g56) = -1.5708
    c: Tangent(g18,g56) = -1.5708
    c: PointOnObject(g59,g17)
    c: PointOnObject(g59,g20)
    c: Tangent(g17,g58) = -1.5708
    c: Tangent(g20,g58) = -1.5708
    c: PointOnObject(g61,g19)
    c: PointOnObject(g61,g20)
    c: Tangent(g19,g60) = -1.5708
    c: Tangent(g20,g60) = -1.5708
    c: PointOnObject(g63,g18)
    c: PointOnObject(g63,g19)
    c: Tangent(g18,g62) = -1.5708
    c: Tangent(g19,g62) = -1.5708
    c: PointOnObject(g65,g22)
    c: PointOnObject(g65,g23)
    c: Tangent(g22,g64) = -1.5708
    c: Tangent(g23,g64) = -1.5708
    c: PointOnObject(g67,g22)
    c: PointOnObject(g67,g25)
    c: Tangent(g22,g66) = -1.5708
    c: Tangent(g25,g66) = -1.5708
    c: PointOnObject(g69,g24)
    c: PointOnObject(g69,g25)
    c: Tangent(g24,g68) = -1.5708
    c: Tangent(g25,g68) = -1.5708
    c: PointOnObject(g71,g23)
    c: PointOnObject(g71,g24)
    c: Tangent(g23,g70) = -1.5708
    c: Tangent(g24,g70) = -1.5708
    c: PointOnObject(g73,g27)
    c: PointOnObject(g73,g28)
    c: Tangent(g27,g72) = -1.5708
    c: Tangent(g28,g72) = -1.5708
    c: PointOnObject(g75,g27)
    c: PointOnObject(g75,g30)
    c: Tangent(g27,g74) = -1.5708
    c: Tangent(g30,g74) = -1.5708
    c: PointOnObject(g77,g29)
    c: PointOnObject(g77,g30)
    c: Tangent(g29,g76) = -1.5708
    c: Tangent(g30,g76) = -1.5708
    c: Equal(g34,g36)
    c: Equal(g36,g38)
    c: Equal(g38,g32)
    c: Equal(g40,g32)
    c: Equal(g42,g44)
    c: Equal(g44,g46)
    c: Equal(g46,g40)
    c: Equal(g48,g40)
    c: Equal(g50,g54)
    c: Equal(g54,g52)
    c: Equal(g48,g52)
    c: Equal(g56,g62)
    c: Equal(g62,g60)
    c: Equal(g60,g58)
    c: Equal(g58,g48)
    c: Equal(g64,g70)
    c: Equal(g70,g68)
    c: Equal(g68,g66)
    c: PointOnObject(g79,g28)
    c: PointOnObject(g79,g29)
    c: Tangent(g28,g78) = -1.5708
    c: Tangent(g29,g78) = -1.5708
    c: Equal(g72,g78)
    c: Equal(g78,g76)
    c: DistanceX(g33,g39) = 20.05
    c: Radius(g32) = 1.5
    c: DistanceY(g43,g41) = 20.05
    c: DistanceY(g51,g49) = 20.05
    c: DistanceX(g49,g53) = 77.2
    c: DistanceX(g59,g61) = 77.2
    c: DistanceY(g57,g59) = 20.05
    c: DistanceY(g65,g67) = 20.05
    c: DistanceY(g73,g75) = 20.05
    c: DistanceX(g67,g69) = 20.05
    c: DistanceX(g75,g77) = 20.05
    c: Equal(g66,g58)
    c: Equal(g74,g66)
    c: Equal(g76,g74)
FEATURE [PartDesign::Pocket] Pocket021  label="f row001"
  BaseFeature = -> Pad006
  Direction = (0,0,-1)
  Length = 5
  Length2 = 5
  Profile = -> Sketch028
  ReferenceAxis = -> Sketch028 [N_Axis]
  Type = 0
FEATURE [Sketcher::SketchObject] Sketch029
  AttachmentOffset = pos=(0,0,5) rot=(0,0,1;0rad)
  FullyConstrained = true
  MapMode = 5
  Placement = pos=(0,0,5) rot=(0,0,1;0rad)
  Support = -> [XY_Plane201]
  expr: Constraints[10] = Spreadsheet.u * 3 + 1
  expr: Constraints[12] = Spreadsheet.u
  expr: Constraints[15] = Spreadsheet.u
  expr: Constraints[2] = Spreadsheet.u * 15 + 1
  expr: Constraints[3] = Spreadsheet.u * 2 - 0.5
  expr: Constraints[4] = Spreadsheet.PCB_width - Spreadsheet.u * 5.25 - 0.5
  expr: Constraints[53] = Spreadsheet.key_fillet
  expr: Constraints[6] = Spreadsheet.u * 5 + 1
  expr: Constraints[8] = Spreadsheet.u * (1.25 * 3 + 6.25 + 1 * 3) + 1
  sketch-geometry (25):
    g0: LineSegment StartX=39.1 StartY=-38.4875 StartZ=0 EndX=322.85 EndY=-38.4875 EndZ=0
    g1: GeomPoint X=180.975 Y=-38.4875 Z=0
    g2: LineSegment StartX=37.6 StartY=-39.9875 StartZ=0 EndX=37.6 EndY=-133.238 EndZ=0
    g3: LineSegment StartX=39.1 StartY=-134.737 StartZ=0 EndX=284.75 EndY=-134.737 EndZ=0
    g4: LineSegment StartX=324.35 StartY=-39.9875 StartZ=0 EndX=324.35 EndY=-95.1375 EndZ=0
    g5: LineSegment StartX=286.25 StartY=-133.237 StartZ=0 EndX=286.25 EndY=-117.188 EndZ=0
    g6: LineSegment StartX=322.85 StartY=-96.6375 StartZ=0 EndX=306.8 EndY=-96.6375 EndZ=0
    g7: LineSegment StartX=287.75 StartY=-115.688 StartZ=0 EndX=303.8 EndY=-115.688 EndZ=0
    g8: LineSegment StartX=305.3 StartY=-98.1375 StartZ=0 EndX=305.3 EndY=-114.188 EndZ=0
    g9: ArcOfCircle CenterX=39.1 CenterY=-39.9875 CenterZ=0 NormalX=0 NormalY=0 NormalZ=1 AngleXU=0 Radius=1.5 StartAngle=1.5708 EndAngle=3.14159
    g10: GeomPoint X=37.6 Y=-38.4875 Z=0
    g11: ArcOfCircle CenterX=39.1 CenterY=-133.238 CenterZ=0 NormalX=0 NormalY=0 NormalZ=1 AngleXU=0 Radius=1.5 StartAngle=3.14159 EndAngle=4.71239
    g12: GeomPoint X=37.6 Y=-134.738 Z=0
    g13: ArcOfCircle CenterX=284.75 CenterY=-133.237 CenterZ=0 NormalX=0 NormalY=0 NormalZ=1 AngleXU=0 Radius=1.5 StartAngle=4.71239 EndAngle=6.28319
    g14: GeomPoint X=286.25 Y=-134.738 Z=0
    g15: ArcOfCircle CenterX=287.75 CenterY=-117.188 CenterZ=0 NormalX=0 NormalY=0 NormalZ=1 AngleXU=0 Radius=1.5 StartAngle=1.5708 EndAngle=3.14159
    g16: GeomPoint X=286.25 Y=-115.688 Z=0
    g17: ArcOfCircle CenterX=303.8 CenterY=-114.188 CenterZ=0 NormalX=0 NormalY=0 NormalZ=1 AngleXU=0 Radius=1.5 StartAngle=4.71239 EndAngle=6.28319
    g18: GeomPoint X=305.3 Y=-115.688 Z=0
    g19: ArcOfCircle CenterX=306.8 CenterY=-98.1375 CenterZ=0 NormalX=0 NormalY=0 NormalZ=1 AngleXU=0 Radius=1.5 StartAngle=1.5708 EndAngle=3.14159
    g20: GeomPoint X=305.3 Y=-96.6375 Z=0
    g21: ArcOfCircle CenterX=322.85 CenterY=-95.1375 CenterZ=0 NormalX=0 NormalY=0 NormalZ=1 AngleXU=0 Radius=1.5 StartAngle=4.71239 EndAngle=6.28319
    g22: GeomPoint X=324.35 Y=-96.6375 Z=0
    g23: ArcOfCircle CenterX=322.85 CenterY=-39.9875 CenterZ=0 NormalX=0 NormalY=0 NormalZ=1 AngleXU=0 Radius=1.5 StartAngle=9e-16 EndAngle=1.5708
    g24: GeomPoint X=324.35 Y=-38.4875 Z=0
  constraints (57):
    c: Horizontal(g0)
    c: Symmetric(g10,g24,g1)
    c: DistanceX(g10,g24) = 286.75
    c: DistanceX(g-1,g10) = 37.6
    c: DistanceY(g10,g-1) = 38.4875
    c: Vertical(g2)
    c: DistanceY(g12,g10) = 96.25
    c: Horizontal(g3)
    c: DistanceX(g12,g14) = 248.65
    c: Vertical(g4)
    c: DistanceY(g22,g24) = 58.15
    c: Vertical(g5)
    c: DistanceY(g14,g16) = 19.05
    c: Horizontal(g6)
    c: Horizontal(g7)
    c: DistanceX(g20,g22) = 19.05
    c: Vertical(g8)
    c: PointOnObject(g10,g0)
    c: PointOnObject(g10,g2)
    c: Tangent(g0,g9) = 1.5708
    c: Tangent(g2,g9) = -1.5708
    c: PointOnObject(g12,g2)
    c: PointOnObject(g12,g3)
    c: Tangent(g2,g11) = -1.5708
    c: Tangent(g3,g11) = -1.5708
    c: PointOnObject(g14,g3)
    c: PointOnObject(g14,g5)
    c: Tangent(g3,g13) = -1.5708
    c: Tangent(g5,g13) = -1.5708
    c: PointOnObject(g16,g5)
    c: PointOnObject(g16,g7)
    c: Tangent(g5,g15) = 1.5708
    c: Tangent(g7,g15) = 1.5708
    c: PointOnObject(g18,g7)
    c: PointOnObject(g18,g8)
    c: Tangent(g7,g17) = -1.5708
    c: Tangent(g8,g17) = 1.5708
    c: PointOnObject(g20,g6)
    c: PointOnObject(g20,g8)
    c: Tangent(g6,g19) = -1.5708
    c: Tangent(g8,g19) = -1.5708
    c: PointOnObject(g22,g4)
    c: PointOnObject(g22,g6)
    c: Tangent(g4,g21) = 1.5708
    c: Tangent(g6,g21) = 1.5708
    c: PointOnObject(g24,g0)
    c: PointOnObject(g24,g4)
    c: Tangent(g0,g23) = 1.5708
    c: Tangent(g4,g23) = 1.5708
    c: Equal(g17,g19)
    c: Equal(g19,g21)
    c: Equal(g23,g9)
    c: Equal(g11,g9)
    c: Radius(g9) = 1.5
    c: Equal(g23,g21)
    c: Equal(g15,g17)
    c: Equal(g15,g13)
FEATURE [PartDesign::Pocket] Pocket022  label="alpha001"
  BaseFeature = -> Pocket021
  Direction = (0,0,-1)
  Length = 5
  Length2 = 5
  Profile = -> Sketch029
  ReferenceAxis = -> Sketch029 [N_Axis]
  Type = 0
FEATURE [Sketcher::SketchObject] Sketch030
  AttachmentOffset = pos=(0,0,5) rot=(0,0,1;0rad)
  FullyConstrained = true
  MapMode = 5
  Placement = pos=(0,0,5) rot=(0,0,1;0rad)
  Support = -> [XY_Plane201]
  expr: Constraints[28] = Spreadsheet.key_fillet
  expr: Constraints[5] = Spreadsheet.u * 4 + 1
  expr: Constraints[6] = Spreadsheet.u + 1
  expr: Constraints[7] = Spreadsheet.u * (0.5 + 17 + 0.5)
  expr: Constraints[8] = Spreadsheet.PCB_width - Spreadsheet.u * (1 + 0.25 + 2)
  sketch-geometry (13):
    g0: LineSegment StartX=332.875 StartY=-39.9875 StartZ=0 EndX=332.875 EndY=-114.187 EndZ=0
    g1: LineSegment StartX=334.375 StartY=-115.687 StartZ=0 EndX=351.425 EndY=-115.687 EndZ=0
    g2: LineSegment StartX=352.925 StartY=-114.187 StartZ=0 EndX=352.925 EndY=-39.9875 EndZ=0
    g3: LineSegment StartX=351.425 StartY=-38.4875 StartZ=0 EndX=334.375 EndY=-38.4875 EndZ=0
    g4: GeomPoint X=342.9 Y=-77.0875 Z=0
    g5: ArcOfCircle CenterX=334.375 CenterY=-39.9875 CenterZ=0 NormalX=0 NormalY=0 NormalZ=1 AngleXU=0 Radius=1.5 StartAngle=1.5708 EndAngle=3.14159
    g6: GeomPoint X=332.875 Y=-38.4875 Z=0
    g7: ArcOfCircle CenterX=334.375 CenterY=-114.187 CenterZ=0 NormalX=0 NormalY=0 NormalZ=1 AngleXU=0 Radius=1.5 StartAngle=3.14159 EndAngle=4.71239
    g8: GeomPoint X=332.875 Y=-115.687 Z=0
    g9: ArcOfCircle CenterX=351.425 CenterY=-114.187 CenterZ=0 NormalX=0 NormalY=0 NormalZ=1 AngleXU=0 Radius=1.5 StartAngle=4.71239 EndAngle=6.28319
    g10: GeomPoint X=352.925 Y=-115.688 Z=0
    g11: ArcOfCircle CenterX=351.425 CenterY=-39.9875 CenterZ=0 NormalX=0 NormalY=0 NormalZ=1 AngleXU=0 Radius=1.5 StartAngle=2e-16 EndAngle=1.5708
    g12: GeomPoint X=352.925 Y=-38.4875 Z=0
  constraints (29):
    c: Horizontal(g1)
    c: Horizontal(g3)
    c: Vertical(g0)
    c: Vertical(g2)
    c: Symmetric(g10,g6,g4)
    c: DistanceY(g10,g12) = 77.2
    c: DistanceX(g6,g12) = 20.05
    c: DistanceX(g-1,g4) = 342.9
    c: DistanceY(g4,g-1) = 77.0875
    c: PointOnObject(g6,g0)
    c: PointOnObject(g6,g3)
    c: Tangent(g0,g5) = -1.5708
    c: Tangent(g3,g5) = -1.5708
    c: PointOnObject(g8,g0)
    c: PointOnObject(g8,g1)
    c: Tangent(g0,g7) = -1.5708
    c: Tangent(g1,g7) = -1.5708
    c: PointOnObject(g10,g1)
    c: PointOnObject(g10,g2)
    c: Tangent(g1,g9) = -1.5708
    c: Tangent(g2,g9) = -1.5708
    c: PointOnObject(g12,g2)
    c: PointOnObject(g12,g3)
    c: Tangent(g2,g11) = -1.5708
    c: Tangent(g3,g11) = -1.5708
    c: Equal(g7,g9)
    c: Equal(g11,g9)
    c: Equal(g11,g5)
    c: Radius(g5) = 1.5
FEATURE [PartDesign::Pocket] Pocket023  label="right thiny001"
  BaseFeature = -> Pocket022
  Direction = (0,0,-1)
  Length = 5
  Length2 = 5
  Profile = -> Sketch030
  ReferenceAxis = -> Sketch030 [N_Axis]
  Type = 0
FEATURE [Sketcher::SketchObject] Sketch031
  AttachmentOffset = pos=(0,0,5) rot=(0,0,1;0rad)
  FullyConstrained = true
  MapMode = 5
  Placement = pos=(0,0,5) rot=(0,0,1;0rad)
  Support = -> [XY_Plane201]
  expr: Constraints[12] = Spreadsheet.u
  expr: Constraints[13] = Spreadsheet.u + 1
  expr: Constraints[1] = Spreadsheet.u * 3 + 1
  expr: Constraints[2] = Spreadsheet.u * (15 + 0.25) - 0.5
  expr: Constraints[3] = Spreadsheet.PCB_width + 0.5
  expr: Constraints[54] = Spreadsheet.key_fillet
  expr: Constraints[55] = Spreadsheet.u + 1
  expr: Constraints[6] = Spreadsheet.u + 1
  expr: Constraints[7] = Spreadsheet.u
  sketch-geometry (24):
    g0: LineSegment StartX=291.513 StartY=-139.5 StartZ=0 EndX=346.663 EndY=-139.5 EndZ=0
    g1: LineSegment StartX=290.013 StartY=-138 StartZ=0 EndX=290.013 EndY=-120.95 EndZ=0
    g2: LineSegment StartX=291.513 StartY=-119.45 StartZ=0 EndX=307.563 EndY=-119.45 EndZ=0
    g3: LineSegment StartX=309.063 StartY=-117.95 StartZ=0 EndX=309.063 EndY=-101.9 EndZ=0
    g4: LineSegment StartX=310.563 StartY=-100.4 StartZ=0 EndX=327.612 EndY=-100.4 EndZ=0
    g5: LineSegment StartX=329.112 StartY=-101.9 StartZ=0 EndX=329.112 EndY=-117.95 EndZ=0
    g6: LineSegment StartX=330.612 StartY=-119.45 StartZ=0 EndX=346.663 EndY=-119.45 EndZ=0
    g7: LineSegment StartX=348.163 StartY=-138 StartZ=0 EndX=348.163 EndY=-120.95 EndZ=0
    g8: ArcOfCircle CenterX=310.563 CenterY=-101.9 CenterZ=0 NormalX=0 NormalY=0 NormalZ=1 AngleXU=0 Radius=1.5 StartAngle=1.5708 EndAngle=3.14159
    g9: GeomPoint X=309.062 Y=-100.4 Z=0
    g10: ArcOfCircle CenterX=307.563 CenterY=-117.95 CenterZ=0 NormalX=0 NormalY=0 NormalZ=1 AngleXU=0 Radius=1.5 StartAngle=4.71239 EndAngle=6.28319
    g11: GeomPoint X=309.062 Y=-119.45 Z=0
    g12: ArcOfCircle CenterX=291.513 CenterY=-120.95 CenterZ=0 NormalX=0 NormalY=0 NormalZ=1 AngleXU=0 Radius=1.5 StartAngle=1.5708 EndAngle=3.14159
    g13: GeomPoint X=290.012 Y=-119.45 Z=0
    g14: ArcOfCircle CenterX=291.513 CenterY=-138 CenterZ=0 NormalX=0 NormalY=0 NormalZ=1 AngleXU=0 Radius=1.5 StartAngle=3.14159 EndAngle=4.71239
    g15: GeomPoint X=290.012 Y=-139.5 Z=0
    g16: ArcOfCircle CenterX=346.663 CenterY=-138 CenterZ=0 NormalX=0 NormalY=0 NormalZ=1 AngleXU=0 Radius=1.5 StartAngle=4.71239 EndAngle=6.28319
    g17: GeomPoint X=348.163 Y=-139.5 Z=0
    g18: ArcOfCircle CenterX=346.663 CenterY=-120.95 CenterZ=0 NormalX=0 NormalY=0 NormalZ=1 AngleXU=0 Radius=1.5 StartAngle=-2.7e-15 EndAngle=1.5708
    g19: GeomPoint X=348.162 Y=-119.45 Z=0
    g20: ArcOfCircle CenterX=330.612 CenterY=-117.95 CenterZ=0 NormalX=0 NormalY=0 NormalZ=1 AngleXU=0 Radius=1.5 StartAngle=3.14159 EndAngle=4.71239
    g21: GeomPoint X=329.112 Y=-119.45 Z=0
    g22: ArcOfCircle CenterX=327.612 CenterY=-101.9 CenterZ=0 NormalX=0 NormalY=0 NormalZ=1 AngleXU=0 Radius=1.5 StartAngle=2e-16 EndAngle=1.5708
    g23: GeomPoint X=329.112 Y=-100.4 Z=0
  constraints (56):
    c: Horizontal(g0)
    c: DistanceX(g15,g17) = 58.15
    c: DistanceX(g-1,g15) = 290.012
    c: DistanceY(g15,g-1) = 139.5
    c: Vertical(g1)
    c: Horizontal(g2)
    c: DistanceY(g15,g13) = 20.05
    c: DistanceX(g13,g11) = 19.05
    c: Vertical(g3)
    c: Horizontal(g4)
    c: Vertical(g5)
    c: Horizontal(g6)
    c: DistanceY(g11,g9) = 19.05
    c: DistanceX(g9,g23) = 20.05
    c: Vertical(g7)
    c: PointOnObject(g9,g3)
    c: PointOnObject(g9,g4)
    c: Tangent(g3,g8) = 1.5708
    c: Tangent(g4,g8) = 1.5708
    c: PointOnObject(g11,g2)
    c: PointOnObject(g11,g3)
    c: Tangent(g2,g10) = -1.5708
    c: Tangent(g3,g10) = -1.5708
    c: PointOnObject(g13,g1)
    c: PointOnObject(g13,g2)
    c: Tangent(g1,g12) = 1.5708
    c: Tangent(g2,g12) = 1.5708
    c: PointOnObject(g15,g0)
    c: PointOnObject(g15,g1)
    c: Tangent(g0,g14) = -1.5708
    c: Tangent(g1,g14) = 1.5708
    c: PointOnObject(g17,g0)
    c: PointOnObject(g17,g7)
    c: Tangent(g0,g16) = -1.5708
    c: Tangent(g7,g16) = -1.5708
    c: PointOnObject(g19,g6)
    c: PointOnObject(g19,g7)
    c: Tangent(g6,g18) = 1.5708
    c: Tangent(g7,g18) = -1.5708
    c: PointOnObject(g21,g5)
    c: PointOnObject(g21,g6)
    c: Tangent(g5,g20) = -1.5708
    c: Tangent(g6,g20) = -1.5708
    c: PointOnObject(g23,g4)
    c: PointOnObject(g23,g5)
    c: Tangent(g4,g22) = 1.5708
    c: Tangent(g5,g22) = 1.5708
    c: Equal(g22,g8)
    c: Equal(g20,g22)
    c: Equal(g18,g20)
    c: Equal(g16,g18)
    c: Equal(g14,g16)
    c: Equal(g12,g14)
    c: Equal(g10,g12)
    c: Radius(g8) = 1.5
    c: DistanceY(g17,g19) = 20.05
FEATURE [PartDesign::Pocket] Pocket024  label="arrow keys001"
  BaseFeature = -> Pocket023
  Direction = (0,0,-1)
  Length = 5
  Length2 = 5
  Profile = -> Sketch031
  ReferenceAxis = -> Sketch031 [N_Axis]
  Type = 0
FEATURE [Sketcher::SketchObject] Sketch033
  AttachmentOffset = pos=(0,0,5) rot=(0,0,1;0rad)
  FullyConstrained = false
  MapMode = 5
  Placement = pos=(0,0,5) rot=(0,0,1;0rad)
  Support = -> [XY_Plane199]
  expr: Constraints[2] = Spreadsheet.PCB_width - Spreadsheet.u * 6.5 - 0.5
  sketch-geometry (121):
    g0: LineSegment StartX=5.32294 StartY=-5.97815 StartZ=0 EndX=5.32294 EndY=-10.8375 EndZ=0
    g1: LineSegment StartX=6.82294 StartY=-12.3375 StartZ=0 EndX=11.6459 EndY=-12.3375 EndZ=0
    g2: LineSegment StartX=7.88758 StartY=-4.92149 StartZ=0 EndX=12.7105 EndY=-9.78083 EndZ=0
    g3: GeomPoint X=32.164 Y=-14.675 Z=0
    g4: LineSegment StartX=13.1519 StartY=-2.3375 StartZ=0 EndX=24.5372 EndY=-2.3375 EndZ=0
    g5: LineSegment StartX=26.0372 StartY=-3.8375 StartZ=0 EndX=26.0372 EndY=-10.8375 EndZ=0
    g6: LineSegment StartX=24.5372 StartY=-12.3375 StartZ=0 EndX=20.0995 EndY=-12.3375 EndZ=0
    g7: LineSegment StartX=19.0348 StartY=-11.8942 StartZ=0 EndX=12.0873 EndY=-4.89417 EndZ=0
    g8: ArcOfCircle CenterX=31.0372 CenterY=-4.3375 CenterZ=0 NormalX=0 NormalY=0 NormalZ=1 AngleXU=0 Radius=2 StartAngle=1.5708 EndAngle=4.71239
    g9: ArcOfCircle CenterX=84.5811 CenterY=-4.3375 CenterZ=0 NormalX=0 NormalY=0 NormalZ=1 AngleXU=0 Radius=2 StartAngle=4.71239 EndAngle=7.85398
    g10: LineSegment StartX=31.0372 StartY=-6.3375 StartZ=0 EndX=84.5811 EndY=-6.3375 EndZ=0
    g11: LineSegment StartX=84.5811 StartY=-2.3375 StartZ=0 EndX=31.0372 EndY=-2.3375 EndZ=0
    g12: ArcOfCircle CenterX=31.0372 CenterY=-10.3375 CenterZ=0 NormalX=0 NormalY=0 NormalZ=1 AngleXU=0 Radius=2 StartAngle=1.5708 EndAngle=4.71239
    g13: ArcOfCircle CenterX=84.5811 CenterY=-10.3375 CenterZ=0 NormalX=0 NormalY=0 NormalZ=1 AngleXU=0 Radius=2 StartAngle=4.71239 EndAngle=7.85398
    g14: LineSegment StartX=31.0372 StartY=-12.3375 StartZ=0 EndX=84.5811 EndY=-12.3375 EndZ=0
    g15: LineSegment StartX=84.5811 StartY=-8.3375 StartZ=0 EndX=31.0372 EndY=-8.3375 EndZ=0
    g16: LineSegment StartX=89.5811 StartY=-3.8375 StartZ=0 EndX=89.5811 EndY=-9.9323 EndZ=0
    g17: LineSegment StartX=91.741 StartY=-11.2793 StartZ=0 EndX=104.182 EndY=-5.18453 EndZ=0
    g18: LineSegment StartX=103.522 StartY=-2.3375 StartZ=0 EndX=91.0811 EndY=-2.3375 EndZ=0
    g19: LineSegment StartX=99.9384 StartY=-9.49047 StartZ=0 EndX=112.379 EndY=-3.39567 EndZ=0
    g20: LineSegment StartX=114.539 StartY=-4.7427 StartZ=0 EndX=114.539 EndY=-10.8375 EndZ=0
    g21: LineSegment StartX=113.039 StartY=-12.3375 StartZ=0 EndX=100.598 EndY=-12.3375 EndZ=0
    g22: LineSegment StartX=117.539 StartY=-3.8375 StartZ=0 EndX=117.539 EndY=-9.79847 EndZ=0
    g23: LineSegment StartX=119.763 StartY=-11.1123 StartZ=0 EndX=130.582 EndY=-5.15129 EndZ=0
    g24: LineSegment StartX=129.858 StartY=-2.3375 StartZ=0 EndX=119.039 EndY=-2.3375 EndZ=0
    g25: LineSegment StartX=126.791 StartY=-9.52371 StartZ=0 EndX=137.61 EndY=-3.56273 EndZ=0
    g26: LineSegment StartX=139.834 StartY=-4.87653 StartZ=0 EndX=139.834 EndY=-10.8375 EndZ=0
    g27: LineSegment StartX=138.334 StartY=-12.3375 StartZ=0 EndX=127.515 EndY=-12.3375 EndZ=0
    g28: LineSegment StartX=142.834 StartY=-3.8375 StartZ=0 EndX=142.834 EndY=-9.90411 EndZ=0
    g29: LineSegment StartX=145.008 StartY=-11.2442 StartZ=0 EndX=157.071 EndY=-5.17757 EndZ=0
    g30: LineSegment StartX=156.397 StartY=-2.3375 StartZ=0 EndX=144.334 EndY=-2.3375 EndZ=0
    g31: LineSegment StartX=152.932 StartY=-9.49743 StartZ=0 EndX=164.995 EndY=-3.43082 EndZ=0
    g32: LineSegment StartX=167.169 StartY=-4.77089 StartZ=0 EndX=167.169 EndY=-10.8375 EndZ=0
    g33: LineSegment StartX=165.669 StartY=-12.3375 StartZ=0 EndX=153.606 EndY=-12.3375 EndZ=0
    g34: ArcOfCircle CenterX=172.169 CenterY=-3.3375 CenterZ=0 NormalX=0 NormalY=0 NormalZ=1 AngleXU=0 Radius=1 StartAngle=1.5708 EndAngle=4.71239
    g35: ArcOfCircle CenterX=243.856 CenterY=-3.3375 CenterZ=0 NormalX=0 NormalY=0 NormalZ=1 AngleXU=0 Radius=1 StartAngle=4.71239 EndAngle=7.85398
    g36: LineSegment StartX=172.169 StartY=-4.3375 StartZ=0 EndX=243.856 EndY=-4.3375 EndZ=0
    g37: LineSegment StartX=243.856 StartY=-2.3375 StartZ=0 EndX=172.169 EndY=-2.3375 EndZ=0
    g38: ArcOfCircle CenterX=172.169 CenterY=-7.3375 CenterZ=0 NormalX=0 NormalY=0 NormalZ=1 AngleXU=0 Radius=1 StartAngle=1.5708 EndAngle=4.71239
    g39: ArcOfCircle CenterX=243.856 CenterY=-7.3375 CenterZ=0 NormalX=0 NormalY=0 NormalZ=1 AngleXU=0 Radius=1 StartAngle=4.71239 EndAngle=7.85398
    g40: LineSegment StartX=172.169 StartY=-8.3375 StartZ=0 EndX=243.856 EndY=-8.3375 EndZ=0
    g41: LineSegment StartX=243.856 StartY=-6.3375 StartZ=0 EndX=172.169 EndY=-6.3375 EndZ=0
    g42: ArcOfCircle CenterX=172.169 CenterY=-11.3375 CenterZ=0 NormalX=0 NormalY=0 NormalZ=1 AngleXU=0 Radius=1 StartAngle=1.5708 EndAngle=4.71239
    g43: ArcOfCircle CenterX=243.856 CenterY=-11.3375 CenterZ=0 NormalX=0 NormalY=0 NormalZ=1 AngleXU=0 Radius=1 StartAngle=4.71239 EndAngle=7.85398
    g44: LineSegment StartX=172.169 StartY=-12.3375 StartZ=0 EndX=243.856 EndY=-12.3375 EndZ=0
    g45: LineSegment StartX=243.856 StartY=-10.3375 StartZ=0 EndX=172.169 EndY=-10.3375 EndZ=0
    g46: LineSegment StartX=248.856 StartY=-3.8375 StartZ=0 EndX=248.856 EndY=-10.8375 EndZ=0
    g47: LineSegment StartX=250.356 StartY=-12.3375 StartZ=0 EndX=265.179 EndY=-12.3375 EndZ=0
    g48: LineSegment StartX=266.679 StartY=-10.8375 StartZ=0 EndX=266.679 EndY=-3.8375 EndZ=0
    g49: LineSegment StartX=265.179 StartY=-2.3375 StartZ=0 EndX=250.356 EndY=-2.3375 EndZ=0
    g50: GeomPoint X=257.767 Y=-7.3375 Z=0
    g51: ArcOfCircle CenterX=265.179 CenterY=-3.8375 CenterZ=0 NormalX=0 NormalY=0 NormalZ=1 AngleXU=0 Radius=1.5 StartAngle=1e-16 EndAngle=1.5708
    g52: GeomPoint X=266.679 Y=-2.3375 Z=0
    g53: ArcOfCircle CenterX=265.179 CenterY=-10.8375 CenterZ=0 NormalX=0 NormalY=0 NormalZ=1 AngleXU=0 Radius=1.5 StartAngle=4.71239 EndAngle=6.28319
    g54: GeomPoint X=266.679 Y=-12.3375 Z=0
    g55: ArcOfCircle CenterX=250.356 CenterY=-10.8375 CenterZ=0 NormalX=0 NormalY=0 NormalZ=1 AngleXU=0 Radius=1.5 StartAngle=3.14159 EndAngle=4.71239
    g56: GeomPoint X=248.856 Y=-12.3375 Z=0
    g57: ArcOfCircle CenterX=250.356 CenterY=-3.8375 CenterZ=0 NormalX=0 NormalY=0 NormalZ=1 AngleXU=0 Radius=1.5 StartAngle=1.5708 EndAngle=3.14159
    g58: GeomPoint X=248.856 Y=-2.3375 Z=0
    g59: ArcOfCircle CenterX=271.679 CenterY=-3.3375 CenterZ=0 NormalX=0 NormalY=0 NormalZ=1 AngleXU=0 Radius=1 StartAngle=1.5708 EndAngle=4.71239
    g60: ArcOfCircle CenterX=347.146 CenterY=-3.3375 CenterZ=0 NormalX=0 NormalY=0 NormalZ=1 AngleXU=0 Radius=1 StartAngle=4.71239 EndAngle=7.85398
    g61: LineSegment StartX=271.679 StartY=-4.3375 StartZ=0 EndX=347.146 EndY=-4.3375 EndZ=0
    g62: LineSegment StartX=347.146 StartY=-2.3375 StartZ=0 EndX=271.679 EndY=-2.3375 EndZ=0
    g63: ArcOfCircle CenterX=271.679 CenterY=-7.3375 CenterZ=0 NormalX=0 NormalY=0 NormalZ=1 AngleXU=0 Radius=1 StartAngle=1.5708 EndAngle=4.71239
    g64: ArcOfCircle CenterX=347.146 CenterY=-7.3375 CenterZ=0 NormalX=0 NormalY=0 NormalZ=1 AngleXU=0 Radius=1 StartAngle=4.71239 EndAngle=7.85398
    g65: LineSegment StartX=271.679 StartY=-8.3375 StartZ=0 EndX=347.146 EndY=-8.3375 EndZ=0
    g66: LineSegment StartX=347.146 StartY=-6.3375 StartZ=0 EndX=271.679 EndY=-6.3375 EndZ=0
    g67: ArcOfCircle CenterX=271.679 CenterY=-11.3375 CenterZ=0 NormalX=0 NormalY=0 NormalZ=1 AngleXU=0 Radius=1 StartAngle=1.5708 EndAngle=4.71239
    g68: ArcOfCircle CenterX=347.146 CenterY=-11.3375 CenterZ=0 NormalX=0 NormalY=0 NormalZ=1 AngleXU=0 Radius=1 StartAngle=4.71239 EndAngle=7.85398
    g69: LineSegment StartX=271.679 StartY=-12.3375 StartZ=0 EndX=347.146 EndY=-12.3375 EndZ=0
    g70: LineSegment StartX=347.146 StartY=-10.3375 StartZ=0 EndX=271.679 EndY=-10.3375 EndZ=0
    g71: ArcOfCircle CenterX=11.6459 CenterY=-10.8375 CenterZ=0 NormalX=0 NormalY=0 NormalZ=1 AngleXU=0 Radius=1.5 StartAngle=4.71239 EndAngle=7.06483
    g72: GeomPoint X=15.2481 Y=-12.3375 Z=0
    g73: ArcOfCircle CenterX=6.82294 CenterY=-5.97815 CenterZ=0 NormalX=0 NormalY=0 NormalZ=1 AngleXU=0 Radius=1.5 StartAngle=0.78164 EndAngle=3.14159
    g74: GeomPoint X=5.32294 Y=-2.3375 Z=0
    g75: ArcOfCircle CenterX=6.82294 CenterY=-10.8375 CenterZ=0 NormalX=0 NormalY=0 NormalZ=1 AngleXU=0 Radius=1.5 StartAngle=3.14159 EndAngle=4.71239
    g76: GeomPoint X=5.32294 Y=-12.3375 Z=0
    g77: ArcOfCircle CenterX=13.1519 CenterY=-3.8375 CenterZ=0 NormalX=0 NormalY=0 NormalZ=1 AngleXU=0 Radius=1.5 StartAngle=1.5708 EndAngle=3.92323
    g78: GeomPoint X=9.54973 Y=-2.3375 Z=0
    g79: ArcOfCircle CenterX=20.0995 CenterY=-10.8375 CenterZ=0 NormalX=0 NormalY=0 NormalZ=1 AngleXU=0 Radius=1.5 StartAngle=3.92323 EndAngle=4.71239
    g80: GeomPoint X=19.4749 Y=-12.3375 Z=0
    g81: ArcOfCircle CenterX=24.5372 CenterY=-10.8375 CenterZ=0 NormalX=0 NormalY=0 NormalZ=1 AngleXU=0 Radius=1.5 StartAngle=4.71239 EndAngle=6.28319
    g82: GeomPoint X=26.0372 Y=-12.3375 Z=0
    g83: ArcOfCircle CenterX=24.5372 CenterY=-3.8375 CenterZ=0 NormalX=0 NormalY=0 NormalZ=1 AngleXU=0 Radius=1.5 StartAngle=0 EndAngle=1.5708
    g84: GeomPoint X=26.0372 Y=-2.3375 Z=0
    g85: ArcOfCircle CenterX=91.0811 CenterY=-9.9323 CenterZ=0 NormalX=0 NormalY=0 NormalZ=1 AngleXU=0 Radius=1.5 StartAngle=3.14159 EndAngle=5.16793
    g86: GeomPoint X=89.5811 Y=-12.3375 Z=0
    g87: ArcOfCircle CenterX=100.598 CenterY=-10.8375 CenterZ=0 NormalX=0 NormalY=0 NormalZ=1 AngleXU=0 Radius=1.5 StartAngle=2.02634 EndAngle=4.71239
    g88: GeomPoint X=94.1271 Y=-12.3375 Z=0
    g89: ArcOfCircle CenterX=103.522 CenterY=-3.8375 CenterZ=0 NormalX=0 NormalY=0 NormalZ=1 AngleXU=0 Radius=1.5 StartAngle=5.16793 EndAngle=7.85398
    g90: GeomPoint X=109.993 Y=-2.3375 Z=0
    g91: ArcOfCircle CenterX=113.039 CenterY=-4.7427 CenterZ=0 NormalX=0 NormalY=0 NormalZ=1 AngleXU=0 Radius=1.5 StartAngle=0 EndAngle=2.02634
    g92: GeomPoint X=114.539 Y=-2.3375 Z=0
    g93: ArcOfCircle CenterX=113.039 CenterY=-10.8375 CenterZ=0 NormalX=0 NormalY=0 NormalZ=1 AngleXU=0 Radius=1.5 StartAngle=4.71239 EndAngle=6.28319
    g94: GeomPoint X=114.539 Y=-12.3375 Z=0
    g95: ArcOfCircle CenterX=91.0811 CenterY=-3.8375 CenterZ=0 NormalX=0 NormalY=0 NormalZ=1 AngleXU=0 Radius=1.5 StartAngle=1.5708 EndAngle=3.14159
    g96: GeomPoint X=89.5811 Y=-2.3375 Z=0
    g97: ArcOfCircle CenterX=119.039 CenterY=-3.8375 CenterZ=0 NormalX=0 NormalY=0 NormalZ=1 AngleXU=0 Radius=1.5 StartAngle=1.5708 EndAngle=3.14159
    g98: GeomPoint X=117.539 Y=-2.3375 Z=0
    g99: ArcOfCircle CenterX=119.039 CenterY=-9.79847 CenterZ=0 NormalX=0 NormalY=0 NormalZ=1 AngleXU=0 Radius=1.5 StartAngle=3.14159 EndAngle=5.21596
    g100: GeomPoint X=117.539 Y=-12.3375 Z=0
    g101: ArcOfCircle CenterX=127.515 CenterY=-10.8375 CenterZ=0 NormalX=0 NormalY=0 NormalZ=1 AngleXU=0 Radius=1.5 StartAngle=2.07437 EndAngle=4.71239
    g102: GeomPoint X=121.684 Y=-12.3375 Z=0
    g103: ArcOfCircle CenterX=129.858 CenterY=-3.8375 CenterZ=0 NormalX=0 NormalY=0 NormalZ=1 AngleXU=0 Radius=1.5 StartAngle=5.21596 EndAngle=7.85398
    g104: GeomPoint X=135.689 Y=-2.3375 Z=0
    g105: ArcOfCircle CenterX=138.334 CenterY=-4.87653 CenterZ=0 NormalX=0 NormalY=0 NormalZ=1 AngleXU=0 Radius=1.5 StartAngle=0 EndAngle=2.07437
    g106: GeomPoint X=139.834 Y=-2.3375 Z=0
    g107: ArcOfCircle CenterX=138.334 CenterY=-10.8375 CenterZ=0 NormalX=0 NormalY=0 NormalZ=1 AngleXU=0 Radius=1.5 StartAngle=4.71239 EndAngle=6.28319
    g108: GeomPoint X=139.834 Y=-12.3375 Z=0
    g109: ArcOfCircle CenterX=144.334 CenterY=-9.90411 CenterZ=0 NormalX=0 NormalY=0 NormalZ=1 AngleXU=0 Radius=1.5 StartAngle=3.14159 EndAngle=5.17837
    g110: GeomPoint X=142.834 Y=-12.3375 Z=0
    g111: ArcOfCircle CenterX=144.334 CenterY=-3.8375 CenterZ=0 NormalX=0 NormalY=0 NormalZ=1 AngleXU=0 Radius=1.5 StartAngle=1.5708 EndAngle=3.14159
    g112: GeomPoint X=142.834 Y=-2.3375 Z=0
    g113: ArcOfCircle CenterX=156.397 CenterY=-3.8375 CenterZ=0 NormalX=0 NormalY=0 NormalZ=1 AngleXU=0 Radius=1.5 StartAngle=5.17837 EndAngle=7.85398
    g114: GeomPoint X=162.718 Y=-2.3375 Z=0
    g115: ArcOfCircle CenterX=165.669 CenterY=-4.77089 CenterZ=0 NormalX=0 NormalY=0 NormalZ=1 AngleXU=0 Radius=1.5 StartAngle=0 EndAngle=2.03678
    g116: GeomPoint X=167.169 Y=-2.3375 Z=0
    g117: ArcOfCircle CenterX=165.669 CenterY=-10.8375 CenterZ=0 NormalX=0 NormalY=0 NormalZ=1 AngleXU=0 Radius=1.5 StartAngle=4.71239 EndAngle=6.28319
    g118: GeomPoint X=167.169 Y=-12.3375 Z=0
    g119: ArcOfCircle CenterX=153.606 CenterY=-10.8375 CenterZ=0 NormalX=0 NormalY=0 NormalZ=1 AngleXU=0 Radius=1.5 StartAngle=2.03678 EndAngle=4.71239
    g120: GeomPoint X=147.285 Y=-12.3375 Z=0
  constraints (277):
    c: Vertical(g0)
    c: Horizontal(g1)
    c: DistanceY(g3,g-1) = 14.675
    c: DistanceY(g76,g74) = 10
    c: DistanceY(g3,g76) = 2.3375
    c: Horizontal(g4)
    c: Vertical(g5)
    c: Horizontal(g6)
    c: Horizontal(g74,g78)
    c: Horizontal(g72,g80)
    c: DistanceX(g80,g82) = 6.56231
    c: Tangent(g8,g10) = -1.5708
    c: Tangent(g10,g9) = -1.5708
    c: Tangent(g9,g11) = -1.5708
    c: Tangent(g11,g8) = -1.5708
    c: Equal(g8,g9)
    c: Horizontal(g10)
    c: Radius(g8) = 2
    c: Horizontal(g84,g8)
    c: Tangent(g12,g14) = -1.5708
    c: Tangent(g14,g13) = -1.5708
    c: Tangent(g13,g15) = -1.5708
    c: Tangent(g15,g12) = -1.5708
    c: Equal(g12,g13)
    c: Horizontal(g14)
    c: Equal(g8,g12) = 2
    c: Vertical(g12,g8)
    c: Vertical(g13,g9)
    c: Horizontal(g12,g82)
    c: DistanceX(g84,g8) = 5
    c: Vertical(g16)
    c: Horizontal(g18)
    c: Horizontal(g96,g9)
    c: Horizontal(g86,g13)
    c: Vertical(g20)
    c: Horizontal(g21)
    c: Horizontal(g13,g88)
    c: Horizontal(g90,g92)
    c: DistanceX(g9,g96) = 5
    c: Vertical(g22)
    c: Horizontal(g24)
    c: Vertical(g26)
    c: Horizontal(g27)
    c: Horizontal(g104,g106)
    c: Vertical(g28)
    c: Horizontal(g30)
    c: Vertical(g32)
    c: Horizontal(g33)
    c: Horizontal(g114,g116)
    c: Horizontal(g98,g92)
    c: Horizontal(g102,g100)
    c: Horizontal(g120,g110)
    c: Horizontal(g112,g106)
    c: Horizontal(g110,g108)
    c: Horizontal(g100,g94)
    c: DistanceX(g92,g98) = 3
    c: DistanceX(g106,g112) = 3
    c: Tangent(g34,g36) = -1.5708
    c: Tangent(g36,g35) = -1.5708
    c: Tangent(g35,g37) = -1.5708
    c: Tangent(g37,g34) = -1.5708
    c: Equal(g34,g35)
    c: Horizontal(g36)
    c: Radius(g34) = 1
    c: Horizontal(g116,g34)
    c: Tangent(g38,g40) = -1.5708
    c: Tangent(g40,g39) = -1.5708
    c: Tangent(g39,g41) = -1.5708
    c: Tangent(g41,g38) = -1.5708
    c: Horizontal(g40)
    c: Equal(g34,g38) = 1
    c: Tangent(g42,g44) = -1.5708
    c: Tangent(g44,g43) = -1.5708
    c: Tangent(g43,g45) = -1.5708
    c: Tangent(g45,g42) = -1.5708
    c: Equal(g42,g43)
    c: Horizontal(g44)
    c: Vertical(g43,g39)
    c: Equal(g42,g38)
    c: Vertical(g38,g34)
    c: Vertical(g42,g38)
    c: Horizontal(g42,g118)
    c: Equal(g38,g39)
    c: Vertical(g39,g35)
    c: DistanceX(g116,g34) = 5
    c: DistanceY(g118,g38) = 5
    c: Horizontal(g47)
    c: Horizontal(g49)
    c: Vertical(g46)
    c: Vertical(g48)
    c: Symmetric(g54,g58,g50)
    c: DistanceY(g56,g58) = 10
    c: Horizontal(g39,g50)
    c: PointOnObject(g52,g48)
    c: PointOnObject(g52,g49)
    c: Tangent(g48,g51) = -1.5708
    c: Tangent(g49,g51) = -1.5708
    c: PointOnObject(g54,g47)
    c: PointOnObject(g54,g48)
    c: Tangent(g47,g53) = -1.5708
    c: Tangent(g48,g53) = -1.5708
    c: PointOnObject(g56,g46)
    c: PointOnObject(g56,g47)
    c: Tangent(g46,g55) = -1.5708
    c: Tangent(g47,g55) = -1.5708
    c: PointOnObject(g58,g46)
    c: PointOnObject(g58,g49)
    c: Tangent(g46,g57) = -1.5708
    c: Tangent(g49,g57) = -1.5708
    c: Equal(g55,g53)
    c: Equal(g53,g51)
    c: Equal(g51,g57)
    c: Radius(g57) = 1.5
    c: DistanceX(g35,g46) = 5
    c: Block(g49)
    c: Tangent(g59,g61) = -1.5708
    c: Tangent(g61,g60) = -1.5708
    c: Tangent(g60,g62) = -1.5708
    c: Tangent(g62,g59) = -1.5708
    c: Equal(g59,g60)
    c: Horizontal(g61)
    c: Equal(g34,g59) = 1
    c: Tangent(g63,g65) = -1.5708
    c: Tangent(g65,g64) = -1.5708
    c: Tangent(g64,g66) = -1.5708
    c: Tangent(g66,g63) = -1.5708
    c: Horizontal(g65)
    c: Equal(g59,g63) = 1
    c: Tangent(g67,g69) = -1.5708
    c: Tangent(g69,g68) = -1.5708
    c: Tangent(g68,g70) = -1.5708
    c: Tangent(g70,g67) = -1.5708
    c: Equal(g67,g68)
    c: Horizontal(g69)
    c: Vertical(g68,g64)
    c: Equal(g67,g63)
    c: Vertical(g63,g59)
    c: Vertical(g67,g63)
    c: Equal(g63,g64)
    c: Vertical(g64,g60)
    c: Horizontal(g59,g49)
    c: Horizontal(g67,g47)
    c: Horizontal(g63,g50)
    c: DistanceX(g48,g59) = 5
    c: PointOnObject(g72,g1)
    c: PointOnObject(g72,g2)
    c: Tangent(g1,g71) = -1.5708
    c: Tangent(g2,g71) = 1.5708
    c: PointOnObject(g74,g0)
    c: PointOnObject(g74,g2)
    c: Tangent(g0,g73) = -1.5708
    c: Tangent(g2,g73) = 1.5708
    c: PointOnObject(g76,g0)
    c: PointOnObject(g76,g1)
    c: Tangent(g0,g75) = -1.5708
    c: Tangent(g1,g75) = -1.5708
    c: PointOnObject(g78,g4)
    c: PointOnObject(g78,g7)
    c: Tangent(g4,g77) = 1.5708
    c: Tangent(g7,g77) = 1.5708
    c: PointOnObject(g80,g6)
    c: PointOnObject(g80,g7)
    c: Tangent(g6,g79) = 1.5708
    c: Tangent(g7,g79) = 1.5708
    c: PointOnObject(g82,g5)
    c: PointOnObject(g82,g6)
    c: Tangent(g5,g81) = 1.5708
    c: Tangent(g6,g81) = 1.5708
    c: PointOnObject(g84,g4)
    c: PointOnObject(g84,g5)
    c: Tangent(g4,g83) = 1.5708
    c: Tangent(g5,g83) = 1.5708
    c: Equal(g77,g83)
    c: Equal(g83,g81)
    c: Equal(g81,g79)
    c: Equal(g79,g71)
    c: Equal(g71,g75)
    c: Equal(g75,g73)
    c: Radius(g73) = 1.5
    c: Distance(g2,g7) = 3
    c: Parallel(g2,g7)
    c: PointOnObject(g86,g16)
    c: PointOnObject(g86,g17)
    c: Tangent(g16,g85) = -1.5708
    c: Tangent(g17,g85) = -1.5708
    c: PointOnObject(g88,g19)
    c: PointOnObject(g88,g21)
    c: Tangent(g19,g87) = 1.5708
    c: Tangent(g21,g87) = 1.5708
    c: PointOnObject(g90,g17)
    c: PointOnObject(g90,g18)
    c: Tangent(g17,g89) = -1.5708
    c: Tangent(g18,g89) = -1.5708
    c: PointOnObject(g92,g19)
    c: PointOnObject(g92,g20)
    c: Tangent(g19,g91) = 1.5708
    c: Tangent(g20,g91) = 1.5708
    c: PointOnObject(g94,g20)
    c: PointOnObject(g94,g21)
    c: Tangent(g20,g93) = 1.5708
    c: Tangent(g21,g93) = 1.5708
    c: PointOnObject(g96,g16)
    c: PointOnObject(g96,g18)
    c: Tangent(g16,g95) = -1.5708
    c: Tangent(g18,g95) = -1.5708
    c: PointOnObject(g98,g22)
    c: PointOnObject(g98,g24)
    c: Tangent(g22,g97) = -1.5708
    c: Tangent(g24,g97) = -1.5708
    c: PointOnObject(g100,g22)
    c: PointOnObject(g100,g23)
    c: Tangent(g22,g99) = -1.5708
    c: Tangent(g23,g99) = -1.5708
    c: PointOnObject(g102,g25)
    c: PointOnObject(g102,g27)
    c: Tangent(g25,g101) = 1.5708
    c: Tangent(g27,g101) = 1.5708
    c: PointOnObject(g104,g23)
    c: PointOnObject(g104,g24)
    c: Tangent(g23,g103) = -1.5708
    c: Tangent(g24,g103) = -1.5708
    c: PointOnObject(g106,g25)
    c: PointOnObject(g106,g26)
    c: Tangent(g25,g105) = 1.5708
    c: Tangent(g26,g105) = 1.5708
    c: PointOnObject(g108,g26)
    c: PointOnObject(g108,g27)
    c: Tangent(g26,g107) = 1.5708
    c: Tangent(g27,g107) = 1.5708
    c: PointOnObject(g110,g28)
    c: PointOnObject(g110,g29)
    c: Tangent(g28,g109) = -1.5708
    c: Tangent(g29,g109) = -1.5708
    c: PointOnObject(g112,g28)
    c: PointOnObject(g112,g30)
    c: Tangent(g28,g111) = -1.5708
    c: Tangent(g30,g111) = -1.5708
    c: PointOnObject(g114,g29)
    c: PointOnObject(g114,g30)
    c: Tangent(g29,g113) = -1.5708
    c: Tangent(g30,g113) = -1.5708
    c: PointOnObject(g116,g31)
    c: PointOnObject(g116,g32)
    c: Tangent(g31,g115) = 1.5708
    c: Tangent(g32,g115) = 1.5708
    c: PointOnObject(g118,g32)
    c: PointOnObject(g118,g33)
    c: Tangent(g32,g117) = 1.5708
    c: Tangent(g33,g117) = 1.5708
    c: PointOnObject(g120,g31)
    c: PointOnObject(g120,g33)
    c: Tangent(g31,g119) = 1.5708
    c: Tangent(g33,g119) = 1.5708
    c: Equal(g99,g101)
    c: Equal(g101,g105)
    c: Equal(g105,g107)
    c: Equal(g107,g109)
    c: Equal(g109,g111)
    c: Equal(g111,g113)
    c: Equal(g113,g119)
    c: Equal(g119,g117)
    c: Equal(g117,g115)
    c: Equal(g115,g103)
    c: Equal(g103,g97)
    c: Equal(g97,g91)
    c: Equal(g91,g93)
    c: Equal(g93,g87)
    c: Equal(g87,g85)
    c: Equal(g85,g89)
    c: Equal(g89,g95)
    c: Radius(g89) = 1.5
    c: Parallel(g17,g19)
    c: Parallel(g23,g25)
    c: Parallel(g29,g31)
    c: Distance(g31,g29) = 2
    c: Distance(g25,g23) = 2
    c: Distance(g19,g17) = 2
FEATURE [PartDesign::Pocket] Pocket026
  BaseFeature = -> Pocket020
  Direction = (0,0,-1)
  Length = 5
  Length2 = 5
  Profile = -> Sketch033
  ReferenceAxis = -> Sketch033 [N_Axis]
  Type = 0
FEATURE [Sketcher::SketchObject] Sketch034
  AttachmentOffset = pos=(0,0,2.9) rot=(0,0,1;0rad)
  FullyConstrained = false
  MapMode = 5
  Placement = pos=(0,0,2.9) rot=(0,0,1;0rad)
  Support = -> [XY_Plane202]
  expr: .AttachmentOffset.Base.z = 1.6 + 1.3
  expr: Constraints[24] = Spreadsheet.Screw_hole
  expr: Constraints[25] = Spreadsheet.PCB_length + Spreadsheet.pcb_to_wall_gap * 2
  expr: Constraints[27] = 2 * Spreadsheet.Top_c_rad * sin(45 / 2)
  expr: Constraints[29] = Spreadsheet.Screw_hole
  expr: Constraints[31] = 2 * Spreadsheet.Top_c_rad * sin(45 / 2)
  expr: Constraints[35] = Spreadsheet.Screw_hole
  expr: Constraints[36] = Spreadsheet.wall_thickness / 2
  expr: Constraints[37] = Spreadsheet.PCB_length / 2
  expr: Constraints[38] = (Spreadsheet.PCB_length + Spreadsheet.pcb_to_wall_gap * 2 + Spreadsheet.wall_thickness * 2) / 4
  expr: Constraints[39] = (Spreadsheet.PCB_length + Spreadsheet.pcb_to_wall_gap * 2 + Spreadsheet.wall_thickness * 2) / 4
  expr: Constraints[41] = 2 * Spreadsheet.Bottom_c_rad * sin(45 / 2)
  expr: Constraints[43] = 2 * Spreadsheet.Bottom_c_rad * sin(45 / 2)
  expr: Constraints[49] = Spreadsheet.PCB_length / 2
  expr: Constraints[4] = Spreadsheet.PCB_length + 2 * Spreadsheet.pcb_to_wall_gap + 2 * Spreadsheet.wall_thickness
  sketch-geometry (39):
    g0: LineSegment StartX=-6.5 StartY=0.5 StartZ=0 EndX=-6.5 EndY=-58.5 EndZ=0
    g1: LineSegment StartX=-1.5 StartY=-63.5 StartZ=0 EndX=46.7407 EndY=-63.5 EndZ=0
    g2: LineSegment StartX=358.925 StartY=-58.5 StartZ=0 EndX=358.925 EndY=0.5 EndZ=0
    g3: LineSegment StartX=352.925 StartY=6.5 StartZ=0 EndX=-0.5 EndY=6.5 EndZ=0
    g4: ArcOfCircle CenterX=-0.5 CenterY=0.5 CenterZ=0 NormalX=0 NormalY=0 NormalZ=1 AngleXU=0 Radius=6 StartAngle=1.5708 EndAngle=3.14159
    g5: GeomPoint X=-6.5 Y=6.5 Z=0
    g6: ArcOfCircle CenterX=352.925 CenterY=0.5 CenterZ=0 NormalX=0 NormalY=0 NormalZ=1 AngleXU=0 Radius=6 StartAngle=0 EndAngle=1.5708
    g7: GeomPoint X=358.925 Y=6.5 Z=0
    g8: ArcOfCircle CenterX=-1.5 CenterY=-58.5 CenterZ=0 NormalX=0 NormalY=0 NormalZ=1 AngleXU=0 Radius=5 StartAngle=3.14159 EndAngle=4.71239
    g9: GeomPoint X=-6.5 Y=-63.5 Z=0
    g10: ArcOfCircle CenterX=353.925 CenterY=-58.5 CenterZ=0 NormalX=0 NormalY=0 NormalZ=1 AngleXU=0 Radius=5 StartAngle=4.71239 EndAngle=6.28319
    g11: GeomPoint X=358.925 Y=-63.5 Z=0
    g12: Circle CenterX=-1.74263 CenterY=1.74277 CenterZ=0 NormalX=0 NormalY=0 NormalZ=1 AngleXU=0 Radius=1.05
    g13: GeomPoint X=-1.67193 Y=0.402977 Z=0
    g14: GeomPoint X=351.753 Y=0.5 Z=0
    g15: GeomPoint X=-4.74264 Y=4.74264 Z=0
    g16: GeomPoint X=1.25739 Y=-1.2571 Z=0
    g17: Circle CenterX=354.168 CenterY=1.74278 CenterZ=0 NormalX=0 NormalY=0 NormalZ=1 AngleXU=0 Radius=1.05
    g18: GeomPoint X=351.168 Y=-1.25708 Z=0
    g19: GeomPoint X=357.168 Y=4.74264 Z=0
    g20: Circle CenterX=84.8563 CenterY=3.5 CenterZ=0 NormalX=0 NormalY=0 NormalZ=1 AngleXU=0 Radius=1.05
    g21: Circle CenterX=176.213 CenterY=3.5 CenterZ=0 NormalX=0 NormalY=0 NormalZ=1 AngleXU=0 Radius=1.05
    g22: Circle CenterX=267.569 CenterY=3.5 CenterZ=0 NormalX=0 NormalY=0 NormalZ=1 AngleXU=0 Radius=1.05
    g23: GeomPoint X=-5.97279 Y=-60.7348 Z=0
    g24: GeomPoint X=356.16 Y=-62.9728 Z=0
    g25: GeomPoint X=176.213 Y=-63.5 Z=0
    g26: LineSegment StartX=49.8717 StartY=-62.3984 StartZ=0 EndX=78.2559 EndY=-39.6016 EndZ=0
    g27: LineSegment StartX=81.3868 StartY=-38.5 StartZ=0 EndX=271.038 EndY=-38.5 EndZ=0
    g28: LineSegment StartX=274.169 StartY=-39.6016 StartZ=0 EndX=302.553 EndY=-62.3984 EndZ=0
    g29: GeomPoint X=176.213 Y=-38.5 Z=0
    g30: LineSegment StartX=305.684 StartY=-63.5 StartZ=0 EndX=353.925 EndY=-63.5 EndZ=0
    g31: ArcOfCircle CenterX=81.3868 CenterY=-43.5 CenterZ=0 NormalX=0 NormalY=0 NormalZ=1 AngleXU=0 Radius=5 StartAngle=1.5708 EndAngle=2.24745
    g32: GeomPoint X=79.6275 Y=-38.5 Z=0
    g33: ArcOfCircle CenterX=271.038 CenterY=-43.5 CenterZ=0 NormalX=0 NormalY=0 NormalZ=1 AngleXU=0 Radius=5 StartAngle=0.894139 EndAngle=1.5708
    g34: GeomPoint X=272.797 Y=-38.5 Z=0
    g35: ArcOfCircle CenterX=305.684 CenterY=-58.5 CenterZ=0 NormalX=0 NormalY=0 NormalZ=1 AngleXU=0 Radius=5 StartAngle=4.03573 EndAngle=4.71239
    g36: GeomPoint X=303.925 Y=-63.5 Z=0
    g37: ArcOfCircle CenterX=46.7407 CenterY=-58.5 CenterZ=0 NormalX=0 NormalY=0 NormalZ=1 AngleXU=0 Radius=5 StartAngle=4.71239 EndAngle=5.38905
    g38: GeomPoint X=48.5 Y=-63.5 Z=0
  constraints (80):
    c: Horizontal(g1)
    c: Horizontal(g3)
    c: Vertical(g0)
    c: Vertical(g2)
    c: DistanceX(g5,g7) = 365.425
    c: PointOnObject(g5,g0)
    c: PointOnObject(g5,g3)
    c: Tangent(g0,g4) = -1.5708
    c: Tangent(g3,g4) = -1.5708
    c: PointOnObject(g7,g2)
    c: PointOnObject(g7,g3)
    c: Tangent(g2,g6) = -1.5708
    c: Tangent(g3,g6) = -1.5708
    c: PointOnObject(g9,g0)
    c: PointOnObject(g9,g1)
    c: Tangent(g0,g8) = -1.5708
    c: Tangent(g1,g8) = -1.5708
    c: PointOnObject(g11,g1)
    c: PointOnObject(g11,g2)
    c: Coincident(g30,g10) = -1.5708
    c: Tangent(g2,g10) = -1.5708
    c: Radius(g8) = 5
    c: Radius(g4) = 6
    c: Radius(g6) = 6
    c: Diameter(g12) = 2.1
    c: DistanceX(g13,g14) = 353.425
    c: PointOnObject(g15,g4)
    c: Distance(g0,g15) = 4.5922
    c: Symmetric(g15,g16,g12)
    c: Diameter(g17) = 2.1
    c: PointOnObject(g19,g6)
    c: Distance(g2,g19) = 4.5922
    c: Symmetric(g18,g19,g17)
    c: Equal(g20,g21)
    c: Equal(g22,g21)
    c: Diameter(g21) = 2.1
    c: Distance(g21,g3) = 3
    c: DistanceX(g-1,g21) = 176.213
    c: DistanceX(g20,g21) = 91.3563
    c: DistanceX(g21,g22) = 91.3563
    c: PointOnObject(g23,g8)
    c: Distance(g0,g23) = 2.2961
    c: PointOnObject(g24,g10)
    c: Distance(g30,g24) = 2.2961
    c: Horizontal(g20,g21)
    c: Horizontal(g22,g21)
    c: DistanceY(g-1,g3) = 6.5
    c: DistanceX(g0,g-1) = 6.5
    c: Equal(g8,g10)
    c: DistanceX(g-1,g25) = 176.213
    c: Horizontal(g27)
    c: Symmetric(g32,g34,g29)
    c: Vertical(g29,g25)
    c: PointOnObject(g32,g26)
    c: PointOnObject(g32,g27)
    c: Tangent(g26,g31) = 1.5708
    c: Tangent(g27,g31) = 1.5708
    c: PointOnObject(g34,g27)
    c: PointOnObject(g34,g28)
    c: Tangent(g27,g33) = 1.5708
    c: Tangent(g28,g33) = 1.5708
    c: Equal(g33,g31)
    c: Horizontal(g38,g36)
    c: Horizontal(g30)
    c: PointOnObject(g36,g28)
    c: PointOnObject(g36,g30)
    c: Tangent(g28,g35) = -1.5708
    c: Tangent(g30,g35) = -1.5708
    c: PointOnObject(g38,g1)
    c: PointOnObject(g38,g26)
    c: Tangent(g1,g37) = -1.5708
    c: Tangent(g26,g37) = -1.5708
    c: DistanceX(g1,g38) = 50
    c: Symmetric(g38,g36,g25)
    c: Equal(g37,g35)
    c: Radius(g37) = 5
    c: Radius(g33) = 5
    c: Vertical(g10,g10)
    c: DistanceY(g11,g7) = 70
    c: DistanceY(g36,g34) = 25
FEATURE [PartDesign::Pad] Pad007
  Direction = (0,0,1)
  Length = 3
  Length2 = 10
  Profile = -> Sketch034
  ReferenceAxis = -> Sketch034 [N_Axis]
  Type = 0
FEATURE [PartDesign::Body] Body007  label="feet"
  Group = -> [Sketch034,Pad007]
  Origin = -> Origin202
  Placement = pos=(0,0,-12) rot=(0,0,1;0rad)
  Tip = -> Pad007
FEATURE [Sketcher::SketchObject] Sketch035
  AttachmentOffset = pos=(0,0,6) rot=(0,0,1;0rad)
  FullyConstrained = false
  MapMode = 5
  Placement = pos=(0,0,6) rot=(0,0,1;0rad)
  Support = -> [XY_Plane196]
  expr: Constraints[5] = Spreadsheet.u
  sketch-geometry (13):
    g0: LineSegment StartX=8.16089 StartY=-46.667 StartZ=0 EndX=8.16089 EndY=-57.0051 EndZ=0
    g1: LineSegment StartX=10.1609 StartY=-59.0051 StartZ=0 EndX=27.9391 EndY=-59.0051 EndZ=0
    g2: LineSegment StartX=29.9391 StartY=-57.0051 StartZ=0 EndX=29.9391 EndY=-46.667 EndZ=0
    g3: LineSegment StartX=27.9391 StartY=-44.667 StartZ=0 EndX=10.1609 EndY=-44.667 EndZ=0
    g4: GeomPoint X=19.05 Y=-51.836 Z=0
    g5: ArcOfCircle CenterX=10.1609 CenterY=-46.667 CenterZ=0 NormalX=0 NormalY=0 NormalZ=1 AngleXU=0 Radius=2 StartAngle=1.5708 EndAngle=3.14159
    g6: GeomPoint X=8.16089 Y=-44.667 Z=0
    g7: ArcOfCircle CenterX=27.9391 CenterY=-46.667 CenterZ=0 NormalX=0 NormalY=0 NormalZ=1 AngleXU=0 Radius=2 StartAngle=1.6e-15 EndAngle=1.5708
    g8: GeomPoint X=29.9391 Y=-44.667 Z=0
    g9: ArcOfCircle CenterX=10.1609 CenterY=-57.0051 CenterZ=0 NormalX=0 NormalY=0 NormalZ=1 AngleXU=0 Radius=2 StartAngle=3.14159 EndAngle=4.71239
    g10: GeomPoint X=8.16089 Y=-59.0051 Z=0
    g11: ArcOfCircle CenterX=27.9391 CenterY=-57.0051 CenterZ=0 NormalX=0 NormalY=0 NormalZ=1 AngleXU=0 Radius=2 StartAngle=4.71239 EndAngle=6.28319
    g12: GeomPoint X=29.9391 Y=-59.0051 Z=0
  constraints (26):
    c: Horizontal(g1)
    c: Horizontal(g3)
    c: Vertical(g0)
    c: Vertical(g2)
    c: Symmetric(g12,g6,g4)
    c: DistanceX(g-1,g4) = 19.05
    c: PointOnObject(g6,g0)
    c: PointOnObject(g6,g3)
    c: Tangent(g0,g5) = -1.5708
    c: Tangent(g3,g5) = -1.5708
    c: PointOnObject(g8,g2)
    c: PointOnObject(g8,g3)
    c: Tangent(g2,g7) = -1.5708
    c: Tangent(g3,g7) = -1.5708
    c: PointOnObject(g10,g0)
    c: PointOnObject(g10,g1)
    c: Tangent(g0,g9) = -1.5708
    c: Tangent(g1,g9) = -1.5708
    c: PointOnObject(g12,g1)
    c: PointOnObject(g12,g2)
    c: Tangent(g1,g11) = -1.5708
    c: Tangent(g2,g11) = -1.5708
    c: Equal(g9,g11)
    c: Equal(g11,g7)
    c: Equal(g7,g5)
    c: Radius(g9) = 2
FEATURE [PartDesign::Pocket] Pocket027
  BaseFeature = -> Pad003
  Direction = (0,0,-1)
  Length = 5
  Length2 = 5
  Profile = -> Sketch035
  ReferenceAxis = -> Sketch035 [N_Axis]
  Type = 0
FEATURE [Sketcher::SketchObject] Sketch036
  AttachmentOffset = pos=(0,0,6) rot=(0,0,1;0rad)
  FullyConstrained = false
  MapMode = 5
  Placement = pos=(0,0,6) rot=(0,0,1;0rad)
  Support = -> [XY_Plane196]
  expr: Constraints[0] = Spreadsheet.PCB_length / 2
  expr: Constraints[11] = Spreadsheet.Spacer_hole
  expr: Constraints[1] = Spreadsheet.PCB_width / 2
  sketch-geometry (15):
    g0: GeomPoint X=176.213 Y=-69.5 Z=0
    g1: GeomPoint X=-6.5 Y=-145.5 Z=0
    g2: GeomPoint X=358.925 Y=-145.5 Z=0
    g3: GeomPoint X=176.213 Y=-69.5 Z=0
    g4: GeomPoint X=354.097 Y=-139.403 Z=0
    g5: GeomPoint X=-0.5 Y=-139.597 Z=0
    g6: Circle CenterX=84.8563 CenterY=-142.5 CenterZ=0 NormalX=0 NormalY=0 NormalZ=1 AngleXU=0 Radius=1.55
    g7: Circle CenterX=176.213 CenterY=-142.5 CenterZ=0 NormalX=0 NormalY=0 NormalZ=1 AngleXU=0 Radius=1.55
    g8: Circle CenterX=267.569 CenterY=-142.5 CenterZ=0 NormalX=0 NormalY=0 NormalZ=1 AngleXU=0 Radius=1.55
    g9: Circle CenterX=-2.62127 CenterY=-141.621 CenterZ=0 NormalX=0 NormalY=0 NormalZ=1 AngleXU=0 Radius=1.55
    g10: GeomPoint X=0.378778 Y=-138.621 Z=0
    g11: GeomPoint X=-5.62132 Y=-144.621 Z=0
    g12: GeomPoint X=352.047 Y=-138.621 Z=0
    g13: GeomPoint X=358.046 Y=-144.621 Z=0
    g14: Circle CenterX=355.047 CenterY=-141.621 CenterZ=0 NormalX=0 NormalY=0 NormalZ=1 AngleXU=0 Radius=1.55
  constraints (14):
    c: DistanceX(g-1,g0) = 176.213
    c: DistanceY(g0,g-1) = 69.5
    c: Coincident(g3,g0)
    c: Equal(g6,g7)
    c: Equal(g8,g7)
    c: DistanceX(g6,g7) = 91.3563
    c: DistanceX(g7,g8) = 91.3563
    c: Horizontal(g6,g7)
    c: Horizontal(g8,g7)
    c: Symmetric(g12,g13,g14)
    c: Symmetric(g11,g10,g9)
    c: Diameter(g7) = 3.1
    c: Equal(g9,g6)
    c: Equal(g14,g8)
FEATURE [Sketcher::SketchObject] Sketch037
  AttachmentOffset = pos=(0,0,2.9) rot=(0,0,1;0rad)
  FullyConstrained = false
  MapMode = 5
  Placement = pos=(0,0,2.9) rot=(0,0,1;0rad)
  Support = -> [XY_Plane204]
  expr: .AttachmentOffset.Base.z = 1.6 + 1.3
  expr: Constraints[24] = Spreadsheet.Screw_hole
  expr: Constraints[25] = Spreadsheet.PCB_length + Spreadsheet.pcb_to_wall_gap * 2
  expr: Constraints[27] = 2 * Spreadsheet.Top_c_rad * sin(45 / 2)
  expr: Constraints[29] = Spreadsheet.Screw_hole
  expr: Constraints[31] = 2 * Spreadsheet.Top_c_rad * sin(45 / 2)
  expr: Constraints[35] = Spreadsheet.Screw_hole
  expr: Constraints[36] = Spreadsheet.wall_thickness / 2
  expr: Constraints[37] = Spreadsheet.PCB_length / 2
  expr: Constraints[38] = (Spreadsheet.PCB_length + Spreadsheet.pcb_to_wall_gap * 2 + Spreadsheet.wall_thickness * 2) / 4
  expr: Constraints[39] = (Spreadsheet.PCB_length + Spreadsheet.pcb_to_wall_gap * 2 + Spreadsheet.wall_thickness * 2) / 4
  expr: Constraints[41] = 2 * Spreadsheet.Bottom_c_rad * sin(45 / 2)
  expr: Constraints[43] = 2 * Spreadsheet.Bottom_c_rad * sin(45 / 2)
  expr: Constraints[49] = Spreadsheet.PCB_length / 2
  expr: Constraints[4] = Spreadsheet.PCB_length + 2 * Spreadsheet.pcb_to_wall_gap + 2 * Spreadsheet.wall_thickness
  sketch-geometry (39):
    g0: LineSegment StartX=-6.5 StartY=0.5 StartZ=0 EndX=-6.5 EndY=-38.5 EndZ=0
    g1: LineSegment StartX=-1.5 StartY=-43.5 StartZ=0 EndX=47.0498 EndY=-43.5 EndZ=0
    g2: LineSegment StartX=358.925 StartY=-38.5 StartZ=0 EndX=358.925 EndY=0.5 EndZ=0
    g3: LineSegment StartX=352.925 StartY=6.5 StartZ=0 EndX=-0.5 EndY=6.5 EndZ=0
    g4: ArcOfCircle CenterX=-0.5 CenterY=0.5 CenterZ=0 NormalX=0 NormalY=0 NormalZ=1 AngleXU=0 Radius=6 StartAngle=1.5708 EndAngle=3.14159
    g5: GeomPoint X=-6.5 Y=6.5 Z=0
    g6: ArcOfCircle CenterX=352.925 CenterY=0.5 CenterZ=0 NormalX=0 NormalY=0 NormalZ=1 AngleXU=0 Radius=6 StartAngle=0 EndAngle=1.5708
    g7: GeomPoint X=358.925 Y=6.5 Z=0
    g8: ArcOfCircle CenterX=-1.5 CenterY=-38.5 CenterZ=0 NormalX=0 NormalY=0 NormalZ=1 AngleXU=0 Radius=5 StartAngle=3.14159 EndAngle=4.71239
    g9: GeomPoint X=-6.5 Y=-43.5 Z=0
    g10: ArcOfCircle CenterX=353.925 CenterY=-38.5 CenterZ=0 NormalX=0 NormalY=0 NormalZ=1 AngleXU=0 Radius=5 StartAngle=4.71239 EndAngle=6.28319
    g11: GeomPoint X=358.925 Y=-43.5 Z=0
    g12: Circle CenterX=-1.7427 CenterY=1.74285 CenterZ=0 NormalX=0 NormalY=0 NormalZ=1 AngleXU=0 Radius=1.05
    g13: GeomPoint X=-1.67193 Y=0.402977 Z=0
    g14: GeomPoint X=351.753 Y=0.5 Z=0
    g15: GeomPoint X=-4.74264 Y=4.74264 Z=0
    g16: GeomPoint X=1.25723 Y=-1.25694 Z=0
    g17: Circle CenterX=354.168 CenterY=1.74286 CenterZ=0 NormalX=0 NormalY=0 NormalZ=1 AngleXU=0 Radius=1.05
    g18: GeomPoint X=351.168 Y=-1.25692 Z=0
    g19: GeomPoint X=357.168 Y=4.74264 Z=0
    g20: Circle CenterX=84.8563 CenterY=3.5 CenterZ=0 NormalX=0 NormalY=0 NormalZ=1 AngleXU=0 Radius=1.05
    g21: Circle CenterX=176.213 CenterY=3.5 CenterZ=0 NormalX=0 NormalY=0 NormalZ=1 AngleXU=0 Radius=1.05
    g22: Circle CenterX=267.569 CenterY=3.5 CenterZ=0 NormalX=0 NormalY=0 NormalZ=1 AngleXU=0 Radius=1.05
    g23: GeomPoint X=-5.97279 Y=-40.7348 Z=0
    g24: GeomPoint X=356.16 Y=-42.9728 Z=0
    g25: GeomPoint X=176.213 Y=-43.5 Z=0
    g26: LineSegment StartX=49.7252 StartY=-42.724 StartZ=0 EndX=78.8516 EndY=-24.276 EndZ=0
    g27: LineSegment StartX=81.527 StartY=-23.5 StartZ=0 EndX=270.898 EndY=-23.5 EndZ=0
    g28: LineSegment StartX=273.573 StartY=-24.276 StartZ=0 EndX=302.7 EndY=-42.724 EndZ=0
    g29: GeomPoint X=176.213 Y=-23.5 Z=0
    g30: LineSegment StartX=305.375 StartY=-43.5 StartZ=0 EndX=353.925 EndY=-43.5 EndZ=0
    g31: ArcOfCircle CenterX=81.527 CenterY=-28.5 CenterZ=0 NormalX=0 NormalY=0 NormalZ=1 AngleXU=0 Radius=5 StartAngle=1.5708 EndAngle=2.1354
    g32: GeomPoint X=80.0767 Y=-23.5 Z=0
    g33: ArcOfCircle CenterX=270.898 CenterY=-28.5 CenterZ=0 NormalX=0 NormalY=0 NormalZ=1 AngleXU=0 Radius=5 StartAngle=1.0062 EndAngle=1.5708
    g34: GeomPoint X=272.348 Y=-23.5 Z=0
    g35: ArcOfCircle CenterX=305.375 CenterY=-38.5 CenterZ=0 NormalX=0 NormalY=0 NormalZ=1 AngleXU=0 Radius=5 StartAngle=4.14779 EndAngle=4.71239
    g36: GeomPoint X=303.925 Y=-43.5 Z=0
    g37: ArcOfCircle CenterX=47.0498 CenterY=-38.5 CenterZ=0 NormalX=0 NormalY=0 NormalZ=1 AngleXU=0 Radius=5 StartAngle=4.71239 EndAngle=5.27699
    g38: GeomPoint X=48.5 Y=-43.5 Z=0
  constraints (80):
    c: Horizontal(g1)
    c: Horizontal(g3)
    c: Vertical(g0)
    c: Vertical(g2)
    c: DistanceX(g5,g7) = 365.425
    c: PointOnObject(g5,g0)
    c: PointOnObject(g5,g3)
    c: Tangent(g0,g4) = -1.5708
    c: Tangent(g3,g4) = -1.5708
    c: PointOnObject(g7,g2)
    c: PointOnObject(g7,g3)
    c: Tangent(g2,g6) = -1.5708
    c: Tangent(g3,g6) = -1.5708
    c: PointOnObject(g9,g0)
    c: PointOnObject(g9,g1)
    c: Tangent(g0,g8) = -1.5708
    c: Tangent(g1,g8) = -1.5708
    c: PointOnObject(g11,g1)
    c: PointOnObject(g11,g2)
    c: Coincident(g30,g10) = -1.5708
    c: Tangent(g2,g10) = -1.5708
    c: Radius(g8) = 5
    c: Radius(g4) = 6
    c: Radius(g6) = 6
    c: Diameter(g12) = 2.1
    c: DistanceX(g13,g14) = 353.425
    c: PointOnObject(g15,g4)
    c: Distance(g0,g15) = 4.5922
    c: Symmetric(g15,g16,g12)
    c: Diameter(g17) = 2.1
    c: PointOnObject(g19,g6)
    c: Distance(g2,g19) = 4.5922
    c: Symmetric(g18,g19,g17)
    c: Equal(g20,g21)
    c: Equal(g22,g21)
    c: Diameter(g21) = 2.1
    c: Distance(g21,g3) = 3
    c: DistanceX(g-1,g21) = 176.213
    c: DistanceX(g20,g21) = 91.3563
    c: DistanceX(g21,g22) = 91.3563
    c: PointOnObject(g23,g8)
    c: Distance(g0,g23) = 2.2961
    c: PointOnObject(g24,g10)
    c: Distance(g30,g24) = 2.2961
    c: Horizontal(g20,g21)
    c: Horizontal(g22,g21)
    c: DistanceY(g-1,g3) = 6.5
    c: DistanceX(g0,g-1) = 6.5
    c: Equal(g8,g10)
    c: DistanceX(g-1,g25) = 176.213
    c: Horizontal(g27)
    c: Symmetric(g32,g34,g29)
    c: Vertical(g29,g25)
    c: PointOnObject(g32,g26)
    c: PointOnObject(g32,g27)
    c: Tangent(g26,g31) = 1.5708
    c: Tangent(g27,g31) = 1.5708
    c: PointOnObject(g34,g27)
    c: PointOnObject(g34,g28)
    c: Tangent(g27,g33) = 1.5708
    c: Tangent(g28,g33) = 1.5708
    c: Equal(g33,g31)
    c: Horizontal(g38,g36)
    c: Horizontal(g30)
    c: PointOnObject(g36,g28)
    c: PointOnObject(g36,g30)
    c: Tangent(g28,g35) = -1.5708
    c: Tangent(g30,g35) = -1.5708
    c: PointOnObject(g38,g1)
    c: PointOnObject(g38,g26)
    c: Tangent(g1,g37) = -1.5708
    c: Tangent(g26,g37) = -1.5708
    c: DistanceX(g1,g38) = 50
    c: Symmetric(g38,g36,g25)
    c: Equal(g37,g35)
    c: Radius(g37) = 5
    c: Radius(g33) = 5
    c: Vertical(g10,g10)
    c: DistanceY(g11,g7) = 50
    c: DistanceY(g36,g34) = 20
FEATURE [PartDesign::Pad] Pad008
  Direction = (0,0,1)
  Length = 3
  Length2 = 10
  Profile = -> Sketch037
  ReferenceAxis = -> Sketch037 [N_Axis]
  Type = 0
FEATURE [Sketcher::SketchObject] Sketch039  label="Sketch038"
  AttachmentOffset = pos=(316,1,2) rot=(0,1,0;3.14159rad)
  FullyConstrained = false
  MapMode = 5
  Placement = pos=(316,1,2) rot=(0,1,0;3.14159rad)
  Support = -> [XY_Plane204]
  sketch-geometry (102):
    g0: LineSegment StartX=82.505 StartY=-2.92238 StartZ=0 EndX=82.505 EndY=-19.9224 EndZ=0
    g1: LineSegment StartX=82.505 StartY=-19.9224 StartZ=0 EndX=87.4677 EndY=-19.9224 EndZ=0
    g2: LineSegment StartX=92.505 StartY=-11.435 StartZ=0 EndX=92.505 EndY=-2.92238 EndZ=0
    g3: LineSegment StartX=92.505 StartY=-2.92238 StartZ=0 EndX=82.505 EndY=-2.92238 EndZ=0
    g4: GeomPoint X=87.505 Y=-11.4224 Z=0
    g5: LineSegment StartX=92.505 StartY=-11.435 StartZ=0 EndX=87.4677 EndY=-11.435 EndZ=0
    g6: LineSegment StartX=87.4677 StartY=-11.435 StartZ=0 EndX=87.4677 EndY=-19.9224 EndZ=0
    g7: LineSegment StartX=95.505 StartY=-2.92238 StartZ=0 EndX=95.505 EndY=-19.9224 EndZ=0
    g8: LineSegment StartX=95.505 StartY=-19.9224 StartZ=0 EndX=98.005 EndY=-19.9224 EndZ=0
    g9: LineSegment StartX=98.005 StartY=-19.9224 StartZ=0 EndX=98.005 EndY=-2.92238 EndZ=0
    g10: LineSegment StartX=98.005 StartY=-2.92238 StartZ=0 EndX=95.505 EndY=-2.92238 EndZ=0
    g11: GeomPoint X=96.755 Y=-11.4224 Z=0
    g12: LineSegment StartX=101.005 StartY=-2.92238 StartZ=0 EndX=101.005 EndY=-4.92238 EndZ=0
    g13: LineSegment StartX=101.005 StartY=-19.9224 StartZ=0 EndX=103.005 EndY=-19.9224 EndZ=0
    g14: LineSegment StartX=118.005 StartY=-19.9224 StartZ=0 EndX=118.005 EndY=-17.9224 EndZ=0
    g15: LineSegment StartX=118.005 StartY=-2.92238 StartZ=0 EndX=116.005 EndY=-2.92238 EndZ=0
    g16: GeomPoint X=109.505 Y=-11.4224 Z=0
    g17: LineSegment StartX=103.005 StartY=-2.92238 StartZ=0 EndX=109.505 EndY=-9.42238 EndZ=0
    g18: LineSegment StartX=116.005 StartY=-19.9224 StartZ=0 EndX=109.505 EndY=-13.4224 EndZ=0
    g19: LineSegment StartX=101.005 StartY=-17.9224 StartZ=0 EndX=107.505 EndY=-11.4224 EndZ=0
    g20: LineSegment StartX=118.005 StartY=-4.92238 StartZ=0 EndX=111.505 EndY=-11.4224 EndZ=0
    g21: GeomPoint X=109.505 Y=-9.42238 Z=0
    g22: GeomPoint X=107.505 Y=-11.4224 Z=0
    g23: GeomPoint X=109.505 Y=-13.4224 Z=0
    g24: GeomPoint X=111.505 Y=-11.4224 Z=0
    g25: LineSegment StartX=121.005 StartY=-2.92238 StartZ=0 EndX=121.005 EndY=-19.9224 EndZ=0
    g26: LineSegment StartX=121.005 StartY=-19.9224 StartZ=0 EndX=131.505 EndY=-19.9224 EndZ=0
    g27: LineSegment StartX=131.505 StartY=-19.9224 StartZ=0 EndX=131.505 EndY=-16.4224 EndZ=0
    g28: LineSegment StartX=131.505 StartY=-2.92238 StartZ=0 EndX=121.005 EndY=-2.92238 EndZ=0
    g29: GeomPoint X=126.255 Y=-11.4224 Z=0
    g30: LineSegment StartX=131.505 StartY=-6.42238 StartZ=0 EndX=124.505 EndY=-6.42238 EndZ=0
    g31: LineSegment StartX=124.505 StartY=-6.42238 StartZ=0 EndX=124.505 EndY=-9.42238 EndZ=0
    g32: LineSegment StartX=124.505 StartY=-9.42238 StartZ=0 EndX=131.505 EndY=-9.42238 EndZ=0
    g33: LineSegment StartX=131.505 StartY=-13.4224 StartZ=0 EndX=124.505 EndY=-13.4224 EndZ=0
    g34: LineSegment StartX=124.505 StartY=-13.4224 StartZ=0 EndX=124.505 EndY=-16.4224 EndZ=0
    g35: LineSegment StartX=124.505 StartY=-16.4224 StartZ=0 EndX=131.505 EndY=-16.4224 EndZ=0
    g36: GeomPoint X=131.505 Y=-11.4224 Z=0
    g37: LineSegment StartX=134.505 StartY=-2.92238 StartZ=0 EndX=134.505 EndY=-19.9224 EndZ=0
    g38: LineSegment StartX=134.505 StartY=-19.9224 StartZ=0 EndX=143.505 EndY=-19.9224 EndZ=0
    g39: LineSegment StartX=143.505 StartY=-19.9224 StartZ=0 EndX=143.505 EndY=-16.5523 EndZ=0
    g40: LineSegment StartX=137.187 StartY=-2.92238 StartZ=0 EndX=134.505 EndY=-2.92238 EndZ=0
    g41: GeomPoint X=139.005 Y=-11.4224 Z=0
    g42: LineSegment StartX=137.187 StartY=-2.92238 StartZ=0 EndX=137.187 EndY=-16.5523 EndZ=0
    g43: LineSegment StartX=137.187 StartY=-16.5523 StartZ=0 EndX=143.505 EndY=-16.5523 EndZ=0
    g44: LineSegment StartX=146.505 StartY=-2.92238 StartZ=0 EndX=146.505 EndY=-19.9224 EndZ=0
    g45: LineSegment StartX=146.505 StartY=-19.9224 StartZ=0 EndX=157.005 EndY=-19.9224 EndZ=0
    g46: LineSegment StartX=157.005 StartY=-19.9224 StartZ=0 EndX=157.005 EndY=-16.4224 EndZ=0
    g47: LineSegment StartX=157.005 StartY=-2.92238 StartZ=0 EndX=146.505 EndY=-2.92238 EndZ=0
    g48: GeomPoint X=151.755 Y=-11.4224 Z=0
    g49: LineSegment StartX=157.005 StartY=-6.42238 StartZ=0 EndX=150.005 EndY=-6.42238 EndZ=0
    g50: LineSegment StartX=150.005 StartY=-6.42238 StartZ=0 EndX=150.005 EndY=-9.42238 EndZ=0
    g51: LineSegment StartX=150.005 StartY=-9.42238 StartZ=0 EndX=157.005 EndY=-9.42238 EndZ=0
    g52: LineSegment StartX=157.005 StartY=-13.4224 StartZ=0 EndX=150.005 EndY=-13.4224 EndZ=0
    g53: LineSegment StartX=150.005 StartY=-13.4224 StartZ=0 EndX=150.005 EndY=-16.4224 EndZ=0
    g54: LineSegment StartX=150.005 StartY=-16.4224 StartZ=0 EndX=157.005 EndY=-16.4224 EndZ=0
    g55: GeomPoint X=157.005 Y=-11.4224 Z=0
    g56: LineSegment StartX=160.005 StartY=-2.92238 StartZ=0 EndX=160.005 EndY=-5.92238 EndZ=0
    g57: LineSegment StartX=163.755 StartY=-19.9224 StartZ=0 EndX=166.755 EndY=-19.9224 EndZ=0
    g58: LineSegment StartX=170.505 StartY=-5.92238 StartZ=0 EndX=170.505 EndY=-2.92238 EndZ=0
    g59: LineSegment StartX=170.505 StartY=-2.92238 StartZ=0 EndX=160.005 EndY=-2.92238 EndZ=0
    g60: GeomPoint X=165.255 Y=-11.4224 Z=0
    g61: LineSegment StartX=187.005 StartY=-3.01371 StartZ=0 EndX=187.005 EndY=-19.831 EndZ=0
    g62: LineSegment StartX=187.005 StartY=-19.831 StartZ=0 EndX=197.505 EndY=-19.831 EndZ=0
    g63: LineSegment StartX=197.505 StartY=-19.831 StartZ=0 EndX=197.505 EndY=-16.2623 EndZ=0
    g64: LineSegment StartX=197.505 StartY=-3.01371 StartZ=0 EndX=187.005 EndY=-3.01371 EndZ=0
    g65: GeomPoint X=192.255 Y=-11.4224 Z=0
    g66: LineSegment StartX=197.505 StartY=-6.58244 StartZ=0 EndX=190.505 EndY=-6.58244 EndZ=0
    g67: LineSegment StartX=190.505 StartY=-6.58244 StartZ=0 EndX=190.505 EndY=-9.42238 EndZ=0
    g68: LineSegment StartX=190.505 StartY=-9.42238 StartZ=0 EndX=197.505 EndY=-9.42238 EndZ=0
    g69: LineSegment StartX=197.505 StartY=-13.4224 StartZ=0 EndX=190.505 EndY=-13.4224 EndZ=0
    g70: LineSegment StartX=190.505 StartY=-13.4224 StartZ=0 EndX=190.505 EndY=-16.2623 EndZ=0
    g71: LineSegment StartX=190.505 StartY=-16.2623 StartZ=0 EndX=197.505 EndY=-16.2623 EndZ=0
    g72: GeomPoint X=197.505 Y=-11.4224 Z=0
    g73: LineSegment StartX=163.755 StartY=-19.9224 StartZ=0 EndX=163.755 EndY=-5.92238 EndZ=0
    g74: LineSegment StartX=166.755 StartY=-19.9224 StartZ=0 EndX=166.755 EndY=-5.92238 EndZ=0
    g75: GeomPoint X=165.255 Y=-19.9224 Z=0
    g76: LineSegment StartX=163.755 StartY=-5.92238 StartZ=0 EndX=160.005 EndY=-5.92238 EndZ=0
    g77: LineSegment StartX=166.755 StartY=-5.92238 StartZ=0 EndX=170.505 EndY=-5.92238 EndZ=0
    g78: LineSegment StartX=173.505 StartY=-2.92238 StartZ=0 EndX=173.505 EndY=-5.92238 EndZ=0
    g79: LineSegment StartX=177.255 StartY=-19.9224 StartZ=0 EndX=180.255 EndY=-19.9224 EndZ=0
    g80: LineSegment StartX=184.005 StartY=-5.92238 StartZ=0 EndX=184.005 EndY=-2.92238 EndZ=0
    g81: LineSegment StartX=184.005 StartY=-2.92238 StartZ=0 EndX=173.505 EndY=-2.92238 EndZ=0
    g82: GeomPoint X=178.755 Y=-11.4224 Z=0
    g83: LineSegment StartX=177.255 StartY=-19.9224 StartZ=0 EndX=177.255 EndY=-5.92238 EndZ=0
    g84: LineSegment StartX=180.255 StartY=-19.9224 StartZ=0 EndX=180.255 EndY=-5.92238 EndZ=0
    g85: GeomPoint X=178.755 Y=-19.9224 Z=0
    g86: LineSegment StartX=177.255 StartY=-5.92238 StartZ=0 EndX=173.505 EndY=-5.92238 EndZ=0
    g87: LineSegment StartX=180.255 StartY=-5.92238 StartZ=0 EndX=184.005 EndY=-5.92238 EndZ=0
    g88: LineSegment StartX=101.005 StartY=-17.9224 StartZ=0 EndX=101.005 EndY=-19.9224 EndZ=0
    g89: LineSegment StartX=109.505 StartY=-9.42238 StartZ=0 EndX=116.005 EndY=-2.92238 EndZ=0
    g90: LineSegment StartX=111.505 StartY=-11.4224 StartZ=0 EndX=118.005 EndY=-17.9224 EndZ=0
    g91: LineSegment StartX=107.505 StartY=-11.4224 StartZ=0 EndX=101.005 EndY=-4.92238 EndZ=0
    g92: LineSegment StartX=109.505 StartY=-13.4224 StartZ=0 EndX=103.005 EndY=-19.9224 EndZ=0
    g93: LineSegment StartX=116.005 StartY=-19.9224 StartZ=0 EndX=118.005 EndY=-19.9224 EndZ=0
    g94: LineSegment StartX=103.005 StartY=-2.92238 StartZ=0 EndX=101.005 EndY=-2.92238 EndZ=0
    g95: LineSegment StartX=118.005 StartY=-4.92238 StartZ=0 EndX=118.005 EndY=-2.92238 EndZ=0
    g96: LineSegment StartX=131.505 StartY=-6.42238 StartZ=0 EndX=131.505 EndY=-2.92238 EndZ=0
    g97: LineSegment StartX=131.505 StartY=-13.4224 StartZ=0 EndX=131.505 EndY=-9.42238 EndZ=0
    g98: LineSegment StartX=157.005 StartY=-6.42238 StartZ=0 EndX=157.005 EndY=-2.92238 EndZ=0
    g99: LineSegment StartX=197.505 StartY=-6.58244 StartZ=0 EndX=197.505 EndY=-3.01371 EndZ=0
    g100: LineSegment StartX=197.505 StartY=-13.4224 StartZ=0 EndX=197.505 EndY=-9.42238 EndZ=0
    g101: LineSegment StartX=157.005 StartY=-13.4224 StartZ=0 EndX=157.005 EndY=-9.42238 EndZ=0
  constraints (226):
    c: Coincident(g0,g1)
    c: Coincident(g2,g3)
    c: Coincident(g3,g0)
    c: Horizontal(g1)
    c: Horizontal(g3)
    c: Vertical(g0)
    c: Vertical(g2)
    c: Horizontal(g5)
    c: Coincident(g6,g5)
    c: Vertical(g6)
    c: Coincident(g7,g8)
    c: Coincident(g8,g9)
    c: Coincident(g9,g10)
    c: Coincident(g10,g7)
    c: Horizontal(g8)
    c: Horizontal(g10)
    c: Vertical(g7)
    c: Vertical(g9)
    c: Symmetric(g8,g7,g11)
    c: DistanceY(g0,g0) = 17
    c: DistanceY(g7,g7) = 17
    c: Horizontal(g11,g4)
    c: Coincident(g88,g13)
    c: Coincident(g93,g14)
    c: Coincident(g95,g15)
    c: Coincident(g94,g12)
    c: Horizontal(g13)
    c: Horizontal(g15)
    c: Vertical(g12)
    c: Vertical(g14)
    c: Symmetric(g93,g12,g16)
    c: DistanceY(g88,g12) = 17
    c: DistanceX(g94,g15) = 17
    c: Horizontal(g16,g11)
    c: DistanceX(g2,g7) = 3
    c: DistanceX(g9,g12) = 3
    c: DistanceX(g10,g10) = 2.5
    c: DistanceY(g93,g90) = 2
    c: DistanceY(g91,g12) = 2
    c: DistanceX(g12,g17) = 2
    c: DistanceX(g18,g93) = 2
    c: DistanceX(g88,g92) = 2
    c: DistanceY(g88,g19) = 2
    c: DistanceY(g20,g95) = 2
    c: DistanceX(g89,g95) = 2
    c: Coincident(g25,g26)
    c: Coincident(g26,g27)
    c: Coincident(g96,g28)
    c: Coincident(g28,g25)
    c: Horizontal(g26)
    c: Horizontal(g28)
    c: Vertical(g25)
    c: Vertical(g27)
    c: Symmetric(g26,g25,g29)
    c: Horizontal(g29,g16)
    c: DistanceY(g25,g25) = 17
    c: DistanceX(g95,g25) = 3
    c: DistanceX(g3,g3) = 10
    c: Horizontal(g30)
    c: Coincident(g31,g30)
    c: Vertical(g31)
    c: Coincident(g32,g31)
    c: Horizontal(g32)
    c: Horizontal(g33)
    c: Coincident(g34,g33)
    c: Vertical(g34)
    c: Coincident(g35,g34)
    c: Horizontal(g35)
    c: Vertical(g33,g31)
    c: DistanceY(g31,g31) = 3
    c: Equal(g31,g34)
    c: Horizontal(g36,g29)
    c: Symmetric(g30,g35,g36)
    c: Coincident(g37,g38)
    c: Coincident(g38,g39)
    c: Coincident(g40,g37)
    c: Horizontal(g38)
    c: Horizontal(g40)
    c: Vertical(g37)
    c: Vertical(g39)
    c: Symmetric(g38,g37,g41)
    c: DistanceX(g28,g28) = 10.5
    c: DistanceX(g96,g37) = 3
    c: Horizontal(g41,g29)
    c: DistanceY(g37,g37) = 17
    c: Vertical(g42)
    c: Coincident(g43,g42)
    c: Horizontal(g43)
    c: Coincident(g44,g45)
    c: Coincident(g45,g46)
    c: Coincident(g98,g47)
    c: Coincident(g47,g44)
    c: Horizontal(g45)
    c: Horizontal(g47)
    c: Vertical(g44)
    c: Vertical(g46)
    c: Symmetric(g45,g44,g48)
    c: Equal(g25,g44) = 17
    c: Horizontal(g49)
    c: Coincident(g50,g49)
    c: Vertical(g50)
    c: Coincident(g51,g50)
    c: Horizontal(g51)
    c: Horizontal(g52)
    c: Coincident(g53,g52)
    c: Vertical(g53)
    c: Coincident(g54,g53)
    c: Horizontal(g54)
    c: Vertical(g52,g50)
    c: Equal(g31,g50) = 3
    c: Equal(g50,g53)
    c: Horizontal(g55,g48)
    c: Symmetric(g49,g54,g55)
    c: Equal(g28,g47) = 10.5
    c: DistanceY(g33,g36) = 2
    c: DistanceY(g52,g55) = 2
    c: DistanceX(g30,g30) = 7
    c: DistanceX(g49,g49) = 7
    c: Coincident(g58,g59)
    c: Coincident(g59,g56)
    c: Horizontal(g57)
    c: Horizontal(g59)
    c: Vertical(g56)
    c: Vertical(g58)
    c: Horizontal(g60,g48)
    c: DistanceX(g98,g56) = 3
    c: Coincident(g61,g62)
    c: Coincident(g62,g63)
    c: Coincident(g99,g64)
    c: Coincident(g64,g61)
    c: Horizontal(g62)
    c: Horizontal(g64)
    c: Vertical(g61)
    c: Vertical(g63)
    c: Symmetric(g62,g61,g65)
    c: Horizontal(g66)
    c: Coincident(g67,g66)
    c: Vertical(g67)
    c: Coincident(g68,g67)
    c: Horizontal(g68)
    c: Horizontal(g69)
    c: Coincident(g70,g69)
    c: Vertical(g70)
    c: Coincident(g71,g70)
    c: Horizontal(g71)
    c: Vertical(g69,g67)
    c: Equal(g67,g70)
    c: Horizontal(g72,g65)
    c: Symmetric(g66,g71,g72)
    c: DistanceY(g69,g72) = 2
    c: Equal(g49,g66) = 7
    c: DistanceX(g64,g64) = 10.5
    c: DistanceX(g59,g59) = 10.5
    c: Vertical(g73)
    c: Vertical(g74)
    c: Symmetric(g73,g74,g75)
    c: Vertical(g75,g60)
    c: Horizontal(g73,g74)
    c: DistanceX(g73,g74) = 3
    c: Coincident(g76,g73)
    c: Horizontal(g76)
    c: DistanceY(g76,g56) = 3
    c: Coincident(g77,g74)
    c: Horizontal(g77)
    c: Coincident(g80,g81)
    c: Coincident(g81,g78)
    c: Horizontal(g79)
    c: Horizontal(g81)
    c: Vertical(g78)
    c: Vertical(g80)
    c: Equal(g59,g81) = 10.5
    c: Vertical(g83)
    c: Vertical(g84)
    c: Symmetric(g83,g84,g85)
    c: Vertical(g85,g82)
    c: Horizontal(g83,g84)
    c: DistanceX(g83,g84) = 3
    c: Coincident(g86,g83)
    c: Horizontal(g86)
    c: DistanceY(g86,g78) = 3
    c: Coincident(g87,g84)
    c: Horizontal(g87)
    c: Horizontal(g60,g82)
    c: Horizontal(g82,g65)
    c: DistanceX(g58,g78) = 3
    c: DistanceX(g80,g61) = 3
    c: Coincident(g2,g5)
    c: Coincident(g1,g6)
    c: Coincident(g12,g91)
    c: Coincident(g88,g19)
    c: Coincident(g17,g89)
    c: Coincident(g91,g19)
    c: Coincident(g20,g90)
    c: Coincident(g92,g18)
    c: Coincident(g13,g92)
    c: Coincident(g93,g18)
    c: Coincident(g15,g89)
    c: Coincident(g94,g17)
    c: Coincident(g14,g90)
    c: Coincident(g95,g20)
    c: Coincident(g97,g32)
    c: Coincident(g96,g30)
    c: Coincident(g27,g35)
    c: Coincident(g97,g33)
    c: Coincident(g39,g43)
    c: Coincident(g40,g42)
    c: Coincident(g101,g51)
    c: Coincident(g98,g49)
    c: Coincident(g56,g76)
    c: Coincident(g57,g73)
    c: Coincident(g58,g77)
    c: Coincident(g78,g86)
    c: Coincident(g79,g83)
    c: Coincident(g80,g87)
    c: Coincident(g79,g84)
    c: Coincident(g100,g68)
    c: Coincident(g99,g66)
    c: Coincident(g63,g71)
    c: Coincident(g100,g69)
    c: Coincident(g57,g74)
    c: Coincident(g20,g24)
    c: Coincident(g17,g21)
    c: Coincident(g19,g22)
    c: Coincident(g18,g23)
    c: Coincident(g46,g54)
    c: Coincident(g101,g52)
FEATURE [Sketcher::SketchObject] Sketch040  label="Sketch039"
  AttachmentOffset = pos=(0,0,6) rot=(0,0,1;0rad)
  FullyConstrained = false
  MapMode = 5
  Placement = pos=(0,0,6) rot=(0,0,1;0rad)
  Support = -> [XY_Plane204]
  sketch-geometry (93):
    g0: LineSegment StartX=82.505 StartY=-2.92238 StartZ=0 EndX=82.505 EndY=-19.9224 EndZ=0
    g1: LineSegment StartX=82.505 StartY=-19.9224 StartZ=0 EndX=92.505 EndY=-19.9224 EndZ=0
    g2: LineSegment StartX=92.505 StartY=-19.9224 StartZ=0 EndX=92.505 EndY=-2.92238 EndZ=0
    g3: LineSegment StartX=92.505 StartY=-2.92238 StartZ=0 EndX=82.505 EndY=-2.92238 EndZ=0
    g4: GeomPoint X=87.505 Y=-11.4224 Z=0
    g5: LineSegment StartX=92.505 StartY=-11.435 StartZ=0 EndX=87.4677 EndY=-11.435 EndZ=0
    g6: LineSegment StartX=87.4677 StartY=-11.435 StartZ=0 EndX=87.4677 EndY=-19.9224 EndZ=0
    g7: LineSegment StartX=95.505 StartY=-2.92238 StartZ=0 EndX=95.505 EndY=-19.9224 EndZ=0
    g8: LineSegment StartX=95.505 StartY=-19.9224 StartZ=0 EndX=98.005 EndY=-19.9224 EndZ=0
    g9: LineSegment StartX=98.005 StartY=-19.9224 StartZ=0 EndX=98.005 EndY=-2.92238 EndZ=0
    g10: LineSegment StartX=98.005 StartY=-2.92238 StartZ=0 EndX=95.505 EndY=-2.92238 EndZ=0
    g11: GeomPoint X=96.755 Y=-11.4224 Z=0
    g12: LineSegment StartX=101.005 StartY=-2.92238 StartZ=0 EndX=101.005 EndY=-19.9224 EndZ=0
    g13: LineSegment StartX=101.005 StartY=-19.9224 StartZ=0 EndX=118.005 EndY=-19.9224 EndZ=0
    g14: LineSegment StartX=118.005 StartY=-19.9224 StartZ=0 EndX=118.005 EndY=-2.92238 EndZ=0
    g15: LineSegment StartX=118.005 StartY=-2.92238 StartZ=0 EndX=101.005 EndY=-2.92238 EndZ=0
    g16: GeomPoint X=109.505 Y=-11.4224 Z=0
    g17: LineSegment StartX=103.005 StartY=-2.92238 StartZ=0 EndX=118.005 EndY=-17.9224 EndZ=0
    g18: LineSegment StartX=116.005 StartY=-19.9224 StartZ=0 EndX=101.005 EndY=-4.92238 EndZ=0
    g19: LineSegment StartX=101.005 StartY=-17.9224 StartZ=0 EndX=116.005 EndY=-2.92238 EndZ=0
    g20: LineSegment StartX=118.005 StartY=-4.92238 StartZ=0 EndX=103.005 EndY=-19.9224 EndZ=0
    g21: GeomPoint X=109.505 Y=-9.42238 Z=0
    g22: GeomPoint X=107.505 Y=-11.4224 Z=0
    g23: GeomPoint X=109.505 Y=-13.4224 Z=0
    g24: GeomPoint X=111.505 Y=-11.4224 Z=0
    g25: LineSegment StartX=84.8786 StartY=-5.02645 StartZ=0 EndX=84.8786 EndY=-9.28184 EndZ=0
    g26: LineSegment StartX=84.8786 StartY=-9.28184 StartZ=0 EndX=90.0567 EndY=-9.28184 EndZ=0
    g27: LineSegment StartX=90.0567 StartY=-9.28184 StartZ=0 EndX=90.0567 EndY=-5.02645 EndZ=0
    g28: LineSegment StartX=90.0567 StartY=-5.02645 StartZ=0 EndX=84.8786 EndY=-5.02645 EndZ=0
    g29: GeomPoint X=87.4677 Y=-7.15415 Z=0
    g30: LineSegment StartX=121.005 StartY=-2.92238 StartZ=0 EndX=121.005 EndY=-19.9224 EndZ=0
    g31: LineSegment StartX=121.005 StartY=-19.9224 StartZ=0 EndX=131.505 EndY=-19.9224 EndZ=0
    g32: LineSegment StartX=131.505 StartY=-19.9224 StartZ=0 EndX=131.505 EndY=-2.92238 EndZ=0
    g33: LineSegment StartX=131.505 StartY=-2.92238 StartZ=0 EndX=121.005 EndY=-2.92238 EndZ=0
    g34: GeomPoint X=126.255 Y=-11.4224 Z=0
    g35: LineSegment StartX=131.505 StartY=-6.42238 StartZ=0 EndX=124.505 EndY=-6.42238 EndZ=0
    g36: LineSegment StartX=124.505 StartY=-6.42238 StartZ=0 EndX=124.505 EndY=-9.42238 EndZ=0
    g37: LineSegment StartX=124.505 StartY=-9.42238 StartZ=0 EndX=131.505 EndY=-9.42238 EndZ=0
    g38: LineSegment StartX=131.505 StartY=-13.4224 StartZ=0 EndX=124.505 EndY=-13.4224 EndZ=0
    g39: LineSegment StartX=124.505 StartY=-13.4224 StartZ=0 EndX=124.505 EndY=-16.4224 EndZ=0
    g40: LineSegment StartX=124.505 StartY=-16.4224 StartZ=0 EndX=131.505 EndY=-16.4224 EndZ=0
    g41: GeomPoint X=131.505 Y=-11.4224 Z=0
    g42: LineSegment StartX=134.505 StartY=-2.92238 StartZ=0 EndX=134.505 EndY=-19.9224 EndZ=0
    g43: LineSegment StartX=134.505 StartY=-19.9224 StartZ=0 EndX=143.505 EndY=-19.9224 EndZ=0
    g44: LineSegment StartX=143.505 StartY=-19.9224 StartZ=0 EndX=143.505 EndY=-2.92238 EndZ=0
    g45: LineSegment StartX=143.505 StartY=-2.92238 StartZ=0 EndX=134.505 EndY=-2.92238 EndZ=0
    g46: GeomPoint X=139.005 Y=-11.4224 Z=0
    g47: LineSegment StartX=137.187 StartY=-2.92238 StartZ=0 EndX=137.187 EndY=-16.5523 EndZ=0
    g48: LineSegment StartX=137.187 StartY=-16.5523 StartZ=0 EndX=143.505 EndY=-16.5523 EndZ=0
    g49: LineSegment StartX=146.505 StartY=-2.92238 StartZ=0 EndX=146.505 EndY=-19.9224 EndZ=0
    g50: LineSegment StartX=146.505 StartY=-19.9224 StartZ=0 EndX=157.005 EndY=-19.9224 EndZ=0
    g51: LineSegment StartX=157.005 StartY=-19.9224 StartZ=0 EndX=157.005 EndY=-2.92238 EndZ=0
    g52: LineSegment StartX=157.005 StartY=-2.92238 StartZ=0 EndX=146.505 EndY=-2.92238 EndZ=0
    g53: GeomPoint X=151.755 Y=-11.4224 Z=0
    g54: LineSegment StartX=157.005 StartY=-6.42238 StartZ=0 EndX=150.005 EndY=-6.42238 EndZ=0
    g55: LineSegment StartX=150.005 StartY=-6.42238 StartZ=0 EndX=150.005 EndY=-9.42238 EndZ=0
    g56: LineSegment StartX=150.005 StartY=-9.42238 StartZ=0 EndX=157.005 EndY=-9.42238 EndZ=0
    g57: LineSegment StartX=157.005 StartY=-13.4224 StartZ=0 EndX=150.005 EndY=-13.4224 EndZ=0
    g58: LineSegment StartX=150.005 StartY=-13.4224 StartZ=0 EndX=150.005 EndY=-16.4224 EndZ=0
    g59: LineSegment StartX=150.005 StartY=-16.4224 StartZ=0 EndX=157.005 EndY=-16.4224 EndZ=0
    g60: GeomPoint X=157.005 Y=-11.4224 Z=0
    g61: LineSegment StartX=160.005 StartY=-2.92238 StartZ=0 EndX=160.005 EndY=-19.9224 EndZ=0
    g62: LineSegment StartX=160.005 StartY=-19.9224 StartZ=0 EndX=170.505 EndY=-19.9224 EndZ=0
    g63: LineSegment StartX=170.505 StartY=-19.9224 StartZ=0 EndX=170.505 EndY=-2.92238 EndZ=0
    g64: LineSegment StartX=170.505 StartY=-2.92238 StartZ=0 EndX=160.005 EndY=-2.92238 EndZ=0
    g65: GeomPoint X=165.255 Y=-11.4224 Z=0
    g66: LineSegment StartX=187.005 StartY=-3.01371 StartZ=0 EndX=187.005 EndY=-19.831 EndZ=0
    g67: LineSegment StartX=187.005 StartY=-19.831 StartZ=0 EndX=197.505 EndY=-19.831 EndZ=0
    g68: LineSegment StartX=197.505 StartY=-19.831 StartZ=0 EndX=197.505 EndY=-3.01371 EndZ=0
    g69: LineSegment StartX=197.505 StartY=-3.01371 StartZ=0 EndX=187.005 EndY=-3.01371 EndZ=0
    g70: GeomPoint X=192.255 Y=-11.4224 Z=0
    g71: LineSegment StartX=197.505 StartY=-6.58244 StartZ=0 EndX=190.505 EndY=-6.58244 EndZ=0
    g72: LineSegment StartX=190.505 StartY=-6.58244 StartZ=0 EndX=190.505 EndY=-9.42238 EndZ=0
    g73: LineSegment StartX=190.505 StartY=-9.42238 StartZ=0 EndX=197.505 EndY=-9.42238 EndZ=0
    g74: LineSegment StartX=197.505 StartY=-13.4224 StartZ=0 EndX=190.505 EndY=-13.4224 EndZ=0
    g75: LineSegment StartX=190.505 StartY=-13.4224 StartZ=0 EndX=190.505 EndY=-16.2623 EndZ=0
    g76: LineSegment StartX=190.505 StartY=-16.2623 StartZ=0 EndX=197.505 EndY=-16.2623 EndZ=0
    g77: GeomPoint X=197.505 Y=-11.4224 Z=0
    g78: LineSegment StartX=163.755 StartY=-19.9224 StartZ=0 EndX=163.755 EndY=-5.92238 EndZ=0
    g79: LineSegment StartX=166.755 StartY=-19.9224 StartZ=0 EndX=166.755 EndY=-5.92238 EndZ=0
    g80: GeomPoint X=165.255 Y=-19.9224 Z=0
    g81: LineSegment StartX=163.755 StartY=-5.92238 StartZ=0 EndX=160.005 EndY=-5.92238 EndZ=0
    g82: LineSegment StartX=166.755 StartY=-5.92238 StartZ=0 EndX=170.505 EndY=-5.92238 EndZ=0
    g83: LineSegment StartX=173.505 StartY=-2.92238 StartZ=0 EndX=173.505 EndY=-19.9224 EndZ=0
    g84: LineSegment StartX=173.505 StartY=-19.9224 StartZ=0 EndX=184.005 EndY=-19.9224 EndZ=0
    g85: LineSegment StartX=184.005 StartY=-19.9224 StartZ=0 EndX=184.005 EndY=-2.92238 EndZ=0
    g86: LineSegment StartX=184.005 StartY=-2.92238 StartZ=0 EndX=173.505 EndY=-2.92238 EndZ=0
    g87: GeomPoint X=178.755 Y=-11.4224 Z=0
    g88: LineSegment StartX=177.255 StartY=-19.9224 StartZ=0 EndX=177.255 EndY=-5.92238 EndZ=0
    g89: LineSegment StartX=180.255 StartY=-19.9224 StartZ=0 EndX=180.255 EndY=-5.92238 EndZ=0
    g90: GeomPoint X=178.755 Y=-19.9224 Z=0
    g91: LineSegment StartX=177.255 StartY=-5.92238 StartZ=0 EndX=173.505 EndY=-5.92238 EndZ=0
    g92: LineSegment StartX=180.255 StartY=-5.92238 StartZ=0 EndX=184.005 EndY=-5.92238 EndZ=0
  constraints (250):
    c: Coincident(g0,g1)
    c: Coincident(g1,g2)
    c: Coincident(g2,g3)
    c: Coincident(g3,g0)
    c: Horizontal(g1)
    c: Horizontal(g3)
    c: Vertical(g0)
    c: Vertical(g2)
    c: Symmetric(g1,g0,g4)
    c: PointOnObject(g5,g2)
    c: Horizontal(g5)
    c: Coincident(g6,g5)
    c: PointOnObject(g6,g1)
    c: Vertical(g6)
    c: Coincident(g7,g8)
    c: Coincident(g8,g9)
    c: Coincident(g9,g10)
    c: Coincident(g10,g7)
    c: Horizontal(g8)
    c: Horizontal(g10)
    c: Vertical(g7)
    c: Vertical(g9)
    c: Symmetric(g8,g7,g11)
    c: DistanceY(g0,g0) = 17
    c: DistanceY(g7,g7) = 17
    c: Horizontal(g11,g4)
    c: Coincident(g12,g13)
    c: Coincident(g13,g14)
    c: Coincident(g14,g15)
    c: Coincident(g15,g12)
    c: Horizontal(g13)
    c: Horizontal(g15)
    c: Vertical(g12)
    c: Vertical(g14)
    c: Symmetric(g13,g12,g16)
    c: DistanceY(g12,g12) = 17
    c: DistanceX(g15,g15) = 17
    c: Horizontal(g16,g11)
    c: DistanceX(g2,g7) = 3
    c: DistanceX(g9,g12) = 3
    c: DistanceX(g10,g10) = 2.5
    c: PointOnObject(g17,g15)
    c: PointOnObject(g17,g14)
    c: PointOnObject(g18,g13)
    c: PointOnObject(g18,g12)
    c: DistanceY(g13,g17) = 2
    c: DistanceY(g18,g12) = 2
    c: DistanceX(g12,g17) = 2
    c: DistanceX(g18,g13) = 2
    c: PointOnObject(g19,g12)
    c: PointOnObject(g19,g15)
    c: PointOnObject(g20,g14)
    c: PointOnObject(g20,g13)
    c: DistanceX(g12,g20) = 2
    c: DistanceY(g12,g19) = 2
    c: DistanceY(g20,g14) = 2
    c: DistanceX(g19,g14) = 2
    c: PointOnObject(g21,g19)
    c: PointOnObject(g22,g19)
    c: PointOnObject(g23,g20)
    c: PointOnObject(g24,g20)
    c: PointOnObject(g24,g17)
    c: PointOnObject(g21,g17)
    c: PointOnObject(g22,g18)
    c: PointOnObject(g23,g18)
    c: Coincident(g25,g26)
    c: Coincident(g26,g27)
    c: Coincident(g27,g28)
    c: Coincident(g28,g25)
    c: Horizontal(g26)
    c: Horizontal(g28)
    c: Vertical(g25)
    c: Vertical(g27)
    c: Symmetric(g26,g25,g29)
    c: Vertical(g5,g29)
    c: Coincident(g30,g31)
    c: Coincident(g31,g32)
    c: Coincident(g32,g33)
    c: Coincident(g33,g30)
    c: Horizontal(g31)
    c: Horizontal(g33)
    c: Vertical(g30)
    c: Vertical(g32)
    c: Symmetric(g31,g30,g34)
    c: Horizontal(g34,g16)
    c: DistanceY(g30,g30) = 17
    c: DistanceX(g14,g30) = 3
    c: DistanceX(g3,g3) = 10
    c: PointOnObject(g35,g32)
    c: Horizontal(g35)
    c: Coincident(g36,g35)
    c: Vertical(g36)
    c: Coincident(g37,g36)
    c: PointOnObject(g37,g32)
    c: Horizontal(g37)
    c: PointOnObject(g38,g32)
    c: Horizontal(g38)
    c: Coincident(g39,g38)
    c: Vertical(g39)
    c: Coincident(g40,g39)
    c: PointOnObject(g40,g32)
    c: Horizontal(g40)
    c: Vertical(g38,g36)
    c: DistanceY(g36,g36) = 3
    c: Equal(g36,g39)
    c: Horizontal(g41,g34)
    c: Symmetric(g35,g40,g41)
    c: Coincident(g42,g43)
    c: Coincident(g43,g44)
    c: Coincident(g44,g45)
    c: Coincident(g45,g42)
    c: Horizontal(g43)
    c: Horizontal(g45)
    c: Vertical(g42)
    c: Vertical(g44)
    c: Symmetric(g43,g42,g46)
    c: DistanceX(g33,g33) = 10.5
    c: DistanceX(g32,g42) = 3
    c: Horizontal(g46,g34)
    c: DistanceY(g42,g42) = 17
    c: PointOnObject(g47,g45)
    c: Vertical(g47)
    c: Coincident(g48,g47)
    c: PointOnObject(g48,g44)
    c: Horizontal(g48)
    c: Coincident(g49,g50)
    c: Coincident(g50,g51)
    c: Coincident(g51,g52)
    c: Coincident(g52,g49)
    c: Horizontal(g50)
    c: Horizontal(g52)
    c: Vertical(g49)
    c: Vertical(g51)
    c: Symmetric(g50,g49,g53)
    c: Equal(g30,g49) = 17
    c: PointOnObject(g54,g51)
    c: Horizontal(g54)
    c: Coincident(g55,g54)
    c: Vertical(g55)
    c: Coincident(g56,g55)
    c: PointOnObject(g56,g51)
    c: Horizontal(g56)
    c: PointOnObject(g57,g51)
    c: Horizontal(g57)
    c: Coincident(g58,g57)
    c: Vertical(g58)
    c: Coincident(g59,g58)
    c: PointOnObject(g59,g51)
    c: Horizontal(g59)
    c: Vertical(g57,g55)
    c: Equal(g36,g55) = 3
    c: Equal(g55,g58)
    c: Horizontal(g60,g53)
    c: Symmetric(g54,g59,g60)
    c: Equal(g33,g52) = 10.5
    c: DistanceY(g38,g41) = 2
    c: DistanceY(g57,g60) = 2
    c: DistanceX(g35,g35) = 7
    c: DistanceX(g54,g54) = 7
    c: Horizontal(g44,g49)
    c: DistanceX(g44,g49) = 3
    c: DistanceX(g45,g45) = 9
    c: Coincident(g61,g62)
    c: Coincident(g62,g63)
    c: Coincident(g63,g64)
    c: Coincident(g64,g61)
    c: Horizontal(g62)
    c: Horizontal(g64)
    c: Vertical(g61)
    c: Vertical(g63)
    c: Symmetric(g62,g61,g65)
    c: DistanceY(g61,g61) = 17
    c: Horizontal(g65,g53)
    c: DistanceX(g51,g61) = 3
    c: Coincident(g66,g67)
    c: Coincident(g67,g68)
    c: Coincident(g68,g69)
    c: Coincident(g69,g66)
    c: Horizontal(g67)
    c: Horizontal(g69)
    c: Vertical(g66)
    c: Vertical(g68)
    c: Symmetric(g67,g66,g70)
    c: PointOnObject(g71,g68)
    c: Horizontal(g71)
    c: Coincident(g72,g71)
    c: Vertical(g72)
    c: Coincident(g73,g72)
    c: PointOnObject(g73,g68)
    c: Horizontal(g73)
    c: PointOnObject(g74,g68)
    c: Horizontal(g74)
    c: Coincident(g75,g74)
    c: Vertical(g75)
    c: Coincident(g76,g75)
    c: PointOnObject(g76,g68)
    c: Horizontal(g76)
    c: Vertical(g74,g72)
    c: Equal(g72,g75)
    c: Horizontal(g77,g70)
    c: Symmetric(g71,g76,g77)
    c: DistanceY(g74,g77) = 2
    c: Equal(g54,g71) = 7
    c: DistanceX(g69,g69) = 10.5
    c: DistanceX(g64,g64) = 10.5
    c: PointOnObject(g78,g62)
    c: Vertical(g78)
    c: PointOnObject(g79,g62)
    c: Vertical(g79)
    c: Symmetric(g78,g79,g80)
    c: Vertical(g80,g65)
    c: Horizontal(g78,g79)
    c: DistanceX(g78,g79) = 3
    c: Coincident(g81,g78)
    c: PointOnObject(g81,g61)
    c: Horizontal(g81)
    c: DistanceY(g81,g61) = 3
    c: Coincident(g82,g79)
    c: PointOnObject(g82,g63)
    c: Horizontal(g82)
    c: Coincident(g83,g84)
    c: Coincident(g84,g85)
    c: Coincident(g85,g86)
    c: Coincident(g86,g83)
    c: Horizontal(g84)
    c: Horizontal(g86)
    c: Vertical(g83)
    c: Vertical(g85)
    c: Symmetric(g84,g83,g87)
    c: Equal(g61,g83) = 17
    c: Equal(g64,g86) = 10.5
    c: PointOnObject(g88,g84)
    c: Vertical(g88)
    c: PointOnObject(g89,g84)
    c: Vertical(g89)
    c: Symmetric(g88,g89,g90)
    c: Vertical(g90,g87)
    c: Horizontal(g88,g89)
    c: DistanceX(g88,g89) = 3
    c: Coincident(g91,g88)
    c: PointOnObject(g91,g83)
    c: Horizontal(g91)
    c: DistanceY(g91,g83) = 3
    c: Coincident(g92,g89)
    c: PointOnObject(g92,g85)
    c: Horizontal(g92)
    c: Horizontal(g65,g87)
    c: Horizontal(g87,g70)
    c: DistanceX(g63,g83) = 3
    c: DistanceX(g85,g66) = 3
FEATURE [PartDesign::Pocket] Pocket029
  BaseFeature = -> Pad008
  Direction = (0,0,1)
  Length = 10
  Length2 = 5
  Profile = -> Sketch039
  ReferenceAxis = -> Sketch039 [N_Axis]
  Type = 0
  UseCustomVector = true
FEATURE [Sketcher::SketchObject] Sketch041
  AttachmentOffset = pos=(0,0,2.9) rot=(0,0,1;0rad)
  FullyConstrained = false
  MapMode = 5
  Placement = pos=(0,0,2.9) rot=(0,0,1;0rad)
  Support = -> [XY_Plane204]
  expr: Constraints[0] = Spreadsheet.PCB_length / 2
  sketch-geometry (3):
    g0: Circle CenterX=6.32665 CenterY=-8.89817 CenterZ=0 NormalX=0 NormalY=0 NormalZ=1 AngleXU=0 Radius=4.05
    g1: Circle CenterX=346.098 CenterY=-8.89817 CenterZ=0 NormalX=0 NormalY=0 NormalZ=1 AngleXU=0 Radius=4.05
    g2: GeomPoint X=176.213 Y=-8.89817 Z=0
  constraints (5):
    c: DistanceX(g-1,g2) = 176.213
    c: Symmetric(g1,g0,g2)
    c: Equal(g1,g0)
    c: Diameter(g1) = 8.1
    c: Horizontal(g1,g0)
FEATURE [Sketcher::SketchObject] Sketch042
  AttachmentOffset = pos=(0,0,2.9) rot=(0,0,1;0rad)
  FullyConstrained = false
  MapMode = 5
  Placement = pos=(0,0,2.9) rot=(0,0,1;0rad)
  Support = -> [XY_Plane196]
  expr: Constraints[0] = Spreadsheet.PCB_length / 2
  sketch-geometry (3):
    g0: GeomPoint X=176.213 Y=-127.899 Z=0
    g1: Circle CenterX=5.01141 CenterY=-127.899 CenterZ=0 NormalX=0 NormalY=0 NormalZ=1 AngleXU=0 Radius=4.05
    g2: Circle CenterX=347.414 CenterY=-127.899 CenterZ=0 NormalX=0 NormalY=0 NormalZ=1 AngleXU=0 Radius=4.05
  constraints (5):
    c: DistanceX(g-1,g0) = 176.213
    c: Symmetric(g2,g1,g0)
    c: Equal(g2,g1)
    c: Diameter(g2) = 8.1
    c: Horizontal(g2,g1)
FEATURE [PartDesign::Pocket] Pocket031
  BaseFeature = -> Pocket027
  Direction = (0,0,1)
  Length = 1
  Length2 = 5
  Profile = -> Sketch042
  ReferenceAxis = -> Sketch042 [N_Axis]
  Type = 0
  UseCustomVector = true
FEATURE [PartDesign::Body] Body003  label="Bottom case"
  Group = -> [Sketch017,Pad003,Sketch035,Pocket027,Sketch036,Sketch042,Pocket031]
  Origin = -> Origin196
  Placement = pos=(0,0,-9) rot=(0,0,1;0rad)
  Tip = -> Pocket031
FEATURE [Sketcher::SketchObject] Sketch043
  AttachmentOffset = pos=(0,0,5) rot=(0,0,1;0rad)
  FullyConstrained = true
  MapMode = 5
  Placement = pos=(0,0,5) rot=(0,0,1;0rad)
  Support = -> [XY_Plane201]
  expr: Constraints[10] = Spreadsheet.u * 0.5
  expr: Constraints[4] = Spreadsheet.u
  expr: Constraints[5] = Spreadsheet.u
  expr: Constraints[6] = Spreadsheet.u
  expr: Constraints[9] = Spreadsheet.PCB_width - Spreadsheet.u * 0.75
  sketch-geometry (4):
    g0: Circle CenterX=9.525 CenterY=-105.663 CenterZ=0 NormalX=0 NormalY=0 NormalZ=1 AngleXU=0 Radius=3.25
    g1: Circle CenterX=28.575 CenterY=-105.663 CenterZ=0 NormalX=0 NormalY=0 NormalZ=1 AngleXU=0 Radius=3.25
    g2: Circle CenterX=28.575 CenterY=-124.713 CenterZ=0 NormalX=0 NormalY=0 NormalZ=1 AngleXU=0 Radius=3.25
    g3: Circle CenterX=9.525 CenterY=-124.713 CenterZ=0 NormalX=0 NormalY=0 NormalZ=1 AngleXU=0 Radius=3.25
  constraints (12):
    c: Equal(g0,g1)
    c: Equal(g1,g2)
    c: Equal(g2,g3)
    c: Diameter(g0) = 6.5
    c: DistanceX(g0,g1) = 19.05
    c: DistanceX(g3,g2) = 19.05
    c: DistanceY(g2,g1) = 19.05
    c: Horizontal(g0,g1)
    c: Horizontal(g3,g2)
    c: DistanceY(g3,g-1) = 124.713
    c: DistanceX(g-1,g3) = 9.525
    c: Vertical(g1,g2)
FEATURE [PartDesign::Pocket] Pocket032  label="button hols"
  BaseFeature = -> Pocket024
  Direction = (0,0,-1)
  Length = 5
  Length2 = 5
  Profile = -> Sketch043
  ReferenceAxis = -> Sketch043 [N_Axis]
  Type = 0
FEATURE [Sketcher::SketchObject] Sketch045
  AttachmentOffset = pos=(0,0,5) rot=(0,0,1;0rad)
  FullyConstrained = false
  MapMode = 5
  Placement = pos=(0,0,5) rot=(0,0,1;0rad)
  Support = -> [XY_Plane205]
  sketch-geometry (6):
    g0: Circle CenterX=9.525 CenterY=-105.663 CenterZ=0 NormalX=0 NormalY=0 NormalZ=1 AngleXU=0 Radius=3.2
    g1: LineSegment StartX=4.47364 StartY=-100.165 StartZ=0 EndX=4.47364 EndY=-111.16 EndZ=0
    g2: LineSegment StartX=4.47364 StartY=-111.16 StartZ=0 EndX=14.5764 EndY=-111.16 EndZ=0
    g3: LineSegment StartX=14.5764 StartY=-111.16 StartZ=0 EndX=14.5764 EndY=-100.165 EndZ=0
    g4: LineSegment StartX=14.5764 StartY=-100.165 StartZ=0 EndX=4.47364 EndY=-100.165 EndZ=0
    g5: GeomPoint X=9.525 Y=-105.662 Z=0
  constraints (10):
    c: Diameter(g0) = 6.4
    c: Coincident(g1,g2)
    c: Coincident(g2,g3)
    c: Coincident(g3,g4)
    c: Coincident(g4,g1)
    c: Horizontal(g2)
    c: Horizontal(g4)
    c: Vertical(g1)
    c: Vertical(g3)
    c: Symmetric(g2,g1,g5)
FEATURE [Sketcher::SketchObject] Sketch047
  AttachmentOffset = pos=(0,0,5) rot=(0,0,1;0rad)
  FullyConstrained = true
  MapMode = 5
  Placement = pos=(0,0,5) rot=(0,0,1;0rad)
  Support = -> [XY_Plane201]
  expr: Constraints[10] = Spreadsheet.screen_length + 1
  expr: Constraints[11] = Spreadsheet.PCB_width - Spreadsheet.u * 3.75 + Spreadsheet.screen_module_length / 2
  expr: Constraints[12] = Spreadsheet.u + Spreadsheet.screen_module_width / 2
  expr: Constraints[13] = 6.25 - 0.5
  expr: Constraints[14] = Spreadsheet.u
  expr: Constraints[9] = Spreadsheet.screen_width + 1
  sketch-geometry (6):
    g0: GeomPoint X=32.7 Y=-93.1625 Z=0
    g1: LineSegment StartX=7.2 StartY=-43.6925 StartZ=0 EndX=7.2 EndY=-87.4125 EndZ=0
    g2: LineSegment StartX=7.2 StartY=-87.4125 StartZ=0 EndX=30.9 EndY=-87.4125 EndZ=0
    g3: LineSegment StartX=30.9 StartY=-87.4125 StartZ=0 EndX=30.9 EndY=-43.6925 EndZ=0
    g4: LineSegment StartX=30.9 StartY=-43.6925 StartZ=0 EndX=7.2 EndY=-43.6925 EndZ=0
    g5: GeomPoint X=19.05 Y=-65.5525 Z=0
  constraints (15):
    c: Coincident(g1,g2)
    c: Coincident(g2,g3)
    c: Coincident(g3,g4)
    c: Coincident(g4,g1)
    c: Horizontal(g2)
    c: Horizontal(g4)
    c: Vertical(g1)
    c: Vertical(g3)
    c: Symmetric(g2,g1,g5)
    c: DistanceX(g4,g4) = 23.7
    c: DistanceY(g3,g3) = 43.72
    c: DistanceY(g0,g-1) = 93.1625
    c: DistanceX(g-1,g0) = 32.7
    c: DistanceY(g0,g2) = 5.75
    c: DistanceX(g-1,g5) = 19.05
FEATURE [PartDesign::Pocket] Pocket035
  AlongSketchNormal = false
  BaseFeature = -> Pocket032
  Direction = (0,0,-1)
  Length = 5
  Length2 = 5
  Profile = -> Sketch047
  ReferenceAxis = -> Sketch047 [N_Axis]
  Type = 0
  UseCustomVector = true
FEATURE [PartDesign::Body] Body006  label="clear top"
  Group = -> [Sketch027,Pad006,Sketch028,Pocket021,Sketch029,Pocket022,Sketch030,Pocket023,Sketch031,Pocket024,Sketch043,Pocket032,Sketch047,Pocket035]
  Origin = -> Origin201
  Placement = pos=(0,0,6.2) rot=(0,0,1;0rad)
  Tip = -> Pocket035
FEATURE [Sketcher::SketchObject] Sketch048
  AttachmentOffset = pos=(0,0,5) rot=(0,0,1;0rad)
  FullyConstrained = true
  MapMode = 5
  Placement = pos=(0,0,5) rot=(0,0,1;0rad)
  Support = -> [XY_Plane199]
  expr: Constraints[10] = Spreadsheet.u * 0.5
  expr: Constraints[4] = Spreadsheet.u
  expr: Constraints[5] = Spreadsheet.u
  expr: Constraints[6] = Spreadsheet.u
  expr: Constraints[9] = Spreadsheet.PCB_width - Spreadsheet.u * 0.75
  sketch-geometry (4):
    g0: Circle CenterX=9.525 CenterY=-105.663 CenterZ=0 NormalX=0 NormalY=0 NormalZ=1 AngleXU=0 Radius=4.25
    g1: Circle CenterX=28.575 CenterY=-105.663 CenterZ=0 NormalX=0 NormalY=0 NormalZ=1 AngleXU=0 Radius=4.25
    g2: Circle CenterX=28.575 CenterY=-124.713 CenterZ=0 NormalX=0 NormalY=0 NormalZ=1 AngleXU=0 Radius=4.25
    g3: Circle CenterX=9.525 CenterY=-124.713 CenterZ=0 NormalX=0 NormalY=0 NormalZ=1 AngleXU=0 Radius=4.25
  constraints (12):
    c: Equal(g0,g1)
    c: Equal(g1,g2)
    c: Equal(g2,g3)
    c: Diameter(g0) = 8.5
    c: DistanceX(g0,g1) = 19.05
    c: DistanceX(g3,g2) = 19.05
    c: DistanceY(g2,g1) = 19.05
    c: Horizontal(g0,g1)
    c: Horizontal(g3,g2)
    c: DistanceY(g3,g-1) = 124.713
    c: DistanceX(g-1,g3) = 9.525
    c: Vertical(g1,g2)
FEATURE [PartDesign::Pocket] Pocket036
  BaseFeature = -> Pocket026
  Direction = (0,0,-1)
  Length = 5
  Length2 = 5
  Profile = -> Sketch048
  ReferenceAxis = -> Sketch048 [N_Axis]
  Type = 0
FEATURE [PartDesign::Body] Body005  label="coloured top"
  Group = -> [Sketch021,Pad005,Sketch022,Pocket016,Sketch023,Pocket017,Sketch024,Pocket018,Sketch025,Pocket019,Sketch026,Pocket020,Sketch033,Pocket026,Sketch048,Pocket036]
  Origin = -> Origin199
  Placement = pos=(0,0,4.2) rot=(0,0,1;0rad)
  Tip = -> Pocket036
FEATURE [Sketcher::SketchObject] Sketch049
  FullyConstrained = false
  MapMode = 5
  Support = -> [XY_Plane205]
  sketch-geometry (1):
    g0: Circle CenterX=9.525 CenterY=-105.663 CenterZ=0 NormalX=0 NormalY=0 NormalZ=1 AngleXU=0 Radius=4.15
  constraints (1):
    c: Diameter(g0) = 8.3
FEATURE [Sketcher::SketchObject] Sketch046
  FullyConstrained = false
  MapMode = 5
  Support = -> [XY_Plane205]
  sketch-geometry (1):
    g0: Circle CenterX=9.525 CenterY=-105.663 CenterZ=0 NormalX=0 NormalY=0 NormalZ=1 AngleXU=0 Radius=2.25
  constraints (1):
    c: Diameter(g0) = 4.5
FEATURE [PartDesign::Pad] Pad009
  Direction = (0,0,1)
  Length = 5
  Length2 = 10
  Profile = -> Sketch049
  ReferenceAxis = -> Sketch049 [N_Axis]
  Type = 0
FEATURE [PartDesign::Pocket] Pocket037
  BaseFeature = -> Pad009
  Direction = (0,0,-1)
  Length = 3
  Length2 = 5
  Profile = -> Sketch045
  ReferenceAxis = -> Sketch045 [N_Axis]
  Type = 0
FEATURE [PartDesign::Pocket] Pocket038
  BaseFeature = -> Pocket037
  Direction = (0,0,1)
  Length = 3
  Length2 = 5
  Profile = -> Sketch046
  ReferenceAxis = -> Sketch046 [N_Axis]
  Type = 0
  UseCustomVector = true
FEATURE [PartDesign::Body] Body009  label="buttons"
  Group = -> [Sketch045,Sketch046,Sketch049,Pad009,Pocket037,Pocket038]
  Origin = -> Origin205
  Placement = pos=(0,0,7.1) rot=(0,0,1;0rad)
  Tip = -> Pocket038
FEATURE [Sketcher::SketchObject] Sketch050
  AttachmentOffset = pos=(0,0,5) rot=(0,0,1;0rad)
  FullyConstrained = false
  MapMode = 5
  Placement = pos=(0,0,5) rot=(0,0,1;0rad)
  Support = -> [XY_Plane206]
  sketch-geometry (6):
    g0: Circle CenterX=9.525 CenterY=-105.663 CenterZ=0 NormalX=0 NormalY=0 NormalZ=1 AngleXU=0 Radius=3.2
    g1: LineSegment StartX=4.47364 StartY=-100.165 StartZ=0 EndX=4.47364 EndY=-111.16 EndZ=0
    g2: LineSegment StartX=4.47364 StartY=-111.16 StartZ=0 EndX=14.5764 EndY=-111.16 EndZ=0
    g3: LineSegment StartX=14.5764 StartY=-111.16 StartZ=0 EndX=14.5764 EndY=-100.165 EndZ=0
    g4: LineSegment StartX=14.5764 StartY=-100.165 StartZ=0 EndX=4.47364 EndY=-100.165 EndZ=0
    g5: GeomPoint X=9.525 Y=-105.662 Z=0
  constraints (10):
    c: Diameter(g0) = 6.4
    c: Coincident(g1,g2)
    c: Coincident(g2,g3)
    c: Coincident(g3,g4)
    c: Coincident(g4,g1)
    c: Horizontal(g2)
    c: Horizontal(g4)
    c: Vertical(g1)
    c: Vertical(g3)
    c: Symmetric(g2,g1,g5)
FEATURE [Sketcher::SketchObject] Sketch051
  FullyConstrained = false
  MapMode = 5
  Support = -> [XY_Plane206]
  sketch-geometry (1):
    g0: Circle CenterX=9.525 CenterY=-105.663 CenterZ=0 NormalX=0 NormalY=0 NormalZ=1 AngleXU=0 Radius=2.25
  constraints (1):
    c: Diameter(g0) = 4.5
FEATURE [Sketcher::SketchObject] Sketch052
  FullyConstrained = false
  MapMode = 5
  Support = -> [XY_Plane206]
  sketch-geometry (1):
    g0: Circle CenterX=9.525 CenterY=-105.663 CenterZ=0 NormalX=0 NormalY=0 NormalZ=1 AngleXU=0 Radius=4.15
  constraints (1):
    c: Diameter(g0) = 8.3
FEATURE [PartDesign::Pad] Pad010
  Direction = (0,0,1)
  Length = 5
  Length2 = 10
  Profile = -> Sketch052
  ReferenceAxis = -> Sketch052 [N_Axis]
  Type = 0
FEATURE [PartDesign::Pocket] Pocket039
  BaseFeature = -> Pad010
  Direction = (0,0,-1)
  Length = 3
  Length2 = 5
  Profile = -> Sketch050
  ReferenceAxis = -> Sketch050 [N_Axis]
  Type = 0
FEATURE [PartDesign::Pocket] Pocket040
  BaseFeature = -> Pocket039
  Direction = (0,0,1)
  Length = 3
  Length2 = 5
  Profile = -> Sketch051
  ReferenceAxis = -> Sketch051 [N_Axis]
  Type = 0
  UseCustomVector = true
FEATURE [PartDesign::Body] Body010  label="buttons001"
  Group = -> [Sketch050,Sketch051,Sketch052,Pad010,Pocket039,Pocket040]
  Origin = -> Origin206
  Placement = pos=(0,-19.05,7.1) rot=(0,0,1;0rad)
  Tip = -> Pocket040
FEATURE [Sketcher::SketchObject] Sketch053
  AttachmentOffset = pos=(0,0,5) rot=(0,0,1;0rad)
  FullyConstrained = false
  MapMode = 5
  Placement = pos=(0,0,5) rot=(0,0,1;0rad)
  Support = -> [XY_Plane207]
  sketch-geometry (6):
    g0: Circle CenterX=9.525 CenterY=-105.663 CenterZ=0 NormalX=0 NormalY=0 NormalZ=1 AngleXU=0 Radius=3.2
    g1: LineSegment StartX=4.47364 StartY=-100.165 StartZ=0 EndX=4.47364 EndY=-111.16 EndZ=0
    g2: LineSegment StartX=4.47364 StartY=-111.16 StartZ=0 EndX=14.5764 EndY=-111.16 EndZ=0
    g3: LineSegment StartX=14.5764 StartY=-111.16 StartZ=0 EndX=14.5764 EndY=-100.165 EndZ=0
    g4: LineSegment StartX=14.5764 StartY=-100.165 StartZ=0 EndX=4.47364 EndY=-100.165 EndZ=0
    g5: GeomPoint X=9.525 Y=-105.662 Z=0
  constraints (10):
    c: Diameter(g0) = 6.4
    c: Coincident(g1,g2)
    c: Coincident(g2,g3)
    c: Coincident(g3,g4)
    c: Coincident(g4,g1)
    c: Horizontal(g2)
    c: Horizontal(g4)
    c: Vertical(g1)
    c: Vertical(g3)
    c: Symmetric(g2,g1,g5)
FEATURE [Sketcher::SketchObject] Sketch054
  FullyConstrained = false
  MapMode = 5
  Support = -> [XY_Plane207]
  sketch-geometry (1):
    g0: Circle CenterX=9.525 CenterY=-105.663 CenterZ=0 NormalX=0 NormalY=0 NormalZ=1 AngleXU=0 Radius=2.25
  constraints (1):
    c: Diameter(g0) = 4.5
FEATURE [Sketcher::SketchObject] Sketch055
  FullyConstrained = false
  MapMode = 5
  Support = -> [XY_Plane207]
  sketch-geometry (1):
    g0: Circle CenterX=9.525 CenterY=-105.663 CenterZ=0 NormalX=0 NormalY=0 NormalZ=1 AngleXU=0 Radius=4.15
  constraints (1):
    c: Diameter(g0) = 8.3
FEATURE [PartDesign::Pad] Pad011
  Direction = (0,0,1)
  Length = 5
  Length2 = 10
  Profile = -> Sketch055
  ReferenceAxis = -> Sketch055 [N_Axis]
  Type = 0
FEATURE [PartDesign::Pocket] Pocket041
  BaseFeature = -> Pad011
  Direction = (0,0,-1)
  Length = 3
  Length2 = 5
  Profile = -> Sketch053
  ReferenceAxis = -> Sketch053 [N_Axis]
  Type = 0
FEATURE [PartDesign::Pocket] Pocket042
  BaseFeature = -> Pocket041
  Direction = (0,0,1)
  Length = 3
  Length2 = 5
  Profile = -> Sketch054
  ReferenceAxis = -> Sketch054 [N_Axis]
  Type = 0
  UseCustomVector = true
FEATURE [PartDesign::Body] Body011  label="buttons002"
  Group = -> [Sketch053,Sketch054,Sketch055,Pad011,Pocket041,Pocket042]
  Origin = -> Origin207
  Placement = pos=(19.05,0,7.1) rot=(0,0,1;0rad)
  Tip = -> Pocket042
FEATURE [Sketcher::SketchObject] Sketch056
  AttachmentOffset = pos=(0,0,5) rot=(0,0,1;0rad)
  FullyConstrained = false
  MapMode = 5
  Placement = pos=(0,0,5) rot=(0,0,1;0rad)
  Support = -> [XY_Plane208]
  sketch-geometry (6):
    g0: Circle CenterX=9.525 CenterY=-105.663 CenterZ=0 NormalX=0 NormalY=0 NormalZ=1 AngleXU=0 Radius=3.2
    g1: LineSegment StartX=4.47364 StartY=-100.165 StartZ=0 EndX=4.47364 EndY=-111.16 EndZ=0
    g2: LineSegment StartX=4.47364 StartY=-111.16 StartZ=0 EndX=14.5764 EndY=-111.16 EndZ=0
    g3: LineSegment StartX=14.5764 StartY=-111.16 StartZ=0 EndX=14.5764 EndY=-100.165 EndZ=0
    g4: LineSegment StartX=14.5764 StartY=-100.165 StartZ=0 EndX=4.47364 EndY=-100.165 EndZ=0
    g5: GeomPoint X=9.525 Y=-105.662 Z=0
  constraints (10):
    c: Diameter(g0) = 6.4
    c: Coincident(g1,g2)
    c: Coincident(g2,g3)
    c: Coincident(g3,g4)
    c: Coincident(g4,g1)
    c: Horizontal(g2)
    c: Horizontal(g4)
    c: Vertical(g1)
    c: Vertical(g3)
    c: Symmetric(g2,g1,g5)
FEATURE [Sketcher::SketchObject] Sketch057
  FullyConstrained = false
  MapMode = 5
  Support = -> [XY_Plane208]
  sketch-geometry (1):
    g0: Circle CenterX=9.525 CenterY=-105.663 CenterZ=0 NormalX=0 NormalY=0 NormalZ=1 AngleXU=0 Radius=2.25
  constraints (1):
    c: Diameter(g0) = 4.5
FEATURE [Sketcher::SketchObject] Sketch058
  FullyConstrained = false
  MapMode = 5
  Support = -> [XY_Plane208]
  sketch-geometry (1):
    g0: Circle CenterX=9.525 CenterY=-105.663 CenterZ=0 NormalX=0 NormalY=0 NormalZ=1 AngleXU=0 Radius=4.15
  constraints (1):
    c: Diameter(g0) = 8.3
FEATURE [PartDesign::Pad] Pad012
  Direction = (0,0,1)
  Length = 5
  Length2 = 10
  Profile = -> Sketch058
  ReferenceAxis = -> Sketch058 [N_Axis]
  Type = 0
FEATURE [PartDesign::Pocket] Pocket043
  BaseFeature = -> Pad012
  Direction = (0,0,-1)
  Length = 3
  Length2 = 5
  Profile = -> Sketch056
  ReferenceAxis = -> Sketch056 [N_Axis]
  Type = 0
FEATURE [PartDesign::Pocket] Pocket044
  BaseFeature = -> Pocket043
  Direction = (0,0,1)
  Length = 3
  Length2 = 5
  Profile = -> Sketch057
  ReferenceAxis = -> Sketch057 [N_Axis]
  Type = 0
  UseCustomVector = true
FEATURE [PartDesign::Body] Body012  label="buttons003"
  Group = -> [Sketch056,Sketch057,Sketch058,Pad012,Pocket043,Pocket044]
  Origin = -> Origin208
  Placement = pos=(19.05,-19.05,7) rot=(0,0,1;0rad)
  Tip = -> Pocket044
FEATURE [TechDraw::DrawSVGTemplate] Template
  Height = 297
  Orientation = 1
  Width = 420
FEATURE [TechDraw::DrawSVGTemplate] Template001
  Height = 420
  Orientation = 1
  Width = 594
FEATURE [TechDraw::DrawViewPart] View003
  CoarseView = false
  Direction = (0,0,1)
  Focus = 100
  HardHidden = false
  IsoCount = 0
  IsoHidden = false
  IsoVisible = false
  LockPosition = false
  Perspective = false
  Rotation = 0
  ScaleType = 0
  SeamHidden = false
  SeamVisible = true
  SmoothHidden = false
  SmoothVisible = true
  Source = -> [Body004]
  X = 387.861
  XDirection = (0,1,0)
  Y = 236.395
FEATURE [TechDraw::DrawViewPart] View004
  CoarseView = false
  Direction = (0,0,1)
  Focus = 100
  HardHidden = false
  IsoCount = 0
  IsoHidden = false
  IsoVisible = false
  LockPosition = false
  Perspective = false
  Rotation = 0
  ScaleType = 0
  SeamHidden = false
  SeamVisible = true
  SmoothHidden = false
  SmoothVisible = true
  Source = -> [Body001]
  X = 233.801
  XDirection = (0,1,0)
  Y = 236.426
FEATURE [TechDraw::DrawViewPart] View005
  CoarseView = false
  Direction = (0,0,1)
  Focus = 100
  HardHidden = false
  IsoCount = 0
  IsoHidden = false
  IsoVisible = false
  LockPosition = false
  Perspective = false
  Rotation = 0
  ScaleType = 0
  SeamHidden = false
  SeamVisible = true
  SmoothHidden = false
  SmoothVisible = true
  Source = -> [Body002]
  X = 76.837
  XDirection = (0,1,0)
  Y = 236.404
FEATURE [TechDraw::DrawPage] Page001  label="Spacers"
  KeepUpdated = true
  NextBalloonIndex = 1
  ProjectionType = 0
  Template = -> Template001
  Views = -> [View003,View004,View005]
FEATURE [TechDraw::DrawSVGTemplate] Template002
  Height = 297
  Orientation = 1
  Width = 420
FEATURE [TechDraw::DrawSVGTemplate] Template003
  Height = 420
  Orientation = 1
  Width = 594
FEATURE [TechDraw::DrawSVGTemplate] Template005
  Height = 297
  Orientation = 1
  Width = 420
FEATURE [PartDesign::Fillet] Fillet
  Base = -> Pocket029 [Edge232,Edge227,Edge229,Edge234,Edge235,Edge230,Edge231,Edge228,Edge236,Edge233,Edge249,Edge248,Edge250,Edge251,Edge239,Edge237,Edge238,Edge252,Edge247,Edge246,Edge243,Edge244,Edge245,Edge242,Edge240,Edge241,Edge264,Edge254,Edge253,Edge256,Edge255,Edge257,Edge259,Edge260,Edge261,Edge262,Edge263,Edge258,Edge265,Edge270,+44 more]
  BaseFeature = -> Pocket029
  Radius = 0.5
  SupportTransform = false
  UseAllEdges = false
FEATURE [Sketcher::SketchObject] Sketch059
  AttachmentOffset = pos=(0,0,4.1) rot=(0,0,1;0rad)
  FullyConstrained = true
  MapMode = 5
  Placement = pos=(0,0,4.1) rot=(0,0,1;0rad)
  Support = -> [XY_Plane209]
  expr: .AttachmentOffset.Base.z = 4.1
  expr: Constraints[10] = Spreadsheet.PCB_width - Spreadsheet.u * 6
  expr: Constraints[11] = Spreadsheet.u * 2.5
  expr: Constraints[138] = Spreadsheet.u * 1.25
  expr: Constraints[153] = Spreadsheet.u
  expr: Constraints[154] = Spreadsheet.u
  expr: Constraints[155] = Spreadsheet.u
  expr: Constraints[156] = Spreadsheet.u
  expr: Constraints[157] = Spreadsheet.u
  expr: Constraints[158] = Spreadsheet.u
  expr: Constraints[159] = Spreadsheet.u
  expr: Constraints[160] = Spreadsheet.u
  expr: Constraints[161] = Spreadsheet.u
  expr: Constraints[162] = Spreadsheet.u * 1.25
  expr: Constraints[163] = Spreadsheet.u * 1.25
  expr: Constraints[164] = Spreadsheet.u * 1.25
  expr: Constraints[165] = Spreadsheet.u * 1.5
  expr: Constraints[9] = Spreadsheet.switch_hole + 0.2
  sketch-geometry (75):
    g0: LineSegment StartX=40.525 StartY=-17.6 StartZ=0 EndX=40.525 EndY=-31.8 EndZ=0
    g1: LineSegment StartX=40.525 StartY=-31.8 StartZ=0 EndX=54.725 EndY=-31.8 EndZ=0
    g2: LineSegment StartX=54.725 StartY=-31.8 StartZ=0 EndX=54.725 EndY=-17.6 EndZ=0
    g3: LineSegment StartX=54.725 StartY=-17.6 StartZ=0 EndX=40.525 EndY=-17.6 EndZ=0
    g4: GeomPoint X=47.625 Y=-24.7 Z=0
    g5: LineSegment StartX=64.3375 StartY=-17.6 StartZ=0 EndX=64.3375 EndY=-31.8 EndZ=0
    g6: LineSegment StartX=64.3375 StartY=-31.8 StartZ=0 EndX=78.5375 EndY=-31.8 EndZ=0
    g7: LineSegment StartX=78.5375 StartY=-31.8 StartZ=0 EndX=78.5375 EndY=-17.6 EndZ=0
    g8: LineSegment StartX=78.5375 StartY=-17.6 StartZ=0 EndX=64.3375 EndY=-17.6 EndZ=0
    g9: GeomPoint X=71.4375 Y=-24.7 Z=0
    g10: LineSegment StartX=83.3875 StartY=-17.6 StartZ=0 EndX=83.3875 EndY=-31.8 EndZ=0
    g11: LineSegment StartX=83.3875 StartY=-31.8 StartZ=0 EndX=97.5875 EndY=-31.8 EndZ=0
    g12: LineSegment StartX=97.5875 StartY=-31.8 StartZ=0 EndX=97.5875 EndY=-17.6 EndZ=0
    g13: LineSegment StartX=97.5875 StartY=-17.6 StartZ=0 EndX=83.3875 EndY=-17.6 EndZ=0
    g14: GeomPoint X=90.4875 Y=-24.7 Z=0
    g15: LineSegment StartX=102.437 StartY=-17.6 StartZ=0 EndX=102.437 EndY=-31.8 EndZ=0
    g16: LineSegment StartX=102.437 StartY=-31.8 StartZ=0 EndX=116.638 EndY=-31.8 EndZ=0
    g17: LineSegment StartX=116.638 StartY=-31.8 StartZ=0 EndX=116.638 EndY=-17.6 EndZ=0
    g18: LineSegment StartX=116.638 StartY=-17.6 StartZ=0 EndX=102.437 EndY=-17.6 EndZ=0
    g19: GeomPoint X=109.538 Y=-24.7 Z=0
    g20: LineSegment StartX=121.487 StartY=-17.6 StartZ=0 EndX=121.487 EndY=-31.8 EndZ=0
    g21: LineSegment StartX=121.487 StartY=-31.8 StartZ=0 EndX=135.688 EndY=-31.8 EndZ=0
    g22: LineSegment StartX=135.688 StartY=-31.8 StartZ=0 EndX=135.688 EndY=-17.6 EndZ=0
    g23: LineSegment StartX=135.688 StartY=-17.6 StartZ=0 EndX=121.487 EndY=-17.6 EndZ=0
    g24: GeomPoint X=128.588 Y=-24.7 Z=0
    g25: LineSegment StartX=145.3 StartY=-17.6 StartZ=0 EndX=145.3 EndY=-31.8 EndZ=0
    g26: LineSegment StartX=145.3 StartY=-31.8 StartZ=0 EndX=159.5 EndY=-31.8 EndZ=0
    g27: LineSegment StartX=159.5 StartY=-31.8 StartZ=0 EndX=159.5 EndY=-17.6 EndZ=0
    g28: LineSegment StartX=159.5 StartY=-17.6 StartZ=0 EndX=145.3 EndY=-17.6 EndZ=0
    g29: GeomPoint X=152.4 Y=-24.7 Z=0
    g30: LineSegment StartX=164.35 StartY=-17.6 StartZ=0 EndX=164.35 EndY=-31.8 EndZ=0
    g31: LineSegment StartX=164.35 StartY=-31.8 StartZ=0 EndX=178.55 EndY=-31.8 EndZ=0
    g32: LineSegment StartX=178.55 StartY=-31.8 StartZ=0 EndX=178.55 EndY=-17.6 EndZ=0
    g33: LineSegment StartX=178.55 StartY=-17.6 StartZ=0 EndX=164.35 EndY=-17.6 EndZ=0
    g34: GeomPoint X=171.45 Y=-24.7 Z=0
    g35: LineSegment StartX=183.4 StartY=-17.6 StartZ=0 EndX=183.4 EndY=-31.8 EndZ=0
    g36: LineSegment StartX=183.4 StartY=-31.8 StartZ=0 EndX=197.6 EndY=-31.8 EndZ=0
    g37: LineSegment StartX=197.6 StartY=-31.8 StartZ=0 EndX=197.6 EndY=-17.6 EndZ=0
    g38: LineSegment StartX=197.6 StartY=-17.6 StartZ=0 EndX=183.4 EndY=-17.6 EndZ=0
    g39: GeomPoint X=190.5 Y=-24.7 Z=0
    g40: LineSegment StartX=202.45 StartY=-17.6 StartZ=0 EndX=202.45 EndY=-31.8 EndZ=0
    g41: LineSegment StartX=202.45 StartY=-31.8 StartZ=0 EndX=216.65 EndY=-31.8 EndZ=0
    g42: LineSegment StartX=216.65 StartY=-31.8 StartZ=0 EndX=216.65 EndY=-17.6 EndZ=0
    g43: LineSegment StartX=216.65 StartY=-17.6 StartZ=0 EndX=202.45 EndY=-17.6 EndZ=0
    g44: GeomPoint X=209.55 Y=-24.7 Z=0
    g45: LineSegment StartX=226.262 StartY=-17.6 StartZ=0 EndX=226.262 EndY=-31.8 EndZ=0
    g46: LineSegment StartX=226.262 StartY=-31.8 StartZ=0 EndX=240.463 EndY=-31.8 EndZ=0
    g47: LineSegment StartX=240.463 StartY=-31.8 StartZ=0 EndX=240.463 EndY=-17.6 EndZ=0
    g48: LineSegment StartX=240.463 StartY=-17.6 StartZ=0 EndX=226.262 EndY=-17.6 EndZ=0
    g49: GeomPoint X=233.363 Y=-24.7 Z=0
    g50: LineSegment StartX=245.312 StartY=-17.6 StartZ=0 EndX=245.312 EndY=-31.8 EndZ=0
    g51: LineSegment StartX=245.312 StartY=-31.8 StartZ=0 EndX=259.513 EndY=-31.8 EndZ=0
    g52: LineSegment StartX=259.513 StartY=-31.8 StartZ=0 EndX=259.513 EndY=-17.6 EndZ=0
    g53: LineSegment StartX=259.513 StartY=-17.6 StartZ=0 EndX=245.312 EndY=-17.6 EndZ=0
    g54: GeomPoint X=252.412 Y=-24.7 Z=0
    g55: LineSegment StartX=264.362 StartY=-17.6 StartZ=0 EndX=264.362 EndY=-31.8 EndZ=0
    g56: LineSegment StartX=264.362 StartY=-31.8 StartZ=0 EndX=278.563 EndY=-31.8 EndZ=0
    g57: LineSegment StartX=278.563 StartY=-31.8 StartZ=0 EndX=278.563 EndY=-17.6 EndZ=0
    g58: LineSegment StartX=278.563 StartY=-17.6 StartZ=0 EndX=264.362 EndY=-17.6 EndZ=0
    g59: GeomPoint X=271.463 Y=-24.7 Z=0
    g60: LineSegment StartX=283.412 StartY=-17.6 StartZ=0 EndX=283.412 EndY=-31.8 EndZ=0
    g61: LineSegment StartX=283.412 StartY=-31.8 StartZ=0 EndX=297.613 EndY=-31.8 EndZ=0
    g62: LineSegment StartX=297.613 StartY=-31.8 StartZ=0 EndX=297.613 EndY=-17.6 EndZ=0
    g63: LineSegment StartX=297.613 StartY=-17.6 StartZ=0 EndX=283.412 EndY=-17.6 EndZ=0
    g64: GeomPoint X=290.512 Y=-24.7 Z=0
    g65: LineSegment StartX=307.225 StartY=-17.6 StartZ=0 EndX=307.225 EndY=-31.8 EndZ=0
    g66: LineSegment StartX=307.225 StartY=-31.8 StartZ=0 EndX=321.425 EndY=-31.8 EndZ=0
    g67: LineSegment StartX=321.425 StartY=-31.8 StartZ=0 EndX=321.425 EndY=-17.6 EndZ=0
    g68: LineSegment StartX=321.425 StartY=-17.6 StartZ=0 EndX=307.225 EndY=-17.6 EndZ=0
    g69: GeomPoint X=314.325 Y=-24.7 Z=0
    g70: LineSegment StartX=335.8 StartY=-17.6 StartZ=0 EndX=335.8 EndY=-31.8 EndZ=0
    g71: LineSegment StartX=335.8 StartY=-31.8 StartZ=0 EndX=350 EndY=-31.8 EndZ=0
    g72: LineSegment StartX=350 StartY=-31.8 StartZ=0 EndX=350 EndY=-17.6 EndZ=0
    g73: LineSegment StartX=350 StartY=-17.6 StartZ=0 EndX=335.8 EndY=-17.6 EndZ=0
    g74: GeomPoint X=342.9 Y=-24.7 Z=0
  constraints (195):
    c: Coincident(g0,g1)
    c: Coincident(g1,g2)
    c: Coincident(g2,g3)
    c: Coincident(g3,g0)
    c: Horizontal(g1)
    c: Horizontal(g3)
    c: Vertical(g0)
    c: Vertical(g2)
    c: Symmetric(g1,g0,g4)
    c: DistanceX(g3,g3) = 14.2
    c: DistanceY(g4,g-1) = 24.7
    c: DistanceX(g-1,g4) = 47.625
    c: Coincident(g5,g6)
    c: Coincident(g6,g7)
    c: Coincident(g7,g8)
    c: Coincident(g8,g5)
    c: Horizontal(g6)
    c: Horizontal(g8)
    c: Vertical(g5)
    c: Vertical(g7)
    c: Symmetric(g6,g5,g9)
    c: Coincident(g10,g11)
    c: Coincident(g11,g12)
    c: Coincident(g12,g13)
    c: Coincident(g13,g10)
    c: Horizontal(g11)
    c: Horizontal(g13)
    c: Vertical(g10)
    c: Vertical(g12)
    c: Symmetric(g11,g10,g14)
    c: Coincident(g15,g16)
    c: Coincident(g16,g17)
    c: Coincident(g17,g18)
    c: Coincident(g18,g15)
    c: Horizontal(g16)
    c: Horizontal(g18)
    c: Vertical(g15)
    c: Vertical(g17)
    c: Symmetric(g16,g15,g19)
    c: Coincident(g20,g21)
    c: Coincident(g21,g22)
    c: Coincident(g22,g23)
    c: Coincident(g23,g20)
    c: Horizontal(g21)
    c: Horizontal(g23)
    c: Vertical(g20)
    c: Vertical(g22)
    c: Symmetric(g21,g20,g24)
    c: Coincident(g25,g26)
    c: Coincident(g26,g27)
    c: Coincident(g27,g28)
    c: Coincident(g28,g25)
    c: Horizontal(g26)
    c: Horizontal(g28)
    c: Vertical(g25)
    c: Vertical(g27)
    c: Symmetric(g26,g25,g29)
    c: Coincident(g30,g31)
    c: Coincident(g31,g32)
    c: Coincident(g32,g33)
    c: Coincident(g33,g30)
    c: Horizontal(g31)
    c: Horizontal(g33)
    c: Vertical(g30)
    c: Vertical(g32)
    c: Symmetric(g31,g30,g34)
    c: Coincident(g35,g36)
    c: Coincident(g36,g37)
    c: Coincident(g37,g38)
    c: Coincident(g38,g35)
    c: Horizontal(g36)
    c: Horizontal(g38)
    c: Vertical(g35)
    c: Vertical(g37)
    c: Symmetric(g36,g35,g39)
    c: Coincident(g40,g41)
    c: Coincident(g41,g42)
    c: Coincident(g42,g43)
    c: Coincident(g43,g40)
    c: Horizontal(g41)
    c: Horizontal(g43)
    c: Vertical(g40)
    c: Vertical(g42)
    c: Symmetric(g41,g40,g44)
    c: Coincident(g45,g46)
    c: Coincident(g46,g47)
    c: Coincident(g47,g48)
    c: Coincident(g48,g45)
    c: Horizontal(g46)
    c: Horizontal(g48)
    c: Vertical(g45)
    c: Vertical(g47)
    c: Symmetric(g46,g45,g49)
    c: Coincident(g50,g51)
    c: Coincident(g51,g52)
    c: Coincident(g52,g53)
    c: Coincident(g53,g50)
    c: Horizontal(g51)
    c: Horizontal(g53)
    c: Vertical(g50)
    c: Vertical(g52)
    c: Symmetric(g51,g50,g54)
    c: Coincident(g55,g56)
    c: Coincident(g56,g57)
    c: Coincident(g57,g58)
    c: Coincident(g58,g55)
    c: Horizontal(g56)
    c: Horizontal(g58)
    c: Vertical(g55)
    c: Vertical(g57)
    c: Symmetric(g56,g55,g59)
    c: Coincident(g60,g61)
    c: Coincident(g61,g62)
    c: Coincident(g62,g63)
    c: Coincident(g63,g60)
    c: Horizontal(g61)
    c: Horizontal(g63)
    c: Vertical(g60)
    c: Vertical(g62)
    c: Symmetric(g61,g60,g64)
    c: Coincident(g65,g66)
    c: Coincident(g66,g67)
    c: Coincident(g67,g68)
    c: Coincident(g68,g65)
    c: Horizontal(g66)
    c: Horizontal(g68)
    c: Vertical(g65)
    c: Vertical(g67)
    c: Symmetric(g66,g65,g69)
    c: Coincident(g70,g71)
    c: Coincident(g71,g72)
    c: Coincident(g72,g73)
    c: Coincident(g73,g70)
    c: Horizontal(g71)
    c: Horizontal(g73)
    c: Vertical(g70)
    c: Vertical(g72)
    c: Symmetric(g71,g70,g74)
    c: DistanceX(g4,g9) = 23.8125
    c: Horizontal(g4,g9)
    c: Horizontal(g9,g14)
    c: Horizontal(g14,g19)
    c: Horizontal(g19,g24)
    c: Horizontal(g24,g29)
    c: Horizontal(g29,g34)
    c: Horizontal(g34,g39)
    c: Horizontal(g39,g44)
    c: Horizontal(g44,g49)
    c: Horizontal(g49,g54)
    c: Horizontal(g54,g59)
    c: Horizontal(g59,g64)
    c: Horizontal(g64,g69)
    c: Horizontal(g69,g74)
    c: DistanceX(g9,g14) = 19.05
    c: DistanceX(g14,g19) = 19.05
    c: DistanceX(g19,g24) = 19.05
    c: DistanceX(g29,g34) = 19.05
    c: DistanceX(g34,g39) = 19.05
    c: DistanceX(g39,g44) = 19.05
    c: DistanceX(g49,g54) = 19.05
    c: DistanceX(g54,g59) = 19.05
    c: DistanceX(g59,g64) = 19.05
    c: DistanceX(g24,g29) = 23.8125
    c: DistanceX(g44,g49) = 23.8125
    c: DistanceX(g64,g69) = 23.8125
    c: DistanceX(g69,g74) = 28.575
    c: Equal(g72,g73)
    c: Equal(g73,g67)
    c: Equal(g67,g68)
    c: Equal(g68,g62)
    c: Equal(g62,g63)
    c: Equal(g63,g57)
    c: Equal(g57,g58)
    c: Equal(g58,g52)
    c: Equal(g52,g53)
    c: Equal(g53,g47)
    c: Equal(g47,g48)
    c: Equal(g48,g42)
    c: Equal(g42,g43)
    c: Equal(g43,g37)
    c: Equal(g37,g38)
    c: Equal(g38,g32)
    c: Equal(g32,g33)
    c: Equal(g33,g27)
    c: Equal(g27,g28)
    c: Equal(g28,g22)
    c: Equal(g22,g23)
    c: Equal(g23,g17)
    c: Equal(g17,g18)
    c: Equal(g18,g12)
    c: Equal(g12,g13)
    c: Equal(g13,g7)
    c: Equal(g7,g8)
    c: Equal(g8,g2)
    c: Equal(g2,g3)
FEATURE [Sketcher::SketchObject] Sketch060
  AttachmentOffset = pos=(0,0,2.9) rot=(0,0,1;0rad)
  FullyConstrained = false
  MapMode = 5
  Placement = pos=(0,0,2.9) rot=(0,0,1;0rad)
  Support = -> [XY_Plane209]
  expr: .AttachmentOffset.Base.z = 1.6 + 1.3
  expr: Constraints[25] = Spreadsheet.Bottom_c_rad
  expr: Constraints[26] = Spreadsheet.Bottom_c_rad
  expr: Constraints[32] = Spreadsheet.PCB_length + Spreadsheet.pcb_to_wall_gap * 2
  expr: Constraints[33] = Spreadsheet.PCB_width + Spreadsheet.pcb_to_wall_gap * 2
  expr: Constraints[35] = 2 * Spreadsheet.Top_c_rad * sin(45 / 2)
  expr: Constraints[39] = 2 * Spreadsheet.Top_c_rad * sin(45 / 2)
  expr: Constraints[44] = Spreadsheet.wall_thickness / 2
  expr: Constraints[45] = Spreadsheet.PCB_length / 2
  expr: Constraints[46] = (Spreadsheet.PCB_length + Spreadsheet.pcb_to_wall_gap * 2 + Spreadsheet.wall_thickness * 2) / 4
  expr: Constraints[47] = (Spreadsheet.PCB_length + Spreadsheet.pcb_to_wall_gap * 2 + Spreadsheet.wall_thickness * 2) / 4
  expr: Constraints[49] = 2 * Spreadsheet.Bottom_c_rad * sin(45 / 2)
  expr: Constraints[51] = 2 * Spreadsheet.Bottom_c_rad * sin(45 / 2)
  expr: Constraints[5] = Spreadsheet.PCB_length / 2
  expr: Constraints[61] = Spreadsheet.PCB_length
  expr: Constraints[62] = Spreadsheet.PCB_width
  expr: Constraints[65] = Spreadsheet.PCB_length + 2 * Spreadsheet.pcb_to_wall_gap
  expr: Constraints[66] = Spreadsheet.PCB_width + 2 * Spreadsheet.pcb_to_wall_gap
  expr: Constraints[6] = Spreadsheet.PCB_width / 2
  expr: Constraints[74] = Spreadsheet.wall_thickness / 2
  expr: Constraints[7] = Spreadsheet.PCB_width + 2 * Spreadsheet.pcb_to_wall_gap + 2 * Spreadsheet.wall_thickness
  expr: Constraints[8] = Spreadsheet.PCB_length + 2 * Spreadsheet.pcb_to_wall_gap + 2 * Spreadsheet.wall_thickness
  sketch-geometry (46):
    g0: LineSegment StartX=-6.5 StartY=0.5 StartZ=0 EndX=-6.5 EndY=-142.5 EndZ=0
    g1: LineSegment StartX=-3.5 StartY=-145.5 StartZ=0 EndX=355.925 EndY=-145.5 EndZ=0
    g2: LineSegment StartX=358.925 StartY=-142.5 StartZ=0 EndX=358.925 EndY=0.5 EndZ=0
    g3: LineSegment StartX=352.925 StartY=6.5 StartZ=0 EndX=-0.5 EndY=6.5 EndZ=0
    g4: GeomPoint X=176.213 Y=-69.5 Z=0
    g5: ArcOfCircle CenterX=-0.5 CenterY=0.5 CenterZ=0 NormalX=0 NormalY=0 NormalZ=1 AngleXU=0 Radius=6 StartAngle=1.5708 EndAngle=3.14159
    g6: GeomPoint X=-6.5 Y=6.5 Z=0
    g7: ArcOfCircle CenterX=352.925 CenterY=0.5 CenterZ=0 NormalX=0 NormalY=0 NormalZ=1 AngleXU=0 Radius=6 StartAngle=0 EndAngle=1.5708
    g8: GeomPoint X=358.925 Y=6.5 Z=0
    g9: ArcOfCircle CenterX=-3.5 CenterY=-142.5 CenterZ=0 NormalX=0 NormalY=0 NormalZ=1 AngleXU=0 Radius=3 StartAngle=3.14159 EndAngle=4.71239
    g10: GeomPoint X=-6.5 Y=-145.5 Z=0
    g11: ArcOfCircle CenterX=355.925 CenterY=-142.5 CenterZ=0 NormalX=0 NormalY=0 NormalZ=1 AngleXU=0 Radius=3 StartAngle=4.71239 EndAngle=6.28319
    g12: GeomPoint X=358.925 Y=-145.5 Z=0
    g13: Circle CenterX=-1.74263 CenterY=1.74264 CenterZ=0 NormalX=0 NormalY=0 NormalZ=1 AngleXU=0 Radius=1.7
    g14: GeomPoint X=176.213 Y=-69.5 Z=0
    g15: GeomPoint X=-0.472801 Y=1.29801 Z=0
    g16: GeomPoint X=352.952 Y=1.5 Z=0
    g17: GeomPoint X=352.898 Y=-140.298 Z=0
    g18: GeomPoint X=-1.5 Y=-138.702 Z=0
    g19: GeomPoint X=-4.74264 Y=4.74264 Z=0
    g20: GeomPoint X=1.25738 Y=-1.25737 Z=0
    g21: Circle CenterX=354.168 CenterY=1.74264 CenterZ=0 NormalX=0 NormalY=0 NormalZ=1 AngleXU=0 Radius=1.7
    g22: GeomPoint X=351.168 Y=-1.25737 Z=0
    g23: GeomPoint X=357.168 Y=4.74264 Z=0
    g24: Circle CenterX=84.8563 CenterY=3.5 CenterZ=0 NormalX=0 NormalY=0 NormalZ=1 AngleXU=0 Radius=1.7
    g25: Circle CenterX=176.213 CenterY=3.5 CenterZ=0 NormalX=0 NormalY=0 NormalZ=1 AngleXU=0 Radius=1.7
    g26: Circle CenterX=267.569 CenterY=3.5 CenterZ=0 NormalX=0 NormalY=0 NormalZ=1 AngleXU=0 Radius=1.7
    g27: Circle CenterX=-2.62131 CenterY=-141.621 CenterZ=0 NormalX=0 NormalY=0 NormalZ=1 AngleXU=0 Radius=1.7
    g28: GeomPoint X=0.378703 Y=-138.621 Z=0
    g29: GeomPoint X=-5.62132 Y=-144.621 Z=0
    g30: GeomPoint X=352.046 Y=-138.621 Z=0
    g31: GeomPoint X=358.046 Y=-144.621 Z=0
    g32: Circle CenterX=355.046 CenterY=-141.621 CenterZ=0 NormalX=0 NormalY=0 NormalZ=1 AngleXU=0 Radius=1.7
    g33: GeomPoint X=176.213 Y=-69.5 Z=0
    g34: GeomPoint X=-0.472801 Y=1.29801 Z=0
    g35: GeomPoint X=7.7e-15 Y=-137.702 Z=0
    g36: GeomPoint X=352.898 Y=-140.298 Z=0
    g37: GeomPoint X=351.952 Y=-3e-15 Z=0
    g38: GeomPoint X=176.213 Y=-69.5 Z=0
    g39: GeomPoint X=-0.850325 Y=1.71354 Z=0
    g40: GeomPoint X=352.925 Y=-0.713539 Z=0
    g41: GeomPoint X=-0.149675 Y=-139.5 Z=0
    g42: GeomPoint X=353.275 Y=-140.714 Z=0
    g43: Circle CenterX=84.8563 CenterY=-142.5 CenterZ=0 NormalX=0 NormalY=0 NormalZ=1 AngleXU=0 Radius=1.7
    g44: Circle CenterX=176.213 CenterY=-142.5 CenterZ=0 NormalX=0 NormalY=0 NormalZ=1 AngleXU=0 Radius=1.7
    g45: Circle CenterX=267.569 CenterY=-142.5 CenterZ=0 NormalX=0 NormalY=0 NormalZ=1 AngleXU=0 Radius=1.7
  constraints (76):
    c: Horizontal(g1)
    c: Horizontal(g3)
    c: Vertical(g0)
    c: Vertical(g2)
    c: Symmetric(g12,g6,g4)
    c: DistanceX(g-1,g4) = 176.213
    c: DistanceY(g4,g-1) = 69.5
    c: DistanceY(g10,g6) = 152
    c: DistanceX(g6,g8) = 365.425
    c: PointOnObject(g6,g0)
    c: PointOnObject(g6,g3)
    c: Tangent(g0,g5) = -1.5708
    c: Tangent(g3,g5) = -1.5708
    c: PointOnObject(g8,g2)
    c: PointOnObject(g8,g3)
    c: Tangent(g2,g7) = -1.5708
    c: Tangent(g3,g7) = -1.5708
    c: PointOnObject(g10,g0)
    c: PointOnObject(g10,g1)
    c: Tangent(g0,g9) = -1.5708
    c: Tangent(g1,g9) = -1.5708
    c: PointOnObject(g12,g1)
    c: PointOnObject(g12,g2)
    c: Tangent(g1,g11) = -1.5708
    c: Tangent(g2,g11) = -1.5708
    c: Radius(g11) = 3
    c: Radius(g9) = 3
    c: Radius(g5) = 6
    c: Radius(g7) = 6
    c: Diameter(g13) = 3.4
    c: Symmetric(g17,g15,g14)
    c: Coincident(g14,g4)
    c: DistanceX(g15,g16) = 353.425
    c: DistanceY(g18,g15) = 140
    c: PointOnObject(g19,g5)
    c: Distance(g0,g19) = 4.5922
    c: Symmetric(g19,g20,g13)
    c: Diameter(g21) = 3.4
    c: PointOnObject(g23,g7)
    c: Distance(g2,g23) = 4.5922
    c: Symmetric(g22,g23,g21)
    c: Equal(g24,g25)
    c: Equal(g26,g25)
    c: Diameter(g25) = 3.4
    c: Distance(g25,g3) = 3
    c: DistanceX(g-1,g25) = 176.213
    c: DistanceX(g24,g25) = 91.3563
    c: DistanceX(g25,g26) = 91.3563
    c: PointOnObject(g29,g9)
    c: Distance(g0,g29) = 2.2961
    c: PointOnObject(g31,g11)
    c: Distance(g1,g31) = 2.2961
    c: Symmetric(g30,g31,g32)
    c: Diameter(g32) = 3.4
    c: Diameter(g27) = 3.4
    c: Symmetric(g29,g28,g27)
    c: Horizontal(g24,g25)
    c: Horizontal(g26,g25)
    c: Symmetric(g36,g34,g33)
    c: Coincident(g33,g4)
    c: Coincident(g36,g17)
    c: DistanceX(g34,g37) = 352.425
    c: DistanceY(g35,g34) = 139
    c: Symmetric(g42,g39,g38)
    c: Coincident(g38,g4)
    c: DistanceX(g41,g42) = 353.425
    c: DistanceY(g42,g40) = 140
    c: Equal(g43,g44)
    c: Equal(g45,g44)
    c: Equal(g25,g44) = 3.1
    c: DistanceX(g43,g44) = 91.3563
    c: DistanceX(g44,g45) = 91.3563
    c: Horizontal(g43,g44)
    c: Horizontal(g45,g44)
    c: Distance(g44,g1) = 3
    c: Vertical(g44,g25)
FEATURE [PartDesign::Pad] Pad013
  Direction = (0,0,1)
  Length = 1.2
  Length2 = 10
  Profile = -> Sketch060
  ReferenceAxis = -> Sketch060 [N_Axis]
  Type = 0
FEATURE [PartDesign::Pocket] Pocket045
  BaseFeature = -> Pad013
  Direction = (0,0,-1)
  Length = 5
  Length2 = 5
  Profile = -> Sketch059
  ReferenceAxis = -> Sketch059 [N_Axis]
  Type = 0
FEATURE [Sketcher::SketchObject] Sketch061
  AttachmentOffset = pos=(0,0,4.1) rot=(0,0,1;0rad)
  FullyConstrained = true
  MapMode = 5
  Placement = pos=(0,0,4.1) rot=(0,0,1;0rad)
  Support = -> [XY_Plane209]
  expr: Constraints[10] = Spreadsheet.PCB_width - Spreadsheet.u * 4.75
  expr: Constraints[11] = Spreadsheet.u * 2.5
  expr: Constraints[138] = Spreadsheet.u
  expr: Constraints[153] = Spreadsheet.u
  expr: Constraints[154] = Spreadsheet.u
  expr: Constraints[155] = Spreadsheet.u
  expr: Constraints[156] = Spreadsheet.u
  expr: Constraints[157] = Spreadsheet.u
  expr: Constraints[158] = Spreadsheet.u
  expr: Constraints[159] = Spreadsheet.u
  expr: Constraints[160] = Spreadsheet.u
  expr: Constraints[161] = Spreadsheet.u
  expr: Constraints[162] = Spreadsheet.u
  expr: Constraints[163] = Spreadsheet.u
  expr: Constraints[164] = Spreadsheet.u * 1.5
  expr: Constraints[165] = Spreadsheet.u * 2
  expr: Constraints[9] = Spreadsheet.switch_hole + 0.2
  sketch-geometry (75):
    g0: LineSegment StartX=40.525 StartY=-41.4125 StartZ=0 EndX=40.525 EndY=-55.6125 EndZ=0
    g1: LineSegment StartX=40.525 StartY=-55.6125 StartZ=0 EndX=54.725 EndY=-55.6125 EndZ=0
    g2: LineSegment StartX=54.725 StartY=-55.6125 StartZ=0 EndX=54.725 EndY=-41.4125 EndZ=0
    g3: LineSegment StartX=54.725 StartY=-41.4125 StartZ=0 EndX=40.525 EndY=-41.4125 EndZ=0
    g4: GeomPoint X=47.625 Y=-48.5125 Z=0
    g5: LineSegment StartX=59.575 StartY=-41.4125 StartZ=0 EndX=59.575 EndY=-55.6125 EndZ=0
    g6: LineSegment StartX=59.575 StartY=-55.6125 StartZ=0 EndX=73.775 EndY=-55.6125 EndZ=0
    g7: LineSegment StartX=73.775 StartY=-55.6125 StartZ=0 EndX=73.775 EndY=-41.4125 EndZ=0
    g8: LineSegment StartX=73.775 StartY=-41.4125 StartZ=0 EndX=59.575 EndY=-41.4125 EndZ=0
    g9: GeomPoint X=66.675 Y=-48.5125 Z=0
    g10: LineSegment StartX=78.625 StartY=-41.4125 StartZ=0 EndX=78.625 EndY=-55.6125 EndZ=0
    g11: LineSegment StartX=78.625 StartY=-55.6125 StartZ=0 EndX=92.825 EndY=-55.6125 EndZ=0
    g12: LineSegment StartX=92.825 StartY=-55.6125 StartZ=0 EndX=92.825 EndY=-41.4125 EndZ=0
    g13: LineSegment StartX=92.825 StartY=-41.4125 StartZ=0 EndX=78.625 EndY=-41.4125 EndZ=0
    g14: GeomPoint X=85.725 Y=-48.5125 Z=0
    g15: LineSegment StartX=97.675 StartY=-41.4125 StartZ=0 EndX=97.675 EndY=-55.6125 EndZ=0
    g16: LineSegment StartX=97.675 StartY=-55.6125 StartZ=0 EndX=111.875 EndY=-55.6125 EndZ=0
    g17: LineSegment StartX=111.875 StartY=-55.6125 StartZ=0 EndX=111.875 EndY=-41.4125 EndZ=0
    g18: LineSegment StartX=111.875 StartY=-41.4125 StartZ=0 EndX=97.675 EndY=-41.4125 EndZ=0
    g19: GeomPoint X=104.775 Y=-48.5125 Z=0
    g20: LineSegment StartX=116.725 StartY=-41.4125 StartZ=0 EndX=116.725 EndY=-55.6125 EndZ=0
    g21: LineSegment StartX=116.725 StartY=-55.6125 StartZ=0 EndX=130.925 EndY=-55.6125 EndZ=0
    g22: LineSegment StartX=130.925 StartY=-55.6125 StartZ=0 EndX=130.925 EndY=-41.4125 EndZ=0
    g23: LineSegment StartX=130.925 StartY=-41.4125 StartZ=0 EndX=116.725 EndY=-41.4125 EndZ=0
    g24: GeomPoint X=123.825 Y=-48.5125 Z=0
    g25: LineSegment StartX=135.775 StartY=-41.4125 StartZ=0 EndX=135.775 EndY=-55.6125 EndZ=0
    g26: LineSegment StartX=135.775 StartY=-55.6125 StartZ=0 EndX=149.975 EndY=-55.6125 EndZ=0
    g27: LineSegment StartX=149.975 StartY=-55.6125 StartZ=0 EndX=149.975 EndY=-41.4125 EndZ=0
    g28: LineSegment StartX=149.975 StartY=-41.4125 StartZ=0 EndX=135.775 EndY=-41.4125 EndZ=0
    g29: GeomPoint X=142.875 Y=-48.5125 Z=0
    g30: LineSegment StartX=154.825 StartY=-41.4125 StartZ=0 EndX=154.825 EndY=-55.6125 EndZ=0
    g31: LineSegment StartX=154.825 StartY=-55.6125 StartZ=0 EndX=169.025 EndY=-55.6125 EndZ=0
    g32: LineSegment StartX=169.025 StartY=-55.6125 StartZ=0 EndX=169.025 EndY=-41.4125 EndZ=0
    g33: LineSegment StartX=169.025 StartY=-41.4125 StartZ=0 EndX=154.825 EndY=-41.4125 EndZ=0
    g34: GeomPoint X=161.925 Y=-48.5125 Z=0
    g35: LineSegment StartX=173.875 StartY=-41.4125 StartZ=0 EndX=173.875 EndY=-55.6125 EndZ=0
    g36: LineSegment StartX=173.875 StartY=-55.6125 StartZ=0 EndX=188.075 EndY=-55.6125 EndZ=0
    g37: LineSegment StartX=188.075 StartY=-55.6125 StartZ=0 EndX=188.075 EndY=-41.4125 EndZ=0
    g38: LineSegment StartX=188.075 StartY=-41.4125 StartZ=0 EndX=173.875 EndY=-41.4125 EndZ=0
    g39: GeomPoint X=180.975 Y=-48.5125 Z=0
    g40: LineSegment StartX=192.925 StartY=-41.4125 StartZ=0 EndX=192.925 EndY=-55.6125 EndZ=0
    g41: LineSegment StartX=192.925 StartY=-55.6125 StartZ=0 EndX=207.125 EndY=-55.6125 EndZ=0
    g42: LineSegment StartX=207.125 StartY=-55.6125 StartZ=0 EndX=207.125 EndY=-41.4125 EndZ=0
    g43: LineSegment StartX=207.125 StartY=-41.4125 StartZ=0 EndX=192.925 EndY=-41.4125 EndZ=0
    g44: GeomPoint X=200.025 Y=-48.5125 Z=0
    g45: LineSegment StartX=211.975 StartY=-41.4125 StartZ=0 EndX=211.975 EndY=-55.6125 EndZ=0
    g46: LineSegment StartX=211.975 StartY=-55.6125 StartZ=0 EndX=226.175 EndY=-55.6125 EndZ=0
    g47: LineSegment StartX=226.175 StartY=-55.6125 StartZ=0 EndX=226.175 EndY=-41.4125 EndZ=0
    g48: LineSegment StartX=226.175 StartY=-41.4125 StartZ=0 EndX=211.975 EndY=-41.4125 EndZ=0
    g49: GeomPoint X=219.075 Y=-48.5125 Z=0
    g50: LineSegment StartX=231.025 StartY=-41.4125 StartZ=0 EndX=231.025 EndY=-55.6125 EndZ=0
    g51: LineSegment StartX=231.025 StartY=-55.6125 StartZ=0 EndX=245.225 EndY=-55.6125 EndZ=0
    g52: LineSegment StartX=245.225 StartY=-55.6125 StartZ=0 EndX=245.225 EndY=-41.4125 EndZ=0
    g53: LineSegment StartX=245.225 StartY=-41.4125 StartZ=0 EndX=231.025 EndY=-41.4125 EndZ=0
    g54: GeomPoint X=238.125 Y=-48.5125 Z=0
    g55: LineSegment StartX=250.075 StartY=-41.4125 StartZ=0 EndX=250.075 EndY=-55.6125 EndZ=0
    g56: LineSegment StartX=250.075 StartY=-55.6125 StartZ=0 EndX=264.275 EndY=-55.6125 EndZ=0
    g57: LineSegment StartX=264.275 StartY=-55.6125 StartZ=0 EndX=264.275 EndY=-41.4125 EndZ=0
    g58: LineSegment StartX=264.275 StartY=-41.4125 StartZ=0 EndX=250.075 EndY=-41.4125 EndZ=0
    g59: GeomPoint X=257.175 Y=-48.5125 Z=0
    g60: LineSegment StartX=269.125 StartY=-41.4125 StartZ=0 EndX=269.125 EndY=-55.6125 EndZ=0
    g61: LineSegment StartX=269.125 StartY=-55.6125 StartZ=0 EndX=283.325 EndY=-55.6125 EndZ=0
    g62: LineSegment StartX=283.325 StartY=-55.6125 StartZ=0 EndX=283.325 EndY=-41.4125 EndZ=0
    g63: LineSegment StartX=283.325 StartY=-41.4125 StartZ=0 EndX=269.125 EndY=-41.4125 EndZ=0
    g64: GeomPoint X=276.225 Y=-48.5125 Z=0
    g65: LineSegment StartX=297.7 StartY=-41.4125 StartZ=0 EndX=297.7 EndY=-55.6125 EndZ=0
    g66: LineSegment StartX=297.7 StartY=-55.6125 StartZ=0 EndX=311.9 EndY=-55.6125 EndZ=0
    g67: LineSegment StartX=311.9 StartY=-55.6125 StartZ=0 EndX=311.9 EndY=-41.4125 EndZ=0
    g68: LineSegment StartX=311.9 StartY=-41.4125 StartZ=0 EndX=297.7 EndY=-41.4125 EndZ=0
    g69: GeomPoint X=304.8 Y=-48.5125 Z=0
    g70: LineSegment StartX=335.8 StartY=-41.4125 StartZ=0 EndX=335.8 EndY=-55.6125 EndZ=0
    g71: LineSegment StartX=335.8 StartY=-55.6125 StartZ=0 EndX=350 EndY=-55.6125 EndZ=0
    g72: LineSegment StartX=350 StartY=-55.6125 StartZ=0 EndX=350 EndY=-41.4125 EndZ=0
    g73: LineSegment StartX=350 StartY=-41.4125 StartZ=0 EndX=335.8 EndY=-41.4125 EndZ=0
    g74: GeomPoint X=342.9 Y=-48.5125 Z=0
  constraints (195):
    c: Coincident(g0,g1)
    c: Coincident(g1,g2)
    c: Coincident(g2,g3)
    c: Coincident(g3,g0)
    c: Horizontal(g1)
    c: Horizontal(g3)
    c: Vertical(g0)
    c: Vertical(g2)
    c: Symmetric(g1,g0,g4)
    c: DistanceX(g3,g3) = 14.2
    c: DistanceY(g4,g-1) = 48.5125
    c: DistanceX(g-1,g4) = 47.625
    c: Coincident(g5,g6)
    c: Coincident(g6,g7)
    c: Coincident(g7,g8)
    c: Coincident(g8,g5)
    c: Horizontal(g6)
    c: Horizontal(g8)
    c: Vertical(g5)
    c: Vertical(g7)
    c: Symmetric(g6,g5,g9)
    c: Coincident(g10,g11)
    c: Coincident(g11,g12)
    c: Coincident(g12,g13)
    c: Coincident(g13,g10)
    c: Horizontal(g11)
    c: Horizontal(g13)
    c: Vertical(g10)
    c: Vertical(g12)
    c: Symmetric(g11,g10,g14)
    c: Coincident(g15,g16)
    c: Coincident(g16,g17)
    c: Coincident(g17,g18)
    c: Coincident(g18,g15)
    c: Horizontal(g16)
    c: Horizontal(g18)
    c: Vertical(g15)
    c: Vertical(g17)
    c: Symmetric(g16,g15,g19)
    c: Coincident(g20,g21)
    c: Coincident(g21,g22)
    c: Coincident(g22,g23)
    c: Coincident(g23,g20)
    c: Horizontal(g21)
    c: Horizontal(g23)
    c: Vertical(g20)
    c: Vertical(g22)
    c: Symmetric(g21,g20,g24)
    c: Coincident(g25,g26)
    c: Coincident(g26,g27)
    c: Coincident(g27,g28)
    c: Coincident(g28,g25)
    c: Horizontal(g26)
    c: Horizontal(g28)
    c: Vertical(g25)
    c: Vertical(g27)
    c: Symmetric(g26,g25,g29)
    c: Coincident(g30,g31)
    c: Coincident(g31,g32)
    c: Coincident(g32,g33)
    c: Coincident(g33,g30)
    c: Horizontal(g31)
    c: Horizontal(g33)
    c: Vertical(g30)
    c: Vertical(g32)
    c: Symmetric(g31,g30,g34)
    c: Coincident(g35,g36)
    c: Coincident(g36,g37)
    c: Coincident(g37,g38)
    c: Coincident(g38,g35)
    c: Horizontal(g36)
    c: Horizontal(g38)
    c: Vertical(g35)
    c: Vertical(g37)
    c: Symmetric(g36,g35,g39)
    c: Coincident(g40,g41)
    c: Coincident(g41,g42)
    c: Coincident(g42,g43)
    c: Coincident(g43,g40)
    c: Horizontal(g41)
    c: Horizontal(g43)
    c: Vertical(g40)
    c: Vertical(g42)
    c: Symmetric(g41,g40,g44)
    c: Coincident(g45,g46)
    c: Coincident(g46,g47)
    c: Coincident(g47,g48)
    c: Coincident(g48,g45)
    c: Horizontal(g46)
    c: Horizontal(g48)
    c: Vertical(g45)
    c: Vertical(g47)
    c: Symmetric(g46,g45,g49)
    c: Coincident(g50,g51)
    c: Coincident(g51,g52)
    c: Coincident(g52,g53)
    c: Coincident(g53,g50)
    c: Horizontal(g51)
    c: Horizontal(g53)
    c: Vertical(g50)
    c: Vertical(g52)
    c: Symmetric(g51,g50,g54)
    c: Coincident(g55,g56)
    c: Coincident(g56,g57)
    c: Coincident(g57,g58)
    c: Coincident(g58,g55)
    c: Horizontal(g56)
    c: Horizontal(g58)
    c: Vertical(g55)
    c: Vertical(g57)
    c: Symmetric(g56,g55,g59)
    c: Coincident(g60,g61)
    c: Coincident(g61,g62)
    c: Coincident(g62,g63)
    c: Coincident(g63,g60)
    c: Horizontal(g61)
    c: Horizontal(g63)
    c: Vertical(g60)
    c: Vertical(g62)
    c: Symmetric(g61,g60,g64)
    c: Coincident(g65,g66)
    c: Coincident(g66,g67)
    c: Coincident(g67,g68)
    c: Coincident(g68,g65)
    c: Horizontal(g66)
    c: Horizontal(g68)
    c: Vertical(g65)
    c: Vertical(g67)
    c: Symmetric(g66,g65,g69)
    c: Coincident(g70,g71)
    c: Coincident(g71,g72)
    c: Coincident(g72,g73)
    c: Coincident(g73,g70)
    c: Horizontal(g71)
    c: Horizontal(g73)
    c: Vertical(g70)
    c: Vertical(g72)
    c: Symmetric(g71,g70,g74)
    c: DistanceX(g4,g9) = 19.05
    c: Horizontal(g4,g9)
    c: Horizontal(g9,g14)
    c: Horizontal(g14,g19)
    c: Horizontal(g19,g24)
    c: Horizontal(g24,g29)
    c: Horizontal(g29,g34)
    c: Horizontal(g34,g39)
    c: Horizontal(g39,g44)
    c: Horizontal(g44,g49)
    c: Horizontal(g49,g54)
    c: Horizontal(g54,g59)
    c: Horizontal(g59,g64)
    c: Horizontal(g64,g69)
    c: Horizontal(g69,g74)
    c: DistanceX(g9,g14) = 19.05
    c: DistanceX(g14,g19) = 19.05
    c: DistanceX(g19,g24) = 19.05
    c: DistanceX(g29,g34) = 19.05
    c: DistanceX(g34,g39) = 19.05
    c: DistanceX(g39,g44) = 19.05
    c: DistanceX(g49,g54) = 19.05
    c: DistanceX(g54,g59) = 19.05
    c: DistanceX(g59,g64) = 19.05
    c: DistanceX(g24,g29) = 19.05
    c: DistanceX(g44,g49) = 19.05
    c: DistanceX(g64,g69) = 28.575
    c: DistanceX(g69,g74) = 38.1
    c: Equal(g72,g73)
    c: Equal(g73,g67)
    c: Equal(g67,g68)
    c: Equal(g68,g62)
    c: Equal(g62,g63)
    c: Equal(g63,g57)
    c: Equal(g57,g58)
    c: Equal(g58,g52)
    c: Equal(g52,g53)
    c: Equal(g53,g47)
    c: Equal(g47,g48)
    c: Equal(g48,g42)
    c: Equal(g42,g43)
    c: Equal(g43,g37)
    c: Equal(g37,g38)
    c: Equal(g38,g32)
    c: Equal(g32,g33)
    c: Equal(g33,g27)
    c: Equal(g27,g28)
    c: Equal(g28,g22)
    c: Equal(g22,g23)
    c: Equal(g23,g17)
    c: Equal(g17,g18)
    c: Equal(g18,g12)
    c: Equal(g12,g13)
    c: Equal(g13,g7)
    c: Equal(g7,g8)
    c: Equal(g8,g2)
    c: Equal(g2,g3)
FEATURE [PartDesign::Pocket] Pocket046
  BaseFeature = -> Pocket045
  Direction = (0,0,-1)
  Length = 5
  Length2 = 5
  Profile = -> Sketch061
  ReferenceAxis = -> Sketch061 [N_Axis]
  Type = 0
FEATURE [Sketcher::SketchObject] Sketch062
  AttachmentOffset = pos=(0,0,4.1) rot=(0,0,1;0rad)
  FullyConstrained = true
  MapMode = 5
  Placement = pos=(0,0,4.1) rot=(0,0,1;0rad)
  Support = -> [XY_Plane209]
  expr: Constraints[10] = Spreadsheet.PCB_width - Spreadsheet.u * 3.75
  expr: Constraints[11] = Spreadsheet.u * 2.75
  expr: Constraints[138] = Spreadsheet.u * 1.25
  expr: Constraints[153] = Spreadsheet.u
  expr: Constraints[154] = Spreadsheet.u
  expr: Constraints[155] = Spreadsheet.u
  expr: Constraints[156] = Spreadsheet.u
  expr: Constraints[157] = Spreadsheet.u
  expr: Constraints[158] = Spreadsheet.u
  expr: Constraints[159] = Spreadsheet.u
  expr: Constraints[160] = Spreadsheet.u
  expr: Constraints[161] = Spreadsheet.u
  expr: Constraints[162] = Spreadsheet.u
  expr: Constraints[163] = Spreadsheet.u
  expr: Constraints[164] = Spreadsheet.u * 1.25
  expr: Constraints[165] = Spreadsheet.u * 1.75
  expr: Constraints[9] = Spreadsheet.switch_hole + 0.2
  sketch-geometry (75):
    g0: LineSegment StartX=45.2875 StartY=-60.4625 StartZ=0 EndX=45.2875 EndY=-74.6625 EndZ=0
    g1: LineSegment StartX=45.2875 StartY=-74.6625 StartZ=0 EndX=59.4875 EndY=-74.6625 EndZ=0
    g2: LineSegment StartX=59.4875 StartY=-74.6625 StartZ=0 EndX=59.4875 EndY=-60.4625 EndZ=0
    g3: LineSegment StartX=59.4875 StartY=-60.4625 StartZ=0 EndX=45.2875 EndY=-60.4625 EndZ=0
    g4: GeomPoint X=52.3875 Y=-67.5625 Z=0
    g5: LineSegment StartX=69.1 StartY=-60.4625 StartZ=0 EndX=69.1 EndY=-74.6625 EndZ=0
    g6: LineSegment StartX=69.1 StartY=-74.6625 StartZ=0 EndX=83.3 EndY=-74.6625 EndZ=0
    g7: LineSegment StartX=83.3 StartY=-74.6625 StartZ=0 EndX=83.3 EndY=-60.4625 EndZ=0
    g8: LineSegment StartX=83.3 StartY=-60.4625 StartZ=0 EndX=69.1 EndY=-60.4625 EndZ=0
    g9: GeomPoint X=76.2 Y=-67.5625 Z=0
    g10: LineSegment StartX=88.15 StartY=-60.4625 StartZ=0 EndX=88.15 EndY=-74.6625 EndZ=0
    g11: LineSegment StartX=88.15 StartY=-74.6625 StartZ=0 EndX=102.35 EndY=-74.6625 EndZ=0
    g12: LineSegment StartX=102.35 StartY=-74.6625 StartZ=0 EndX=102.35 EndY=-60.4625 EndZ=0
    g13: LineSegment StartX=102.35 StartY=-60.4625 StartZ=0 EndX=88.15 EndY=-60.4625 EndZ=0
    g14: GeomPoint X=95.25 Y=-67.5625 Z=0
    g15: LineSegment StartX=107.2 StartY=-60.4625 StartZ=0 EndX=107.2 EndY=-74.6625 EndZ=0
    g16: LineSegment StartX=107.2 StartY=-74.6625 StartZ=0 EndX=121.4 EndY=-74.6625 EndZ=0
    g17: LineSegment StartX=121.4 StartY=-74.6625 StartZ=0 EndX=121.4 EndY=-60.4625 EndZ=0
    g18: LineSegment StartX=121.4 StartY=-60.4625 StartZ=0 EndX=107.2 EndY=-60.4625 EndZ=0
    g19: GeomPoint X=114.3 Y=-67.5625 Z=0
    g20: LineSegment StartX=126.25 StartY=-60.4625 StartZ=0 EndX=126.25 EndY=-74.6625 EndZ=0
    g21: LineSegment StartX=126.25 StartY=-74.6625 StartZ=0 EndX=140.45 EndY=-74.6625 EndZ=0
    g22: LineSegment StartX=140.45 StartY=-74.6625 StartZ=0 EndX=140.45 EndY=-60.4625 EndZ=0
    g23: LineSegment StartX=140.45 StartY=-60.4625 StartZ=0 EndX=126.25 EndY=-60.4625 EndZ=0
    g24: GeomPoint X=133.35 Y=-67.5625 Z=0
    g25: LineSegment StartX=145.3 StartY=-60.4625 StartZ=0 EndX=145.3 EndY=-74.6625 EndZ=0
    g26: LineSegment StartX=145.3 StartY=-74.6625 StartZ=0 EndX=159.5 EndY=-74.6625 EndZ=0
    g27: LineSegment StartX=159.5 StartY=-74.6625 StartZ=0 EndX=159.5 EndY=-60.4625 EndZ=0
    g28: LineSegment StartX=159.5 StartY=-60.4625 StartZ=0 EndX=145.3 EndY=-60.4625 EndZ=0
    g29: GeomPoint X=152.4 Y=-67.5625 Z=0
    g30: LineSegment StartX=164.35 StartY=-60.4625 StartZ=0 EndX=164.35 EndY=-74.6625 EndZ=0
    g31: LineSegment StartX=164.35 StartY=-74.6625 StartZ=0 EndX=178.55 EndY=-74.6625 EndZ=0
    g32: LineSegment StartX=178.55 StartY=-74.6625 StartZ=0 EndX=178.55 EndY=-60.4625 EndZ=0
    g33: LineSegment StartX=178.55 StartY=-60.4625 StartZ=0 EndX=164.35 EndY=-60.4625 EndZ=0
    g34: GeomPoint X=171.45 Y=-67.5625 Z=0
    g35: LineSegment StartX=183.4 StartY=-60.4625 StartZ=0 EndX=183.4 EndY=-74.6625 EndZ=0
    g36: LineSegment StartX=183.4 StartY=-74.6625 StartZ=0 EndX=197.6 EndY=-74.6625 EndZ=0
    g37: LineSegment StartX=197.6 StartY=-74.6625 StartZ=0 EndX=197.6 EndY=-60.4625 EndZ=0
    g38: LineSegment StartX=197.6 StartY=-60.4625 StartZ=0 EndX=183.4 EndY=-60.4625 EndZ=0
    g39: GeomPoint X=190.5 Y=-67.5625 Z=0
    g40: LineSegment StartX=202.45 StartY=-60.4625 StartZ=0 EndX=202.45 EndY=-74.6625 EndZ=0
    g41: LineSegment StartX=202.45 StartY=-74.6625 StartZ=0 EndX=216.65 EndY=-74.6625 EndZ=0
    g42: LineSegment StartX=216.65 StartY=-74.6625 StartZ=0 EndX=216.65 EndY=-60.4625 EndZ=0
    g43: LineSegment StartX=216.65 StartY=-60.4625 StartZ=0 EndX=202.45 EndY=-60.4625 EndZ=0
    g44: GeomPoint X=209.55 Y=-67.5625 Z=0
    g45: LineSegment StartX=221.5 StartY=-60.4625 StartZ=0 EndX=221.5 EndY=-74.6625 EndZ=0
    g46: LineSegment StartX=221.5 StartY=-74.6625 StartZ=0 EndX=235.7 EndY=-74.6625 EndZ=0
    g47: LineSegment StartX=235.7 StartY=-74.6625 StartZ=0 EndX=235.7 EndY=-60.4625 EndZ=0
    g48: LineSegment StartX=235.7 StartY=-60.4625 StartZ=0 EndX=221.5 EndY=-60.4625 EndZ=0
    g49: GeomPoint X=228.6 Y=-67.5625 Z=0
    g50: LineSegment StartX=240.55 StartY=-60.4625 StartZ=0 EndX=240.55 EndY=-74.6625 EndZ=0
    g51: LineSegment StartX=240.55 StartY=-74.6625 StartZ=0 EndX=254.75 EndY=-74.6625 EndZ=0
    g52: LineSegment StartX=254.75 StartY=-74.6625 StartZ=0 EndX=254.75 EndY=-60.4625 EndZ=0
    g53: LineSegment StartX=254.75 StartY=-60.4625 StartZ=0 EndX=240.55 EndY=-60.4625 EndZ=0
    g54: GeomPoint X=247.65 Y=-67.5625 Z=0
    g55: LineSegment StartX=259.6 StartY=-60.4625 StartZ=0 EndX=259.6 EndY=-74.6625 EndZ=0
    g56: LineSegment StartX=259.6 StartY=-74.6625 StartZ=0 EndX=273.8 EndY=-74.6625 EndZ=0
    g57: LineSegment StartX=273.8 StartY=-74.6625 StartZ=0 EndX=273.8 EndY=-60.4625 EndZ=0
    g58: LineSegment StartX=273.8 StartY=-60.4625 StartZ=0 EndX=259.6 EndY=-60.4625 EndZ=0
    g59: GeomPoint X=266.7 Y=-67.5625 Z=0
    g60: LineSegment StartX=278.65 StartY=-60.4625 StartZ=0 EndX=278.65 EndY=-74.6625 EndZ=0
    g61: LineSegment StartX=278.65 StartY=-74.6625 StartZ=0 EndX=292.85 EndY=-74.6625 EndZ=0
    g62: LineSegment StartX=292.85 StartY=-74.6625 StartZ=0 EndX=292.85 EndY=-60.4625 EndZ=0
    g63: LineSegment StartX=292.85 StartY=-60.4625 StartZ=0 EndX=278.65 EndY=-60.4625 EndZ=0
    g64: GeomPoint X=285.75 Y=-67.5625 Z=0
    g65: LineSegment StartX=302.462 StartY=-60.4625 StartZ=0 EndX=302.462 EndY=-74.6625 EndZ=0
    g66: LineSegment StartX=302.462 StartY=-74.6625 StartZ=0 EndX=316.663 EndY=-74.6625 EndZ=0
    g67: LineSegment StartX=316.663 StartY=-74.6625 StartZ=0 EndX=316.663 EndY=-60.4625 EndZ=0
    g68: LineSegment StartX=316.663 StartY=-60.4625 StartZ=0 EndX=302.462 EndY=-60.4625 EndZ=0
    g69: GeomPoint X=309.562 Y=-67.5625 Z=0
    g70: LineSegment StartX=335.8 StartY=-60.4625 StartZ=0 EndX=335.8 EndY=-74.6625 EndZ=0
    g71: LineSegment StartX=335.8 StartY=-74.6625 StartZ=0 EndX=350 EndY=-74.6625 EndZ=0
    g72: LineSegment StartX=350 StartY=-74.6625 StartZ=0 EndX=350 EndY=-60.4625 EndZ=0
    g73: LineSegment StartX=350 StartY=-60.4625 StartZ=0 EndX=335.8 EndY=-60.4625 EndZ=0
    g74: GeomPoint X=342.9 Y=-67.5625 Z=0
  constraints (195):
    c: Coincident(g0,g1)
    c: Coincident(g1,g2)
    c: Coincident(g2,g3)
    c: Coincident(g3,g0)
    c: Horizontal(g1)
    c: Horizontal(g3)
    c: Vertical(g0)
    c: Vertical(g2)
    c: Symmetric(g1,g0,g4)
    c: DistanceX(g3,g3) = 14.2
    c: DistanceY(g4,g-1) = 67.5625
    c: DistanceX(g-1,g4) = 52.3875
    c: Coincident(g5,g6)
    c: Coincident(g6,g7)
    c: Coincident(g7,g8)
    c: Coincident(g8,g5)
    c: Horizontal(g6)
    c: Horizontal(g8)
    c: Vertical(g5)
    c: Vertical(g7)
    c: Symmetric(g6,g5,g9)
    c: Coincident(g10,g11)
    c: Coincident(g11,g12)
    c: Coincident(g12,g13)
    c: Coincident(g13,g10)
    c: Horizontal(g11)
    c: Horizontal(g13)
    c: Vertical(g10)
    c: Vertical(g12)
    c: Symmetric(g11,g10,g14)
    c: Coincident(g15,g16)
    c: Coincident(g16,g17)
    c: Coincident(g17,g18)
    c: Coincident(g18,g15)
    c: Horizontal(g16)
    c: Horizontal(g18)
    c: Vertical(g15)
    c: Vertical(g17)
    c: Symmetric(g16,g15,g19)
    c: Coincident(g20,g21)
    c: Coincident(g21,g22)
    c: Coincident(g22,g23)
    c: Coincident(g23,g20)
    c: Horizontal(g21)
    c: Horizontal(g23)
    c: Vertical(g20)
    c: Vertical(g22)
    c: Symmetric(g21,g20,g24)
    c: Coincident(g25,g26)
    c: Coincident(g26,g27)
    c: Coincident(g27,g28)
    c: Coincident(g28,g25)
    c: Horizontal(g26)
    c: Horizontal(g28)
    c: Vertical(g25)
    c: Vertical(g27)
    c: Symmetric(g26,g25,g29)
    c: Coincident(g30,g31)
    c: Coincident(g31,g32)
    c: Coincident(g32,g33)
    c: Coincident(g33,g30)
    c: Horizontal(g31)
    c: Horizontal(g33)
    c: Vertical(g30)
    c: Vertical(g32)
    c: Symmetric(g31,g30,g34)
    c: Coincident(g35,g36)
    c: Coincident(g36,g37)
    c: Coincident(g37,g38)
    c: Coincident(g38,g35)
    c: Horizontal(g36)
    c: Horizontal(g38)
    c: Vertical(g35)
    c: Vertical(g37)
    c: Symmetric(g36,g35,g39)
    c: Coincident(g40,g41)
    c: Coincident(g41,g42)
    c: Coincident(g42,g43)
    c: Coincident(g43,g40)
    c: Horizontal(g41)
    c: Horizontal(g43)
    c: Vertical(g40)
    c: Vertical(g42)
    c: Symmetric(g41,g40,g44)
    c: Coincident(g45,g46)
    c: Coincident(g46,g47)
    c: Coincident(g47,g48)
    c: Coincident(g48,g45)
    c: Horizontal(g46)
    c: Horizontal(g48)
    c: Vertical(g45)
    c: Vertical(g47)
    c: Symmetric(g46,g45,g49)
    c: Coincident(g50,g51)
    c: Coincident(g51,g52)
    c: Coincident(g52,g53)
    c: Coincident(g53,g50)
    c: Horizontal(g51)
    c: Horizontal(g53)
    c: Vertical(g50)
    c: Vertical(g52)
    c: Symmetric(g51,g50,g54)
    c: Coincident(g55,g56)
    c: Coincident(g56,g57)
    c: Coincident(g57,g58)
    c: Coincident(g58,g55)
    c: Horizontal(g56)
    c: Horizontal(g58)
    c: Vertical(g55)
    c: Vertical(g57)
    c: Symmetric(g56,g55,g59)
    c: Coincident(g60,g61)
    c: Coincident(g61,g62)
    c: Coincident(g62,g63)
    c: Coincident(g63,g60)
    c: Horizontal(g61)
    c: Horizontal(g63)
    c: Vertical(g60)
    c: Vertical(g62)
    c: Symmetric(g61,g60,g64)
    c: Coincident(g65,g66)
    c: Coincident(g66,g67)
    c: Coincident(g67,g68)
    c: Coincident(g68,g65)
    c: Horizontal(g66)
    c: Horizontal(g68)
    c: Vertical(g65)
    c: Vertical(g67)
    c: Symmetric(g66,g65,g69)
    c: Coincident(g70,g71)
    c: Coincident(g71,g72)
    c: Coincident(g72,g73)
    c: Coincident(g73,g70)
    c: Horizontal(g71)
    c: Horizontal(g73)
    c: Vertical(g70)
    c: Vertical(g72)
    c: Symmetric(g71,g70,g74)
    c: DistanceX(g4,g9) = 23.8125
    c: Horizontal(g4,g9)
    c: Horizontal(g9,g14)
    c: Horizontal(g14,g19)
    c: Horizontal(g19,g24)
    c: Horizontal(g24,g29)
    c: Horizontal(g29,g34)
    c: Horizontal(g34,g39)
    c: Horizontal(g39,g44)
    c: Horizontal(g44,g49)
    c: Horizontal(g49,g54)
    c: Horizontal(g54,g59)
    c: Horizontal(g59,g64)
    c: Horizontal(g64,g69)
    c: Horizontal(g69,g74)
    c: DistanceX(g9,g14) = 19.05
    c: DistanceX(g14,g19) = 19.05
    c: DistanceX(g19,g24) = 19.05
    c: DistanceX(g29,g34) = 19.05
    c: DistanceX(g34,g39) = 19.05
    c: DistanceX(g39,g44) = 19.05
    c: DistanceX(g49,g54) = 19.05
    c: DistanceX(g54,g59) = 19.05
    c: DistanceX(g59,g64) = 19.05
    c: DistanceX(g24,g29) = 19.05
    c: DistanceX(g44,g49) = 19.05
    c: DistanceX(g64,g69) = 23.8125
    c: DistanceX(g69,g74) = 33.3375
    c: Equal(g72,g73)
    c: Equal(g73,g67)
    c: Equal(g67,g68)
    c: Equal(g68,g62)
    c: Equal(g62,g63)
    c: Equal(g63,g57)
    c: Equal(g57,g58)
    c: Equal(g58,g52)
    c: Equal(g52,g53)
    c: Equal(g53,g47)
    c: Equal(g47,g48)
    c: Equal(g48,g42)
    c: Equal(g42,g43)
    c: Equal(g43,g37)
    c: Equal(g37,g38)
    c: Equal(g38,g32)
    c: Equal(g32,g33)
    c: Equal(g33,g27)
    c: Equal(g27,g28)
    c: Equal(g28,g22)
    c: Equal(g22,g23)
    c: Equal(g23,g17)
    c: Equal(g17,g18)
    c: Equal(g18,g12)
    c: Equal(g12,g13)
    c: Equal(g13,g7)
    c: Equal(g7,g8)
    c: Equal(g8,g2)
    c: Equal(g2,g3)
FEATURE [PartDesign::Pocket] Pocket047
  BaseFeature = -> Pocket046
  Direction = (0,0,-1)
  Length = 5
  Length2 = 5
  Profile = -> Sketch062
  ReferenceAxis = -> Sketch062 [N_Axis]
  Type = 0
FEATURE [Sketcher::SketchObject] Sketch063
  AttachmentOffset = pos=(0,0,4.1) rot=(0,0,1;0rad)
  FullyConstrained = true
  MapMode = 5
  Placement = pos=(0,0,4.1) rot=(0,0,1;0rad)
  Support = -> [XY_Plane209]
  expr: Constraints[10] = Spreadsheet.PCB_width - Spreadsheet.u * 2.75
  expr: Constraints[11] = Spreadsheet.u * 2.875
  expr: Constraints[129] = Spreadsheet.u * 1.375
  expr: Constraints[143] = Spreadsheet.u
  expr: Constraints[144] = Spreadsheet.u
  expr: Constraints[145] = Spreadsheet.u
  expr: Constraints[146] = Spreadsheet.u
  expr: Constraints[147] = Spreadsheet.u
  expr: Constraints[148] = Spreadsheet.u
  expr: Constraints[149] = Spreadsheet.u
  expr: Constraints[150] = Spreadsheet.u
  expr: Constraints[151] = Spreadsheet.u * (0.5 + 1.125)
  expr: Constraints[152] = Spreadsheet.u
  expr: Constraints[153] = Spreadsheet.u
  expr: Constraints[154] = Spreadsheet.u * (1.125 + 1)
  expr: Constraints[9] = Spreadsheet.switch_hole + 0.2
  sketch-geometry (70):
    g0: LineSegment StartX=47.6687 StartY=-79.5125 StartZ=0 EndX=47.6687 EndY=-93.7125 EndZ=0
    g1: LineSegment StartX=47.6687 StartY=-93.7125 StartZ=0 EndX=61.8687 EndY=-93.7125 EndZ=0
    g2: LineSegment StartX=61.8687 StartY=-93.7125 StartZ=0 EndX=61.8687 EndY=-79.5125 EndZ=0
    g3: LineSegment StartX=61.8687 StartY=-79.5125 StartZ=0 EndX=47.6687 EndY=-79.5125 EndZ=0
    g4: GeomPoint X=54.7688 Y=-86.6125 Z=0
    g5: LineSegment StartX=73.8625 StartY=-79.5125 StartZ=0 EndX=73.8625 EndY=-93.7125 EndZ=0
    g6: LineSegment StartX=73.8625 StartY=-93.7125 StartZ=0 EndX=88.0625 EndY=-93.7125 EndZ=0
    g7: LineSegment StartX=88.0625 StartY=-93.7125 StartZ=0 EndX=88.0625 EndY=-79.5125 EndZ=0
    g8: LineSegment StartX=88.0625 StartY=-79.5125 StartZ=0 EndX=73.8625 EndY=-79.5125 EndZ=0
    g9: GeomPoint X=80.9625 Y=-86.6125 Z=0
    g10: LineSegment StartX=92.9125 StartY=-79.5125 StartZ=0 EndX=92.9125 EndY=-93.7125 EndZ=0
    g11: LineSegment StartX=92.9125 StartY=-93.7125 StartZ=0 EndX=107.113 EndY=-93.7125 EndZ=0
    g12: LineSegment StartX=107.113 StartY=-93.7125 StartZ=0 EndX=107.113 EndY=-79.5125 EndZ=0
    g13: LineSegment StartX=107.113 StartY=-79.5125 StartZ=0 EndX=92.9125 EndY=-79.5125 EndZ=0
    g14: GeomPoint X=100.013 Y=-86.6125 Z=0
    g15: LineSegment StartX=111.962 StartY=-79.5125 StartZ=0 EndX=111.962 EndY=-93.7125 EndZ=0
    g16: LineSegment StartX=111.962 StartY=-93.7125 StartZ=0 EndX=126.163 EndY=-93.7125 EndZ=0
    g17: LineSegment StartX=126.163 StartY=-93.7125 StartZ=0 EndX=126.163 EndY=-79.5125 EndZ=0
    g18: LineSegment StartX=126.163 StartY=-79.5125 StartZ=0 EndX=111.962 EndY=-79.5125 EndZ=0
    g19: GeomPoint X=119.063 Y=-86.6125 Z=0
    g20: LineSegment StartX=131.012 StartY=-79.5125 StartZ=0 EndX=131.012 EndY=-93.7125 EndZ=0
    g21: LineSegment StartX=131.012 StartY=-93.7125 StartZ=0 EndX=145.213 EndY=-93.7125 EndZ=0
    g22: LineSegment StartX=145.213 StartY=-93.7125 StartZ=0 EndX=145.213 EndY=-79.5125 EndZ=0
    g23: LineSegment StartX=145.213 StartY=-79.5125 StartZ=0 EndX=131.012 EndY=-79.5125 EndZ=0
    g24: GeomPoint X=138.113 Y=-86.6125 Z=0
    g25: LineSegment StartX=150.062 StartY=-79.5125 StartZ=0 EndX=150.062 EndY=-93.7125 EndZ=0
    g26: LineSegment StartX=150.062 StartY=-93.7125 StartZ=0 EndX=164.263 EndY=-93.7125 EndZ=0
    g27: LineSegment StartX=164.263 StartY=-93.7125 StartZ=0 EndX=164.263 EndY=-79.5125 EndZ=0
    g28: LineSegment StartX=164.263 StartY=-79.5125 StartZ=0 EndX=150.062 EndY=-79.5125 EndZ=0
    g29: GeomPoint X=157.162 Y=-86.6125 Z=0
    g30: LineSegment StartX=169.112 StartY=-79.5125 StartZ=0 EndX=169.112 EndY=-93.7125 EndZ=0
    g31: LineSegment StartX=169.112 StartY=-93.7125 StartZ=0 EndX=183.313 EndY=-93.7125 EndZ=0
    g32: LineSegment StartX=183.313 StartY=-93.7125 StartZ=0 EndX=183.313 EndY=-79.5125 EndZ=0
    g33: LineSegment StartX=183.313 StartY=-79.5125 StartZ=0 EndX=169.112 EndY=-79.5125 EndZ=0
    g34: GeomPoint X=176.213 Y=-86.6125 Z=0
    g35: LineSegment StartX=188.162 StartY=-79.5125 StartZ=0 EndX=188.162 EndY=-93.7125 EndZ=0
    g36: LineSegment StartX=188.162 StartY=-93.7125 StartZ=0 EndX=202.363 EndY=-93.7125 EndZ=0
    g37: LineSegment StartX=202.363 StartY=-93.7125 StartZ=0 EndX=202.363 EndY=-79.5125 EndZ=0
    g38: LineSegment StartX=202.363 StartY=-79.5125 StartZ=0 EndX=188.162 EndY=-79.5125 EndZ=0
    g39: GeomPoint X=195.263 Y=-86.6125 Z=0
    g40: LineSegment StartX=207.212 StartY=-79.5125 StartZ=0 EndX=207.212 EndY=-93.7125 EndZ=0
    g41: LineSegment StartX=207.212 StartY=-93.7125 StartZ=0 EndX=221.413 EndY=-93.7125 EndZ=0
    g42: LineSegment StartX=221.413 StartY=-93.7125 StartZ=0 EndX=221.413 EndY=-79.5125 EndZ=0
    g43: LineSegment StartX=221.413 StartY=-79.5125 StartZ=0 EndX=207.212 EndY=-79.5125 EndZ=0
    g44: GeomPoint X=214.312 Y=-86.6125 Z=0
    g45: LineSegment StartX=226.262 StartY=-79.5125 StartZ=0 EndX=226.262 EndY=-93.7125 EndZ=0
    g46: LineSegment StartX=226.262 StartY=-93.7125 StartZ=0 EndX=240.463 EndY=-93.7125 EndZ=0
    g47: LineSegment StartX=240.463 StartY=-93.7125 StartZ=0 EndX=240.463 EndY=-79.5125 EndZ=0
    g48: LineSegment StartX=240.463 StartY=-79.5125 StartZ=0 EndX=226.262 EndY=-79.5125 EndZ=0
    g49: GeomPoint X=233.363 Y=-86.6125 Z=0
    g50: LineSegment StartX=245.312 StartY=-79.5125 StartZ=0 EndX=245.312 EndY=-93.7125 EndZ=0
    g51: LineSegment StartX=245.312 StartY=-93.7125 StartZ=0 EndX=259.513 EndY=-93.7125 EndZ=0
    g52: LineSegment StartX=259.513 StartY=-93.7125 StartZ=0 EndX=259.513 EndY=-79.5125 EndZ=0
    g53: LineSegment StartX=259.513 StartY=-79.5125 StartZ=0 EndX=245.312 EndY=-79.5125 EndZ=0
    g54: GeomPoint X=252.413 Y=-86.6125 Z=0
    g55: LineSegment StartX=264.362 StartY=-79.5125 StartZ=0 EndX=264.362 EndY=-93.7125 EndZ=0
    g56: LineSegment StartX=264.362 StartY=-93.7125 StartZ=0 EndX=278.563 EndY=-93.7125 EndZ=0
    g57: LineSegment StartX=278.563 StartY=-93.7125 StartZ=0 EndX=278.563 EndY=-79.5125 EndZ=0
    g58: LineSegment StartX=278.563 StartY=-79.5125 StartZ=0 EndX=264.362 EndY=-79.5125 EndZ=0
    g59: GeomPoint X=271.463 Y=-86.6125 Z=0
    g60: LineSegment StartX=295.319 StartY=-79.5125 StartZ=0 EndX=295.319 EndY=-93.7125 EndZ=0
    g61: LineSegment StartX=295.319 StartY=-93.7125 StartZ=0 EndX=309.519 EndY=-93.7125 EndZ=0
    g62: LineSegment StartX=309.519 StartY=-93.7125 StartZ=0 EndX=309.519 EndY=-79.5125 EndZ=0
    g63: LineSegment StartX=309.519 StartY=-79.5125 StartZ=0 EndX=295.319 EndY=-79.5125 EndZ=0
    g64: GeomPoint X=302.419 Y=-86.6125 Z=0
    g65: LineSegment StartX=335.8 StartY=-79.5125 StartZ=0 EndX=335.8 EndY=-93.7125 EndZ=0
    g66: LineSegment StartX=335.8 StartY=-93.7125 StartZ=0 EndX=350 EndY=-93.7125 EndZ=0
    g67: LineSegment StartX=350 StartY=-93.7125 StartZ=0 EndX=350 EndY=-79.5125 EndZ=0
    g68: LineSegment StartX=350 StartY=-79.5125 StartZ=0 EndX=335.8 EndY=-79.5125 EndZ=0
    g69: GeomPoint X=342.9 Y=-86.6125 Z=0
  constraints (182):
    c: Coincident(g0,g1)
    c: Coincident(g1,g2)
    c: Coincident(g2,g3)
    c: Coincident(g3,g0)
    c: Horizontal(g1)
    c: Horizontal(g3)
    c: Vertical(g0)
    c: Vertical(g2)
    c: Symmetric(g1,g0,g4)
    c: DistanceX(g3,g3) = 14.2
    c: DistanceY(g4,g-1) = 86.6125
    c: DistanceX(g-1,g4) = 54.7688
    c: Coincident(g5,g6)
    c: Coincident(g6,g7)
    c: Coincident(g7,g8)
    c: Coincident(g8,g5)
    c: Horizontal(g6)
    c: Horizontal(g8)
    c: Vertical(g5)
    c: Vertical(g7)
    c: Symmetric(g6,g5,g9)
    c: Coincident(g10,g11)
    c: Coincident(g11,g12)
    c: Coincident(g12,g13)
    c: Coincident(g13,g10)
    c: Horizontal(g11)
    c: Horizontal(g13)
    c: Vertical(g10)
    c: Vertical(g12)
    c: Symmetric(g11,g10,g14)
    c: Coincident(g15,g16)
    c: Coincident(g16,g17)
    c: Coincident(g17,g18)
    c: Coincident(g18,g15)
    c: Horizontal(g16)
    c: Horizontal(g18)
    c: Vertical(g15)
    c: Vertical(g17)
    c: Symmetric(g16,g15,g19)
    c: Coincident(g20,g21)
    c: Coincident(g21,g22)
    c: Coincident(g22,g23)
    c: Coincident(g23,g20)
    c: Horizontal(g21)
    c: Horizontal(g23)
    c: Vertical(g20)
    c: Vertical(g22)
    c: Symmetric(g21,g20,g24)
    c: Coincident(g25,g26)
    c: Coincident(g26,g27)
    c: Coincident(g27,g28)
    c: Coincident(g28,g25)
    c: Horizontal(g26)
    c: Horizontal(g28)
    c: Vertical(g25)
    c: Vertical(g27)
    c: Symmetric(g26,g25,g29)
    c: Coincident(g30,g31)
    c: Coincident(g31,g32)
    c: Coincident(g32,g33)
    c: Coincident(g33,g30)
    c: Horizontal(g31)
    c: Horizontal(g33)
    c: Vertical(g30)
    c: Vertical(g32)
    c: Symmetric(g31,g30,g34)
    c: Coincident(g35,g36)
    c: Coincident(g36,g37)
    c: Coincident(g37,g38)
    c: Coincident(g38,g35)
    c: Horizontal(g36)
    c: Horizontal(g38)
    c: Vertical(g35)
    c: Vertical(g37)
    c: Symmetric(g36,g35,g39)
    c: Coincident(g40,g41)
    c: Coincident(g41,g42)
    c: Coincident(g42,g43)
    c: Coincident(g43,g40)
    c: Horizontal(g41)
    c: Horizontal(g43)
    c: Vertical(g40)
    c: Vertical(g42)
    c: Symmetric(g41,g40,g44)
    c: Coincident(g45,g46)
    c: Coincident(g46,g47)
    c: Coincident(g47,g48)
    c: Coincident(g48,g45)
    c: Horizontal(g46)
    c: Horizontal(g48)
    c: Vertical(g45)
    c: Vertical(g47)
    c: Symmetric(g46,g45,g49)
    c: Coincident(g50,g51)
    c: Coincident(g51,g52)
    c: Coincident(g52,g53)
    c: Coincident(g53,g50)
    c: Horizontal(g51)
    c: Horizontal(g53)
    c: Vertical(g50)
    c: Vertical(g52)
    c: Symmetric(g51,g50,g54)
    c: Coincident(g55,g56)
    c: Coincident(g56,g57)
    c: Coincident(g57,g58)
    c: Coincident(g58,g55)
    c: Horizontal(g56)
    c: Horizontal(g58)
    c: Vertical(g55)
    c: Vertical(g57)
    c: Symmetric(g56,g55,g59)
    c: Coincident(g60,g61)
    c: Coincident(g61,g62)
    c: Coincident(g62,g63)
    c: Coincident(g63,g60)
    c: Horizontal(g61)
    c: Horizontal(g63)
    c: Vertical(g60)
    c: Vertical(g62)
    c: Symmetric(g61,g60,g64)
    c: Coincident(g65,g66)
    c: Coincident(g66,g67)
    c: Coincident(g67,g68)
    c: Coincident(g68,g65)
    c: Horizontal(g66)
    c: Horizontal(g68)
    c: Vertical(g65)
    c: Vertical(g67)
    c: Symmetric(g66,g65,g69)
    c: DistanceX(g4,g9) = 26.1938
    c: Horizontal(g4,g9)
    c: Horizontal(g9,g14)
    c: Horizontal(g14,g19)
    c: Horizontal(g19,g24)
    c: Horizontal(g24,g29)
    c: Horizontal(g29,g34)
    c: Horizontal(g34,g39)
    c: Horizontal(g39,g44)
    c: Horizontal(g44,g49)
    c: Horizontal(g49,g54)
    c: Horizontal(g54,g59)
    c: Horizontal(g59,g64)
    c: Horizontal(g64,g69)
    c: DistanceX(g9,g14) = 19.05
    c: DistanceX(g14,g19) = 19.05
    c: DistanceX(g19,g24) = 19.05
    c: DistanceX(g29,g34) = 19.05
    c: DistanceX(g34,g39) = 19.05
    c: DistanceX(g39,g44) = 19.05
    c: DistanceX(g49,g54) = 19.05
    c: DistanceX(g54,g59) = 19.05
    c: DistanceX(g59,g64) = 30.9563
    c: DistanceX(g24,g29) = 19.05
    c: DistanceX(g44,g49) = 19.05
    c: DistanceX(g64,g69) = 40.4813
    c: Equal(g67,g68)
    c: Equal(g68,g62)
    c: Equal(g62,g63)
    c: Equal(g63,g57)
    c: Equal(g57,g58)
    c: Equal(g58,g52)
    c: Equal(g52,g53)
    c: Equal(g53,g47)
    c: Equal(g47,g48)
    c: Equal(g48,g42)
    c: Equal(g42,g43)
    c: Equal(g43,g37)
    c: Equal(g37,g38)
    c: Equal(g38,g32)
    c: Equal(g32,g33)
    c: Equal(g33,g27)
    c: Equal(g27,g28)
    c: Equal(g28,g22)
    c: Equal(g22,g23)
    c: Equal(g23,g17)
    c: Equal(g17,g18)
    c: Equal(g18,g12)
    c: Equal(g12,g13)
    c: Equal(g13,g7)
    c: Equal(g7,g8)
    c: Equal(g8,g2)
    c: Equal(g2,g3)
FEATURE [PartDesign::Pocket] Pocket048
  BaseFeature = -> Pocket047
  Direction = (0,0,-1)
  Length = 5
  Length2 = 5
  Profile = -> Sketch063
  ReferenceAxis = -> Sketch063 [N_Axis]
  Type = 0
FEATURE [Sketcher::SketchObject] Sketch064
  AttachmentOffset = pos=(0,0,4.1) rot=(0,0,1;0rad)
  FullyConstrained = true
  MapMode = 5
  Placement = pos=(0,0,4.1) rot=(0,0,1;0rad)
  Support = -> [XY_Plane209]
  expr: Constraints[10] = Spreadsheet.PCB_width - Spreadsheet.u * 1.75
  expr: Constraints[11] = Spreadsheet.u * (2 + 1.125)
  expr: Constraints[129] = Spreadsheet.u * (1.125 + 0.5)
  expr: Constraints[141] = Spreadsheet.u
  expr: Constraints[142] = Spreadsheet.u
  expr: Constraints[143] = Spreadsheet.u
  expr: Constraints[144] = Spreadsheet.u
  expr: Constraints[145] = Spreadsheet.u
  expr: Constraints[146] = Spreadsheet.u
  expr: Constraints[147] = Spreadsheet.u
  expr: Constraints[148] = Spreadsheet.u * (0.5 + 1.75 / 2)
  expr: Constraints[149] = Spreadsheet.u * (0.5 + 1.125)
  expr: Constraints[150] = Spreadsheet.u
  expr: Constraints[151] = Spreadsheet.u
  expr: Constraints[152] = Spreadsheet.u * 1.25
  expr: Constraints[154] = Spreadsheet.u * 0.25
  expr: Constraints[9] = Spreadsheet.switch_hole + 0.2
  sketch-geometry (70):
    g0: LineSegment StartX=52.4312 StartY=-98.5625 StartZ=0 EndX=52.4312 EndY=-112.763 EndZ=0
    g1: LineSegment StartX=52.4312 StartY=-112.763 StartZ=0 EndX=66.6312 EndY=-112.763 EndZ=0
    g2: LineSegment StartX=66.6312 StartY=-112.763 StartZ=0 EndX=66.6312 EndY=-98.5625 EndZ=0
    g3: LineSegment StartX=66.6312 StartY=-98.5625 StartZ=0 EndX=52.4312 EndY=-98.5625 EndZ=0
    g4: GeomPoint X=59.5312 Y=-105.662 Z=0
    g5: LineSegment StartX=83.3875 StartY=-98.5625 StartZ=0 EndX=83.3875 EndY=-112.762 EndZ=0
    g6: LineSegment StartX=83.3875 StartY=-112.762 StartZ=0 EndX=97.5875 EndY=-112.762 EndZ=0
    g7: LineSegment StartX=97.5875 StartY=-112.762 StartZ=0 EndX=97.5875 EndY=-98.5625 EndZ=0
    g8: LineSegment StartX=97.5875 StartY=-98.5625 StartZ=0 EndX=83.3875 EndY=-98.5625 EndZ=0
    g9: GeomPoint X=90.4875 Y=-105.662 Z=0
    g10: LineSegment StartX=102.437 StartY=-98.5625 StartZ=0 EndX=102.437 EndY=-112.763 EndZ=0
    g11: LineSegment StartX=102.437 StartY=-112.763 StartZ=0 EndX=116.638 EndY=-112.763 EndZ=0
    g12: LineSegment StartX=116.638 StartY=-112.763 StartZ=0 EndX=116.638 EndY=-98.5625 EndZ=0
    g13: LineSegment StartX=116.638 StartY=-98.5625 StartZ=0 EndX=102.437 EndY=-98.5625 EndZ=0
    g14: GeomPoint X=109.537 Y=-105.662 Z=0
    g15: LineSegment StartX=121.487 StartY=-98.5625 StartZ=0 EndX=121.487 EndY=-112.763 EndZ=0
    g16: LineSegment StartX=121.487 StartY=-112.763 StartZ=0 EndX=135.688 EndY=-112.763 EndZ=0
    g17: LineSegment StartX=135.688 StartY=-112.763 StartZ=0 EndX=135.688 EndY=-98.5625 EndZ=0
    g18: LineSegment StartX=135.688 StartY=-98.5625 StartZ=0 EndX=121.487 EndY=-98.5625 EndZ=0
    g19: GeomPoint X=128.588 Y=-105.662 Z=0
    g20: LineSegment StartX=140.537 StartY=-98.5625 StartZ=0 EndX=140.537 EndY=-112.763 EndZ=0
    g21: LineSegment StartX=140.537 StartY=-112.763 StartZ=0 EndX=154.738 EndY=-112.763 EndZ=0
    g22: LineSegment StartX=154.738 StartY=-112.763 StartZ=0 EndX=154.738 EndY=-98.5625 EndZ=0
    g23: LineSegment StartX=154.738 StartY=-98.5625 StartZ=0 EndX=140.537 EndY=-98.5625 EndZ=0
    g24: GeomPoint X=147.638 Y=-105.662 Z=0
    g25: LineSegment StartX=159.587 StartY=-98.5625 StartZ=0 EndX=159.587 EndY=-112.763 EndZ=0
    g26: LineSegment StartX=159.587 StartY=-112.763 StartZ=0 EndX=173.788 EndY=-112.763 EndZ=0
    g27: LineSegment StartX=173.788 StartY=-112.763 StartZ=0 EndX=173.788 EndY=-98.5625 EndZ=0
    g28: LineSegment StartX=173.788 StartY=-98.5625 StartZ=0 EndX=159.587 EndY=-98.5625 EndZ=0
    g29: GeomPoint X=166.688 Y=-105.662 Z=0
    g30: LineSegment StartX=178.637 StartY=-98.5625 StartZ=0 EndX=178.637 EndY=-112.763 EndZ=0
    g31: LineSegment StartX=178.637 StartY=-112.763 StartZ=0 EndX=192.838 EndY=-112.763 EndZ=0
    g32: LineSegment StartX=192.838 StartY=-112.763 StartZ=0 EndX=192.838 EndY=-98.5625 EndZ=0
    g33: LineSegment StartX=192.838 StartY=-98.5625 StartZ=0 EndX=178.637 EndY=-98.5625 EndZ=0
    g34: GeomPoint X=185.738 Y=-105.662 Z=0
    g35: LineSegment StartX=197.687 StartY=-98.5625 StartZ=0 EndX=197.687 EndY=-112.763 EndZ=0
    g36: LineSegment StartX=197.687 StartY=-112.763 StartZ=0 EndX=211.888 EndY=-112.763 EndZ=0
    g37: LineSegment StartX=211.888 StartY=-112.763 StartZ=0 EndX=211.888 EndY=-98.5625 EndZ=0
    g38: LineSegment StartX=211.888 StartY=-98.5625 StartZ=0 EndX=197.687 EndY=-98.5625 EndZ=0
    g39: GeomPoint X=204.787 Y=-105.662 Z=0
    g40: LineSegment StartX=216.737 StartY=-98.5625 StartZ=0 EndX=216.737 EndY=-112.763 EndZ=0
    g41: LineSegment StartX=216.737 StartY=-112.763 StartZ=0 EndX=230.938 EndY=-112.763 EndZ=0
    g42: LineSegment StartX=230.938 StartY=-112.763 StartZ=0 EndX=230.938 EndY=-98.5625 EndZ=0
    g43: LineSegment StartX=230.938 StartY=-98.5625 StartZ=0 EndX=216.737 EndY=-98.5625 EndZ=0
    g44: GeomPoint X=223.838 Y=-105.662 Z=0
    g45: LineSegment StartX=235.787 StartY=-98.5625 StartZ=0 EndX=235.787 EndY=-112.763 EndZ=0
    g46: LineSegment StartX=235.787 StartY=-112.763 StartZ=0 EndX=249.988 EndY=-112.763 EndZ=0
    g47: LineSegment StartX=249.988 StartY=-112.763 StartZ=0 EndX=249.988 EndY=-98.5625 EndZ=0
    g48: LineSegment StartX=249.988 StartY=-98.5625 StartZ=0 EndX=235.787 EndY=-98.5625 EndZ=0
    g49: GeomPoint X=242.888 Y=-105.662 Z=0
    g50: LineSegment StartX=254.837 StartY=-98.5625 StartZ=0 EndX=254.837 EndY=-112.763 EndZ=0
    g51: LineSegment StartX=254.837 StartY=-112.763 StartZ=0 EndX=269.038 EndY=-112.763 EndZ=0
    g52: LineSegment StartX=269.038 StartY=-112.763 StartZ=0 EndX=269.038 EndY=-98.5625 EndZ=0
    g53: LineSegment StartX=269.038 StartY=-98.5625 StartZ=0 EndX=254.837 EndY=-98.5625 EndZ=0
    g54: GeomPoint X=261.938 Y=-105.662 Z=0
    g55: LineSegment StartX=281.031 StartY=-98.5625 StartZ=0 EndX=281.031 EndY=-112.763 EndZ=0
    g56: LineSegment StartX=281.031 StartY=-112.763 StartZ=0 EndX=295.231 EndY=-112.763 EndZ=0
    g57: LineSegment StartX=295.231 StartY=-112.763 StartZ=0 EndX=295.231 EndY=-98.5625 EndZ=0
    g58: LineSegment StartX=295.231 StartY=-98.5625 StartZ=0 EndX=281.031 EndY=-98.5625 EndZ=0
    g59: GeomPoint X=288.131 Y=-105.662 Z=0
    g60: LineSegment StartX=311.987 StartY=-103.325 StartZ=0 EndX=311.987 EndY=-117.525 EndZ=0
    g61: LineSegment StartX=311.987 StartY=-117.525 StartZ=0 EndX=326.188 EndY=-117.525 EndZ=0
    g62: LineSegment StartX=326.188 StartY=-117.525 StartZ=0 EndX=326.188 EndY=-103.325 EndZ=0
    g63: LineSegment StartX=326.188 StartY=-103.325 StartZ=0 EndX=311.987 EndY=-103.325 EndZ=0
    g64: GeomPoint X=319.088 Y=-110.425 Z=0
    g65: LineSegment StartX=335.8 StartY=-98.5625 StartZ=0 EndX=335.8 EndY=-112.763 EndZ=0
    g66: LineSegment StartX=335.8 StartY=-112.763 StartZ=0 EndX=350 EndY=-112.763 EndZ=0
    g67: LineSegment StartX=350 StartY=-112.763 StartZ=0 EndX=350 EndY=-98.5625 EndZ=0
    g68: LineSegment StartX=350 StartY=-98.5625 StartZ=0 EndX=335.8 EndY=-98.5625 EndZ=0
    g69: GeomPoint X=342.9 Y=-105.662 Z=0
  constraints (182):
    c: Coincident(g0,g1)
    c: Coincident(g1,g2)
    c: Coincident(g2,g3)
    c: Coincident(g3,g0)
    c: Horizontal(g1)
    c: Horizontal(g3)
    c: Vertical(g0)
    c: Vertical(g2)
    c: Symmetric(g1,g0,g4)
    c: DistanceX(g3,g3) = 14.2
    c: DistanceY(g4,g-1) = 105.662
    c: DistanceX(g-1,g4) = 59.5312
    c: Coincident(g5,g6)
    c: Coincident(g6,g7)
    c: Coincident(g7,g8)
    c: Coincident(g8,g5)
    c: Horizontal(g6)
    c: Horizontal(g8)
    c: Vertical(g5)
    c: Vertical(g7)
    c: Symmetric(g6,g5,g9)
    c: Coincident(g10,g11)
    c: Coincident(g11,g12)
    c: Coincident(g12,g13)
    c: Coincident(g13,g10)
    c: Horizontal(g11)
    c: Horizontal(g13)
    c: Vertical(g10)
    c: Vertical(g12)
    c: Symmetric(g11,g10,g14)
    c: Coincident(g15,g16)
    c: Coincident(g16,g17)
    c: Coincident(g17,g18)
    c: Coincident(g18,g15)
    c: Horizontal(g16)
    c: Horizontal(g18)
    c: Vertical(g15)
    c: Vertical(g17)
    c: Symmetric(g16,g15,g19)
    c: Coincident(g20,g21)
    c: Coincident(g21,g22)
    c: Coincident(g22,g23)
    c: Coincident(g23,g20)
    c: Horizontal(g21)
    c: Horizontal(g23)
    c: Vertical(g20)
    c: Vertical(g22)
    c: Symmetric(g21,g20,g24)
    c: Coincident(g25,g26)
    c: Coincident(g26,g27)
    c: Coincident(g27,g28)
    c: Coincident(g28,g25)
    c: Horizontal(g26)
    c: Horizontal(g28)
    c: Vertical(g25)
    c: Vertical(g27)
    c: Symmetric(g26,g25,g29)
    c: Coincident(g30,g31)
    c: Coincident(g31,g32)
    c: Coincident(g32,g33)
    c: Coincident(g33,g30)
    c: Horizontal(g31)
    c: Horizontal(g33)
    c: Vertical(g30)
    c: Vertical(g32)
    c: Symmetric(g31,g30,g34)
    c: Coincident(g35,g36)
    c: Coincident(g36,g37)
    c: Coincident(g37,g38)
    c: Coincident(g38,g35)
    c: Horizontal(g36)
    c: Horizontal(g38)
    c: Vertical(g35)
    c: Vertical(g37)
    c: Symmetric(g36,g35,g39)
    c: Coincident(g40,g41)
    c: Coincident(g41,g42)
    c: Coincident(g42,g43)
    c: Coincident(g43,g40)
    c: Horizontal(g41)
    c: Horizontal(g43)
    c: Vertical(g40)
    c: Vertical(g42)
    c: Symmetric(g41,g40,g44)
    c: Coincident(g45,g46)
    c: Coincident(g46,g47)
    c: Coincident(g47,g48)
    c: Coincident(g48,g45)
    c: Horizontal(g46)
    c: Horizontal(g48)
    c: Vertical(g45)
    c: Vertical(g47)
    c: Symmetric(g46,g45,g49)
    c: Coincident(g50,g51)
    c: Coincident(g51,g52)
    c: Coincident(g52,g53)
    c: Coincident(g53,g50)
    c: Horizontal(g51)
    c: Horizontal(g53)
    c: Vertical(g50)
    c: Vertical(g52)
    c: Symmetric(g51,g50,g54)
    c: Coincident(g55,g56)
    c: Coincident(g56,g57)
    c: Coincident(g57,g58)
    c: Coincident(g58,g55)
    c: Horizontal(g56)
    c: Horizontal(g58)
    c: Vertical(g55)
    c: Vertical(g57)
    c: Symmetric(g56,g55,g59)
    c: Coincident(g60,g61)
    c: Coincident(g61,g62)
    c: Coincident(g62,g63)
    c: Coincident(g63,g60)
    c: Horizontal(g61)
    c: Horizontal(g63)
    c: Vertical(g60)
    c: Vertical(g62)
    c: Symmetric(g61,g60,g64)
    c: Coincident(g65,g66)
    c: Coincident(g66,g67)
    c: Coincident(g67,g68)
    c: Coincident(g68,g65)
    c: Horizontal(g66)
    c: Horizontal(g68)
    c: Vertical(g65)
    c: Vertical(g67)
    c: Symmetric(g66,g65,g69)
    c: DistanceX(g4,g9) = 30.9563
    c: Horizontal(g4,g9)
    c: Horizontal(g9,g14)
    c: Horizontal(g14,g19)
    c: Horizontal(g19,g24)
    c: Horizontal(g24,g29)
    c: Horizontal(g29,g34)
    c: Horizontal(g34,g39)
    c: Horizontal(g39,g44)
    c: Horizontal(g44,g49)
    c: Horizontal(g49,g54)
    c: Horizontal(g54,g59)
    c: DistanceX(g9,g14) = 19.05
    c: DistanceX(g14,g19) = 19.05
    c: DistanceX(g19,g24) = 19.05
    c: DistanceX(g29,g34) = 19.05
    c: DistanceX(g34,g39) = 19.05
    c: DistanceX(g39,g44) = 19.05
    c: DistanceX(g49,g54) = 19.05
    c: DistanceX(g54,g59) = 26.1938
    c: DistanceX(g59,g64) = 30.9563
    c: DistanceX(g24,g29) = 19.05
    c: DistanceX(g44,g49) = 19.05
    c: DistanceX(g64,g69) = 23.8125
    c: Horizontal(g59,g69)
    c: DistanceY(g64,g59) = 4.7625
    c: Equal(g3,g2)
    c: Equal(g8,g3)
    c: Equal(g8,g7)
    c: Equal(g13,g8)
    c: Equal(g13,g12)
    c: Equal(g67,g68)
    c: Equal(g68,g62)
    c: Equal(g62,g63)
    c: Equal(g63,g57)
    c: Equal(g57,g58)
    c: Equal(g58,g52)
    c: Equal(g52,g53)
    c: Equal(g53,g47)
    c: Equal(g47,g48)
    c: Equal(g48,g42)
    c: Equal(g42,g43)
    c: Equal(g43,g37)
    c: Equal(g37,g38)
    c: Equal(g38,g32)
    c: Equal(g32,g33)
    c: Equal(g33,g27)
    c: Equal(g27,g28)
    c: Equal(g28,g22)
    c: Equal(g22,g23)
    c: Equal(g23,g17)
    c: Equal(g17,g18)
    c: Equal(g18,g12)
FEATURE [PartDesign::Pocket] Pocket049
  BaseFeature = -> Pocket048
  Direction = (0,0,-1)
  Length = 5
  Length2 = 5
  Profile = -> Sketch064
  ReferenceAxis = -> Sketch064 [N_Axis]
  Type = 0
FEATURE [Sketcher::SketchObject] Sketch065
  AttachmentOffset = pos=(0,0,4.1) rot=(0,0,1;0rad)
  FullyConstrained = true
  MapMode = 5
  Placement = pos=(0,0,4.1) rot=(0,0,1;0rad)
  Support = -> [XY_Plane209]
  expr: Constraints[10] = Spreadsheet.PCB_width - Spreadsheet.u * 0.75
  expr: Constraints[110] = Spreadsheet.u
  expr: Constraints[11] = Spreadsheet.u * (2 + 1.25 / 2)
  expr: Constraints[84] = Spreadsheet.u * 1.25
  expr: Constraints[90] = Spreadsheet.u * 1.25
  expr: Constraints[91] = Spreadsheet.u * (1.25 / 2 + 6.25 / 2)
  expr: Constraints[92] = Spreadsheet.u
  expr: Constraints[93] = Spreadsheet.u
  expr: Constraints[94] = Spreadsheet.u * (1 + 0.25)
  expr: Constraints[95] = Spreadsheet.u
  expr: Constraints[96] = Spreadsheet.u * 0.25
  expr: Constraints[97] = Spreadsheet.u * (6.25 / 2 + 0.5)
  expr: Constraints[9] = Spreadsheet.switch_hole + 0.2
  sketch-geometry (50):
    g0: LineSegment StartX=42.9063 StartY=-117.613 StartZ=0 EndX=42.9063 EndY=-131.812 EndZ=0
    g1: LineSegment StartX=42.9063 StartY=-131.812 StartZ=0 EndX=57.1063 EndY=-131.812 EndZ=0
    g2: LineSegment StartX=57.1063 StartY=-131.812 StartZ=0 EndX=57.1063 EndY=-117.613 EndZ=0
    g3: LineSegment StartX=57.1063 StartY=-117.613 StartZ=0 EndX=42.9063 EndY=-117.613 EndZ=0
    g4: GeomPoint X=50.0063 Y=-124.713 Z=0
    g5: LineSegment StartX=66.7188 StartY=-117.612 StartZ=0 EndX=66.7188 EndY=-131.812 EndZ=0
    g6: LineSegment StartX=66.7188 StartY=-131.812 StartZ=0 EndX=80.9188 EndY=-131.812 EndZ=0
    g7: LineSegment StartX=80.9188 StartY=-131.812 StartZ=0 EndX=80.9188 EndY=-117.612 EndZ=0
    g8: LineSegment StartX=80.9188 StartY=-117.612 StartZ=0 EndX=66.7188 EndY=-117.612 EndZ=0
    g9: GeomPoint X=73.8188 Y=-124.713 Z=0
    g10: LineSegment StartX=90.5313 StartY=-117.612 StartZ=0 EndX=90.5313 EndY=-131.812 EndZ=0
    g11: LineSegment StartX=90.5313 StartY=-131.812 StartZ=0 EndX=104.731 EndY=-131.812 EndZ=0
    g12: LineSegment StartX=104.731 StartY=-131.812 StartZ=0 EndX=104.731 EndY=-117.612 EndZ=0
    g13: LineSegment StartX=104.731 StartY=-117.612 StartZ=0 EndX=90.5313 EndY=-117.612 EndZ=0
    g14: GeomPoint X=97.6312 Y=-124.713 Z=0
    g15: LineSegment StartX=161.969 StartY=-117.613 StartZ=0 EndX=161.969 EndY=-131.813 EndZ=0
    g16: LineSegment StartX=161.969 StartY=-131.813 StartZ=0 EndX=176.169 EndY=-131.813 EndZ=0
    g17: LineSegment StartX=176.169 StartY=-131.813 StartZ=0 EndX=176.169 EndY=-117.613 EndZ=0
    g18: LineSegment StartX=176.169 StartY=-117.613 StartZ=0 EndX=161.969 EndY=-117.613 EndZ=0
    g19: GeomPoint X=169.069 Y=-124.713 Z=0
    g20: LineSegment StartX=231.025 StartY=-117.612 StartZ=0 EndX=231.025 EndY=-131.812 EndZ=0
    g21: LineSegment StartX=231.025 StartY=-131.812 StartZ=0 EndX=245.225 EndY=-131.812 EndZ=0
    g22: LineSegment StartX=245.225 StartY=-131.812 StartZ=0 EndX=245.225 EndY=-117.612 EndZ=0
    g23: LineSegment StartX=245.225 StartY=-117.612 StartZ=0 EndX=231.025 EndY=-117.612 EndZ=0
    g24: GeomPoint X=238.125 Y=-124.713 Z=0
    g25: LineSegment StartX=250.075 StartY=-117.613 StartZ=0 EndX=250.075 EndY=-131.813 EndZ=0
    g26: LineSegment StartX=250.075 StartY=-131.813 StartZ=0 EndX=264.275 EndY=-131.813 EndZ=0
    g27: LineSegment StartX=264.275 StartY=-131.813 StartZ=0 EndX=264.275 EndY=-117.613 EndZ=0
    g28: LineSegment StartX=264.275 StartY=-117.613 StartZ=0 EndX=250.075 EndY=-117.613 EndZ=0
    g29: GeomPoint X=257.175 Y=-124.713 Z=0
    g30: LineSegment StartX=269.125 StartY=-117.613 StartZ=0 EndX=269.125 EndY=-131.813 EndZ=0
    g31: LineSegment StartX=269.125 StartY=-131.813 StartZ=0 EndX=283.325 EndY=-131.813 EndZ=0
    g32: LineSegment StartX=283.325 StartY=-131.813 StartZ=0 EndX=283.325 EndY=-117.613 EndZ=0
    g33: LineSegment StartX=283.325 StartY=-117.613 StartZ=0 EndX=269.125 EndY=-117.613 EndZ=0
    g34: GeomPoint X=276.225 Y=-124.713 Z=0
    g35: LineSegment StartX=292.938 StartY=-122.375 StartZ=0 EndX=292.938 EndY=-136.575 EndZ=0
    g36: LineSegment StartX=292.938 StartY=-136.575 StartZ=0 EndX=307.138 EndY=-136.575 EndZ=0
    g37: LineSegment StartX=307.138 StartY=-136.575 StartZ=0 EndX=307.138 EndY=-122.375 EndZ=0
    g38: LineSegment StartX=307.138 StartY=-122.375 StartZ=0 EndX=292.938 EndY=-122.375 EndZ=0
    g39: GeomPoint X=300.038 Y=-129.475 Z=0
    g40: LineSegment StartX=311.988 StartY=-122.375 StartZ=0 EndX=311.988 EndY=-136.575 EndZ=0
    g41: LineSegment StartX=311.988 StartY=-136.575 StartZ=0 EndX=326.188 EndY=-136.575 EndZ=0
    g42: LineSegment StartX=326.188 StartY=-136.575 StartZ=0 EndX=326.188 EndY=-122.375 EndZ=0
    g43: LineSegment StartX=326.188 StartY=-122.375 StartZ=0 EndX=311.988 EndY=-122.375 EndZ=0
    g44: GeomPoint X=319.088 Y=-129.475 Z=0
    g45: LineSegment StartX=331.037 StartY=-122.375 StartZ=0 EndX=331.037 EndY=-136.575 EndZ=0
    g46: LineSegment StartX=331.037 StartY=-136.575 StartZ=0 EndX=345.237 EndY=-136.575 EndZ=0
    g47: LineSegment StartX=345.237 StartY=-136.575 StartZ=0 EndX=345.237 EndY=-122.375 EndZ=0
    g48: LineSegment StartX=345.237 StartY=-122.375 StartZ=0 EndX=331.037 EndY=-122.375 EndZ=0
    g49: GeomPoint X=338.137 Y=-129.475 Z=0
  constraints (130):
    c: Coincident(g0,g1)
    c: Coincident(g1,g2)
    c: Coincident(g2,g3)
    c: Coincident(g3,g0)
    c: Horizontal(g1)
    c: Horizontal(g3)
    c: Vertical(g0)
    c: Vertical(g2)
    c: Symmetric(g1,g0,g4)
    c: DistanceX(g3,g3) = 14.2
    c: DistanceY(g4,g-1) = 124.713
    c: DistanceX(g-1,g4) = 50.0063
    c: Coincident(g5,g6)
    c: Coincident(g6,g7)
    c: Coincident(g7,g8)
    c: Coincident(g8,g5)
    c: Horizontal(g6)
    c: Horizontal(g8)
    c: Vertical(g5)
    c: Vertical(g7)
    c: Symmetric(g6,g5,g9)
    c: Coincident(g10,g11)
    c: Coincident(g11,g12)
    c: Coincident(g12,g13)
    c: Coincident(g13,g10)
    c: Horizontal(g11)
    c: Horizontal(g13)
    c: Vertical(g10)
    c: Vertical(g12)
    c: Symmetric(g11,g10,g14)
    c: Coincident(g15,g16)
    c: Coincident(g16,g17)
    c: Coincident(g17,g18)
    c: Coincident(g18,g15)
    c: Horizontal(g16)
    c: Horizontal(g18)
    c: Vertical(g15)
    c: Vertical(g17)
    c: Symmetric(g16,g15,g19)
    c: Coincident(g20,g21)
    c: Coincident(g21,g22)
    c: Coincident(g22,g23)
    c: Coincident(g23,g20)
    c: Horizontal(g21)
    c: Horizontal(g23)
    c: Vertical(g20)
    c: Vertical(g22)
    c: Symmetric(g21,g20,g24)
    c: Coincident(g25,g26)
    c: Coincident(g26,g27)
    c: Coincident(g27,g28)
    c: Coincident(g28,g25)
    c: Horizontal(g26)
    c: Horizontal(g28)
    c: Vertical(g25)
    c: Vertical(g27)
    c: Symmetric(g26,g25,g29)
    c: Coincident(g30,g31)
    c: Coincident(g31,g32)
    c: Coincident(g32,g33)
    c: Coincident(g33,g30)
    c: Horizontal(g31)
    c: Horizontal(g33)
    c: Vertical(g30)
    c: Vertical(g32)
    c: Symmetric(g31,g30,g34)
    c: Coincident(g35,g36)
    c: Coincident(g36,g37)
    c: Coincident(g37,g38)
    c: Coincident(g38,g35)
    c: Horizontal(g36)
    c: Horizontal(g38)
    c: Vertical(g35)
    c: Vertical(g37)
    c: Symmetric(g36,g35,g39)
    c: Coincident(g40,g41)
    c: Coincident(g41,g42)
    c: Coincident(g42,g43)
    c: Coincident(g43,g40)
    c: Horizontal(g41)
    c: Horizontal(g43)
    c: Vertical(g40)
    c: Vertical(g42)
    c: Symmetric(g41,g40,g44)
    c: DistanceX(g4,g9) = 23.8125
    c: Horizontal(g4,g9)
    c: Horizontal(g9,g14)
    c: Horizontal(g14,g19)
    c: Horizontal(g24,g29)
    c: Horizontal(g29,g34)
    c: DistanceX(g9,g14) = 23.8125
    c: DistanceX(g14,g19) = 71.4375
    c: DistanceX(g24,g29) = 19.05
    c: DistanceX(g29,g34) = 19.05
    c: DistanceX(g34,g39) = 23.8125
    c: DistanceX(g39,g44) = 19.05
    c: DistanceY(g39,g34) = 4.7625
    c: DistanceX(g19,g24) = 69.0563
    c: Horizontal(g19,g24)
    c: Horizontal(g39,g44)
    c: Coincident(g45,g46)
    c: Coincident(g46,g47)
    c: Coincident(g47,g48)
    c: Coincident(g48,g45)
    c: Horizontal(g46)
    c: Horizontal(g48)
    c: Vertical(g45)
    c: Vertical(g47)
    c: Symmetric(g46,g45,g49)
    c: Horizontal(g44,g49)
    c: DistanceX(g44,g49) = 19.05
    c: Equal(g2,g3)
    c: Equal(g47,g48)
    c: Equal(g48,g42)
    c: Equal(g42,g43)
    c: Equal(g43,g37)
    c: Equal(g37,g38)
    c: Equal(g38,g32)
    c: Equal(g32,g33)
    c: Equal(g33,g27)
    c: Equal(g27,g28)
    c: Equal(g28,g22)
    c: Equal(g22,g23)
    c: Equal(g23,g17)
    c: Equal(g17,g18)
    c: Equal(g18,g12)
    c: Equal(g12,g13)
    c: Equal(g13,g7)
    c: Equal(g7,g8)
    c: Equal(g8,g2)
FEATURE [PartDesign::Pocket] Pocket050
  BaseFeature = -> Pocket049
  Direction = (0,0,-1)
  Length = 5
  Length2 = 5
  Profile = -> Sketch065
  ReferenceAxis = -> Sketch065 [N_Axis]
  Type = 0
FEATURE [Sketcher::SketchObject] Sketch066
  AttachmentOffset = pos=(0,0,4.1) rot=(0,0,1;0rad)
  FullyConstrained = true
  MapMode = 5
  Placement = pos=(0,0,4.1) rot=(0,0,1;0rad)
  Support = -> [XY_Plane209]
  expr: Constraints[11] = Spreadsheet.encoder_hole_width
  expr: Constraints[12] = Spreadsheet.encoder_hole_width
  expr: Constraints[13] = Spreadsheet.u
  expr: Constraints[14] = Spreadsheet.encoder_hole_length
  expr: Constraints[15] = Spreadsheet.encoder_hole_length
  expr: Constraints[16] = Spreadsheet.u * 0.5
  expr: Constraints[17] = Spreadsheet.PCB_width - Spreadsheet.u * 6
  expr: Constraints[22] = Spreadsheet.encoder_fillet_rad
  expr: Constraints[51] = Spreadsheet.encoder_fillet_rad
  expr: Constraints[52] = Spreadsheet.encoder_fillet_rad
  expr: Constraints[53] = Spreadsheet.encoder_fillet_rad
  expr: Constraints[54] = Spreadsheet.encoder_fillet_rad
  expr: Constraints[55] = Spreadsheet.encoder_fillet_rad
  expr: Constraints[56] = Spreadsheet.encoder_fillet_rad
  expr: Constraints[57] = Spreadsheet.encoder_fillet_rad
  sketch-geometry (26):
    g0: LineSegment StartX=22.075 StartY=-17.95 StartZ=0 EndX=22.075 EndY=-31.45 EndZ=0
    g1: LineSegment StartX=23.325 StartY=-32.7 StartZ=0 EndX=33.825 EndY=-32.7 EndZ=0
    g2: LineSegment StartX=35.075 StartY=-31.45 StartZ=0 EndX=35.075 EndY=-17.95 EndZ=0
    g3: LineSegment StartX=33.825 StartY=-16.7 StartZ=0 EndX=23.325 EndY=-16.7 EndZ=0
    g4: GeomPoint X=28.575 Y=-24.7 Z=0
    g5: LineSegment StartX=3.025 StartY=-17.95 StartZ=0 EndX=3.025 EndY=-31.45 EndZ=0
    g6: LineSegment StartX=4.275 StartY=-32.7 StartZ=0 EndX=14.775 EndY=-32.7 EndZ=0
    g7: LineSegment StartX=16.025 StartY=-31.45 StartZ=0 EndX=16.025 EndY=-17.95 EndZ=0
    g8: LineSegment StartX=14.775 StartY=-16.7 StartZ=0 EndX=4.275 EndY=-16.7 EndZ=0
    g9: GeomPoint X=9.525 Y=-24.7 Z=0
    g10: ArcOfCircle CenterX=14.775 CenterY=-31.45 CenterZ=0 NormalX=0 NormalY=0 NormalZ=1 AngleXU=0 Radius=1.25 StartAngle=4.71239 EndAngle=6.28319
    g11: GeomPoint X=16.025 Y=-32.7 Z=0
    g12: ArcOfCircle CenterX=14.775 CenterY=-17.95 CenterZ=0 NormalX=0 NormalY=0 NormalZ=1 AngleXU=0 Radius=1.25 StartAngle=0 EndAngle=1.5708
    g13: GeomPoint X=16.025 Y=-16.7 Z=0
    g14: ArcOfCircle CenterX=4.275 CenterY=-17.95 CenterZ=0 NormalX=0 NormalY=0 NormalZ=1 AngleXU=0 Radius=1.25 StartAngle=1.5708 EndAngle=3.14159
    g15: GeomPoint X=3.025 Y=-16.7 Z=0
    g16: ArcOfCircle CenterX=4.275 CenterY=-31.45 CenterZ=0 NormalX=0 NormalY=0 NormalZ=1 AngleXU=0 Radius=1.25 StartAngle=3.14159 EndAngle=4.71239
    g17: GeomPoint X=3.025 Y=-32.7 Z=0
    g18: ArcOfCircle CenterX=23.325 CenterY=-31.45 CenterZ=0 NormalX=0 NormalY=0 NormalZ=1 AngleXU=0 Radius=1.25 StartAngle=3.14159 EndAngle=4.71239
    g19: GeomPoint X=22.075 Y=-32.7 Z=0
    g20: ArcOfCircle CenterX=33.825 CenterY=-31.45 CenterZ=0 NormalX=0 NormalY=0 NormalZ=1 AngleXU=0 Radius=1.25 StartAngle=4.71239 EndAngle=6.28319
    g21: GeomPoint X=35.075 Y=-32.7 Z=0
    g22: ArcOfCircle CenterX=33.825 CenterY=-17.95 CenterZ=0 NormalX=0 NormalY=0 NormalZ=1 AngleXU=0 Radius=1.25 StartAngle=1.2e-15 EndAngle=1.5708
    g23: GeomPoint X=35.075 Y=-16.7 Z=0
    g24: ArcOfCircle CenterX=23.325 CenterY=-17.95 CenterZ=0 NormalX=0 NormalY=0 NormalZ=1 AngleXU=0 Radius=1.25 StartAngle=1.5708 EndAngle=3.14159
    g25: GeomPoint X=22.075 Y=-16.7 Z=0
  constraints (58):
    c: Horizontal(g1)
    c: Horizontal(g3)
    c: Vertical(g0)
    c: Vertical(g2)
    c: Symmetric(g21,g25,g4)
    c: Horizontal(g6)
    c: Horizontal(g8)
    c: Vertical(g5)
    c: Vertical(g7)
    c: Symmetric(g11,g15,g9)
    c: Horizontal(g9,g4)
    c: DistanceX(g15,g13) = 13
    c: DistanceX(g25,g23) = 13
    c: DistanceX(g9,g4) = 19.05
    c: DistanceY(g11,g13) = 16
    c: DistanceY(g21,g23) = 16
    c: DistanceX(g-1,g9) = 9.525
    c: DistanceY(g9,g-1) = 24.7
    c: PointOnObject(g11,g6)
    c: PointOnObject(g11,g7)
    c: Tangent(g6,g10) = -1.5708
    c: Tangent(g7,g10) = -1.5708
    c: Radius(g10) = 1.25
    c: PointOnObject(g13,g7)
    c: PointOnObject(g13,g8)
    c: Tangent(g7,g12) = -1.5708
    c: Tangent(g8,g12) = -1.5708
    c: PointOnObject(g15,g5)
    c: PointOnObject(g15,g8)
    c: Tangent(g5,g14) = -1.5708
    c: Tangent(g8,g14) = -1.5708
    c: PointOnObject(g17,g5)
    c: PointOnObject(g17,g6)
    c: Tangent(g5,g16) = -1.5708
    c: Tangent(g6,g16) = -1.5708
    c: PointOnObject(g19,g0)
    c: PointOnObject(g19,g1)
    c: Tangent(g0,g18) = -1.5708
    c: Tangent(g1,g18) = -1.5708
    c: PointOnObject(g21,g1)
    c: PointOnObject(g21,g2)
    c: Tangent(g1,g20) = -1.5708
    c: Tangent(g2,g20) = -1.5708
    c: PointOnObject(g23,g2)
    c: PointOnObject(g23,g3)
    c: Tangent(g2,g22) = -1.5708
    c: Tangent(g3,g22) = -1.5708
    c: PointOnObject(g25,g0)
    c: PointOnObject(g25,g3)
    c: Tangent(g0,g24) = -1.5708
    c: Tangent(g3,g24) = -1.5708
    c: Radius(g12) = 1.25
    c: Radius(g14) = 1.25
    c: Radius(g16) = 1.25
    c: Radius(g18) = 1.25
    c: Radius(g20) = 1.25
    c: Radius(g22) = 1.25
    c: Radius(g24) = 1.25
FEATURE [PartDesign::Pocket] Pocket051
  BaseFeature = -> Pocket050
  Direction = (0,0,-1)
  Length = 5
  Length2 = 5
  Profile = -> Sketch066
  ReferenceAxis = -> Sketch066 [N_Axis]
  Type = 0
FEATURE [Sketcher::SketchObject] Sketch067
  AttachmentOffset = pos=(0,0,4.1) rot=(0,0,1;0rad)
  FullyConstrained = true
  MapMode = 5
  Placement = pos=(0,0,4.1) rot=(0,0,1;0rad)
  Support = -> [XY_Plane209]
  expr: Constraints[5] = Spreadsheet.screen_module_width + 1
  expr: Constraints[6] = Spreadsheet.screen_module_length + 1
  expr: Constraints[7] = Spreadsheet.PCB_width - Spreadsheet.u * 3.75
  expr: Constraints[8] = Spreadsheet.u * 1
  sketch-geometry (13):
    g0: LineSegment StartX=4.9 StartY=-42.9625 StartZ=0 EndX=4.9 EndY=-92.1625 EndZ=0
    g1: LineSegment StartX=6.4 StartY=-93.6625 StartZ=0 EndX=31.7 EndY=-93.6625 EndZ=0
    g2: LineSegment StartX=33.2 StartY=-92.1625 StartZ=0 EndX=33.2 EndY=-42.9625 EndZ=0
    g3: LineSegment StartX=31.7 StartY=-41.4625 StartZ=0 EndX=6.4 EndY=-41.4625 EndZ=0
    g4: GeomPoint X=19.05 Y=-67.5625 Z=0
    g5: ArcOfCircle CenterX=31.7 CenterY=-42.9625 CenterZ=0 NormalX=0 NormalY=0 NormalZ=1 AngleXU=0 Radius=1.5 StartAngle=8e-16 EndAngle=1.5708
    g6: GeomPoint X=33.2 Y=-41.4625 Z=0
    g7: ArcOfCircle CenterX=6.4 CenterY=-42.9625 CenterZ=0 NormalX=0 NormalY=0 NormalZ=1 AngleXU=0 Radius=1.5 StartAngle=1.5708 EndAngle=3.14159
    g8: GeomPoint X=4.9 Y=-41.4625 Z=0
    g9: ArcOfCircle CenterX=6.4 CenterY=-92.1625 CenterZ=0 NormalX=0 NormalY=0 NormalZ=1 AngleXU=0 Radius=1.5 StartAngle=3.14159 EndAngle=4.71239
    g10: GeomPoint X=4.9 Y=-93.6625 Z=0
    g11: ArcOfCircle CenterX=31.7 CenterY=-92.1625 CenterZ=0 NormalX=0 NormalY=0 NormalZ=1 AngleXU=0 Radius=1.5 StartAngle=4.71239 EndAngle=6.28319
    g12: GeomPoint X=33.2 Y=-93.6625 Z=0
  constraints (29):
    c: Horizontal(g1)
    c: Horizontal(g3)
    c: Vertical(g0)
    c: Vertical(g2)
    c: Symmetric(g12,g8,g4)
    c: DistanceX(g8,g6) = 28.3
    c: DistanceY(g12,g6) = 52.2
    c: DistanceY(g4,g-1) = 67.5625
    c: DistanceX(g-1,g4) = 19.05
    c: PointOnObject(g6,g2)
    c: PointOnObject(g6,g3)
    c: Tangent(g2,g5) = -1.5708
    c: Tangent(g3,g5) = -1.5708
    c: Radius(g5) = 1.5
    c: PointOnObject(g8,g0)
    c: PointOnObject(g8,g3)
    c: Tangent(g0,g7) = -1.5708
    c: Tangent(g3,g7) = -1.5708
    c: PointOnObject(g10,g0)
    c: PointOnObject(g10,g1)
    c: Tangent(g0,g9) = -1.5708
    c: Tangent(g1,g9) = -1.5708
    c: PointOnObject(g12,g1)
    c: PointOnObject(g12,g2)
    c: Tangent(g1,g11) = -1.5708
    c: Tangent(g2,g11) = -1.5708
    c: Radius(g11) = 1.5
    c: Radius(g9) = 1.5
    c: Radius(g7) = 1.5
FEATURE [PartDesign::Pocket] Pocket052
  BaseFeature = -> Pocket051
  Direction = (0,0,-1)
  Length = 5
  Length2 = 5
  Profile = -> Sketch067
  ReferenceAxis = -> Sketch067 [N_Axis]
  Type = 0
FEATURE [Sketcher::SketchObject] Sketch068
  AttachmentOffset = pos=(0,0,4.1) rot=(0,0,1;0rad)
  FullyConstrained = true
  MapMode = 5
  Placement = pos=(0,0,4.1) rot=(0,0,1;0rad)
  Support = -> [XY_Plane209]
  expr: Constraints[47] = Spreadsheet.tact_button_size + 1.5
  expr: Constraints[48] = Spreadsheet.PCB_width - Spreadsheet.u * 1.75
  expr: Constraints[49] = Spreadsheet.u
  expr: Constraints[50] = Spreadsheet.u
  expr: Constraints[51] = Spreadsheet.u * 0.5
  sketch-geometry (20):
    g0: LineSegment StartX=5.775 StartY=-120.963 StartZ=0 EndX=5.775 EndY=-128.462 EndZ=0
    g1: LineSegment StartX=5.775 StartY=-128.462 StartZ=0 EndX=13.275 EndY=-128.462 EndZ=0
    g2: LineSegment StartX=13.275 StartY=-128.462 StartZ=0 EndX=13.275 EndY=-120.963 EndZ=0
    g3: LineSegment StartX=13.275 StartY=-120.963 StartZ=0 EndX=5.775 EndY=-120.963 EndZ=0
    g4: GeomPoint X=9.525 Y=-124.712 Z=0
    g5: LineSegment StartX=24.825 StartY=-120.963 StartZ=0 EndX=24.825 EndY=-128.462 EndZ=0
    g6: LineSegment StartX=24.825 StartY=-128.462 StartZ=0 EndX=32.325 EndY=-128.462 EndZ=0
    g7: LineSegment StartX=32.325 StartY=-128.462 StartZ=0 EndX=32.325 EndY=-120.963 EndZ=0
    g8: LineSegment StartX=32.325 StartY=-120.963 StartZ=0 EndX=24.825 EndY=-120.963 EndZ=0
    g9: GeomPoint X=28.575 Y=-124.712 Z=0
    g10: LineSegment StartX=24.825 StartY=-101.913 StartZ=0 EndX=24.825 EndY=-109.412 EndZ=0
    g11: LineSegment StartX=24.825 StartY=-109.412 StartZ=0 EndX=32.325 EndY=-109.412 EndZ=0
    g12: LineSegment StartX=32.325 StartY=-109.412 StartZ=0 EndX=32.325 EndY=-101.913 EndZ=0
    g13: LineSegment StartX=32.325 StartY=-101.913 StartZ=0 EndX=24.825 EndY=-101.913 EndZ=0
    g14: GeomPoint X=28.575 Y=-105.662 Z=0
    g15: LineSegment StartX=5.775 StartY=-101.913 StartZ=0 EndX=5.775 EndY=-109.413 EndZ=0
    g16: LineSegment StartX=5.775 StartY=-109.413 StartZ=0 EndX=13.275 EndY=-109.413 EndZ=0
    g17: LineSegment StartX=13.275 StartY=-109.413 StartZ=0 EndX=13.275 EndY=-101.913 EndZ=0
    g18: LineSegment StartX=13.275 StartY=-101.913 StartZ=0 EndX=5.775 EndY=-101.913 EndZ=0
    g19: GeomPoint X=9.525 Y=-105.662 Z=0
  constraints (52):
    c: Coincident(g0,g1)
    c: Coincident(g1,g2)
    c: Coincident(g2,g3)
    c: Coincident(g3,g0)
    c: Horizontal(g1)
    c: Horizontal(g3)
    c: Vertical(g0)
    c: Vertical(g2)
    c: Symmetric(g1,g0,g4)
    c: Coincident(g5,g6)
    c: Coincident(g6,g7)
    c: Coincident(g7,g8)
    c: Coincident(g8,g5)
    c: Horizontal(g6)
    c: Horizontal(g8)
    c: Vertical(g5)
    c: Vertical(g7)
    c: Symmetric(g6,g5,g9)
    c: Coincident(g10,g11)
    c: Coincident(g11,g12)
    c: Coincident(g12,g13)
    c: Coincident(g13,g10)
    c: Horizontal(g11)
    c: Horizontal(g13)
    c: Vertical(g10)
    c: Vertical(g12)
    c: Symmetric(g11,g10,g14)
    c: Coincident(g15,g16)
    c: Coincident(g16,g17)
    c: Coincident(g17,g18)
    c: Coincident(g18,g15)
    c: Horizontal(g16)
    c: Horizontal(g18)
    c: Vertical(g15)
    c: Vertical(g17)
    c: Symmetric(g16,g15,g19)
    c: Equal(g17,g18)
    c: Equal(g12,g13)
    c: Equal(g7,g8)
    c: Equal(g2,g3)
    c: Equal(g3,g18)
    c: Equal(g8,g13)
    c: Equal(g13,g18)
    c: Horizontal(g19,g14)
    c: Horizontal(g4,g9)
    c: Vertical(g19,g4)
    c: Vertical(g9,g14)
    c: DistanceX(g18,g18) = 7.5
    c: DistanceY(g19,g-1) = 105.662
    c: DistanceY(g4,g19) = 19.05
    c: DistanceX(g19,g14) = 19.05
    c: DistanceX(g-1,g19) = 9.525
FEATURE [PartDesign::Pocket] Pocket053
  BaseFeature = -> Pocket052
  Direction = (0,0,-1)
  Length = 5
  Length2 = 5
  Profile = -> Sketch068
  ReferenceAxis = -> Sketch068 [N_Axis]
  Type = 0
FEATURE [Sketcher::SketchObject] Sketch069
  AttachmentOffset = pos=(0,0,4.1) rot=(0,0,1;0rad)
  FullyConstrained = true
  MapMode = 5
  Placement = pos=(0,0,4.1) rot=(0,0,1;0rad)
  Support = -> [XY_Plane209]
  expr: Constraints[0] = Spreadsheet.u * (2 + 3 * 1.25 + 6.25 / 2)
  expr: Constraints[1] = Spreadsheet.PCB_width - Spreadsheet.u * 0.75
  expr: Constraints[26] = Spreadsheet.stab_length + 0.2
  expr: Constraints[37] = Spreadsheet.stab_width + 0.2
  expr: Constraints[45] = (Spreadsheet.stab_width + 0.2) / 2 - 2
  expr: Constraints[59] = (Spreadsheet.stab_width + 0.2) / 2 - 2
  sketch-geometry (24):
    g0: GeomPoint X=169.069 Y=-124.713 Z=0
    g1: LineSegment StartX=116.019 StartY=-117.793 StartZ=0 EndX=116.019 EndY=-130.393 EndZ=0
    g2: LineSegment StartX=116.019 StartY=-130.393 StartZ=0 EndX=122.119 EndY=-130.393 EndZ=0
    g3: LineSegment StartX=122.119 StartY=-130.393 StartZ=0 EndX=122.119 EndY=-127.003 EndZ=0
    g4: LineSegment StartX=122.119 StartY=-117.793 StartZ=0 EndX=121.069 EndY=-117.793 EndZ=0
    g5: GeomPoint X=119.069 Y=-124.093 Z=0
    g6: LineSegment StartX=216.019 StartY=-117.793 StartZ=0 EndX=216.019 EndY=-123.803 EndZ=0
    g7: LineSegment StartX=216.019 StartY=-130.393 StartZ=0 EndX=222.119 EndY=-130.393 EndZ=0
    g8: LineSegment StartX=222.119 StartY=-130.393 StartZ=0 EndX=222.119 EndY=-117.793 EndZ=0
    g9: LineSegment StartX=222.119 StartY=-117.793 StartZ=0 EndX=221.069 EndY=-117.793 EndZ=0
    g10: GeomPoint X=219.069 Y=-124.093 Z=0
    g11: LineSegment StartX=122.119 StartY=-123.803 StartZ=0 EndX=216.019 EndY=-123.803 EndZ=0
    g12: LineSegment StartX=216.019 StartY=-127.003 StartZ=0 EndX=122.119 EndY=-127.003 EndZ=0
    g13: LineSegment StartX=122.119 StartY=-123.803 StartZ=0 EndX=122.119 EndY=-117.793 EndZ=0
    g14: LineSegment StartX=216.019 StartY=-127.003 StartZ=0 EndX=216.019 EndY=-130.393 EndZ=0
    g15: GeomPoint X=169.069 Y=-124.093 Z=0
    g16: LineSegment StartX=121.069 StartY=-117.793 StartZ=0 EndX=121.069 EndY=-115.793 EndZ=0
    g17: LineSegment StartX=121.069 StartY=-115.793 StartZ=0 EndX=117.069 EndY=-115.793 EndZ=0
    g18: LineSegment StartX=117.069 StartY=-115.793 StartZ=0 EndX=117.069 EndY=-117.793 EndZ=0
    g19: LineSegment StartX=117.069 StartY=-117.793 StartZ=0 EndX=116.019 EndY=-117.793 EndZ=0
    g20: LineSegment StartX=217.069 StartY=-117.793 StartZ=0 EndX=217.069 EndY=-115.793 EndZ=0
    g21: LineSegment StartX=217.069 StartY=-115.793 StartZ=0 EndX=221.069 EndY=-115.793 EndZ=0
    g22: LineSegment StartX=221.069 StartY=-115.793 StartZ=0 EndX=221.069 EndY=-117.793 EndZ=0
    g23: LineSegment StartX=217.069 StartY=-117.793 StartZ=0 EndX=216.019 EndY=-117.793 EndZ=0
  constraints (65):
    c: DistanceX(g-1,g0) = 169.069
    c: DistanceY(g0,g-1) = 124.713
    c: Coincident(g1,g2)
    c: Coincident(g2,g3)
    c: Coincident(g13,g4)
    c: Coincident(g19,g1)
    c: Horizontal(g2)
    c: Horizontal(g4)
    c: Vertical(g1)
    c: Vertical(g3)
    c: Symmetric(g2,g1,g5)
    c: Coincident(g14,g7)
    c: Coincident(g7,g8)
    c: Coincident(g8,g9)
    c: Coincident(g23,g6)
    c: Horizontal(g7)
    c: Horizontal(g9)
    c: Vertical(g6)
    c: Vertical(g8)
    c: Symmetric(g7,g6,g10)
    c: Horizontal(g5,g10)
    c: DistanceX(g5,g10) = 100
    c: Horizontal(g11)
    c: Horizontal(g12)
    c: DistanceY(g12,g11) = 3.2
    c: DistanceY(g2,g12) = 3.39
    c: DistanceY(g1,g1) = 12.6
    c: Coincident(g3,g12)
    c: Coincident(g13,g11)
    c: Coincident(g6,g11)
    c: Coincident(g14,g12)
    c: Vertical(g13)
    c: Vertical(g14)
    c: Equal(g8,g1)
    c: Vertical(g0,g15)
    c: DistanceY(g0,g15) = 0.62
    c: Symmetric(g10,g5,g15)
    c: DistanceX(g2,g2) = 6.1
    c: Vertical(g16)
    c: Coincident(g17,g16)
    c: Horizontal(g17)
    c: Coincident(g18,g17)
    c: Vertical(g18)
    c: DistanceY(g18,g18) = 2
    c: DistanceX(g17,g17) = 4
    c: DistanceX(g16,g4) = 1.05
    c: Coincident(g4,g16)
    c: Coincident(g19,g18)
    c: Horizontal(g19)
    c: Vertical(g11,g3)
    c: Horizontal(g18,g4)
    c: Vertical(g20)
    c: Coincident(g21,g20)
    c: Horizontal(g21)
    c: Coincident(g22,g21)
    c: Vertical(g22)
    c: DistanceY(g20,g20) = 2
    c: DistanceX(g21,g21) = 4
    c: Equal(g7,g2)
    c: DistanceX(g6,g20) = 1.05
    c: Coincident(g9,g22)
    c: Coincident(g23,g20)
    c: Vertical(g6,g12)
    c: Horizontal(g20,g9)
    c: Horizontal(g23)
FEATURE [PartDesign::Pocket] Pocket054
  BaseFeature = -> Pocket053
  Direction = (0,0,-1)
  Length = 5
  Length2 = 5
  Profile = -> Sketch069
  ReferenceAxis = -> Sketch069 [N_Axis]
  Type = 0
FEATURE [Sketcher::SketchObject] Sketch070
  AttachmentOffset = pos=(0,0,4.1) rot=(0,0,1;0rad)
  FullyConstrained = true
  MapMode = 5
  Placement = pos=(0,0,4.1) rot=(0,0,1;0rad)
  Support = -> [XY_Plane209]
  expr: Constraints[0] = Spreadsheet.u * (2 + 2.25 / 2)
  expr: Constraints[1] = Spreadsheet.PCB_width - Spreadsheet.u * 1.75
  expr: Constraints[30] = Spreadsheet.stab_length + 0.2
  expr: Constraints[51] = Spreadsheet.stab_width + 0.2
  expr: Constraints[53] = (Spreadsheet.stab_width + 0.2) / 2 - 2
  expr: Constraints[58] = (Spreadsheet.stab_width + 0.2) / 2 - 2
  sketch-geometry (24):
    g0: GeomPoint X=59.5312 Y=-105.662 Z=0
    g1: LineSegment StartX=44.4813 StartY=-98.7425 StartZ=0 EndX=44.4813 EndY=-111.342 EndZ=0
    g2: LineSegment StartX=44.4813 StartY=-111.342 StartZ=0 EndX=50.5813 EndY=-111.342 EndZ=0
    g3: LineSegment StartX=50.5813 StartY=-111.342 StartZ=0 EndX=50.5813 EndY=-107.952 EndZ=0
    g4: LineSegment StartX=50.5813 StartY=-98.7425 StartZ=0 EndX=49.5313 EndY=-98.7425 EndZ=0
    g5: GeomPoint X=47.5312 Y=-105.042 Z=0
    g6: LineSegment StartX=68.4813 StartY=-98.7425 StartZ=0 EndX=68.4813 EndY=-104.752 EndZ=0
    g7: LineSegment StartX=68.4813 StartY=-111.342 StartZ=0 EndX=74.5813 EndY=-111.342 EndZ=0
    g8: LineSegment StartX=74.5813 StartY=-111.342 StartZ=0 EndX=74.5813 EndY=-98.7425 EndZ=0
    g9: LineSegment StartX=74.5813 StartY=-98.7425 StartZ=0 EndX=73.5313 EndY=-98.7425 EndZ=0
    g10: GeomPoint X=71.5312 Y=-105.042 Z=0
    g11: LineSegment StartX=50.5813 StartY=-104.752 StartZ=0 EndX=68.4813 EndY=-104.752 EndZ=0
    g12: LineSegment StartX=68.4813 StartY=-107.952 StartZ=0 EndX=50.5813 EndY=-107.952 EndZ=0
    g13: LineSegment StartX=50.5813 StartY=-104.752 StartZ=0 EndX=50.5813 EndY=-98.7425 EndZ=0
    g14: LineSegment StartX=68.4813 StartY=-107.952 StartZ=0 EndX=68.4813 EndY=-111.342 EndZ=0
    g15: GeomPoint X=59.5312 Y=-105.042 Z=0
    g16: LineSegment StartX=45.5313 StartY=-98.7425 StartZ=0 EndX=45.5313 EndY=-96.7425 EndZ=0
    g17: LineSegment StartX=45.5313 StartY=-96.7425 StartZ=0 EndX=49.5313 EndY=-96.7425 EndZ=0
    g18: LineSegment StartX=49.5313 StartY=-96.7425 StartZ=0 EndX=49.5313 EndY=-98.7425 EndZ=0
    g19: LineSegment StartX=69.5313 StartY=-98.7425 StartZ=0 EndX=69.5313 EndY=-96.7425 EndZ=0
    g20: LineSegment StartX=69.5313 StartY=-96.7425 StartZ=0 EndX=73.5313 EndY=-96.7425 EndZ=0
    g21: LineSegment StartX=73.5313 StartY=-96.7425 StartZ=0 EndX=73.5313 EndY=-98.7425 EndZ=0
    g22: LineSegment StartX=45.5313 StartY=-98.7425 StartZ=0 EndX=44.4813 EndY=-98.7425 EndZ=0
    g23: LineSegment StartX=69.5313 StartY=-98.7425 StartZ=0 EndX=68.4813 EndY=-98.7425 EndZ=0
  constraints (65):
    c: DistanceX(g-1,g0) = 59.5312
    c: DistanceY(g0,g-1) = 105.662
    c: Coincident(g1,g2)
    c: Coincident(g2,g3)
    c: Coincident(g13,g4)
    c: Coincident(g22,g1)
    c: Horizontal(g2)
    c: Horizontal(g4)
    c: Vertical(g1)
    c: Vertical(g3)
    c: Symmetric(g2,g1,g5)
    c: Coincident(g14,g7)
    c: Coincident(g7,g8)
    c: Coincident(g8,g9)
    c: Coincident(g23,g6)
    c: Horizontal(g7)
    c: Horizontal(g9)
    c: Vertical(g6)
    c: Vertical(g8)
    c: Symmetric(g7,g6,g10)
    c: Horizontal(g5,g10)
    c: DistanceX(g5,g10) = 24
    c: Horizontal(g11)
    c: Horizontal(g12)
    c: DistanceY(g12,g11) = 3.2
    c: DistanceY(g2,g12) = 3.39
    c: Coincident(g3,g12)
    c: Coincident(g13,g11)
    c: Coincident(g6,g11)
    c: Coincident(g14,g12)
    c: DistanceY(g1,g1) = 12.6
    c: Equal(g8,g1)
    c: Vertical(g14)
    c: Vertical(g13)
    c: Vertical(g0,g15)
    c: DistanceY(g0,g15) = 0.62
    c: Symmetric(g5,g10,g15)
    c: Vertical(g16)
    c: Coincident(g17,g16)
    c: Horizontal(g17)
    c: Coincident(g18,g17)
    c: Vertical(g18)
    c: Vertical(g19)
    c: Coincident(g20,g19)
    c: Horizontal(g20)
    c: Coincident(g21,g20)
    c: Vertical(g21)
    c: DistanceX(g20,g20) = 4
    c: DistanceX(g17,g17) = 4
    c: DistanceY(g16,g16) = 2
    c: DistanceY(g19,g19) = 2
    c: DistanceX(g2,g2) = 6.1
    c: Vertical(g11,g3)
    c: DistanceX(g18,g4) = 1.05
    c: Coincident(g4,g18)
    c: Coincident(g22,g16)
    c: Horizontal(g22)
    c: Horizontal(g4,g16)
    c: DistanceX(g6,g19) = 1.05
    c: Coincident(g9,g21)
    c: Coincident(g23,g19)
    c: Vertical(g6,g12)
    c: Horizontal(g19,g9)
    c: Horizontal(g23)
    c: Equal(g7,g2)
FEATURE [PartDesign::Pocket] Pocket055
  BaseFeature = -> Pocket054
  Direction = (0,0,-1)
  Length = 5
  Length2 = 5
  Profile = -> Sketch070
  ReferenceAxis = -> Sketch070 [N_Axis]
  Type = 0
FEATURE [Sketcher::SketchObject] Sketch071
  AttachmentOffset = pos=(0,0,4.1) rot=(0,0,1;0rad)
  FullyConstrained = true
  MapMode = 5
  Placement = pos=(0,0,4.1) rot=(0,0,1;0rad)
  Support = -> [XY_Plane209]
  expr: Constraints[0] = Spreadsheet.u * (2 + 1.75 + 11 + 2.25 / 2)
  expr: Constraints[16] = Spreadsheet.stab_length + 0.2
  expr: Constraints[1] = Spreadsheet.PCB_width - Spreadsheet.u * 2.75
  expr: Constraints[46] = Spreadsheet.stab_width + 0.2
  expr: Constraints[47] = (Spreadsheet.stab_width + 0.2) / 2 - 2
  expr: Constraints[48] = (Spreadsheet.stab_width + 0.2) / 2 - 2
  sketch-geometry (24):
    g0: GeomPoint X=302.419 Y=-86.6125 Z=0
    g1: LineSegment StartX=287.369 StartY=-79.6925 StartZ=0 EndX=287.369 EndY=-92.2925 EndZ=0
    g2: LineSegment StartX=287.369 StartY=-92.2925 StartZ=0 EndX=293.469 EndY=-92.2925 EndZ=0
    g3: LineSegment StartX=293.469 StartY=-79.6925 StartZ=0 EndX=292.419 EndY=-79.6925 EndZ=0
    g4: GeomPoint X=290.419 Y=-85.9925 Z=0
    g5: LineSegment StartX=311.369 StartY=-92.2925 StartZ=0 EndX=317.469 EndY=-92.2925 EndZ=0
    g6: LineSegment StartX=317.469 StartY=-92.2925 StartZ=0 EndX=317.469 EndY=-79.6925 EndZ=0
    g7: LineSegment StartX=317.469 StartY=-79.6925 StartZ=0 EndX=316.419 EndY=-79.6925 EndZ=0
    g8: GeomPoint X=314.419 Y=-85.9925 Z=0
    g9: LineSegment StartX=293.469 StartY=-79.6925 StartZ=0 EndX=293.469 EndY=-85.7025 EndZ=0
    g10: LineSegment StartX=293.469 StartY=-85.7025 StartZ=0 EndX=311.369 EndY=-85.7025 EndZ=0
    g11: LineSegment StartX=311.369 StartY=-85.7025 StartZ=0 EndX=311.369 EndY=-79.6925 EndZ=0
    g12: LineSegment StartX=311.369 StartY=-92.2925 StartZ=0 EndX=311.369 EndY=-88.9025 EndZ=0
    g13: LineSegment StartX=311.369 StartY=-88.9025 StartZ=0 EndX=293.469 EndY=-88.9025 EndZ=0
    g14: LineSegment StartX=293.469 StartY=-88.9025 StartZ=0 EndX=293.469 EndY=-92.2925 EndZ=0
    g15: GeomPoint X=302.419 Y=-85.9925 Z=0
    g16: LineSegment StartX=288.419 StartY=-79.6925 StartZ=0 EndX=288.419 EndY=-77.6925 EndZ=0
    g17: LineSegment StartX=288.419 StartY=-77.6925 StartZ=0 EndX=292.419 EndY=-77.6925 EndZ=0
    g18: LineSegment StartX=292.419 StartY=-77.6925 StartZ=0 EndX=292.419 EndY=-79.6925 EndZ=0
    g19: LineSegment StartX=312.419 StartY=-79.6925 StartZ=0 EndX=312.419 EndY=-77.6925 EndZ=0
    g20: LineSegment StartX=312.419 StartY=-77.6925 StartZ=0 EndX=316.419 EndY=-77.6925 EndZ=0
    g21: LineSegment StartX=316.419 StartY=-77.6925 StartZ=0 EndX=316.419 EndY=-79.6925 EndZ=0
    g22: LineSegment StartX=312.419 StartY=-79.6925 StartZ=0 EndX=311.369 EndY=-79.6925 EndZ=0
    g23: LineSegment StartX=288.419 StartY=-79.6925 StartZ=0 EndX=287.369 EndY=-79.6925 EndZ=0
  constraints (65):
    c: DistanceX(g-1,g0) = 302.419
    c: DistanceY(g0,g-1) = 86.6125
    c: Coincident(g1,g2)
    c: Coincident(g23,g1)
    c: Horizontal(g2)
    c: Horizontal(g3)
    c: Vertical(g1)
    c: Symmetric(g2,g1,g4)
    c: Coincident(g5,g6)
    c: Coincident(g6,g7)
    c: Horizontal(g5)
    c: Horizontal(g7)
    c: Vertical(g6)
    c: Symmetric(g5,g22,g8)
    c: Horizontal(g4,g8)
    c: DistanceX(g4,g8) = 24
    c: DistanceY(g1,g1) = 12.6
    c: Equal(g1,g6)
    c: Coincident(g9,g3)
    c: Vertical(g9)
    c: Coincident(g10,g9)
    c: Horizontal(g10)
    c: Coincident(g11,g10)
    c: Coincident(g11,g22)
    c: Vertical(g11)
    c: Coincident(g12,g5)
    c: Vertical(g12)
    c: Horizontal(g13)
    c: Coincident(g14,g13)
    c: Coincident(g14,g2)
    c: Vertical(g14)
    c: DistanceY(g13,g9) = 3.2
    c: DistanceY(g14,g14) = 3.39
    c: Coincident(g12,g13)
    c: Vertical(g15,g0)
    c: DistanceY(g0,g15) = 0.62
    c: Symmetric(g4,g8,g15)
    c: Vertical(g16)
    c: Coincident(g17,g16)
    c: Horizontal(g17)
    c: Coincident(g18,g17)
    c: Vertical(g18)
    c: Vertical(g19)
    c: Coincident(g20,g19)
    c: Horizontal(g20)
    c: Vertical(g21)
    c: DistanceX(g2,g2) = 6.1
    c: DistanceX(g18,g3) = 1.05
    c: DistanceX(g22,g19) = 1.05
    c: DistanceX(g17,g17) = 4
    c: DistanceX(g20,g20) = 4
    c: Coincident(g20,g21)
    c: DistanceY(g18,g18) = 2
    c: DistanceY(g19,g19) = 2
    c: Coincident(g7,g21)
    c: Coincident(g22,g19)
    c: Coincident(g3,g18)
    c: Coincident(g23,g16)
    c: Equal(g5,g2)
    c: Vertical(g13,g9)
    c: Vertical(g10,g12)
    c: Horizontal(g23)
    c: Horizontal(g3,g16)
    c: Horizontal(g22)
    c: Horizontal(g19,g7)
FEATURE [PartDesign::Pocket] Pocket056
  BaseFeature = -> Pocket055
  Direction = (0,0,-1)
  Length = 5
  Length2 = 5
  Profile = -> Sketch071
  ReferenceAxis = -> Sketch071 [N_Axis]
  Type = 0
FEATURE [Sketcher::SketchObject] Sketch072
  AttachmentOffset = pos=(0,0,4.1) rot=(0,0,1;0rad)
  FullyConstrained = true
  MapMode = 5
  Placement = pos=(0,0,4.1) rot=(0,0,1;0rad)
  Support = -> [XY_Plane209]
  expr: Constraints[0] = Spreadsheet.u * (2 + +13 + 2 / 2)
  expr: Constraints[15] = Spreadsheet.stab_length + 0.2
  expr: Constraints[1] = Spreadsheet.PCB_width - Spreadsheet.u * 4.75
  expr: Constraints[37] = Spreadsheet.stab_width + 0.2
  expr: Constraints[48] = (Spreadsheet.stab_width + 0.2) / 2 - 2
  expr: Constraints[49] = (Spreadsheet.stab_width + 0.2) / 2 - 2
  sketch-geometry (24):
    g0: GeomPoint X=304.8 Y=-48.5125 Z=0
    g1: LineSegment StartX=289.75 StartY=-41.5925 StartZ=0 EndX=289.75 EndY=-54.1925 EndZ=0
    g2: LineSegment StartX=289.75 StartY=-54.1925 StartZ=0 EndX=295.85 EndY=-54.1925 EndZ=0
    g3: LineSegment StartX=295.85 StartY=-41.5925 StartZ=0 EndX=294.8 EndY=-41.5925 EndZ=0
    g4: GeomPoint X=292.8 Y=-47.8925 Z=0
    g5: LineSegment StartX=313.75 StartY=-54.1925 StartZ=0 EndX=319.85 EndY=-54.1925 EndZ=0
    g6: LineSegment StartX=319.85 StartY=-54.1925 StartZ=0 EndX=319.85 EndY=-41.5925 EndZ=0
    g7: LineSegment StartX=319.85 StartY=-41.5925 StartZ=0 EndX=318.8 EndY=-41.5925 EndZ=0
    g8: GeomPoint X=316.8 Y=-47.8925 Z=0
    g9: LineSegment StartX=313.75 StartY=-41.5925 StartZ=0 EndX=313.75 EndY=-47.6025 EndZ=0
    g10: LineSegment StartX=313.75 StartY=-47.6025 StartZ=0 EndX=295.85 EndY=-47.6025 EndZ=0
    g11: LineSegment StartX=295.85 StartY=-41.5925 StartZ=0 EndX=295.85 EndY=-47.6025 EndZ=0
    g12: LineSegment StartX=295.85 StartY=-54.1925 StartZ=0 EndX=295.85 EndY=-50.8025 EndZ=0
    g13: LineSegment StartX=295.85 StartY=-50.8025 StartZ=0 EndX=313.75 EndY=-50.8025 EndZ=0
    g14: LineSegment StartX=313.75 StartY=-50.8025 StartZ=0 EndX=313.75 EndY=-54.1925 EndZ=0
    g15: GeomPoint X=304.8 Y=-47.8925 Z=0
    g16: LineSegment StartX=290.8 StartY=-41.5925 StartZ=0 EndX=290.8 EndY=-39.5925 EndZ=0
    g17: LineSegment StartX=290.8 StartY=-39.5925 StartZ=0 EndX=294.8 EndY=-39.5925 EndZ=0
    g18: LineSegment StartX=294.8 StartY=-39.5925 StartZ=0 EndX=294.8 EndY=-41.5925 EndZ=0
    g19: LineSegment StartX=314.8 StartY=-41.5925 StartZ=0 EndX=314.8 EndY=-39.5925 EndZ=0
    g20: LineSegment StartX=314.8 StartY=-39.5925 StartZ=0 EndX=318.8 EndY=-39.5925 EndZ=0
    g21: LineSegment StartX=318.8 StartY=-39.5925 StartZ=0 EndX=318.8 EndY=-41.5925 EndZ=0
    g22: LineSegment StartX=314.8 StartY=-41.5925 StartZ=0 EndX=313.75 EndY=-41.5925 EndZ=0
    g23: LineSegment StartX=290.8 StartY=-41.5925 StartZ=0 EndX=289.75 EndY=-41.5925 EndZ=0
  constraints (65):
    c: DistanceX(g-1,g0) = 304.8
    c: DistanceY(g0,g-1) = 48.5125
    c: Coincident(g1,g2)
    c: Coincident(g23,g1)
    c: Horizontal(g2)
    c: Horizontal(g3)
    c: Vertical(g1)
    c: Symmetric(g2,g1,g4)
    c: Coincident(g5,g6)
    c: Coincident(g6,g7)
    c: Horizontal(g5)
    c: Horizontal(g7)
    c: Vertical(g6)
    c: Symmetric(g5,g22,g8)
    c: DistanceX(g4,g8) = 24
    c: DistanceY(g1,g1) = 12.6
    c: Equal(g1,g6)
    c: Coincident(g9,g22)
    c: Vertical(g9)
    c: Coincident(g10,g9)
    c: Horizontal(g10)
    c: Coincident(g11,g3)
    c: Coincident(g11,g10)
    c: Vertical(g11)
    c: Coincident(g12,g2)
    c: Vertical(g12)
    c: Coincident(g13,g12)
    c: Horizontal(g13)
    c: Coincident(g14,g13)
    c: Coincident(g14,g5)
    c: Vertical(g14)
    c: DistanceY(g12,g10) = 3.2
    c: Horizontal(g4,g8)
    c: Symmetric(g4,g8,g15)
    c: Vertical(g15,g0)
    c: DistanceY(g0,g15) = 0.62
    c: DistanceY(g12,g12) = 3.39
    c: DistanceX(g2,g2) = 6.1
    c: Vertical(g16)
    c: Coincident(g17,g16)
    c: Horizontal(g17)
    c: Coincident(g18,g17)
    c: Vertical(g18)
    c: Vertical(g19)
    c: Coincident(g20,g19)
    c: Horizontal(g20)
    c: Coincident(g21,g20)
    c: Vertical(g21)
    c: DistanceX(g18,g3) = 1.05
    c: DistanceX(g22,g19) = 1.05
    c: DistanceX(g17,g17) = 4
    c: DistanceX(g20,g20) = 4
    c: DistanceY(g16,g16) = 2
    c: DistanceY(g19,g19) = 2
    c: Coincident(g7,g21)
    c: Coincident(g22,g19)
    c: Coincident(g3,g18)
    c: Coincident(g23,g16)
    c: Equal(g5,g2)
    c: Vertical(g10,g12)
    c: Vertical(g9,g13)
    c: Horizontal(g16,g3)
    c: Horizontal(g23)
    c: Horizontal(g19,g7)
    c: Horizontal(g22)
FEATURE [PartDesign::Pocket] Pocket057
  BaseFeature = -> Pocket056
  Direction = (0,0,-1)
  Length = 5
  Length2 = 5
  Profile = -> Sketch072
  ReferenceAxis = -> Sketch072 [N_Axis]
  Type = 0
FEATURE [Sketcher::SketchObject] Sketch073
  AttachmentOffset = pos=(0,0,5) rot=(0,0,1;0rad)
  FullyConstrained = false
  MapMode = 5
  Placement = pos=(0,0,5) rot=(0,0,1;0rad)
  Support = -> [XY_Plane209]
  expr: Constraints[5] = Spreadsheet.PCB_length
  expr: Constraints[9] = 8 + 1.5 + 5
  sketch-geometry (19):
    g0: GeomPoint X=352.425 Y=3.90395 Z=0
    g1: GeomPoint X=263.925 Y=-8 Z=0
    g2: GeomPoint X=251.425 Y=-8 Z=0
    g3: LineSegment StartX=253.425 StartY=-8 StartZ=0 EndX=261.925 EndY=-8 EndZ=0
    g4: LineSegment StartX=251.425 StartY=-6 StartZ=0 EndX=251.425 EndY=4.5 EndZ=0
    g5: LineSegment StartX=263.925 StartY=-6 StartZ=0 EndX=263.925 EndY=4.5 EndZ=0
    g6: LineSegment StartX=249.425 StartY=6.5 StartZ=0 EndX=-27.3647 EndY=6.5 EndZ=0
    g7: LineSegment StartX=265.925 StartY=6.5 StartZ=0 EndX=398.557 EndY=6.5 EndZ=0
    g8: LineSegment StartX=398.557 StartY=6.5 StartZ=0 EndX=398.557 EndY=82.3248 EndZ=0
    g9: LineSegment StartX=398.557 StartY=82.3248 StartZ=0 EndX=-27.3647 EndY=82.3248 EndZ=0
    g10: LineSegment StartX=-27.3647 StartY=82.3248 StartZ=0 EndX=-27.3647 EndY=6.5 EndZ=0
    g11: ArcOfCircle CenterX=249.425 CenterY=4.5 CenterZ=0 NormalX=0 NormalY=0 NormalZ=1 AngleXU=0 Radius=2 StartAngle=1e-16 EndAngle=1.5708
    g12: GeomPoint X=251.425 Y=6.5 Z=0
    g13: ArcOfCircle CenterX=265.925 CenterY=4.5 CenterZ=0 NormalX=0 NormalY=0 NormalZ=1 AngleXU=0 Radius=2 StartAngle=1.5708 EndAngle=3.14159
    g14: GeomPoint X=263.925 Y=6.5 Z=0
    g15: ArcOfCircle CenterX=261.925 CenterY=-6 CenterZ=0 NormalX=0 NormalY=0 NormalZ=1 AngleXU=0 Radius=2 StartAngle=4.71239 EndAngle=6.28319
    g16: GeomPoint X=263.925 Y=-8 Z=0
    g17: ArcOfCircle CenterX=253.425 CenterY=-6 CenterZ=0 NormalX=0 NormalY=0 NormalZ=1 AngleXU=0 Radius=2 StartAngle=3.14159 EndAngle=4.71239
    g18: GeomPoint X=251.425 Y=-8 Z=0
  constraints (40):
    c: Coincident(g18,g2)
    c: Coincident(g16,g1)
    c: Horizontal(g3)
    c: DistanceX(g16,g0) = 88.5
    c: DistanceX(g18,g0) = 101
    c: DistanceX(g-1,g0) = 352.425
    c: DistanceY(g18,g-1) = 8
    c: Vertical(g4)
    c: Vertical(g5)
    c: DistanceY(g18,g12) = 14.5
    c: Horizontal(g12,g14)
    c: Horizontal(g6)
    c: Horizontal(g7)
    c: Vertical(g8)
    c: Coincident(g9,g8)
    c: Horizontal(g9)
    c: Coincident(g10,g6)
    c: Vertical(g10)
    c: PointOnObject(g12,g4)
    c: PointOnObject(g12,g6)
    c: Tangent(g4,g11) = -1.5708
    c: Tangent(g6,g11) = -1.5708
    c: PointOnObject(g14,g5)
    c: PointOnObject(g14,g7)
    c: Tangent(g5,g13) = 1.5708
    c: Tangent(g7,g13) = 1.5708
    c: Radius(g11) = 2
    c: Radius(g13) = 2
    c: Coincident(g7,g8)
    c: Coincident(g9,g10)
    c: PointOnObject(g16,g5)
    c: PointOnObject(g16,g3)
    c: Tangent(g5,g15) = -1.5708
    c: Tangent(g3,g15) = -1.5708
    c: PointOnObject(g18,g3)
    c: PointOnObject(g18,g4)
    c: Tangent(g3,g17) = -1.5708
    c: Tangent(g4,g17) = 1.5708
    c: Radius(g17) = 2
    c: Radius(g15) = 2
FEATURE [PartDesign::Pocket] Pocket058
  BaseFeature = -> Pocket057
  Direction = (0,0,-1)
  Length = 5
  Length2 = 5
  Profile = -> Sketch073
  ReferenceAxis = -> Sketch073 [N_Axis]
  Type = 0
FEATURE [PartDesign::Body] Body013
  Group = -> [Sketch059,Sketch060,Pad013,Sketch061,Pocket045,Pocket046,Sketch062,Pocket047,Sketch063,Pocket048,Sketch064,Pocket049,Sketch065,Pocket050,Sketch066,Pocket051,Sketch067,Pocket052,Sketch068,Pocket053,Sketch069,Pocket054,Sketch070,Pocket055,Sketch071,Pocket056,Sketch072,Pocket057,Sketch073,Pocket058]
  Origin = -> Origin209
  Tip = -> Pocket058
FEATURE [App::Part] Part  label="plate"
  Group = -> [Body,Body013]
  Origin = -> Origin096
FEATURE [TechDraw::DrawViewPart] View
  CoarseView = false
  Direction = (0,0,1)
  Focus = 100
  HardHidden = false
  IsoCount = 0
  IsoHidden = false
  IsoVisible = false
  LockPosition = false
  Perspective = false
  Rotation = 0
  ScaleType = 0
  SeamHidden = false
  SeamVisible = true
  SmoothHidden = false
  SmoothVisible = true
  Source = -> [Part]
  X = 185.801
  XDirection = (1,0,0)
  Y = 218.409
FEATURE [TechDraw::DrawSVGTemplate] Template006
  Height = 420
  Orientation = 1
  Width = 594
FEATURE [TechDraw::DrawViewPart] View012
  CoarseView = false
  Direction = (0,0,1)
  Focus = 100
  HardHidden = false
  IsoCount = 0
  IsoHidden = false
  IsoVisible = false
  LockPosition = false
  Perspective = false
  Rotation = 0
  ScaleType = 0
  SeamHidden = false
  SeamVisible = true
  SmoothHidden = false
  SmoothVisible = true
  Source = -> [Body013]
  X = 184.806
  XDirection = (1,0,0)
  Y = 341.75
FEATURE [TechDraw::DrawViewPart] View013
  CoarseView = false
  Direction = (0,0,1)
  Focus = 100
  HardHidden = false
  IsoCount = 0
  IsoHidden = false
  IsoVisible = false
  LockPosition = false
  Perspective = false
  Rotation = 0
  ScaleType = 0
  SeamHidden = false
  SeamVisible = true
  SmoothHidden = false
  SmoothVisible = true
  Source = -> [Body]
  X = 184.806
  XDirection = (1,0,0)
  Y = 184.973
FEATURE [TechDraw::DrawPage] Page006  label="plate2"
  KeepUpdated = true
  NextBalloonIndex = 1
  ProjectionType = 0
  Template = -> Template006
  Views = -> [View012,View013]
FEATURE [TechDraw::DrawViewDimension] Dimension
  AngleOverride = false
  Arbitrary = false
  ArbitraryTolerances = false
  EqualTolerance = true
  ExtensionAngle = 0
  FormatSpec = %.2w
  FormatSpecOverTolerance = %+.2w
  FormatSpecUnderTolerance = %+.2w
  Inverted = false
  LineAngle = 0
  LockPosition = false
  MeasureType = 1
  OverTolerance = 0
  References2D = -> [View]
  Rotation = 0
  ScaleType = 0
  TheoreticalExact = false
  Type = 1
  UnderTolerance = 0
  X = -116.681
  Y = -40.6719
FEATURE [TechDraw::DrawViewDimension] Dimension001
  AngleOverride = false
  Arbitrary = false
  ArbitraryTolerances = false
  EqualTolerance = true
  ExtensionAngle = 0
  FormatSpec = %.2w
  FormatSpecOverTolerance = %+.2w
  FormatSpecUnderTolerance = %+.2w
  Inverted = false
  LineAngle = 0
  LockPosition = false
  MeasureType = 1
  OverTolerance = 0
  References2D = -> [View]
  Rotation = 0
  ScaleType = 0
  TheoreticalExact = false
  Type = 1
  UnderTolerance = 0
  X = -104.285
  Y = -32.137
FEATURE [TechDraw::DrawViewDimension] Dimension002
  AngleOverride = false
  Arbitrary = false
  ArbitraryTolerances = false
  EqualTolerance = true
  ExtensionAngle = 0
  FormatSpec = %.2w
  FormatSpecOverTolerance = %+.2w
  FormatSpecUnderTolerance = %+.2w
  Inverted = false
  LineAngle = 0
  LockPosition = false
  MeasureType = 1
  OverTolerance = 0
  References2D = -> [View]
  Rotation = 0
  ScaleType = 0
  TheoreticalExact = false
  Type = 2
  UnderTolerance = 0
  X = -88.6286
  Y = -34.7962
FEATURE [TechDraw::DrawViewDimension] Dimension003
  AngleOverride = false
  Arbitrary = false
  ArbitraryTolerances = false
  EqualTolerance = true
  ExtensionAngle = 0
  FormatSpec = ⌀%.2w
  FormatSpecOverTolerance = %+.2w
  FormatSpecUnderTolerance = %+.2w
  Inverted = false
  LineAngle = 0
  LockPosition = false
  MeasureType = 1
  OverTolerance = 0
  References2D = -> [View]
  Rotation = 0
  ScaleType = 0
  TheoreticalExact = false
  Type = 5
  UnderTolerance = 0
  X = -76.9961
  Y = -64.5288
FEATURE [TechDraw::DrawPage] Page  label="Plate"
  KeepUpdated = true
  NextBalloonIndex = 1
  ProjectionType = 0
  Template = -> Template
  Views = -> [View,Dimension,Dimension001,Dimension002,Dimension003]
FEATURE [Sketcher::SketchObject] Sketch074
  AttachmentOffset = pos=(0,0,2.9) rot=(0,0,1;0rad)
  FullyConstrained = false
  MapMode = 5
  Placement = pos=(0,0,2.9) rot=(0,0,1;0rad)
  Support = -> [XY_Plane210]
  expr: .AttachmentOffset.Base.z = 1.6 + 1.3
  expr: Constraints[25] = Spreadsheet.Bottom_c_rad
  expr: Constraints[26] = Spreadsheet.Bottom_c_rad
  expr: Constraints[29] = Spreadsheet.Spacer_hole
  expr: Constraints[36] = Spreadsheet.PCB_length + Spreadsheet.pcb_to_wall_gap * 2
  expr: Constraints[37] = Spreadsheet.PCB_width + Spreadsheet.pcb_to_wall_gap * 2
  expr: Constraints[54] = Spreadsheet.Bottom_c_rad
  expr: Constraints[57] = Spreadsheet.Bottom_c_rad
  expr: Constraints[5] = Spreadsheet.PCB_length / 2
  expr: Constraints[60] = 2 * Spreadsheet.Top_c_rad * sin(45 / 2)
  expr: Constraints[61] = 2 * Spreadsheet.Top_c_rad * sin(45 / 2)
  expr: Constraints[66] = 2 * Spreadsheet.Top_c_rad * sin(45 / 2)
  expr: Constraints[67] = 2 * Spreadsheet.Top_c_rad * sin(45 / 2)
  expr: Constraints[6] = Spreadsheet.PCB_width / 2
  expr: Constraints[72] = Spreadsheet.wall_thickness / 2
  expr: Constraints[73] = Spreadsheet.PCB_length / 2
  expr: Constraints[74] = (Spreadsheet.PCB_length + Spreadsheet.pcb_to_wall_gap * 2 + Spreadsheet.wall_thickness * 2) / 4
  expr: Constraints[75] = (Spreadsheet.PCB_length + Spreadsheet.pcb_to_wall_gap * 2 + Spreadsheet.wall_thickness * 2) / 4
  expr: Constraints[7] = Spreadsheet.PCB_width + 2 * Spreadsheet.pcb_to_wall_gap + 2 * Spreadsheet.wall_thickness
  expr: Constraints[83] = Spreadsheet.wall_thickness / 2
  expr: Constraints[88] = 2 * Spreadsheet.Bottom_c_rad * sin(45 / 2)
  expr: Constraints[89] = 2 * Spreadsheet.Bottom_c_rad * sin(45 / 2)
  expr: Constraints[8] = Spreadsheet.PCB_length + 2 * Spreadsheet.pcb_to_wall_gap + 2 * Spreadsheet.wall_thickness
  expr: Constraints[92] = 2 * Spreadsheet.Bottom_c_rad * sin(45 / 2)
  expr: Constraints[93] = 2 * Spreadsheet.Bottom_c_rad * sin(45 / 2)
  sketch-geometry (45):
    g0: LineSegment StartX=-6.5 StartY=0.5 StartZ=0 EndX=-6.5 EndY=-142.5 EndZ=0
    g1: LineSegment StartX=-3.5 StartY=-145.5 StartZ=0 EndX=355.925 EndY=-145.5 EndZ=0
    g2: LineSegment StartX=358.925 StartY=-142.5 StartZ=0 EndX=358.925 EndY=0.5 EndZ=0
    g3: LineSegment StartX=352.925 StartY=6.5 StartZ=0 EndX=-0.5 EndY=6.5 EndZ=0
    g4: GeomPoint X=176.213 Y=-69.5 Z=0
    g5: ArcOfCircle CenterX=-0.5 CenterY=0.5 CenterZ=0 NormalX=0 NormalY=0 NormalZ=1 AngleXU=0 Radius=6 StartAngle=1.5708 EndAngle=3.14159
    g6: GeomPoint X=-6.5 Y=6.5 Z=0
    g7: ArcOfCircle CenterX=352.925 CenterY=0.5 CenterZ=0 NormalX=0 NormalY=0 NormalZ=1 AngleXU=0 Radius=6 StartAngle=0 EndAngle=1.5708
    g8: GeomPoint X=358.925 Y=6.5 Z=0
    g9: ArcOfCircle CenterX=-3.5 CenterY=-142.5 CenterZ=0 NormalX=0 NormalY=0 NormalZ=1 AngleXU=0 Radius=3 StartAngle=3.14159 EndAngle=4.71239
    g10: GeomPoint X=-6.5 Y=-145.5 Z=0
    g11: ArcOfCircle CenterX=355.925 CenterY=-142.5 CenterZ=0 NormalX=0 NormalY=0 NormalZ=1 AngleXU=0 Radius=3 StartAngle=4.71239 EndAngle=6.28319
    g12: GeomPoint X=358.925 Y=-145.5 Z=0
    g13: Circle CenterX=-1.74264 CenterY=1.74264 CenterZ=0 NormalX=0 NormalY=0 NormalZ=1 AngleXU=0 Radius=1.55
    g14: LineSegment StartX=-0.5 StartY=-5.5 StartZ=0 EndX=-0.5 EndY=-136.5 EndZ=0
    g15: LineSegment StartX=2.5 StartY=-139.5 StartZ=0 EndX=349.925 EndY=-139.5 EndZ=0
    g16: LineSegment StartX=352.925 StartY=-136.5 StartZ=0 EndX=352.925 EndY=-5.5 EndZ=0
    g17: LineSegment StartX=346.925 StartY=0.5 StartZ=0 EndX=5.5 EndY=0.5 EndZ=0
    g18: GeomPoint X=176.213 Y=-69.5 Z=0
    g19: ArcOfCircle CenterX=5.5 CenterY=-5.5 CenterZ=0 NormalX=0 NormalY=0 NormalZ=1 AngleXU=0 Radius=6 StartAngle=1.5708 EndAngle=3.14159
    g20: GeomPoint X=-0.5 Y=0.5 Z=0
    g21: ArcOfCircle CenterX=346.925 CenterY=-5.5 CenterZ=0 NormalX=0 NormalY=0 NormalZ=1 AngleXU=0 Radius=6 StartAngle=0 EndAngle=1.5708
    g22: GeomPoint X=352.925 Y=0.5 Z=0
    g23: ArcOfCircle CenterX=349.925 CenterY=-136.5 CenterZ=0 NormalX=0 NormalY=0 NormalZ=1 AngleXU=0 Radius=3 StartAngle=4.71239 EndAngle=6.28319
    g24: GeomPoint X=352.925 Y=-139.5 Z=0
    g25: ArcOfCircle CenterX=2.5 CenterY=-136.5 CenterZ=0 NormalX=0 NormalY=0 NormalZ=1 AngleXU=0 Radius=3 StartAngle=3.14159 EndAngle=4.71239
    g26: GeomPoint X=-0.5 Y=-139.5 Z=0
    g27: GeomPoint X=-4.74264 Y=4.74264 Z=0
    g28: GeomPoint X=1.25736 Y=-1.25736 Z=0
    g29: Circle CenterX=354.168 CenterY=1.74264 CenterZ=0 NormalX=0 NormalY=0 NormalZ=1 AngleXU=0 Radius=1.55
    g30: GeomPoint X=351.168 Y=-1.25736 Z=0
    g31: GeomPoint X=357.168 Y=4.74264 Z=0
    g32: Circle CenterX=84.8563 CenterY=3.5 CenterZ=0 NormalX=0 NormalY=0 NormalZ=1 AngleXU=0 Radius=1.55
    g33: Circle CenterX=176.213 CenterY=3.5 CenterZ=0 NormalX=0 NormalY=0 NormalZ=1 AngleXU=0 Radius=1.55
    g34: Circle CenterX=267.569 CenterY=3.5 CenterZ=0 NormalX=0 NormalY=0 NormalZ=1 AngleXU=0 Radius=1.55
    g35: Circle CenterX=84.8563 CenterY=-142.5 CenterZ=0 NormalX=0 NormalY=0 NormalZ=1 AngleXU=0 Radius=1.55
    g36: Circle CenterX=176.213 CenterY=-142.5 CenterZ=0 NormalX=0 NormalY=0 NormalZ=1 AngleXU=0 Radius=1.55
    g37: Circle CenterX=267.569 CenterY=-142.5 CenterZ=0 NormalX=0 NormalY=0 NormalZ=1 AngleXU=0 Radius=1.55
    g38: Circle CenterX=-2.62132 CenterY=-141.621 CenterZ=0 NormalX=0 NormalY=0 NormalZ=1 AngleXU=0 Radius=1.55
    g39: GeomPoint X=0.37868 Y=-138.621 Z=0
    g40: GeomPoint X=-5.62132 Y=-144.621 Z=0
    g41: GeomPoint X=6.2644 Y=-139.5 Z=0
    g42: GeomPoint X=352.046 Y=-138.621 Z=0
    g43: GeomPoint X=358.046 Y=-144.621 Z=0
    g44: Circle CenterX=355.046 CenterY=-141.621 CenterZ=0 NormalX=0 NormalY=0 NormalZ=1 AngleXU=0 Radius=1.55
  constraints (100):
    c: Horizontal(g1)
    c: Horizontal(g3)
    c: Vertical(g0)
    c: Vertical(g2)
    c: Symmetric(g12,g6,g4)
    c: DistanceX(g-1,g4) = 176.213
    c: DistanceY(g4,g-1) = 69.5
    c: DistanceY(g10,g6) = 152
    c: DistanceX(g6,g8) = 365.425
    c: PointOnObject(g6,g0)
    c: PointOnObject(g6,g3)
    c: Tangent(g0,g5) = -1.5708
    c: Tangent(g3,g5) = -1.5708
    c: PointOnObject(g8,g2)
    c: PointOnObject(g8,g3)
    c: Tangent(g2,g7) = -1.5708
    c: Tangent(g3,g7) = -1.5708
    c: PointOnObject(g10,g0)
    c: PointOnObject(g10,g1)
    c: Tangent(g0,g9) = -1.5708
    c: Tangent(g1,g9) = -1.5708
    c: PointOnObject(g12,g1)
    c: PointOnObject(g12,g2)
    c: Tangent(g1,g11) = -1.5708
    c: Tangent(g2,g11) = -1.5708
    c: Radius(g11) = 3
    c: Radius(g9) = 3
    c: Radius(g5) = 6
    c: Radius(g7) = 6
    c: Diameter(g13) = 3.1
    c: Horizontal(g15)
    c: Horizontal(g17)
    c: Vertical(g14)
    c: Vertical(g16)
    c: Symmetric(g24,g20,g18)
    c: Coincident(g18,g4)
    c: DistanceX(g20,g22) = 353.425
    c: DistanceY(g26,g20) = 140
    c: PointOnObject(g20,g14)
    c: PointOnObject(g20,g17)
    c: Tangent(g14,g19) = -1.5708
    c: Tangent(g17,g19) = -1.5708
    c: PointOnObject(g22,g16)
    c: PointOnObject(g22,g17)
    c: Tangent(g16,g21) = -1.5708
    c: Tangent(g17,g21) = -1.5708
    c: PointOnObject(g24,g15)
    c: PointOnObject(g24,g16)
    c: Tangent(g15,g23) = -1.5708
    c: Tangent(g16,g23) = -1.5708
    c: PointOnObject(g26,g14)
    c: PointOnObject(g26,g15)
    c: Tangent(g14,g25) = -1.5708
    c: Tangent(g15,g25) = -1.5708
    c: Radius(g25) = 3
    c: Radius(g19) = 6
    c: Radius(g21) = 6
    c: Radius(g23) = 3
    c: PointOnObject(g27,g5)
    c: PointOnObject(g28,g19)
    c: Distance(g14,g28) = 4.5922
    c: Distance(g0,g27) = 4.5922
    c: Symmetric(g27,g28,g13)
    c: Diameter(g29) = 3.1
    c: PointOnObject(g30,g21)
    c: PointOnObject(g31,g7)
    c: Distance(g30,g16) = 4.5922
    c: Distance(g2,g31) = 4.5922
    c: Symmetric(g30,g31,g29)
    c: Equal(g32,g33)
    c: Equal(g34,g33)
    c: Diameter(g33) = 3.1
    c: Distance(g33,g3) = 3
    c: DistanceX(g-1,g33) = 176.213
    c: DistanceX(g32,g33) = 91.3563
    c: DistanceX(g33,g34) = 91.3563
    c: Equal(g35,g36)
    c: Equal(g37,g36)
    c: Equal(g33,g36) = 3.1
    c: DistanceX(g35,g36) = 91.3563
    c: DistanceX(g36,g37) = 91.3563
    c: Horizontal(g35,g36)
    c: Horizontal(g37,g36)
    c: Distance(g36,g1) = 3
    c: Vertical(g36,g33)
    c: PointOnObject(g39,g25)
    c: PointOnObject(g40,g9)
    c: PointOnObject(g41,g15)
    c: Distance(g39,g14) = 2.2961
    c: Distance(g0,g40) = 2.2961
    c: PointOnObject(g42,g23)
    c: PointOnObject(g43,g11)
    c: Distance(g15,g42) = 2.2961
    c: Distance(g1,g43) = 2.2961
    c: Symmetric(g42,g43,g44)
    c: Diameter(g44) = 3.1
    c: Diameter(g38) = 3.1
    c: Symmetric(g40,g39,g38)
    c: Horizontal(g32,g33)
    c: Horizontal(g34,g33)
FEATURE [PartDesign::Pad] Pad014
  Direction = (0,0,1)
  Length = 2
  Length2 = 10
  Profile = -> Sketch074
  ReferenceAxis = -> Sketch074 [N_Axis]
  Type = 0
FEATURE [PartDesign::Body] Body014
  Group = -> [Sketch074,Pad014]
  Origin = -> Origin210
  Placement = pos=(0,0,-8) rot=(0,0,1;0rad)
  Tip = -> Pad014
FEATURE [App::Part] Part001  label="Spacer"
  Group = -> [Body001,Body002,Body004,Body014]
  Origin = -> Origin193
FEATURE [Sketcher::SketchObject] Sketch076
  AttachmentOffset = pos=(0,0,2.9) rot=(0,0,1;0rad)
  FullyConstrained = false
  MapMode = 5
  Placement = pos=(0,0,2.9) rot=(0,0,1;0rad)
  Support = -> [XY_Plane211]
  expr: .AttachmentOffset.Base.z = 1.6 + 1.3
  expr: Constraints[25] = Spreadsheet.Bottom_c_rad
  expr: Constraints[26] = Spreadsheet.Bottom_c_rad
  expr: Constraints[29] = Spreadsheet.Spacer_hole
  expr: Constraints[32] = Spreadsheet.PCB_length + Spreadsheet.pcb_to_wall_gap * 2
  expr: Constraints[33] = Spreadsheet.PCB_width + Spreadsheet.pcb_to_wall_gap * 2
  expr: Constraints[35] = 2 * Spreadsheet.Top_c_rad * sin(45 / 2)
  expr: Constraints[37] = Spreadsheet.Spacer_hole
  expr: Constraints[39] = 2 * Spreadsheet.Top_c_rad * sin(45 / 2)
  expr: Constraints[43] = Spreadsheet.Spacer_hole
  expr: Constraints[44] = Spreadsheet.wall_thickness / 2
  expr: Constraints[45] = Spreadsheet.PCB_length / 2
  expr: Constraints[46] = (Spreadsheet.PCB_length + Spreadsheet.pcb_to_wall_gap * 2 + Spreadsheet.wall_thickness * 2) / 4
  expr: Constraints[47] = (Spreadsheet.PCB_length + Spreadsheet.pcb_to_wall_gap * 2 + Spreadsheet.wall_thickness * 2) / 4
  expr: Constraints[54] = Spreadsheet.wall_thickness / 2
  expr: Constraints[57] = 2 * Spreadsheet.Bottom_c_rad * sin(45 / 2)
  expr: Constraints[59] = 2 * Spreadsheet.Bottom_c_rad * sin(45 / 2)
  expr: Constraints[5] = Spreadsheet.PCB_length / 2
  expr: Constraints[61] = Spreadsheet.Spacer_hole
  expr: Constraints[62] = Spreadsheet.Spacer_hole
  expr: Constraints[66] = Spreadsheet.Spacer_hole
  expr: Constraints[6] = Spreadsheet.PCB_width / 2
  expr: Constraints[7] = Spreadsheet.PCB_width + 2 * Spreadsheet.pcb_to_wall_gap + 2 * Spreadsheet.wall_thickness
  expr: Constraints[8] = Spreadsheet.PCB_length + 2 * Spreadsheet.pcb_to_wall_gap + 2 * Spreadsheet.wall_thickness
  sketch-geometry (36):
    g0: LineSegment StartX=-6.5 StartY=0.5 StartZ=0 EndX=-6.5 EndY=-142.5 EndZ=0
    g1: LineSegment StartX=-3.5 StartY=-145.5 StartZ=0 EndX=355.925 EndY=-145.5 EndZ=0
    g2: LineSegment StartX=358.925 StartY=-142.5 StartZ=0 EndX=358.925 EndY=0.5 EndZ=0
    g3: LineSegment StartX=352.925 StartY=6.5 StartZ=0 EndX=-0.5 EndY=6.5 EndZ=0
    g4: GeomPoint X=176.213 Y=-69.5 Z=0
    g5: ArcOfCircle CenterX=-0.5 CenterY=0.5 CenterZ=0 NormalX=0 NormalY=0 NormalZ=1 AngleXU=0 Radius=6 StartAngle=1.5708 EndAngle=3.14159
    g6: GeomPoint X=-6.5 Y=6.5 Z=0
    g7: ArcOfCircle CenterX=352.925 CenterY=0.5 CenterZ=0 NormalX=0 NormalY=0 NormalZ=1 AngleXU=0 Radius=6 StartAngle=0 EndAngle=1.5708
    g8: GeomPoint X=358.925 Y=6.5 Z=0
    g9: ArcOfCircle CenterX=-3.5 CenterY=-142.5 CenterZ=0 NormalX=0 NormalY=0 NormalZ=1 AngleXU=0 Radius=3 StartAngle=3.14159 EndAngle=4.71239
    g10: GeomPoint X=-6.5 Y=-145.5 Z=0
    g11: ArcOfCircle CenterX=355.925 CenterY=-142.5 CenterZ=0 NormalX=0 NormalY=0 NormalZ=1 AngleXU=0 Radius=3 StartAngle=4.71239 EndAngle=6.28319
    g12: GeomPoint X=358.925 Y=-145.5 Z=0
    g13: Circle CenterX=-1.74259 CenterY=1.74261 CenterZ=0 NormalX=0 NormalY=0 NormalZ=1 AngleXU=0 Radius=1.55
    g14: GeomPoint X=176.213 Y=-69.5 Z=0
    g15: GeomPoint X=-1.67193 Y=0.402977 Z=0
    g16: GeomPoint X=351.753 Y=0.5 Z=0
    g17: GeomPoint X=354.097 Y=-139.403 Z=0
    g18: GeomPoint X=-0.5 Y=-139.597 Z=0
    g19: GeomPoint X=-4.74264 Y=4.74264 Z=0
    g20: GeomPoint X=1.25746 Y=-1.25743 Z=0
    g21: Circle CenterX=354.168 CenterY=1.74261 CenterZ=0 NormalX=0 NormalY=0 NormalZ=1 AngleXU=0 Radius=1.55
    g22: GeomPoint X=351.168 Y=-1.25743 Z=0
    g23: GeomPoint X=357.168 Y=4.74264 Z=0
    g24: Circle CenterX=84.8563 CenterY=3.5 CenterZ=0 NormalX=0 NormalY=0 NormalZ=1 AngleXU=0 Radius=1.55
    g25: Circle CenterX=176.213 CenterY=3.5 CenterZ=0 NormalX=0 NormalY=0 NormalZ=1 AngleXU=0 Radius=1.55
    g26: Circle CenterX=267.569 CenterY=3.5 CenterZ=0 NormalX=0 NormalY=0 NormalZ=1 AngleXU=0 Radius=1.55
    g27: Circle CenterX=84.8563 CenterY=-142.5 CenterZ=0 NormalX=0 NormalY=0 NormalZ=1 AngleXU=0 Radius=1.55
    g28: Circle CenterX=176.213 CenterY=-142.5 CenterZ=0 NormalX=0 NormalY=0 NormalZ=1 AngleXU=0 Radius=1.55
    g29: Circle CenterX=267.569 CenterY=-142.5 CenterZ=0 NormalX=0 NormalY=0 NormalZ=1 AngleXU=0 Radius=1.55
    g30: Circle CenterX=-2.62127 CenterY=-141.621 CenterZ=0 NormalX=0 NormalY=0 NormalZ=1 AngleXU=0 Radius=1.55
    g31: GeomPoint X=0.378778 Y=-138.621 Z=0
    g32: GeomPoint X=-5.62132 Y=-144.621 Z=0
    g33: GeomPoint X=352.047 Y=-138.621 Z=0
    g34: GeomPoint X=358.046 Y=-144.621 Z=0
    g35: Circle CenterX=355.047 CenterY=-141.621 CenterZ=0 NormalX=0 NormalY=0 NormalZ=1 AngleXU=0 Radius=1.55
  constraints (67):
    c: Horizontal(g1)
    c: Horizontal(g3)
    c: Vertical(g0)
    c: Vertical(g2)
    c: Symmetric(g12,g6,g4)
    c: DistanceX(g-1,g4) = 176.213
    c: DistanceY(g4,g-1) = 69.5
    c: DistanceY(g10,g6) = 152
    c: DistanceX(g6,g8) = 365.425
    c: PointOnObject(g6,g0)
    c: PointOnObject(g6,g3)
    c: Tangent(g0,g5) = -1.5708
    c: Tangent(g3,g5) = -1.5708
    c: PointOnObject(g8,g2)
    c: PointOnObject(g8,g3)
    c: Tangent(g2,g7) = -1.5708
    c: Tangent(g3,g7) = -1.5708
    c: PointOnObject(g10,g0)
    c: PointOnObject(g10,g1)
    c: Tangent(g0,g9) = -1.5708
    c: Tangent(g1,g9) = -1.5708
    c: PointOnObject(g12,g1)
    c: PointOnObject(g12,g2)
    c: Tangent(g1,g11) = -1.5708
    c: Tangent(g2,g11) = -1.5708
    c: Radius(g11) = 3
    c: Radius(g9) = 3
    c: Radius(g5) = 6
    c: Radius(g7) = 6
    c: Diameter(g13) = 3.1
    c: Symmetric(g17,g15,g14)
    c: Coincident(g14,g4)
    c: DistanceX(g15,g16) = 353.425
    c: DistanceY(g18,g15) = 140
    c: PointOnObject(g19,g5)
    c: Distance(g0,g19) = 4.5922
    c: Symmetric(g19,g20,g13)
    c: Diameter(g21) = 3.1
    c: PointOnObject(g23,g7)
    c: Distance(g2,g23) = 4.5922
    c: Symmetric(g22,g23,g21)
    c: Equal(g24,g25)
    c: Equal(g26,g25)
    c: Diameter(g25) = 3.1
    c: Distance(g25,g3) = 3
    c: DistanceX(g-1,g25) = 176.213
    c: DistanceX(g24,g25) = 91.3563
    c: DistanceX(g25,g26) = 91.3563
    c: Equal(g27,g28)
    c: Equal(g29,g28)
    c: DistanceX(g27,g28) = 91.3563
    c: DistanceX(g28,g29) = 91.3563
    c: Horizontal(g27,g28)
    c: Horizontal(g29,g28)
    c: Distance(g28,g1) = 3
    c: Vertical(g28,g25)
    c: PointOnObject(g32,g9)
    c: Distance(g0,g32) = 2.2961
    c: PointOnObject(g34,g11)
    c: Distance(g1,g34) = 2.2961
    c: Symmetric(g33,g34,g35)
    c: Diameter(g35) = 3.1
    c: Diameter(g30) = 3.1
    c: Symmetric(g32,g31,g30)
    c: Horizontal(g24,g25)
    c: Horizontal(g26,g25)
    c: Diameter(g28) = 3.1
FEATURE [PartDesign::Pad] Pad015
  Direction = (0,0,1)
  Length = 2
  Length2 = 10
  Profile = -> Sketch076
  ReferenceAxis = -> Sketch076 [N_Axis]
  Type = 0
FEATURE [Sketcher::SketchObject] Sketch077
  AttachmentOffset = pos=(0,0,6) rot=(0,0,1;0rad)
  FullyConstrained = false
  MapMode = 5
  Placement = pos=(0,0,6) rot=(0,0,1;0rad)
  Support = -> [XY_Plane211]
  expr: Constraints[5] = Spreadsheet.u
  sketch-geometry (13):
    g0: LineSegment StartX=8.16089 StartY=-46.667 StartZ=0 EndX=8.16089 EndY=-57.0051 EndZ=0
    g1: LineSegment StartX=10.1609 StartY=-59.0051 StartZ=0 EndX=27.9391 EndY=-59.0051 EndZ=0
    g2: LineSegment StartX=29.9391 StartY=-57.0051 StartZ=0 EndX=29.9391 EndY=-46.667 EndZ=0
    g3: LineSegment StartX=27.9391 StartY=-44.667 StartZ=0 EndX=10.1609 EndY=-44.667 EndZ=0
    g4: GeomPoint X=19.05 Y=-51.836 Z=0
    g5: ArcOfCircle CenterX=10.1609 CenterY=-46.667 CenterZ=0 NormalX=0 NormalY=0 NormalZ=1 AngleXU=0 Radius=2 StartAngle=1.5708 EndAngle=3.14159
    g6: GeomPoint X=8.16089 Y=-44.667 Z=0
    g7: ArcOfCircle CenterX=27.9391 CenterY=-46.667 CenterZ=0 NormalX=0 NormalY=0 NormalZ=1 AngleXU=0 Radius=2 StartAngle=1.6e-15 EndAngle=1.5708
    g8: GeomPoint X=29.9391 Y=-44.667 Z=0
    g9: ArcOfCircle CenterX=10.1609 CenterY=-57.0051 CenterZ=0 NormalX=0 NormalY=0 NormalZ=1 AngleXU=0 Radius=2 StartAngle=3.14159 EndAngle=4.71239
    g10: GeomPoint X=8.16089 Y=-59.0051 Z=0
    g11: ArcOfCircle CenterX=27.9391 CenterY=-57.0051 CenterZ=0 NormalX=0 NormalY=0 NormalZ=1 AngleXU=0 Radius=2 StartAngle=4.71239 EndAngle=6.28319
    g12: GeomPoint X=29.9391 Y=-59.0051 Z=0
  constraints (26):
    c: Horizontal(g1)
    c: Horizontal(g3)
    c: Vertical(g0)
    c: Vertical(g2)
    c: Symmetric(g12,g6,g4)
    c: DistanceX(g-1,g4) = 19.05
    c: PointOnObject(g6,g0)
    c: PointOnObject(g6,g3)
    c: Tangent(g0,g5) = -1.5708
    c: Tangent(g3,g5) = -1.5708
    c: PointOnObject(g8,g2)
    c: PointOnObject(g8,g3)
    c: Tangent(g2,g7) = -1.5708
    c: Tangent(g3,g7) = -1.5708
    c: PointOnObject(g10,g0)
    c: PointOnObject(g10,g1)
    c: Tangent(g0,g9) = -1.5708
    c: Tangent(g1,g9) = -1.5708
    c: PointOnObject(g12,g1)
    c: PointOnObject(g12,g2)
    c: Tangent(g1,g11) = -1.5708
    c: Tangent(g2,g11) = -1.5708
    c: Equal(g9,g11)
    c: Equal(g11,g7)
    c: Equal(g7,g5)
    c: Radius(g9) = 2
FEATURE [PartDesign::Pocket] Pocket060
  BaseFeature = -> Pad015
  Direction = (0,0,-1)
  Length = 5
  Length2 = 5
  Profile = -> Sketch077
  ReferenceAxis = -> Sketch077 [N_Axis]
  Type = 0
FEATURE [Sketcher::SketchObject] Sketch078
  AttachmentOffset = pos=(0,0,6) rot=(0,0,1;0rad)
  FullyConstrained = false
  MapMode = 5
  Placement = pos=(0,0,6) rot=(0,0,1;0rad)
  Support = -> [XY_Plane211]
  expr: Constraints[0] = Spreadsheet.PCB_length / 2
  expr: Constraints[11] = Spreadsheet.Spacer_hole
  expr: Constraints[1] = Spreadsheet.PCB_width / 2
  sketch-geometry (15):
    g0: GeomPoint X=176.213 Y=-69.5 Z=0
    g1: GeomPoint X=-6.5 Y=-145.5 Z=0
    g2: GeomPoint X=358.925 Y=-145.5 Z=0
    g3: GeomPoint X=176.213 Y=-69.5 Z=0
    g4: GeomPoint X=354.097 Y=-139.403 Z=0
    g5: GeomPoint X=-0.5 Y=-139.597 Z=0
    g6: Circle CenterX=84.8563 CenterY=-142.5 CenterZ=0 NormalX=0 NormalY=0 NormalZ=1 AngleXU=0 Radius=1.55
    g7: Circle CenterX=176.213 CenterY=-142.5 CenterZ=0 NormalX=0 NormalY=0 NormalZ=1 AngleXU=0 Radius=1.55
    g8: Circle CenterX=267.569 CenterY=-142.5 CenterZ=0 NormalX=0 NormalY=0 NormalZ=1 AngleXU=0 Radius=1.55
    g9: Circle CenterX=-2.62127 CenterY=-141.621 CenterZ=0 NormalX=0 NormalY=0 NormalZ=1 AngleXU=0 Radius=1.55
    g10: GeomPoint X=0.378778 Y=-138.621 Z=0
    g11: GeomPoint X=-5.62132 Y=-144.621 Z=0
    g12: GeomPoint X=352.047 Y=-138.621 Z=0
    g13: GeomPoint X=358.046 Y=-144.621 Z=0
    g14: Circle CenterX=355.047 CenterY=-141.621 CenterZ=0 NormalX=0 NormalY=0 NormalZ=1 AngleXU=0 Radius=1.55
  constraints (14):
    c: DistanceX(g-1,g0) = 176.213
    c: DistanceY(g0,g-1) = 69.5
    c: Coincident(g3,g0)
    c: Equal(g6,g7)
    c: Equal(g8,g7)
    c: DistanceX(g6,g7) = 91.3563
    c: DistanceX(g7,g8) = 91.3563
    c: Horizontal(g6,g7)
    c: Horizontal(g8,g7)
    c: Symmetric(g12,g13,g14)
    c: Symmetric(g11,g10,g9)
    c: Diameter(g7) = 3.1
    c: Equal(g9,g6)
    c: Equal(g14,g8)
FEATURE [PartDesign::Pocket] Pocket061
  BaseFeature = -> Pocket060
  Direction = (0,0,-1)
  Length = 1
  Length2 = 5
  Profile = -> Sketch078
  ReferenceAxis = -> Sketch078 [N_Axis]
  Type = 0
FEATURE [Sketcher::SketchObject] Sketch079
  AttachmentOffset = pos=(0,0,2.9) rot=(0,0,1;0rad)
  FullyConstrained = false
  MapMode = 5
  Placement = pos=(0,0,2.9) rot=(0,0,1;0rad)
  Support = -> [XY_Plane211]
  expr: Constraints[0] = Spreadsheet.PCB_length / 2
  sketch-geometry (3):
    g0: GeomPoint X=176.213 Y=-127.899 Z=0
    g1: Circle CenterX=5.01141 CenterY=-127.899 CenterZ=0 NormalX=0 NormalY=0 NormalZ=1 AngleXU=0 Radius=4.05
    g2: Circle CenterX=347.414 CenterY=-127.899 CenterZ=0 NormalX=0 NormalY=0 NormalZ=1 AngleXU=0 Radius=4.05
  constraints (5):
    c: DistanceX(g-1,g0) = 176.213
    c: Symmetric(g2,g1,g0)
    c: Equal(g2,g1)
    c: Diameter(g2) = 8.1
    c: Horizontal(g2,g1)
FEATURE [PartDesign::Pocket] Pocket062
  BaseFeature = -> Pocket061
  Direction = (0,0,-1)
  Length = 1
  Length2 = 5
  Profile = -> Sketch079
  ReferenceAxis = -> Sketch079 [N_Axis]
  Type = 0
FEATURE [PartDesign::Body] Body015  label="Bottom case001"
  Group = -> [Sketch076,Pad015,Sketch077,Pocket060,Sketch078,Pocket061,Sketch079,Pocket062]
  Origin = -> Origin211
  Placement = pos=(0,0,-6) rot=(0,0,1;0rad)
  Tip = -> Pocket062
FEATURE [Sketcher::SketchObject] Sketch080
  AttachmentOffset = pos=(0,0,2.9) rot=(0,0,1;0rad)
  FullyConstrained = false
  MapMode = 5
  Placement = pos=(0,0,2.9) rot=(0,0,1;0rad)
  Support = -> [XY_Plane212]
  expr: .AttachmentOffset.Base.z = 1.6 + 1.3
  expr: Constraints[25] = Spreadsheet.Bottom_c_rad
  expr: Constraints[26] = Spreadsheet.Bottom_c_rad
  expr: Constraints[30] = Spreadsheet.PCB_width + Spreadsheet.pcb_to_wall_gap * 2
  expr: Constraints[32] = 2 * Spreadsheet.Top_c_rad * sin(45 / 2)
  expr: Constraints[36] = 2 * Spreadsheet.Bottom_c_rad * sin(45 / 2)
  expr: Constraints[38] = 2 * Spreadsheet.Bottom_c_rad * sin(45 / 2)
  expr: Constraints[5] = (Spreadsheet.u * 2 - 0.5 - Spreadsheet.wall_thickness - Spreadsheet.pcb_to_wall_gap) / 2
  expr: Constraints[6] = Spreadsheet.PCB_width / 2
  expr: Constraints[7] = Spreadsheet.PCB_width + 2 * Spreadsheet.pcb_to_wall_gap + 2 * Spreadsheet.wall_thickness
  expr: Constraints[8] = Spreadsheet.wall_thickness + Spreadsheet.pcb_to_wall_gap + Spreadsheet.u * 2 - 0.5
  sketch-geometry (24):
    g0: LineSegment StartX=-6.5 StartY=0.5 StartZ=0 EndX=-6.5 EndY=-142.5 EndZ=0
    g1: LineSegment StartX=-3.5 StartY=-145.5 StartZ=0 EndX=34.6 EndY=-145.5 EndZ=0
    g2: LineSegment StartX=37.6 StartY=-142.5 StartZ=0 EndX=37.6 EndY=0.5 EndZ=0
    g3: LineSegment StartX=31.6 StartY=6.5 StartZ=0 EndX=-0.5 EndY=6.5 EndZ=0
    g4: GeomPoint X=15.55 Y=-69.5 Z=0
    g5: ArcOfCircle CenterX=-0.5 CenterY=0.5 CenterZ=0 NormalX=0 NormalY=0 NormalZ=1 AngleXU=0 Radius=6 StartAngle=1.5708 EndAngle=3.14159
    g6: GeomPoint X=-6.5 Y=6.5 Z=0
    g7: ArcOfCircle CenterX=31.6 CenterY=0.5 CenterZ=0 NormalX=0 NormalY=0 NormalZ=1 AngleXU=0 Radius=6 StartAngle=0 EndAngle=1.5708
    g8: GeomPoint X=37.6 Y=6.5 Z=0
    g9: ArcOfCircle CenterX=-3.5 CenterY=-142.5 CenterZ=0 NormalX=0 NormalY=0 NormalZ=1 AngleXU=0 Radius=3 StartAngle=3.14159 EndAngle=4.71239
    g10: GeomPoint X=-6.5 Y=-145.5 Z=0
    g11: ArcOfCircle CenterX=34.6 CenterY=-142.5 CenterZ=0 NormalX=0 NormalY=0 NormalZ=1 AngleXU=0 Radius=3 StartAngle=4.71239 EndAngle=6.28319
    g12: GeomPoint X=37.6 Y=-145.5 Z=0
    g13: Circle CenterX=-1.74264 CenterY=1.74264 CenterZ=0 NormalX=0 NormalY=0 NormalZ=1 AngleXU=0 Radius=1.05
    g14: GeomPoint X=15.55 Y=-69.5 Z=0
    g15: GeomPoint X=-1.66549 Y=1.10512 Z=0
    g16: GeomPoint X=-0.5 Y=-138.895 Z=0
    g17: GeomPoint X=-4.74264 Y=4.74264 Z=0
    g18: GeomPoint X=1.25736 Y=-1.25736 Z=0
    g19: GeomPoint X=36.6695 Y=3.70941 Z=0
    g20: Circle CenterX=-2.62132 CenterY=-141.621 CenterZ=0 NormalX=0 NormalY=0 NormalZ=1 AngleXU=0 Radius=1.05
    g21: GeomPoint X=0.37868 Y=-138.621 Z=0
    g22: GeomPoint X=-5.62132 Y=-144.621 Z=0
    g23: GeomPoint X=36.7213 Y=-144.621 Z=0
  constraints (42):
    c: Horizontal(g1)
    c: Horizontal(g3)
    c: Vertical(g0)
    c: Vertical(g2)
    c: Symmetric(g12,g6,g4)
    c: DistanceX(g-1,g4) = 15.55
    c: DistanceY(g4,g-1) = 69.5
    c: DistanceY(g10,g6) = 152
    c: DistanceX(g6,g8) = 44.1
    c: PointOnObject(g6,g0)
    c: PointOnObject(g6,g3)
    c: Tangent(g0,g5) = -1.5708
    c: Tangent(g3,g5) = -1.5708
    c: PointOnObject(g8,g2)
    c: PointOnObject(g8,g3)
    c: Tangent(g2,g7) = -1.5708
    c: Tangent(g3,g7) = -1.5708
    c: PointOnObject(g10,g0)
    c: PointOnObject(g10,g1)
    c: Tangent(g0,g9) = -1.5708
    c: Tangent(g1,g9) = -1.5708
    c: PointOnObject(g12,g1)
    c: PointOnObject(g12,g2)
    c: Tangent(g1,g11) = -1.5708
    c: Tangent(g2,g11) = -1.5708
    c: Radius(g11) = 3
    c: Radius(g9) = 3
    c: Radius(g5) = 6
    c: Radius(g7) = 6
    c: Coincident(g14,g4)
    c: DistanceY(g16,g15) = 140
    c: PointOnObject(g17,g5)
    c: Distance(g0,g17) = 4.5922
    c: Symmetric(g17,g18,g13)
    c: PointOnObject(g19,g7)
    c: PointOnObject(g22,g9)
    c: Distance(g0,g22) = 2.2961
    c: PointOnObject(g23,g11)
    c: Distance(g1,g23) = 2.2961
    c: Symmetric(g22,g21,g20)
    c: Block(g13)
    c: Block(g20)
FEATURE [PartDesign::Pad] Pad016
  Direction = (0,0,1)
  Length = 2
  Length2 = 10
  Profile = -> Sketch080
  ReferenceAxis = -> Sketch080 [N_Axis]
  Type = 0
FEATURE [Sketcher::SketchObject] Sketch081
  AttachmentOffset = pos=(0,0,5) rot=(0,0,1;0rad)
  FullyConstrained = true
  MapMode = 5
  Placement = pos=(0,0,5) rot=(0,0,1;0rad)
  Support = -> [XY_Plane212]
  expr: Constraints[10] = Spreadsheet.PCB_width - Spreadsheet.u * 6
  expr: Constraints[11] = Spreadsheet.u * 2.5
  expr: Constraints[12] = Spreadsheet.u + 1
  expr: Constraints[13] = Spreadsheet.u * 4 + 1
  expr: Constraints[15] = Spreadsheet.u * (0.5 + 0.25 + 2)
  expr: Constraints[166] = Spreadsheet.u + 1
  expr: Constraints[167] = Spreadsheet.key_fillet
  expr: Constraints[168] = Spreadsheet.u + 1
  expr: Constraints[169] = Spreadsheet.u + 1
  expr: Constraints[170] = Spreadsheet.u * 4 + 1
  expr: Constraints[171] = Spreadsheet.u * 4 + 1
  expr: Constraints[172] = Spreadsheet.u + 1
  expr: Constraints[173] = Spreadsheet.u + 1
  expr: Constraints[174] = Spreadsheet.u + 1
  expr: Constraints[175] = Spreadsheet.u + 1
  expr: Constraints[176] = Spreadsheet.u + 1
  expr: Constraints[22] = Spreadsheet.u * (2 + 0.25 + 2)
  expr: Constraints[41] = Spreadsheet.u * (2 + 0.25 + 2)
  expr: Constraints[42] = Spreadsheet.u * (0.5 + 2 + 0.25)
  expr: Constraints[43] = Spreadsheet.u * 1.5
  expr: Constraints[47] = 13.5
  expr: Constraints[48] = Spreadsheet.u
  expr: Constraints[49] = Spreadsheet.u
  sketch-geometry (80):
    g0: Circle CenterX=9.525 CenterY=-24.7 CenterZ=0 NormalX=0 NormalY=0 NormalZ=1 AngleXU=0 Radius=6.75
    g1: Circle CenterX=28.575 CenterY=-24.7 CenterZ=0 NormalX=0 NormalY=0 NormalZ=1 AngleXU=0 Radius=6.75
    g2: LineSegment StartX=37.6 StartY=-16.175 StartZ=0 EndX=37.6 EndY=-33.225 EndZ=0
    g3: LineSegment StartX=39.1 StartY=-34.725 StartZ=0 EndX=56.15 EndY=-34.725 EndZ=0
    g4: LineSegment StartX=57.65 StartY=-33.225 StartZ=0 EndX=57.65 EndY=-16.175 EndZ=0
    g5: LineSegment StartX=56.15 StartY=-14.675 StartZ=0 EndX=39.1 EndY=-14.675 EndZ=0
    g6: GeomPoint X=47.625 Y=-24.7 Z=0
    g7: LineSegment StartX=61.4125 StartY=-16.175 StartZ=0 EndX=61.4125 EndY=-33.225 EndZ=0
    g8: LineSegment StartX=62.9125 StartY=-34.725 StartZ=0 EndX=137.113 EndY=-34.725 EndZ=0
    g9: LineSegment StartX=138.613 StartY=-33.225 StartZ=0 EndX=138.613 EndY=-16.175 EndZ=0
    g10: LineSegment StartX=137.113 StartY=-14.675 StartZ=0 EndX=62.9125 EndY=-14.675 EndZ=0
    g11: GeomPoint X=100.013 Y=-24.7 Z=0
    g12: LineSegment StartX=142.375 StartY=-16.175 StartZ=0 EndX=142.375 EndY=-33.225 EndZ=0
    g13: LineSegment StartX=143.875 StartY=-34.725 StartZ=0 EndX=218.075 EndY=-34.725 EndZ=0
    g14: LineSegment StartX=219.575 StartY=-33.225 StartZ=0 EndX=219.575 EndY=-16.175 EndZ=0
    g15: LineSegment StartX=218.075 StartY=-14.675 StartZ=0 EndX=143.875 EndY=-14.675 EndZ=0
    g16: GeomPoint X=180.975 Y=-24.7 Z=0
    g17: LineSegment StartX=223.338 StartY=-16.175 StartZ=0 EndX=223.338 EndY=-33.225 EndZ=0
    g18: LineSegment StartX=224.838 StartY=-34.725 StartZ=0 EndX=299.037 EndY=-34.725 EndZ=0
    g19: LineSegment StartX=300.537 StartY=-33.225 StartZ=0 EndX=300.537 EndY=-16.175 EndZ=0
    g20: LineSegment StartX=299.037 StartY=-14.675 StartZ=0 EndX=224.838 EndY=-14.675 EndZ=0
    g21: GeomPoint X=261.938 Y=-24.7 Z=0
    g22: LineSegment StartX=304.3 StartY=-16.175 StartZ=0 EndX=304.3 EndY=-33.225 EndZ=0
    g23: LineSegment StartX=305.8 StartY=-34.725 StartZ=0 EndX=322.85 EndY=-34.725 EndZ=0
    g24: LineSegment StartX=324.35 StartY=-33.225 StartZ=0 EndX=324.35 EndY=-16.175 EndZ=0
    g25: LineSegment StartX=322.85 StartY=-14.675 StartZ=0 EndX=305.8 EndY=-14.675 EndZ=0
    g26: GeomPoint X=314.325 Y=-24.7 Z=0
    g27: LineSegment StartX=332.875 StartY=-16.175 StartZ=0 EndX=332.875 EndY=-33.225 EndZ=0
    g28: LineSegment StartX=334.375 StartY=-34.725 StartZ=0 EndX=351.425 EndY=-34.725 EndZ=0
    g29: LineSegment StartX=352.925 StartY=-33.225 StartZ=0 EndX=352.925 EndY=-16.175 EndZ=0
    g30: LineSegment StartX=351.425 StartY=-14.675 StartZ=0 EndX=334.375 EndY=-14.675 EndZ=0
    g31: GeomPoint X=342.9 Y=-24.7 Z=0
    g32: ArcOfCircle CenterX=39.1 CenterY=-16.175 CenterZ=0 NormalX=0 NormalY=0 NormalZ=1 AngleXU=0 Radius=1.5 StartAngle=1.5708 EndAngle=3.14159
    g33: GeomPoint X=37.6 Y=-14.675 Z=0
    g34: ArcOfCircle CenterX=39.1 CenterY=-33.225 CenterZ=0 NormalX=0 NormalY=0 NormalZ=1 AngleXU=0 Radius=1.5 StartAngle=3.14159 EndAngle=4.71239
    g35: GeomPoint X=37.6 Y=-34.725 Z=0
    g36: ArcOfCircle CenterX=56.15 CenterY=-33.225 CenterZ=0 NormalX=0 NormalY=0 NormalZ=1 AngleXU=0 Radius=1.5 StartAngle=4.71239 EndAngle=6.28319
    g37: GeomPoint X=57.65 Y=-34.725 Z=0
    g38: ArcOfCircle CenterX=56.15 CenterY=-16.175 CenterZ=0 NormalX=0 NormalY=0 NormalZ=1 AngleXU=0 Radius=1.5 StartAngle=-9e-16 EndAngle=1.5708
    g39: GeomPoint X=57.65 Y=-14.675 Z=0
    g40: ArcOfCircle CenterX=62.9125 CenterY=-16.175 CenterZ=0 NormalX=0 NormalY=0 NormalZ=1 AngleXU=0 Radius=1.5 StartAngle=1.5708 EndAngle=3.14159
    g41: GeomPoint X=61.4125 Y=-14.675 Z=0
    g42: ArcOfCircle CenterX=62.9125 CenterY=-33.225 CenterZ=0 NormalX=0 NormalY=0 NormalZ=1 AngleXU=0 Radius=1.5 StartAngle=3.14159 EndAngle=4.71239
    g43: GeomPoint X=61.4125 Y=-34.725 Z=0
    g44: ArcOfCircle CenterX=137.113 CenterY=-33.225 CenterZ=0 NormalX=0 NormalY=0 NormalZ=1 AngleXU=0 Radius=1.5 StartAngle=4.71239 EndAngle=6.28319
    g45: GeomPoint X=138.613 Y=-34.725 Z=0
    g46: ArcOfCircle CenterX=137.113 CenterY=-16.175 CenterZ=0 NormalX=0 NormalY=0 NormalZ=1 AngleXU=0 Radius=1.5 StartAngle=-9e-16 EndAngle=1.5708
    g47: GeomPoint X=138.613 Y=-14.675 Z=0
    g48: ArcOfCircle CenterX=143.875 CenterY=-16.175 CenterZ=0 NormalX=0 NormalY=0 NormalZ=1 AngleXU=0 Radius=1.5 StartAngle=1.5708 EndAngle=3.14159
    g49: GeomPoint X=142.375 Y=-14.675 Z=0
    g50: ArcOfCircle CenterX=143.875 CenterY=-33.225 CenterZ=0 NormalX=0 NormalY=0 NormalZ=1 AngleXU=0 Radius=1.5 StartAngle=3.14159 EndAngle=4.71239
    g51: GeomPoint X=142.375 Y=-34.725 Z=0
    g52: ArcOfCircle CenterX=218.075 CenterY=-16.175 CenterZ=0 NormalX=0 NormalY=0 NormalZ=1 AngleXU=0 Radius=1.5 StartAngle=-9e-16 EndAngle=1.5708
    g53: GeomPoint X=219.575 Y=-14.675 Z=0
    g54: ArcOfCircle CenterX=218.075 CenterY=-33.225 CenterZ=0 NormalX=0 NormalY=0 NormalZ=1 AngleXU=0 Radius=1.5 StartAngle=4.71239 EndAngle=6.28319
    g55: GeomPoint X=219.575 Y=-34.725 Z=0
    g56: ArcOfCircle CenterX=224.838 CenterY=-33.225 CenterZ=0 NormalX=0 NormalY=0 NormalZ=1 AngleXU=0 Radius=1.5 StartAngle=3.14159 EndAngle=4.71239
    g57: GeomPoint X=223.338 Y=-34.725 Z=0
    g58: ArcOfCircle CenterX=224.838 CenterY=-16.175 CenterZ=0 NormalX=0 NormalY=0 NormalZ=1 AngleXU=0 Radius=1.5 StartAngle=1.5708 EndAngle=3.14159
    g59: GeomPoint X=223.338 Y=-14.675 Z=0
    g60: ArcOfCircle CenterX=299.037 CenterY=-16.175 CenterZ=0 NormalX=0 NormalY=0 NormalZ=1 AngleXU=0 Radius=1.5 StartAngle=0 EndAngle=1.5708
    g61: GeomPoint X=300.538 Y=-14.675 Z=0
    g62: ArcOfCircle CenterX=299.037 CenterY=-33.225 CenterZ=0 NormalX=0 NormalY=0 NormalZ=1 AngleXU=0 Radius=1.5 StartAngle=4.71239 EndAngle=6.28319
    g63: GeomPoint X=300.537 Y=-34.725 Z=0
    g64: ArcOfCircle CenterX=305.8 CenterY=-33.225 CenterZ=0 NormalX=0 NormalY=0 NormalZ=1 AngleXU=0 Radius=1.5 StartAngle=3.14159 EndAngle=4.71239
    g65: GeomPoint X=304.3 Y=-34.725 Z=0
    g66: ArcOfCircle CenterX=305.8 CenterY=-16.175 CenterZ=0 NormalX=0 NormalY=0 NormalZ=1 AngleXU=0 Radius=1.5 StartAngle=1.5708 EndAngle=3.14159
    g67: GeomPoint X=304.3 Y=-14.675 Z=0
    g68: ArcOfCircle CenterX=322.85 CenterY=-16.175 CenterZ=0 NormalX=0 NormalY=0 NormalZ=1 AngleXU=0 Radius=1.5 StartAngle=-9e-16 EndAngle=1.5708
    g69: GeomPoint X=324.35 Y=-14.675 Z=0
    g70: ArcOfCircle CenterX=322.85 CenterY=-33.225 CenterZ=0 NormalX=0 NormalY=0 NormalZ=1 AngleXU=0 Radius=1.5 StartAngle=4.71239 EndAngle=6.28319
    g71: GeomPoint X=324.35 Y=-34.725 Z=0
    g72: ArcOfCircle CenterX=334.375 CenterY=-33.225 CenterZ=0 NormalX=0 NormalY=0 NormalZ=1 AngleXU=0 Radius=1.5 StartAngle=3.14159 EndAngle=4.71239
    g73: GeomPoint X=332.875 Y=-34.725 Z=0
    g74: ArcOfCircle CenterX=334.375 CenterY=-16.175 CenterZ=0 NormalX=0 NormalY=0 NormalZ=1 AngleXU=0 Radius=1.5 StartAngle=1.5708 EndAngle=3.14159
    g75: GeomPoint X=332.875 Y=-14.675 Z=0
    g76: ArcOfCircle CenterX=351.425 CenterY=-16.175 CenterZ=0 NormalX=0 NormalY=0 NormalZ=1 AngleXU=0 Radius=1.5 StartAngle=2.7e-15 EndAngle=1.5708
    g77: GeomPoint X=352.925 Y=-14.675 Z=0
    g78: ArcOfCircle CenterX=351.425 CenterY=-33.225 CenterZ=0 NormalX=0 NormalY=0 NormalZ=1 AngleXU=0 Radius=1.5 StartAngle=4.71239 EndAngle=6.28319
    g79: GeomPoint X=352.925 Y=-34.725 Z=0
  constraints (180):
    c: Horizontal(g3)
    c: Horizontal(g5)
    c: Vertical(g2)
    c: Vertical(g4)
    c: Symmetric(g37,g33,g6)
    c: Horizontal(g8)
    c: Horizontal(g10)
    c: Vertical(g7)
    c: Vertical(g9)
    c: Symmetric(g45,g41,g11)
    c: DistanceY(g6,g-1) = 24.7
    c: DistanceX(g-1,g6) = 47.625
    c: DistanceY(g35,g33) = 20.05
    c: DistanceX(g41,g47) = 77.2
    c: Horizontal(g6,g11)
    c: DistanceX(g6,g11) = 52.3875
    c: Horizontal(g13)
    c: Horizontal(g15)
    c: Vertical(g12)
    c: Vertical(g14)
    c: Symmetric(g55,g49,g16)
    c: Horizontal(g11,g16)
    c: DistanceX(g11,g16) = 80.9625
    c: Horizontal(g18)
    c: Horizontal(g20)
    c: Vertical(g17)
    c: Vertical(g19)
    c: Symmetric(g63,g59,g21)
    c: Horizontal(g23)
    c: Horizontal(g25)
    c: Vertical(g22)
    c: Vertical(g24)
    c: Symmetric(g71,g67,g26)
    c: Horizontal(g28)
    c: Horizontal(g30)
    c: Vertical(g27)
    c: Vertical(g29)
    c: Symmetric(g79,g75,g31)
    c: Horizontal(g16,g21)
    c: Horizontal(g21,g26)
    c: Horizontal(g26,g31)
    c: DistanceX(g16,g21) = 80.9625
    c: DistanceX(g21,g26) = 52.3875
    c: DistanceX(g26,g31) = 28.575
    c: Equal(g0,g1)
    c: Horizontal(g1,g6)
    c: Horizontal(g0,g6)
    c: Diameter(g1) = 13.5
    c: DistanceX(g1,g6) = 19.05
    c: DistanceX(g0,g1) = 19.05
    c: PointOnObject(g33,g2)
    c: PointOnObject(g33,g5)
    c: Tangent(g2,g32) = -1.5708
    c: Tangent(g5,g32) = -1.5708
    c: PointOnObject(g35,g2)
    c: PointOnObject(g35,g3)
    c: Tangent(g2,g34) = -1.5708
    c: Tangent(g3,g34) = -1.5708
    c: PointOnObject(g37,g3)
    c: PointOnObject(g37,g4)
    c: Tangent(g3,g36) = -1.5708
    c: Tangent(g4,g36) = -1.5708
    c: PointOnObject(g39,g4)
    c: PointOnObject(g39,g5)
    c: Tangent(g4,g38) = -1.5708
    c: Tangent(g5,g38) = -1.5708
    c: PointOnObject(g41,g7)
    c: PointOnObject(g41,g10)
    c: Tangent(g7,g40) = -1.5708
    c: Tangent(g10,g40) = -1.5708
    c: PointOnObject(g43,g7)
    c: PointOnObject(g43,g8)
    c: Tangent(g7,g42) = -1.5708
    c: Tangent(g8,g42) = -1.5708
    c: PointOnObject(g45,g8)
    c: PointOnObject(g45,g9)
    c: Tangent(g8,g44) = -1.5708
    c: Tangent(g9,g44) = -1.5708
    c: PointOnObject(g47,g9)
    c: PointOnObject(g47,g10)
    c: Tangent(g9,g46) = -1.5708
    c: Tangent(g10,g46) = -1.5708
    c: PointOnObject(g49,g12)
    c: PointOnObject(g49,g15)
    c: Tangent(g12,g48) = -1.5708
    c: Tangent(g15,g48) = -1.5708
    c: PointOnObject(g51,g12)
    c: PointOnObject(g51,g13)
    c: Tangent(g12,g50) = -1.5708
    c: Tangent(g13,g50) = -1.5708
    c: PointOnObject(g53,g14)
    c: PointOnObject(g53,g15)
    c: Tangent(g14,g52) = -1.5708
    c: Tangent(g15,g52) = -1.5708
    c: PointOnObject(g55,g13)
    c: PointOnObject(g55,g14)
    c: Tangent(g13,g54) = -1.5708
    c: Tangent(g14,g54) = -1.5708
    c: PointOnObject(g57,g17)
    c: PointOnObject(g57,g18)
    c: Tangent(g17,g56) = -1.5708
    c: Tangent(g18,g56) = -1.5708
    c: PointOnObject(g59,g17)
    c: PointOnObject(g59,g20)
    c: Tangent(g17,g58) = -1.5708
    c: Tangent(g20,g58) = -1.5708
    c: PointOnObject(g61,g19)
    c: PointOnObject(g61,g20)
    c: Tangent(g19,g60) = -1.5708
    c: Tangent(g20,g60) = -1.5708
    c: PointOnObject(g63,g18)
    c: PointOnObject(g63,g19)
    c: Tangent(g18,g62) = -1.5708
    c: Tangent(g19,g62) = -1.5708
    c: PointOnObject(g65,g22)
    c: PointOnObject(g65,g23)
    c: Tangent(g22,g64) = -1.5708
    c: Tangent(g23,g64) = -1.5708
    c: PointOnObject(g67,g22)
    c: PointOnObject(g67,g25)
    c: Tangent(g22,g66) = -1.5708
    c: Tangent(g25,g66) = -1.5708
    c: PointOnObject(g69,g24)
    c: PointOnObject(g69,g25)
    c: Tangent(g24,g68) = -1.5708
    c: Tangent(g25,g68) = -1.5708
    c: PointOnObject(g71,g23)
    c: PointOnObject(g71,g24)
    c: Tangent(g23,g70) = -1.5708
    c: Tangent(g24,g70) = -1.5708
    c: PointOnObject(g73,g27)
    c: PointOnObject(g73,g28)
    c: Tangent(g27,g72) = -1.5708
    c: Tangent(g28,g72) = -1.5708
    c: PointOnObject(g75,g27)
    c: PointOnObject(g75,g30)
    c: Tangent(g27,g74) = -1.5708
    c: Tangent(g30,g74) = -1.5708
    c: PointOnObject(g77,g29)
    c: PointOnObject(g77,g30)
    c: Tangent(g29,g76) = -1.5708
    c: Tangent(g30,g76) = -1.5708
    c: Equal(g34,g36)
    c: Equal(g36,g38)
    c: Equal(g38,g32)
    c: Equal(g40,g32)
    c: Equal(g42,g44)
    c: Equal(g44,g46)
    c: Equal(g46,g40)
    c: Equal(g48,g40)
    c: Equal(g50,g54)
    c: Equal(g54,g52)
    c: Equal(g48,g52)
    c: Equal(g56,g62)
    c: Equal(g62,g60)
    c: Equal(g60,g58)
    c: Equal(g58,g48)
    c: Equal(g64,g70)
    c: Equal(g70,g68)
    c: Equal(g68,g66)
    c: PointOnObject(g79,g28)
    c: PointOnObject(g79,g29)
    c: Tangent(g28,g78) = -1.5708
    c: Tangent(g29,g78) = -1.5708
    c: Equal(g72,g78)
    c: Equal(g78,g76)
    c: DistanceX(g33,g39) = 20.05
    c: Radius(g32) = 1.5
    c: DistanceY(g43,g41) = 20.05
    c: DistanceY(g51,g49) = 20.05
    c: DistanceX(g49,g53) = 77.2
    c: DistanceX(g59,g61) = 77.2
    c: DistanceY(g57,g59) = 20.05
    c: DistanceY(g65,g67) = 20.05
    c: DistanceY(g73,g75) = 20.05
    c: DistanceX(g67,g69) = 20.05
    c: DistanceX(g75,g77) = 20.05
    c: Equal(g66,g58)
    c: Equal(g74,g66)
    c: Equal(g76,g74)
FEATURE [PartDesign::Pocket] Pocket063  label="f row002"
  BaseFeature = -> Pad016
  Direction = (0,0,-1)
  Length = 5
  Length2 = 5
  Profile = -> Sketch081
  ReferenceAxis = -> Sketch081 [N_Axis]
  Type = 0
FEATURE [Sketcher::SketchObject] Sketch082
  AttachmentOffset = pos=(0,0,5) rot=(0,0,1;0rad)
  FullyConstrained = true
  MapMode = 5
  Placement = pos=(0,0,5) rot=(0,0,1;0rad)
  Support = -> [XY_Plane212]
  expr: Constraints[10] = Spreadsheet.u * 3 + 1
  expr: Constraints[12] = Spreadsheet.u
  expr: Constraints[15] = Spreadsheet.u
  expr: Constraints[2] = Spreadsheet.u * 15 + 1
  expr: Constraints[3] = Spreadsheet.u * 2 - 0.5
  expr: Constraints[4] = Spreadsheet.PCB_width - Spreadsheet.u * 5.25 - 0.5
  expr: Constraints[53] = Spreadsheet.key_fillet
  expr: Constraints[6] = Spreadsheet.u * 5 + 1
  expr: Constraints[8] = Spreadsheet.u * (1.25 * 3 + 6.25 + 1 * 3) + 1
  sketch-geometry (25):
    g0: LineSegment StartX=39.1 StartY=-38.4875 StartZ=0 EndX=322.85 EndY=-38.4875 EndZ=0
    g1: GeomPoint X=180.975 Y=-38.4875 Z=0
    g2: LineSegment StartX=37.6 StartY=-39.9875 StartZ=0 EndX=37.6 EndY=-133.238 EndZ=0
    g3: LineSegment StartX=39.1 StartY=-134.737 StartZ=0 EndX=284.75 EndY=-134.737 EndZ=0
    g4: LineSegment StartX=324.35 StartY=-39.9875 StartZ=0 EndX=324.35 EndY=-95.1375 EndZ=0
    g5: LineSegment StartX=286.25 StartY=-133.237 StartZ=0 EndX=286.25 EndY=-117.188 EndZ=0
    g6: LineSegment StartX=322.85 StartY=-96.6375 StartZ=0 EndX=306.8 EndY=-96.6375 EndZ=0
    g7: LineSegment StartX=287.75 StartY=-115.688 StartZ=0 EndX=303.8 EndY=-115.688 EndZ=0
    g8: LineSegment StartX=305.3 StartY=-98.1375 StartZ=0 EndX=305.3 EndY=-114.188 EndZ=0
    g9: ArcOfCircle CenterX=39.1 CenterY=-39.9875 CenterZ=0 NormalX=0 NormalY=0 NormalZ=1 AngleXU=0 Radius=1.5 StartAngle=1.5708 EndAngle=3.14159
    g10: GeomPoint X=37.6 Y=-38.4875 Z=0
    g11: ArcOfCircle CenterX=39.1 CenterY=-133.238 CenterZ=0 NormalX=0 NormalY=0 NormalZ=1 AngleXU=0 Radius=1.5 StartAngle=3.14159 EndAngle=4.71239
    g12: GeomPoint X=37.6 Y=-134.738 Z=0
    g13: ArcOfCircle CenterX=284.75 CenterY=-133.237 CenterZ=0 NormalX=0 NormalY=0 NormalZ=1 AngleXU=0 Radius=1.5 StartAngle=4.71239 EndAngle=6.28319
    g14: GeomPoint X=286.25 Y=-134.738 Z=0
    g15: ArcOfCircle CenterX=287.75 CenterY=-117.188 CenterZ=0 NormalX=0 NormalY=0 NormalZ=1 AngleXU=0 Radius=1.5 StartAngle=1.5708 EndAngle=3.14159
    g16: GeomPoint X=286.25 Y=-115.688 Z=0
    g17: ArcOfCircle CenterX=303.8 CenterY=-114.188 CenterZ=0 NormalX=0 NormalY=0 NormalZ=1 AngleXU=0 Radius=1.5 StartAngle=4.71239 EndAngle=6.28319
    g18: GeomPoint X=305.3 Y=-115.688 Z=0
    g19: ArcOfCircle CenterX=306.8 CenterY=-98.1375 CenterZ=0 NormalX=0 NormalY=0 NormalZ=1 AngleXU=0 Radius=1.5 StartAngle=1.5708 EndAngle=3.14159
    g20: GeomPoint X=305.3 Y=-96.6375 Z=0
    g21: ArcOfCircle CenterX=322.85 CenterY=-95.1375 CenterZ=0 NormalX=0 NormalY=0 NormalZ=1 AngleXU=0 Radius=1.5 StartAngle=4.71239 EndAngle=6.28319
    g22: GeomPoint X=324.35 Y=-96.6375 Z=0
    g23: ArcOfCircle CenterX=322.85 CenterY=-39.9875 CenterZ=0 NormalX=0 NormalY=0 NormalZ=1 AngleXU=0 Radius=1.5 StartAngle=9e-16 EndAngle=1.5708
    g24: GeomPoint X=324.35 Y=-38.4875 Z=0
  constraints (57):
    c: Horizontal(g0)
    c: Symmetric(g10,g24,g1)
    c: DistanceX(g10,g24) = 286.75
    c: DistanceX(g-1,g10) = 37.6
    c: DistanceY(g10,g-1) = 38.4875
    c: Vertical(g2)
    c: DistanceY(g12,g10) = 96.25
    c: Horizontal(g3)
    c: DistanceX(g12,g14) = 248.65
    c: Vertical(g4)
    c: DistanceY(g22,g24) = 58.15
    c: Vertical(g5)
    c: DistanceY(g14,g16) = 19.05
    c: Horizontal(g6)
    c: Horizontal(g7)
    c: DistanceX(g20,g22) = 19.05
    c: Vertical(g8)
    c: PointOnObject(g10,g0)
    c: PointOnObject(g10,g2)
    c: Tangent(g0,g9) = 1.5708
    c: Tangent(g2,g9) = -1.5708
    c: PointOnObject(g12,g2)
    c: PointOnObject(g12,g3)
    c: Tangent(g2,g11) = -1.5708
    c: Tangent(g3,g11) = -1.5708
    c: PointOnObject(g14,g3)
    c: PointOnObject(g14,g5)
    c: Tangent(g3,g13) = -1.5708
    c: Tangent(g5,g13) = -1.5708
    c: PointOnObject(g16,g5)
    c: PointOnObject(g16,g7)
    c: Tangent(g5,g15) = 1.5708
    c: Tangent(g7,g15) = 1.5708
    c: PointOnObject(g18,g7)
    c: PointOnObject(g18,g8)
    c: Tangent(g7,g17) = -1.5708
    c: Tangent(g8,g17) = 1.5708
    c: PointOnObject(g20,g6)
    c: PointOnObject(g20,g8)
    c: Tangent(g6,g19) = -1.5708
    c: Tangent(g8,g19) = -1.5708
    c: PointOnObject(g22,g4)
    c: PointOnObject(g22,g6)
    c: Tangent(g4,g21) = 1.5708
    c: Tangent(g6,g21) = 1.5708
    c: PointOnObject(g24,g0)
    c: PointOnObject(g24,g4)
    c: Tangent(g0,g23) = 1.5708
    c: Tangent(g4,g23) = 1.5708
    c: Equal(g17,g19)
    c: Equal(g19,g21)
    c: Equal(g23,g9)
    c: Equal(g11,g9)
    c: Radius(g9) = 1.5
    c: Equal(g23,g21)
    c: Equal(g15,g17)
    c: Equal(g15,g13)
FEATURE [PartDesign::Pocket] Pocket064  label="alpha002"
  BaseFeature = -> Pocket063
  Direction = (0,0,-1)
  Length = 5
  Length2 = 5
  Profile = -> Sketch082
  ReferenceAxis = -> Sketch082 [N_Axis]
  Type = 0
FEATURE [Sketcher::SketchObject] Sketch083
  AttachmentOffset = pos=(0,0,5) rot=(0,0,1;0rad)
  FullyConstrained = true
  MapMode = 5
  Placement = pos=(0,0,5) rot=(0,0,1;0rad)
  Support = -> [XY_Plane212]
  expr: Constraints[28] = Spreadsheet.key_fillet
  expr: Constraints[5] = Spreadsheet.u * 4 + 1
  expr: Constraints[6] = Spreadsheet.u + 1
  expr: Constraints[7] = Spreadsheet.u * (0.5 + 17 + 0.5)
  expr: Constraints[8] = Spreadsheet.PCB_width - Spreadsheet.u * (1 + 0.25 + 2)
  sketch-geometry (13):
    g0: LineSegment StartX=332.875 StartY=-39.9875 StartZ=0 EndX=332.875 EndY=-114.187 EndZ=0
    g1: LineSegment StartX=334.375 StartY=-115.687 StartZ=0 EndX=351.425 EndY=-115.687 EndZ=0
    g2: LineSegment StartX=352.925 StartY=-114.187 StartZ=0 EndX=352.925 EndY=-39.9875 EndZ=0
    g3: LineSegment StartX=351.425 StartY=-38.4875 StartZ=0 EndX=334.375 EndY=-38.4875 EndZ=0
    g4: GeomPoint X=342.9 Y=-77.0875 Z=0
    g5: ArcOfCircle CenterX=334.375 CenterY=-39.9875 CenterZ=0 NormalX=0 NormalY=0 NormalZ=1 AngleXU=0 Radius=1.5 StartAngle=1.5708 EndAngle=3.14159
    g6: GeomPoint X=332.875 Y=-38.4875 Z=0
    g7: ArcOfCircle CenterX=334.375 CenterY=-114.187 CenterZ=0 NormalX=0 NormalY=0 NormalZ=1 AngleXU=0 Radius=1.5 StartAngle=3.14159 EndAngle=4.71239
    g8: GeomPoint X=332.875 Y=-115.687 Z=0
    g9: ArcOfCircle CenterX=351.425 CenterY=-114.187 CenterZ=0 NormalX=0 NormalY=0 NormalZ=1 AngleXU=0 Radius=1.5 StartAngle=4.71239 EndAngle=6.28319
    g10: GeomPoint X=352.925 Y=-115.688 Z=0
    g11: ArcOfCircle CenterX=351.425 CenterY=-39.9875 CenterZ=0 NormalX=0 NormalY=0 NormalZ=1 AngleXU=0 Radius=1.5 StartAngle=2e-16 EndAngle=1.5708
    g12: GeomPoint X=352.925 Y=-38.4875 Z=0
  constraints (29):
    c: Horizontal(g1)
    c: Horizontal(g3)
    c: Vertical(g0)
    c: Vertical(g2)
    c: Symmetric(g10,g6,g4)
    c: DistanceY(g10,g12) = 77.2
    c: DistanceX(g6,g12) = 20.05
    c: DistanceX(g-1,g4) = 342.9
    c: DistanceY(g4,g-1) = 77.0875
    c: PointOnObject(g6,g0)
    c: PointOnObject(g6,g3)
    c: Tangent(g0,g5) = -1.5708
    c: Tangent(g3,g5) = -1.5708
    c: PointOnObject(g8,g0)
    c: PointOnObject(g8,g1)
    c: Tangent(g0,g7) = -1.5708
    c: Tangent(g1,g7) = -1.5708
    c: PointOnObject(g10,g1)
    c: PointOnObject(g10,g2)
    c: Tangent(g1,g9) = -1.5708
    c: Tangent(g2,g9) = -1.5708
    c: PointOnObject(g12,g2)
    c: PointOnObject(g12,g3)
    c: Tangent(g2,g11) = -1.5708
    c: Tangent(g3,g11) = -1.5708
    c: Equal(g7,g9)
    c: Equal(g11,g9)
    c: Equal(g11,g5)
    c: Radius(g5) = 1.5
FEATURE [PartDesign::Pocket] Pocket065  label="right thiny002"
  BaseFeature = -> Pocket064
  Direction = (0,0,-1)
  Length = 5
  Length2 = 5
  Profile = -> Sketch083
  ReferenceAxis = -> Sketch083 [N_Axis]
  Type = 0
FEATURE [Sketcher::SketchObject] Sketch084
  AttachmentOffset = pos=(0,0,5) rot=(0,0,1;0rad)
  FullyConstrained = true
  MapMode = 5
  Placement = pos=(0,0,5) rot=(0,0,1;0rad)
  Support = -> [XY_Plane212]
  expr: Constraints[12] = Spreadsheet.u
  expr: Constraints[13] = Spreadsheet.u + 1
  expr: Constraints[1] = Spreadsheet.u * 3 + 1
  expr: Constraints[2] = Spreadsheet.u * (15 + 0.25) - 0.5
  expr: Constraints[3] = Spreadsheet.PCB_width + 0.5
  expr: Constraints[54] = Spreadsheet.key_fillet
  expr: Constraints[55] = Spreadsheet.u + 1
  expr: Constraints[6] = Spreadsheet.u + 1
  expr: Constraints[7] = Spreadsheet.u
  sketch-geometry (24):
    g0: LineSegment StartX=291.513 StartY=-139.5 StartZ=0 EndX=346.663 EndY=-139.5 EndZ=0
    g1: LineSegment StartX=290.013 StartY=-138 StartZ=0 EndX=290.013 EndY=-120.95 EndZ=0
    g2: LineSegment StartX=291.513 StartY=-119.45 StartZ=0 EndX=307.563 EndY=-119.45 EndZ=0
    g3: LineSegment StartX=309.063 StartY=-117.95 StartZ=0 EndX=309.063 EndY=-101.9 EndZ=0
    g4: LineSegment StartX=310.563 StartY=-100.4 StartZ=0 EndX=327.612 EndY=-100.4 EndZ=0
    g5: LineSegment StartX=329.112 StartY=-101.9 StartZ=0 EndX=329.112 EndY=-117.95 EndZ=0
    g6: LineSegment StartX=330.612 StartY=-119.45 StartZ=0 EndX=346.663 EndY=-119.45 EndZ=0
    g7: LineSegment StartX=348.163 StartY=-138 StartZ=0 EndX=348.163 EndY=-120.95 EndZ=0
    g8: ArcOfCircle CenterX=310.563 CenterY=-101.9 CenterZ=0 NormalX=0 NormalY=0 NormalZ=1 AngleXU=0 Radius=1.5 StartAngle=1.5708 EndAngle=3.14159
    g9: GeomPoint X=309.062 Y=-100.4 Z=0
    g10: ArcOfCircle CenterX=307.563 CenterY=-117.95 CenterZ=0 NormalX=0 NormalY=0 NormalZ=1 AngleXU=0 Radius=1.5 StartAngle=4.71239 EndAngle=6.28319
    g11: GeomPoint X=309.062 Y=-119.45 Z=0
    g12: ArcOfCircle CenterX=291.513 CenterY=-120.95 CenterZ=0 NormalX=0 NormalY=0 NormalZ=1 AngleXU=0 Radius=1.5 StartAngle=1.5708 EndAngle=3.14159
    g13: GeomPoint X=290.012 Y=-119.45 Z=0
    g14: ArcOfCircle CenterX=291.513 CenterY=-138 CenterZ=0 NormalX=0 NormalY=0 NormalZ=1 AngleXU=0 Radius=1.5 StartAngle=3.14159 EndAngle=4.71239
    g15: GeomPoint X=290.012 Y=-139.5 Z=0
    g16: ArcOfCircle CenterX=346.663 CenterY=-138 CenterZ=0 NormalX=0 NormalY=0 NormalZ=1 AngleXU=0 Radius=1.5 StartAngle=4.71239 EndAngle=6.28319
    g17: GeomPoint X=348.163 Y=-139.5 Z=0
    g18: ArcOfCircle CenterX=346.663 CenterY=-120.95 CenterZ=0 NormalX=0 NormalY=0 NormalZ=1 AngleXU=0 Radius=1.5 StartAngle=-2.7e-15 EndAngle=1.5708
    g19: GeomPoint X=348.162 Y=-119.45 Z=0
    g20: ArcOfCircle CenterX=330.612 CenterY=-117.95 CenterZ=0 NormalX=0 NormalY=0 NormalZ=1 AngleXU=0 Radius=1.5 StartAngle=3.14159 EndAngle=4.71239
    g21: GeomPoint X=329.112 Y=-119.45 Z=0
    g22: ArcOfCircle CenterX=327.612 CenterY=-101.9 CenterZ=0 NormalX=0 NormalY=0 NormalZ=1 AngleXU=0 Radius=1.5 StartAngle=2e-16 EndAngle=1.5708
    g23: GeomPoint X=329.112 Y=-100.4 Z=0
  constraints (56):
    c: Horizontal(g0)
    c: DistanceX(g15,g17) = 58.15
    c: DistanceX(g-1,g15) = 290.012
    c: DistanceY(g15,g-1) = 139.5
    c: Vertical(g1)
    c: Horizontal(g2)
    c: DistanceY(g15,g13) = 20.05
    c: DistanceX(g13,g11) = 19.05
    c: Vertical(g3)
    c: Horizontal(g4)
    c: Vertical(g5)
    c: Horizontal(g6)
    c: DistanceY(g11,g9) = 19.05
    c: DistanceX(g9,g23) = 20.05
    c: Vertical(g7)
    c: PointOnObject(g9,g3)
    c: PointOnObject(g9,g4)
    c: Tangent(g3,g8) = 1.5708
    c: Tangent(g4,g8) = 1.5708
    c: PointOnObject(g11,g2)
    c: PointOnObject(g11,g3)
    c: Tangent(g2,g10) = -1.5708
    c: Tangent(g3,g10) = -1.5708
    c: PointOnObject(g13,g1)
    c: PointOnObject(g13,g2)
    c: Tangent(g1,g12) = 1.5708
    c: Tangent(g2,g12) = 1.5708
    c: PointOnObject(g15,g0)
    c: PointOnObject(g15,g1)
    c: Tangent(g0,g14) = -1.5708
    c: Tangent(g1,g14) = 1.5708
    c: PointOnObject(g17,g0)
    c: PointOnObject(g17,g7)
    c: Tangent(g0,g16) = -1.5708
    c: Tangent(g7,g16) = -1.5708
    c: PointOnObject(g19,g6)
    c: PointOnObject(g19,g7)
    c: Tangent(g6,g18) = 1.5708
    c: Tangent(g7,g18) = -1.5708
    c: PointOnObject(g21,g5)
    c: PointOnObject(g21,g6)
    c: Tangent(g5,g20) = -1.5708
    c: Tangent(g6,g20) = -1.5708
    c: PointOnObject(g23,g4)
    c: PointOnObject(g23,g5)
    c: Tangent(g4,g22) = 1.5708
    c: Tangent(g5,g22) = 1.5708
    c: Equal(g22,g8)
    c: Equal(g20,g22)
    c: Equal(g18,g20)
    c: Equal(g16,g18)
    c: Equal(g14,g16)
    c: Equal(g12,g14)
    c: Equal(g10,g12)
    c: Radius(g8) = 1.5
    c: DistanceY(g17,g19) = 20.05
FEATURE [PartDesign::Pocket] Pocket066  label="arrow keys002"
  BaseFeature = -> Pocket065
  Direction = (0,0,-1)
  Length = 5
  Length2 = 5
  Profile = -> Sketch084
  ReferenceAxis = -> Sketch084 [N_Axis]
  Type = 0
FEATURE [Sketcher::SketchObject] Sketch085
  AttachmentOffset = pos=(0,0,5) rot=(0,0,1;0rad)
  FullyConstrained = true
  MapMode = 5
  Placement = pos=(0,0,5) rot=(0,0,1;0rad)
  Support = -> [XY_Plane212]
  expr: Constraints[10] = Spreadsheet.u * 0.5
  expr: Constraints[4] = Spreadsheet.u
  expr: Constraints[5] = Spreadsheet.u
  expr: Constraints[6] = Spreadsheet.u
  expr: Constraints[9] = Spreadsheet.PCB_width - Spreadsheet.u * 0.75
  sketch-geometry (4):
    g0: Circle CenterX=9.525 CenterY=-105.663 CenterZ=0 NormalX=0 NormalY=0 NormalZ=1 AngleXU=0 Radius=3.25
    g1: Circle CenterX=28.575 CenterY=-105.663 CenterZ=0 NormalX=0 NormalY=0 NormalZ=1 AngleXU=0 Radius=3.25
    g2: Circle CenterX=28.575 CenterY=-124.713 CenterZ=0 NormalX=0 NormalY=0 NormalZ=1 AngleXU=0 Radius=3.25
    g3: Circle CenterX=9.525 CenterY=-124.713 CenterZ=0 NormalX=0 NormalY=0 NormalZ=1 AngleXU=0 Radius=3.25
  constraints (12):
    c: Equal(g0,g1)
    c: Equal(g1,g2)
    c: Equal(g2,g3)
    c: Diameter(g0) = 6.5
    c: DistanceX(g0,g1) = 19.05
    c: DistanceX(g3,g2) = 19.05
    c: DistanceY(g2,g1) = 19.05
    c: Horizontal(g0,g1)
    c: Horizontal(g3,g2)
    c: DistanceY(g3,g-1) = 124.713
    c: DistanceX(g-1,g3) = 9.525
    c: Vertical(g1,g2)
FEATURE [PartDesign::Pocket] Pocket067  label="button hols001"
  BaseFeature = -> Pocket066
  Direction = (0,0,-1)
  Length = 5
  Length2 = 5
  Profile = -> Sketch085
  ReferenceAxis = -> Sketch085 [N_Axis]
  Type = 0
FEATURE [Sketcher::SketchObject] Sketch086
  AttachmentOffset = pos=(0,0,5) rot=(0,0,1;0rad)
  FullyConstrained = true
  MapMode = 5
  Placement = pos=(0,0,5) rot=(0,0,1;0rad)
  Support = -> [XY_Plane212]
  expr: Constraints[10] = Spreadsheet.screen_length + 1
  expr: Constraints[11] = Spreadsheet.PCB_width - Spreadsheet.u * 3.75 + Spreadsheet.screen_module_length / 2
  expr: Constraints[12] = Spreadsheet.u + Spreadsheet.screen_module_width / 2
  expr: Constraints[13] = 6.25 - 0.5
  expr: Constraints[14] = Spreadsheet.u
  expr: Constraints[9] = Spreadsheet.screen_width + 1
  sketch-geometry (6):
    g0: GeomPoint X=32.7 Y=-93.1625 Z=0
    g1: LineSegment StartX=7.2 StartY=-43.6925 StartZ=0 EndX=7.2 EndY=-87.4125 EndZ=0
    g2: LineSegment StartX=7.2 StartY=-87.4125 StartZ=0 EndX=30.9 EndY=-87.4125 EndZ=0
    g3: LineSegment StartX=30.9 StartY=-87.4125 StartZ=0 EndX=30.9 EndY=-43.6925 EndZ=0
    g4: LineSegment StartX=30.9 StartY=-43.6925 StartZ=0 EndX=7.2 EndY=-43.6925 EndZ=0
    g5: GeomPoint X=19.05 Y=-65.5525 Z=0
  constraints (15):
    c: Coincident(g1,g2)
    c: Coincident(g2,g3)
    c: Coincident(g3,g4)
    c: Coincident(g4,g1)
    c: Horizontal(g2)
    c: Horizontal(g4)
    c: Vertical(g1)
    c: Vertical(g3)
    c: Symmetric(g2,g1,g5)
    c: DistanceX(g4,g4) = 23.7
    c: DistanceY(g3,g3) = 43.72
    c: DistanceY(g0,g-1) = 93.1625
    c: DistanceX(g-1,g0) = 32.7
    c: DistanceY(g0,g2) = 5.75
    c: DistanceX(g-1,g5) = 19.05
FEATURE [PartDesign::Pocket] Pocket068
  AlongSketchNormal = false
  BaseFeature = -> Pocket067
  Direction = (0,0,-1)
  Length = 5
  Length2 = 5
  Profile = -> Sketch086
  ReferenceAxis = -> Sketch086 [N_Axis]
  Type = 0
  UseCustomVector = true
FEATURE [PartDesign::Body] Body016  label="clear top001"
  Group = -> [Sketch080,Pad016,Sketch081,Pocket063,Sketch082,Pocket064,Sketch083,Pocket065,Sketch084,Pocket066,Sketch085,Pocket067,Sketch086,Pocket068]
  Origin = -> Origin212
  Placement = pos=(0,0,6.2) rot=(0,0,1;0rad)
  Tip = -> Pocket068
FEATURE [App::Part] Part003  label="Top_case"
  Group = -> [Body005,Body006,Body009,Body010,Body011,Body012,Body016]
  Origin = -> Origin200
FEATURE [TechDraw::DrawViewPart] View014
  CoarseView = false
  Direction = (0,0,1)
  Focus = 100
  HardHidden = false
  IsoCount = 0
  IsoHidden = false
  IsoVisible = false
  LockPosition = false
  Perspective = false
  Rotation = 0
  ScaleType = 0
  SeamHidden = false
  SeamVisible = true
  SmoothHidden = false
  SmoothVisible = true
  Source = -> [Body016]
  X = 23.8093
  XDirection = (1,0,0)
  Y = 219.532
FEATURE [TechDraw::DrawPage] Page005  label="Clear_Top"
  KeepUpdated = true
  NextBalloonIndex = 1
  ProjectionType = 0
  Template = -> Template005
  Views = -> [View014]
FEATURE [TechDraw::DrawViewPart] View016
  CoarseView = false
  Direction = (0,0,1)
  Focus = 100
  HardHidden = false
  IsoCount = 0
  IsoHidden = false
  IsoVisible = false
  LockPosition = false
  Perspective = false
  Rotation = 0
  ScaleType = 0
  SeamHidden = false
  SeamVisible = true
  SmoothHidden = false
  SmoothVisible = true
  Source = -> [Body014]
  X = 387.956
  XDirection = (0,1,0)
  Y = 235.397
FEATURE [TechDraw::DrawViewPart] View017
  CoarseView = false
  Direction = (0,0,1)
  Focus = 100
  HardHidden = false
  IsoCount = 0
  IsoHidden = false
  IsoVisible = false
  LockPosition = false
  Perspective = false
  Rotation = 0
  ScaleType = 0
  SeamHidden = false
  SeamVisible = true
  SmoothHidden = false
  SmoothVisible = true
  Source = -> [Body005]
  X = 78.9616
  XDirection = (0,1,0)
  Y = 235.308
FEATURE [TechDraw::DrawViewPart] View018
  CoarseView = false
  Direction = (0,0,1)
  Focus = 100
  HardHidden = false
  IsoCount = 0
  IsoHidden = false
  IsoVisible = false
  LockPosition = false
  Perspective = false
  Rotation = 0
  ScaleType = 0
  SeamHidden = false
  SeamVisible = true
  SmoothHidden = false
  SmoothVisible = true
  Source = -> [Body015]
  X = 233.3
  XDirection = (0,1,0)
  Y = 235.263
FEATURE [TechDraw::DrawPage] Page003  label="Coloured_Top"
  KeepUpdated = true
  NextBalloonIndex = 1
  ProjectionType = 0
  Template = -> Template003
  Views = -> [View016,View017,View018]
FEATURE [Sketcher::SketchObject] Sketch087
  AttachmentOffset = pos=(0,0,2.9) rot=(0,0,1;0rad)
  FullyConstrained = false
  MapMode = 5
  Placement = pos=(0,0,2.9) rot=(0,0,1;0rad)
  Support = -> [XY_Plane204]
  expr: Constraints[0] = Spreadsheet.PCB_length / 2
  sketch-geometry (3):
    g0: GeomPoint X=176.213 Y=-33.7406 Z=0
    g1: Circle CenterX=5.0114 CenterY=-33.7406 CenterZ=0 NormalX=0 NormalY=0 NormalZ=1 AngleXU=0 Radius=4.05
    g2: Circle CenterX=347.414 CenterY=-33.7406 CenterZ=0 NormalX=0 NormalY=0 NormalZ=1 AngleXU=0 Radius=4.05
  constraints (6):
    c: DistanceX(g-1,g0) = 176.213
    c: Symmetric(g2,g1,g0)
    c: Equal(g2,g1)
    c: Diameter(g2) = 8.1
    c: Horizontal(g2,g1)
    c: DistanceX(g1,g2) = 342.402
FEATURE [PartDesign::Pocket] Pocket069
  BaseFeature = -> Fillet
  Direction = (0,0,1)
  Length = 1
  Length2 = 5
  Profile = -> Sketch087
  ReferenceAxis = -> Sketch087 [N_Axis]
  Type = 0
  UseCustomVector = true
FEATURE [PartDesign::Body] Body008  label="feet001"
  Group = -> [Sketch037,Pad008,Sketch039,Pocket029,Sketch041,Fillet,Sketch087,Pocket069]
  Origin = -> Origin204
  Placement = pos=(0,0,-15) rot=(0,0,1;0rad)
  Tip = -> Pocket069
FEATURE [App::Part] Part002  label="Bottom_case"
  Group = -> [Body003,Body007,Body008,Body015]
  Origin = -> Origin198
  Placement = pos=(0,0,-2) rot=(0,0,1;0rad)
FEATURE [App::Part] Part004  label="case"
  Group = -> [Part,Part001,Part002,Part003]
  Origin = -> Origin203
FEATURE [App::DocumentObjectGroup] Group  label="Case"
  Group = -> [Part004]
FEATURE [TechDraw::DrawViewPart] View019
  CoarseView = false
  Direction = (0,0,-1)
  Focus = 100
  HardHidden = false
  IsoCount = 0
  IsoHidden = false
  IsoVisible = false
  LockPosition = false
  Perspective = false
  Rotation = 0
  ScaleType = 0
  SeamHidden = false
  SeamVisible = true
  SmoothHidden = false
  SmoothVisible = true
  Source = -> [Body003]
  X = 184.494
  XDirection = (-1,0,0)
  Y = 219.278
FEATURE [TechDraw::DrawViewPart] View020
  CoarseView = false
  Direction = (0,0,-1)
  Focus = 100
  HardHidden = false
  IsoCount = 0
  IsoHidden = false
  IsoVisible = false
  LockPosition = false
  Perspective = false
  Rotation = 0
  ScaleType = 0
  SeamHidden = false
  SeamVisible = true
  SmoothHidden = false
  SmoothVisible = true
  Source = -> [Body007]
  X = 184.644
  XDirection = (-1,0,0)
  Y = 105.69
FEATURE [TechDraw::DrawViewPart] View021
  CoarseView = false
  Direction = (0,0,-1)
  Focus = 100
  HardHidden = false
  IsoCount = 0
  IsoHidden = false
  IsoVisible = false
  LockPosition = false
  Perspective = false
  Rotation = 0
  ScaleType = 0
  SeamHidden = false
  SeamVisible = true
  SmoothHidden = false
  SmoothVisible = true
  Source = -> [Body008]
  X = 184.649
  XDirection = (-1,0,0)
  Y = 42.6264
FEATURE [TechDraw::DrawPage] Page002  label="Bottom"
  KeepUpdated = true
  NextBalloonIndex = 1
  ProjectionType = 0
  Template = -> Template002
  Views = -> [View019,View020,View021]
